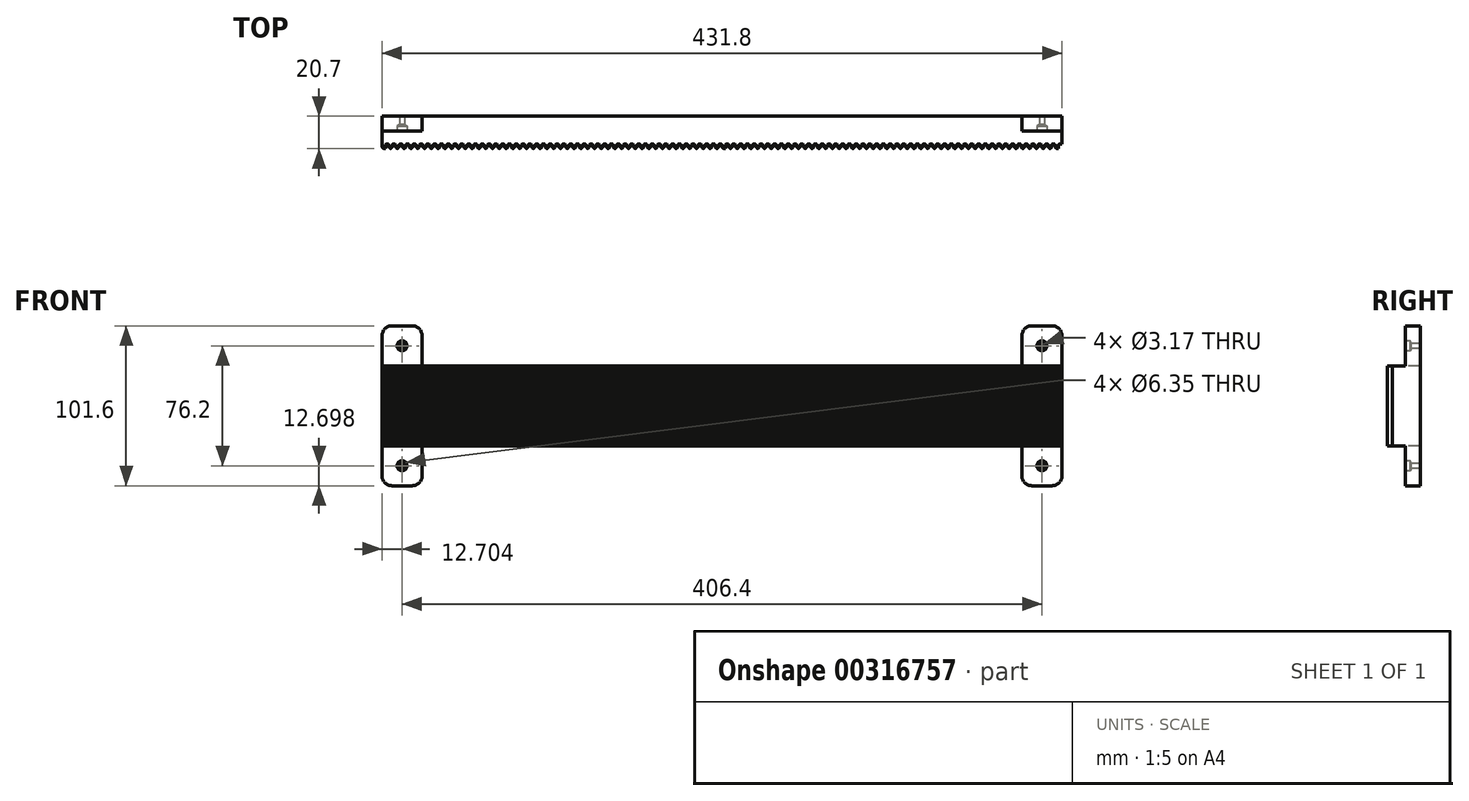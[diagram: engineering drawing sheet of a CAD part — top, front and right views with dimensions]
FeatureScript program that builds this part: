
annotation { "Feature Type Name" : "Feature", "Feature Type Description" : "" }
export const myFeature = defineFeature(function(context is Context, id is Id, definition is map)
    precondition{}
    {
        {
            var Q0;
            Q0=qCreatedBy(makeId("Front.planeOp"),FACE);
            var sketch = newSketch(context, id + "F0", { "sketchPlane" : qUnion([Q0])});
            skLineSegment(sketch, "E0.bottom", {"start": v(-210.38, -43.82) * mm, "end": v(221.42, -43.82) * mm});
            skLineSegment(sketch, "E0.top", {"start": v(-210.38, -94.62) * mm, "end": v(221.42, -94.62) * mm});
            skLineSegment(sketch, "E0.left", {"start": v(-210.38, -43.82) * mm, "end": v(-210.38, -94.62) * mm});
            skLineSegment(sketch, "E0.right", {"start": v(221.42, -43.82) * mm, "end": v(221.42, -94.62) * mm});
            skSolve(sketch);
        }
        {
            var Q0;
            Q0=makeQuery(id+"F0.imprint","IMPRINT",FACE,{"disambiguationData":[TD([[makeQuery(id+"F0.imprint","IMPRINT",EDGE,{"derivedFrom":sQuery(id+"F0.wireOp",EDGE,"E0.bottom")}),-1.0]])]});
            extrude(context, id + "F1", {"entities" : qUnion([Q0]), "depth" : 20.7 * mm});
        }
        {
            var Q0;
            Q0=makeQuery(id+"F1.opExtrude","SWEPT_FACE",FACE,{"disambiguationData":[OSD([sQuery(id+"F0.wireOp",EDGE,"E0.top")])]});
            var sketch = newSketch(context, id + "F2", { "sketchPlane" : qUnion([Q0])});
            skLineSegment(sketch, "E1.bottom", {"start": v(-210.38, 0) * mm, "end": v(-184.98, 0) * mm});
            skLineSegment(sketch, "E1.top", {"start": v(-210.38, 9.53) * mm, "end": v(-184.98, 9.53) * mm});
            skLineSegment(sketch, "E1.left", {"start": v(-210.38, 0) * mm, "end": v(-210.38, 9.53) * mm});
            skLineSegment(sketch, "E1.right", {"start": v(-184.98, 0) * mm, "end": v(-184.98, 9.53) * mm});
            skLineSegment(sketch, "E2.bottom", {"start": v(221.42, 0) * mm, "end": v(196.02, 0) * mm});
            skLineSegment(sketch, "E2.top", {"start": v(221.42, 9.52) * mm, "end": v(196.02, 9.52) * mm});
            skLineSegment(sketch, "E2.left", {"start": v(221.42, 0) * mm, "end": v(221.42, 9.52) * mm});
            skLineSegment(sketch, "E2.right", {"start": v(196.02, 0) * mm, "end": v(196.02, 9.52) * mm});
            skSolve(sketch);
        }
        {
            var Q0;
            Q0=makeQuery(id+"F1.opExtrude","SWEPT_FACE",FACE,{"disambiguationData":[OSD([sQuery(id+"F0.wireOp",EDGE,"E0.bottom")])]});
            var sketch = newSketch(context, id + "F3", { "sketchPlane" : qUnion([Q0])});
            skLineSegment(sketch, "E3.bottom", {"start": v(-210.38, 0) * mm, "end": v(-184.98, 0) * mm});
            skLineSegment(sketch, "E3.top", {"start": v(-210.38, -9.52) * mm, "end": v(-184.98, -9.52) * mm});
            skLineSegment(sketch, "E3.left", {"start": v(-210.38, 0) * mm, "end": v(-210.38, -9.52) * mm});
            skLineSegment(sketch, "E3.right", {"start": v(-184.98, 0) * mm, "end": v(-184.98, -9.52) * mm});
            skLineSegment(sketch, "E4.bottom", {"start": v(221.42, 0) * mm, "end": v(196.02, 0) * mm});
            skLineSegment(sketch, "E4.top", {"start": v(221.42, -9.53) * mm, "end": v(196.02, -9.53) * mm});
            skLineSegment(sketch, "E4.left", {"start": v(221.42, 0) * mm, "end": v(221.42, -9.53) * mm});
            skLineSegment(sketch, "E4.right", {"start": v(196.02, 0) * mm, "end": v(196.02, -9.53) * mm});
            skSolve(sketch);
        }
        {
            var Q0;
            Q0=makeQuery(id+"F2.imprint","IMPRINT",FACE,{"disambiguationData":[TD([[makeQuery(id+"F2.imprint","IMPRINT",EDGE,{"derivedFrom":sQuery(id+"F2.wireOp",EDGE,"E1.bottom")}),1.0]])]});
            var Q1;
            Q1=makeQuery(id+"F2.imprint","IMPRINT",FACE,{"disambiguationData":[TD([[makeQuery(id+"F2.imprint","IMPRINT",EDGE,{"derivedFrom":sQuery(id+"F2.wireOp",EDGE,"E2.bottom")}),1.0]])]});
            extrude(context, id + "F4", {"entities" : qUnion([Q0, Q1]), "operationType" : NewBodyOperationType.ADD, "depth" : 25.4 * mm});
        }
        {
            var Q0;
            Q0=makeQuery(id+"F3.imprint","IMPRINT",FACE,{"disambiguationData":[TD([[makeQuery(id+"F3.imprint","IMPRINT",EDGE,{"derivedFrom":sQuery(id+"F3.wireOp",EDGE,"E3.bottom")}),-1.0]])]});
            var Q1;
            Q1=makeQuery(id+"F3.imprint","IMPRINT",FACE,{"disambiguationData":[TD([[makeQuery(id+"F3.imprint","IMPRINT",EDGE,{"derivedFrom":sQuery(id+"F3.wireOp",EDGE,"E4.bottom")}),-1.0]])]});
            extrude(context, id + "F5", {"entities" : qUnion([Q0, Q1]), "operationType" : NewBodyOperationType.ADD, "depth" : 25.4 * mm});
        }
        {
            var Q0;
            Q0=makeQuery(id+"F5.opExtrude","CAP_EDGE",EDGE,{"disambiguationData":[OSD([sQuery(id+"F3.wireOp",EDGE,"E3.left")])],"isStart":false});
            var Q1;
            Q1=makeQuery(id+"F5.opExtrude","CAP_EDGE",EDGE,{"disambiguationData":[OSD([sQuery(id+"F3.wireOp",EDGE,"E3.right")])],"isStart":false});
            var Q2;
            Q2=makeQuery(id+"F5.opExtrude","CAP_EDGE",EDGE,{"disambiguationData":[OSD([sQuery(id+"F3.wireOp",EDGE,"E4.left")])],"isStart":false});
            var Q3;
            Q3=makeQuery(id+"F5.opExtrude","CAP_EDGE",EDGE,{"disambiguationData":[OSD([sQuery(id+"F3.wireOp",EDGE,"E4.right")])],"isStart":false});
            var Q4;
            Q4=makeQuery(id+"F4.opExtrude","CAP_EDGE",EDGE,{"disambiguationData":[OSD([sQuery(id+"F2.wireOp",EDGE,"E2.left")])],"isStart":false});
            var Q5;
            Q5=makeQuery(id+"F4.opExtrude","CAP_EDGE",EDGE,{"disambiguationData":[OSD([sQuery(id+"F2.wireOp",EDGE,"E2.right")])],"isStart":false});
            var Q6;
            Q6=makeQuery(id+"F4.opExtrude","CAP_EDGE",EDGE,{"disambiguationData":[OSD([sQuery(id+"F2.wireOp",EDGE,"E1.left")])],"isStart":false});
            var Q7;
            Q7=makeQuery(id+"F4.opExtrude","CAP_EDGE",EDGE,{"disambiguationData":[OSD([sQuery(id+"F2.wireOp",EDGE,"E1.right")])],"isStart":false});
            fillet(context, id + "F6", {"entities" : qUnion([Q0, Q1, Q2, Q3, Q4, Q5, Q6, Q7]), "radius" : 6.35 * mm, "tangentPropagation" : true, "allowEdgeOverflow" : false});
        }
        {
            var Q0;
            Q0=makeQuery(id+"F4.opExtrude","SWEPT_FACE",FACE,{"disambiguationData":[OSD([sQuery(id+"F2.wireOp",EDGE,"E1.top")])]});
            var sketch = newSketch(context, id + "F7", { "sketchPlane" : qUnion([Q0])});
            skPoint(sketch, "E5", {"position": v(-197.68, -107.32) * mm});
            skPoint(sketch, "E5.positionSnap0", {"position": v(-197.68, -94.62) * mm});
            skPoint(sketch, "E6", {"position": v(-197.68, -31.12) * mm});
            skSolve(sketch);
        }
        {
            var Q0;
            Q0=sQuery(id+"F7.wireOp",VERTEX,"E6");
            var Q1;
            Q1=sQuery(id+"F7.wireOp",VERTEX,"E5");
            var Q2;
            Q2=makeQuery(id+"F1.opExtrude","SWEPT_BODY",BODY,{"disambiguationData":[OSD([sQuery(id+"F0.wireOp",EDGE,"E0.bottom"),sQuery(id+"F0.wireOp",EDGE,"E0.top"),sQuery(id+"F0.wireOp",EDGE,"E0.left"),sQuery(id+"F0.wireOp",EDGE,"E0.right")])]});
            hole(context, id + "F8", {"style" : HoleStyle.SIMPLE, "endStyle" : HoleEndStyle.THROUGH, "holeDiameter" : 3.17 * mm, "tappedDepth" : 12.7 * mm, "tapClearance" : 3, "locations" : qUnion([Q0, Q1]), "scope" : qUnion([Q2])});
        }
        {
            var Q0;
            Q0=sQuery(id+"F7.wireOp",VERTEX,"E6");
            var Q1;
            Q1=sQuery(id+"F7.wireOp",VERTEX,"E5");
            var Q2;
            Q2=makeQuery(id+"F1.opExtrude","SWEPT_BODY",BODY,{"disambiguationData":[OSD([sQuery(id+"F0.wireOp",EDGE,"E0.bottom"),sQuery(id+"F0.wireOp",EDGE,"E0.top"),sQuery(id+"F0.wireOp",EDGE,"E0.left"),sQuery(id+"F0.wireOp",EDGE,"E0.right")])]});
            hole(context, id + "F9", {"style" : HoleStyle.SIMPLE, "endStyle" : HoleEndStyle.BLIND, "holeDiameter" : 6.35 * mm, "holeDepth" : 3.17 * mm, "tappedDepth" : 12.7 * mm, "tapClearance" : 3, "locations" : qUnion([Q0, Q1]), "scope" : qUnion([Q2])});
        }
        {
            var Q0;
            Q0=makeQuery(id+"F4.opExtrude","SWEPT_FACE",FACE,{"disambiguationData":[OSD([sQuery(id+"F2.wireOp",EDGE,"E2.top")])]});
            var sketch = newSketch(context, id + "F10", { "sketchPlane" : qUnion([Q0])});
            skPoint(sketch, "E7", {"position": v(208.72, -31.12) * mm});
            skPoint(sketch, "E8", {"position": v(208.72, -107.32) * mm});
            skSolve(sketch);
        }
        {
            var Q0;
            Q0=sQuery(id+"F10.wireOp",VERTEX,"E7");
            var Q1;
            Q1=sQuery(id+"F10.wireOp",VERTEX,"E8");
            var Q2;
            Q2=makeQuery(id+"F1.opExtrude","SWEPT_BODY",BODY,{"disambiguationData":[OSD([sQuery(id+"F0.wireOp",EDGE,"E0.bottom"),sQuery(id+"F0.wireOp",EDGE,"E0.top"),sQuery(id+"F0.wireOp",EDGE,"E0.left"),sQuery(id+"F0.wireOp",EDGE,"E0.right")])]});
            hole(context, id + "F11", {"style" : HoleStyle.SIMPLE, "endStyle" : HoleEndStyle.BLIND, "holeDiameter" : 6.35 * mm, "holeDepth" : 3.17 * mm, "tappedDepth" : 12.7 * mm, "tapClearance" : 3, "locations" : qUnion([Q0, Q1]), "scope" : qUnion([Q2])});
        }
        {
            var Q0;
            Q0=sQuery(id+"F10.wireOp",VERTEX,"E7");
            var Q1;
            Q1=sQuery(id+"F10.wireOp",VERTEX,"E8");
            var Q2;
            Q2=makeQuery(id+"F1.opExtrude","SWEPT_BODY",BODY,{"disambiguationData":[OSD([sQuery(id+"F0.wireOp",EDGE,"E0.bottom"),sQuery(id+"F0.wireOp",EDGE,"E0.top"),sQuery(id+"F0.wireOp",EDGE,"E0.left"),sQuery(id+"F0.wireOp",EDGE,"E0.right")])]});
            hole(context, id + "F12", {"style" : HoleStyle.SIMPLE, "endStyle" : HoleEndStyle.THROUGH, "holeDiameter" : 3.17 * mm, "tappedDepth" : 12.7 * mm, "tapClearance" : 3, "locations" : qUnion([Q0, Q1]), "scope" : qUnion([Q2])});
        }
        {
            var Q0;
            Q0=makeQuery(id+"F1.opExtrude","SWEPT_FACE",FACE,{"disambiguationData":[OSD([sQuery(id+"F0.wireOp",EDGE,"E0.top")])]});
            var sketch = newSketch(context, id + "F13", { "sketchPlane" : qUnion([Q0])});
            skLineSegment(sketch, "E9.bottom", {"start": v(-208.22, 20.7) * mm, "end": v(-206.03, 20.7) * mm});
            skLineSegment(sketch, "E9.top", {"start": v(-208.22, 17.65) * mm, "end": v(-206.03, 17.65) * mm});
            skLineSegment(sketch, "E9.left", {"start": v(-208.22, 20.7) * mm, "end": v(-208.22, 17.65) * mm});
            skLineSegment(sketch, "E9.right", {"start": v(-206.03, 20.7) * mm, "end": v(-206.03, 17.65) * mm});
            skLineSegment(sketch, "E10.1.0.0", {"start": v(-206.06, 20.7) * mm, "end": v(-206.06, 17.65) * mm});
            skLineSegment(sketch, "E10.1.0.1", {"start": v(-206.06, 20.7) * mm, "end": v(-203.87, 20.7) * mm});
            skLineSegment(sketch, "E10.1.0.2", {"start": v(-203.87, 20.7) * mm, "end": v(-203.87, 17.65) * mm});
            skLineSegment(sketch, "E10.1.0.3", {"start": v(-206.06, 17.65) * mm, "end": v(-203.87, 17.65) * mm});
            skLineSegment(sketch, "E10.2.0.0", {"start": v(-203.9, 20.7) * mm, "end": v(-203.9, 17.65) * mm});
            skLineSegment(sketch, "E10.2.0.1", {"start": v(-203.9, 20.7) * mm, "end": v(-201.71, 20.7) * mm});
            skLineSegment(sketch, "E10.2.0.2", {"start": v(-201.71, 20.7) * mm, "end": v(-201.71, 17.65) * mm});
            skLineSegment(sketch, "E10.2.0.3", {"start": v(-203.9, 17.65) * mm, "end": v(-201.71, 17.65) * mm});
            skLineSegment(sketch, "E10.3.0.0", {"start": v(-201.74, 20.7) * mm, "end": v(-201.74, 17.65) * mm});
            skLineSegment(sketch, "E10.3.0.1", {"start": v(-201.74, 20.7) * mm, "end": v(-199.56, 20.7) * mm});
            skLineSegment(sketch, "E10.3.0.2", {"start": v(-199.56, 20.7) * mm, "end": v(-199.56, 17.65) * mm});
            skLineSegment(sketch, "E10.3.0.3", {"start": v(-201.74, 17.65) * mm, "end": v(-199.56, 17.65) * mm});
            skLineSegment(sketch, "E10.4.0.0", {"start": v(-199.58, 20.7) * mm, "end": v(-199.58, 17.65) * mm});
            skLineSegment(sketch, "E10.4.0.1", {"start": v(-199.58, 20.7) * mm, "end": v(-197.4, 20.7) * mm});
            skLineSegment(sketch, "E10.4.0.2", {"start": v(-197.4, 20.7) * mm, "end": v(-197.4, 17.65) * mm});
            skLineSegment(sketch, "E10.4.0.3", {"start": v(-199.58, 17.65) * mm, "end": v(-197.4, 17.65) * mm});
            skLineSegment(sketch, "E10.5.0.0", {"start": v(-197.42, 20.7) * mm, "end": v(-197.42, 17.65) * mm});
            skLineSegment(sketch, "E10.5.0.1", {"start": v(-197.42, 20.7) * mm, "end": v(-195.24, 20.7) * mm});
            skLineSegment(sketch, "E10.5.0.2", {"start": v(-195.24, 20.7) * mm, "end": v(-195.24, 17.65) * mm});
            skLineSegment(sketch, "E10.5.0.3", {"start": v(-197.42, 17.65) * mm, "end": v(-195.24, 17.65) * mm});
            skLineSegment(sketch, "E10.6.0.0", {"start": v(-195.26, 20.7) * mm, "end": v(-195.26, 17.65) * mm});
            skLineSegment(sketch, "E10.6.0.1", {"start": v(-195.26, 20.7) * mm, "end": v(-193.08, 20.7) * mm});
            skLineSegment(sketch, "E10.6.0.2", {"start": v(-193.08, 20.7) * mm, "end": v(-193.08, 17.65) * mm});
            skLineSegment(sketch, "E10.6.0.3", {"start": v(-195.26, 17.65) * mm, "end": v(-193.08, 17.65) * mm});
            skLineSegment(sketch, "E10.7.0.0", {"start": v(-193.1, 20.7) * mm, "end": v(-193.1, 17.65) * mm});
            skLineSegment(sketch, "E10.7.0.1", {"start": v(-193.1, 20.7) * mm, "end": v(-190.92, 20.7) * mm});
            skLineSegment(sketch, "E10.7.0.2", {"start": v(-190.92, 20.7) * mm, "end": v(-190.92, 17.65) * mm});
            skLineSegment(sketch, "E10.7.0.3", {"start": v(-193.1, 17.65) * mm, "end": v(-190.92, 17.65) * mm});
            skLineSegment(sketch, "E10.8.0.0", {"start": v(-190.94, 20.7) * mm, "end": v(-190.94, 17.65) * mm});
            skLineSegment(sketch, "E10.8.0.1", {"start": v(-190.94, 20.7) * mm, "end": v(-188.76, 20.7) * mm});
            skLineSegment(sketch, "E10.8.0.2", {"start": v(-188.76, 20.7) * mm, "end": v(-188.76, 17.65) * mm});
            skLineSegment(sketch, "E10.8.0.3", {"start": v(-190.94, 17.65) * mm, "end": v(-188.76, 17.65) * mm});
            skLineSegment(sketch, "E10.9.0.0", {"start": v(-188.79, 20.7) * mm, "end": v(-188.79, 17.65) * mm});
            skLineSegment(sketch, "E10.9.0.1", {"start": v(-188.79, 20.7) * mm, "end": v(-186.6, 20.7) * mm});
            skLineSegment(sketch, "E10.9.0.2", {"start": v(-186.6, 20.7) * mm, "end": v(-186.6, 17.65) * mm});
            skLineSegment(sketch, "E10.9.0.3", {"start": v(-188.79, 17.65) * mm, "end": v(-186.6, 17.65) * mm});
            skLineSegment(sketch, "E10.10.0.0", {"start": v(-186.63, 20.7) * mm, "end": v(-186.63, 17.65) * mm});
            skLineSegment(sketch, "E10.10.0.1", {"start": v(-186.63, 20.7) * mm, "end": v(-184.44, 20.7) * mm});
            skLineSegment(sketch, "E10.10.0.2", {"start": v(-184.44, 20.7) * mm, "end": v(-184.44, 17.65) * mm});
            skLineSegment(sketch, "E10.10.0.3", {"start": v(-186.63, 17.65) * mm, "end": v(-184.44, 17.65) * mm});
            skLineSegment(sketch, "E10.11.0.0", {"start": v(-184.47, 20.7) * mm, "end": v(-184.47, 17.65) * mm});
            skLineSegment(sketch, "E10.11.0.1", {"start": v(-184.47, 20.7) * mm, "end": v(-182.28, 20.7) * mm});
            skLineSegment(sketch, "E10.11.0.2", {"start": v(-182.28, 20.7) * mm, "end": v(-182.28, 17.65) * mm});
            skLineSegment(sketch, "E10.11.0.3", {"start": v(-184.47, 17.65) * mm, "end": v(-182.28, 17.65) * mm});
            skLineSegment(sketch, "E10.12.0.0", {"start": v(-182.3, 20.7) * mm, "end": v(-182.3, 17.65) * mm});
            skLineSegment(sketch, "E10.12.0.1", {"start": v(-182.3, 20.7) * mm, "end": v(-180.12, 20.7) * mm});
            skLineSegment(sketch, "E10.12.0.2", {"start": v(-180.12, 20.7) * mm, "end": v(-180.12, 17.65) * mm});
            skLineSegment(sketch, "E10.12.0.3", {"start": v(-182.3, 17.65) * mm, "end": v(-180.12, 17.65) * mm});
            skLineSegment(sketch, "E10.13.0.0", {"start": v(-180.15, 20.7) * mm, "end": v(-180.15, 17.65) * mm});
            skLineSegment(sketch, "E10.13.0.1", {"start": v(-180.15, 20.7) * mm, "end": v(-177.97, 20.7) * mm});
            skLineSegment(sketch, "E10.13.0.2", {"start": v(-177.97, 20.7) * mm, "end": v(-177.97, 17.65) * mm});
            skLineSegment(sketch, "E10.13.0.3", {"start": v(-180.15, 17.65) * mm, "end": v(-177.97, 17.65) * mm});
            skLineSegment(sketch, "E10.14.0.0", {"start": v(-178, 20.7) * mm, "end": v(-178, 17.65) * mm});
            skLineSegment(sketch, "E10.14.0.1", {"start": v(-178, 20.7) * mm, "end": v(-175.8, 20.7) * mm});
            skLineSegment(sketch, "E10.14.0.2", {"start": v(-175.8, 20.7) * mm, "end": v(-175.8, 17.65) * mm});
            skLineSegment(sketch, "E10.14.0.3", {"start": v(-178, 17.65) * mm, "end": v(-175.8, 17.65) * mm});
            skLineSegment(sketch, "E10.15.0.0", {"start": v(-175.83, 20.7) * mm, "end": v(-175.83, 17.65) * mm});
            skLineSegment(sketch, "E10.15.0.1", {"start": v(-175.83, 20.7) * mm, "end": v(-173.65, 20.7) * mm});
            skLineSegment(sketch, "E10.15.0.2", {"start": v(-173.65, 20.7) * mm, "end": v(-173.65, 17.65) * mm});
            skLineSegment(sketch, "E10.15.0.3", {"start": v(-175.83, 17.65) * mm, "end": v(-173.65, 17.65) * mm});
            skLineSegment(sketch, "E10.16.0.0", {"start": v(-173.67, 20.7) * mm, "end": v(-173.67, 17.65) * mm});
            skLineSegment(sketch, "E10.16.0.1", {"start": v(-173.67, 20.7) * mm, "end": v(-171.49, 20.7) * mm});
            skLineSegment(sketch, "E10.16.0.2", {"start": v(-171.49, 20.7) * mm, "end": v(-171.49, 17.65) * mm});
            skLineSegment(sketch, "E10.16.0.3", {"start": v(-173.67, 17.65) * mm, "end": v(-171.49, 17.65) * mm});
            skLineSegment(sketch, "E10.17.0.0", {"start": v(-171.51, 20.7) * mm, "end": v(-171.51, 17.65) * mm});
            skLineSegment(sketch, "E10.17.0.1", {"start": v(-171.51, 20.7) * mm, "end": v(-169.33, 20.7) * mm});
            skLineSegment(sketch, "E10.17.0.2", {"start": v(-169.33, 20.7) * mm, "end": v(-169.33, 17.65) * mm});
            skLineSegment(sketch, "E10.17.0.3", {"start": v(-171.51, 17.65) * mm, "end": v(-169.33, 17.65) * mm});
            skLineSegment(sketch, "E10.18.0.0", {"start": v(-169.35, 20.7) * mm, "end": v(-169.35, 17.65) * mm});
            skLineSegment(sketch, "E10.18.0.1", {"start": v(-169.35, 20.7) * mm, "end": v(-167.17, 20.7) * mm});
            skLineSegment(sketch, "E10.18.0.2", {"start": v(-167.17, 20.7) * mm, "end": v(-167.17, 17.65) * mm});
            skLineSegment(sketch, "E10.18.0.3", {"start": v(-169.35, 17.65) * mm, "end": v(-167.17, 17.65) * mm});
            skLineSegment(sketch, "E10.19.0.0", {"start": v(-167.2, 20.7) * mm, "end": v(-167.2, 17.65) * mm});
            skLineSegment(sketch, "E10.19.0.1", {"start": v(-167.2, 20.7) * mm, "end": v(-165.01, 20.7) * mm});
            skLineSegment(sketch, "E10.19.0.2", {"start": v(-165.01, 20.7) * mm, "end": v(-165.01, 17.65) * mm});
            skLineSegment(sketch, "E10.19.0.3", {"start": v(-167.2, 17.65) * mm, "end": v(-165.01, 17.65) * mm});
            skLineSegment(sketch, "E10.20.0.0", {"start": v(-165.04, 20.7) * mm, "end": v(-165.04, 17.65) * mm});
            skLineSegment(sketch, "E10.20.0.1", {"start": v(-165.04, 20.7) * mm, "end": v(-162.85, 20.7) * mm});
            skLineSegment(sketch, "E10.20.0.2", {"start": v(-162.85, 20.7) * mm, "end": v(-162.85, 17.65) * mm});
            skLineSegment(sketch, "E10.20.0.3", {"start": v(-165.04, 17.65) * mm, "end": v(-162.85, 17.65) * mm});
            skLineSegment(sketch, "E10.21.0.0", {"start": v(-162.88, 20.7) * mm, "end": v(-162.88, 17.65) * mm});
            skLineSegment(sketch, "E10.21.0.1", {"start": v(-162.88, 20.7) * mm, "end": v(-160.7, 20.7) * mm});
            skLineSegment(sketch, "E10.21.0.2", {"start": v(-160.7, 20.7) * mm, "end": v(-160.7, 17.65) * mm});
            skLineSegment(sketch, "E10.21.0.3", {"start": v(-162.88, 17.65) * mm, "end": v(-160.7, 17.65) * mm});
            skLineSegment(sketch, "E10.22.0.0", {"start": v(-160.72, 20.7) * mm, "end": v(-160.72, 17.65) * mm});
            skLineSegment(sketch, "E10.22.0.1", {"start": v(-160.72, 20.7) * mm, "end": v(-158.53, 20.7) * mm});
            skLineSegment(sketch, "E10.22.0.2", {"start": v(-158.53, 20.7) * mm, "end": v(-158.53, 17.65) * mm});
            skLineSegment(sketch, "E10.22.0.3", {"start": v(-160.72, 17.65) * mm, "end": v(-158.53, 17.65) * mm});
            skLineSegment(sketch, "E10.23.0.0", {"start": v(-158.56, 20.7) * mm, "end": v(-158.56, 17.65) * mm});
            skLineSegment(sketch, "E10.23.0.1", {"start": v(-158.56, 20.7) * mm, "end": v(-156.38, 20.7) * mm});
            skLineSegment(sketch, "E10.23.0.2", {"start": v(-156.38, 20.7) * mm, "end": v(-156.38, 17.65) * mm});
            skLineSegment(sketch, "E10.23.0.3", {"start": v(-158.56, 17.65) * mm, "end": v(-156.38, 17.65) * mm});
            skLineSegment(sketch, "E10.24.0.0", {"start": v(-156.4, 20.7) * mm, "end": v(-156.4, 17.65) * mm});
            skLineSegment(sketch, "E10.24.0.1", {"start": v(-156.4, 20.7) * mm, "end": v(-154.22, 20.7) * mm});
            skLineSegment(sketch, "E10.24.0.2", {"start": v(-154.22, 20.7) * mm, "end": v(-154.22, 17.65) * mm});
            skLineSegment(sketch, "E10.24.0.3", {"start": v(-156.4, 17.65) * mm, "end": v(-154.22, 17.65) * mm});
            skLineSegment(sketch, "E10.25.0.0", {"start": v(-154.24, 20.7) * mm, "end": v(-154.24, 17.65) * mm});
            skLineSegment(sketch, "E10.25.0.1", {"start": v(-154.24, 20.7) * mm, "end": v(-152.06, 20.7) * mm});
            skLineSegment(sketch, "E10.25.0.2", {"start": v(-152.06, 20.7) * mm, "end": v(-152.06, 17.65) * mm});
            skLineSegment(sketch, "E10.25.0.3", {"start": v(-154.24, 17.65) * mm, "end": v(-152.06, 17.65) * mm});
            skLineSegment(sketch, "E10.26.0.0", {"start": v(-152.08, 20.7) * mm, "end": v(-152.08, 17.65) * mm});
            skLineSegment(sketch, "E10.26.0.1", {"start": v(-152.08, 20.7) * mm, "end": v(-149.9, 20.7) * mm});
            skLineSegment(sketch, "E10.26.0.2", {"start": v(-149.9, 20.7) * mm, "end": v(-149.9, 17.65) * mm});
            skLineSegment(sketch, "E10.26.0.3", {"start": v(-152.08, 17.65) * mm, "end": v(-149.9, 17.65) * mm});
            skLineSegment(sketch, "E10.27.0.0", {"start": v(-149.92, 20.7) * mm, "end": v(-149.92, 17.65) * mm});
            skLineSegment(sketch, "E10.27.0.1", {"start": v(-149.92, 20.7) * mm, "end": v(-147.74, 20.7) * mm});
            skLineSegment(sketch, "E10.27.0.2", {"start": v(-147.74, 20.7) * mm, "end": v(-147.74, 17.65) * mm});
            skLineSegment(sketch, "E10.27.0.3", {"start": v(-149.92, 17.65) * mm, "end": v(-147.74, 17.65) * mm});
            skLineSegment(sketch, "E10.28.0.0", {"start": v(-147.76, 20.7) * mm, "end": v(-147.76, 17.65) * mm});
            skLineSegment(sketch, "E10.28.0.1", {"start": v(-147.76, 20.7) * mm, "end": v(-145.58, 20.7) * mm});
            skLineSegment(sketch, "E10.28.0.2", {"start": v(-145.58, 20.7) * mm, "end": v(-145.58, 17.65) * mm});
            skLineSegment(sketch, "E10.28.0.3", {"start": v(-147.76, 17.65) * mm, "end": v(-145.58, 17.65) * mm});
            skLineSegment(sketch, "E10.29.0.0", {"start": v(-145.6, 20.7) * mm, "end": v(-145.6, 17.65) * mm});
            skLineSegment(sketch, "E10.29.0.1", {"start": v(-145.6, 20.7) * mm, "end": v(-143.42, 20.7) * mm});
            skLineSegment(sketch, "E10.29.0.2", {"start": v(-143.42, 20.7) * mm, "end": v(-143.42, 17.65) * mm});
            skLineSegment(sketch, "E10.29.0.3", {"start": v(-145.6, 17.65) * mm, "end": v(-143.42, 17.65) * mm});
            skLineSegment(sketch, "E10.30.0.0", {"start": v(-143.45, 20.7) * mm, "end": v(-143.45, 17.65) * mm});
            skLineSegment(sketch, "E10.30.0.1", {"start": v(-143.45, 20.7) * mm, "end": v(-141.26, 20.7) * mm});
            skLineSegment(sketch, "E10.30.0.2", {"start": v(-141.26, 20.7) * mm, "end": v(-141.26, 17.65) * mm});
            skLineSegment(sketch, "E10.30.0.3", {"start": v(-143.45, 17.65) * mm, "end": v(-141.26, 17.65) * mm});
            skLineSegment(sketch, "E10.31.0.0", {"start": v(-141.29, 20.7) * mm, "end": v(-141.29, 17.65) * mm});
            skLineSegment(sketch, "E10.31.0.1", {"start": v(-141.29, 20.7) * mm, "end": v(-139.1, 20.7) * mm});
            skLineSegment(sketch, "E10.31.0.2", {"start": v(-139.1, 20.7) * mm, "end": v(-139.1, 17.65) * mm});
            skLineSegment(sketch, "E10.31.0.3", {"start": v(-141.29, 17.65) * mm, "end": v(-139.1, 17.65) * mm});
            skLineSegment(sketch, "E10.32.0.0", {"start": v(-139.13, 20.7) * mm, "end": v(-139.13, 17.65) * mm});
            skLineSegment(sketch, "E10.32.0.1", {"start": v(-139.13, 20.7) * mm, "end": v(-136.94, 20.7) * mm});
            skLineSegment(sketch, "E10.32.0.2", {"start": v(-136.94, 20.7) * mm, "end": v(-136.94, 17.65) * mm});
            skLineSegment(sketch, "E10.32.0.3", {"start": v(-139.13, 17.65) * mm, "end": v(-136.94, 17.65) * mm});
            skLineSegment(sketch, "E10.33.0.0", {"start": v(-136.97, 20.7) * mm, "end": v(-136.97, 17.65) * mm});
            skLineSegment(sketch, "E10.33.0.1", {"start": v(-136.97, 20.7) * mm, "end": v(-134.79, 20.7) * mm});
            skLineSegment(sketch, "E10.33.0.2", {"start": v(-134.79, 20.7) * mm, "end": v(-134.79, 17.65) * mm});
            skLineSegment(sketch, "E10.33.0.3", {"start": v(-136.97, 17.65) * mm, "end": v(-134.79, 17.65) * mm});
            skLineSegment(sketch, "E10.34.0.0", {"start": v(-134.81, 20.7) * mm, "end": v(-134.81, 17.65) * mm});
            skLineSegment(sketch, "E10.34.0.1", {"start": v(-134.81, 20.7) * mm, "end": v(-132.63, 20.7) * mm});
            skLineSegment(sketch, "E10.34.0.2", {"start": v(-132.63, 20.7) * mm, "end": v(-132.63, 17.65) * mm});
            skLineSegment(sketch, "E10.34.0.3", {"start": v(-134.81, 17.65) * mm, "end": v(-132.63, 17.65) * mm});
            skLineSegment(sketch, "E10.35.0.0", {"start": v(-132.65, 20.7) * mm, "end": v(-132.65, 17.65) * mm});
            skLineSegment(sketch, "E10.35.0.1", {"start": v(-132.65, 20.7) * mm, "end": v(-130.47, 20.7) * mm});
            skLineSegment(sketch, "E10.35.0.2", {"start": v(-130.47, 20.7) * mm, "end": v(-130.47, 17.65) * mm});
            skLineSegment(sketch, "E10.35.0.3", {"start": v(-132.65, 17.65) * mm, "end": v(-130.47, 17.65) * mm});
            skLineSegment(sketch, "E10.36.0.0", {"start": v(-130.5, 20.7) * mm, "end": v(-130.5, 17.65) * mm});
            skLineSegment(sketch, "E10.36.0.1", {"start": v(-130.5, 20.7) * mm, "end": v(-128.3, 20.7) * mm});
            skLineSegment(sketch, "E10.36.0.2", {"start": v(-128.3, 20.7) * mm, "end": v(-128.3, 17.65) * mm});
            skLineSegment(sketch, "E10.36.0.3", {"start": v(-130.5, 17.65) * mm, "end": v(-128.3, 17.65) * mm});
            skLineSegment(sketch, "E10.37.0.0", {"start": v(-128.33, 20.7) * mm, "end": v(-128.33, 17.65) * mm});
            skLineSegment(sketch, "E10.37.0.1", {"start": v(-128.33, 20.7) * mm, "end": v(-126.15, 20.7) * mm});
            skLineSegment(sketch, "E10.37.0.2", {"start": v(-126.15, 20.7) * mm, "end": v(-126.15, 17.65) * mm});
            skLineSegment(sketch, "E10.37.0.3", {"start": v(-128.33, 17.65) * mm, "end": v(-126.15, 17.65) * mm});
            skLineSegment(sketch, "E10.38.0.0", {"start": v(-126.17, 20.7) * mm, "end": v(-126.17, 17.65) * mm});
            skLineSegment(sketch, "E10.38.0.1", {"start": v(-126.17, 20.7) * mm, "end": v(-124, 20.7) * mm});
            skLineSegment(sketch, "E10.38.0.2", {"start": v(-124, 20.7) * mm, "end": v(-124, 17.65) * mm});
            skLineSegment(sketch, "E10.38.0.3", {"start": v(-126.17, 17.65) * mm, "end": v(-124, 17.65) * mm});
            skLineSegment(sketch, "E10.39.0.0", {"start": v(-124.02, 20.7) * mm, "end": v(-124.02, 17.65) * mm});
            skLineSegment(sketch, "E10.39.0.1", {"start": v(-124.02, 20.7) * mm, "end": v(-121.83, 20.7) * mm});
            skLineSegment(sketch, "E10.39.0.2", {"start": v(-121.83, 20.7) * mm, "end": v(-121.83, 17.65) * mm});
            skLineSegment(sketch, "E10.39.0.3", {"start": v(-124.02, 17.65) * mm, "end": v(-121.83, 17.65) * mm});
            skLineSegment(sketch, "E10.40.0.0", {"start": v(-121.86, 20.7) * mm, "end": v(-121.86, 17.65) * mm});
            skLineSegment(sketch, "E10.40.0.1", {"start": v(-121.86, 20.7) * mm, "end": v(-119.67, 20.7) * mm});
            skLineSegment(sketch, "E10.40.0.2", {"start": v(-119.67, 20.7) * mm, "end": v(-119.67, 17.65) * mm});
            skLineSegment(sketch, "E10.40.0.3", {"start": v(-121.86, 17.65) * mm, "end": v(-119.67, 17.65) * mm});
            skLineSegment(sketch, "E10.41.0.0", {"start": v(-119.7, 20.7) * mm, "end": v(-119.7, 17.65) * mm});
            skLineSegment(sketch, "E10.41.0.1", {"start": v(-119.7, 20.7) * mm, "end": v(-117.51, 20.7) * mm});
            skLineSegment(sketch, "E10.41.0.2", {"start": v(-117.51, 20.7) * mm, "end": v(-117.51, 17.65) * mm});
            skLineSegment(sketch, "E10.41.0.3", {"start": v(-119.7, 17.65) * mm, "end": v(-117.51, 17.65) * mm});
            skLineSegment(sketch, "E10.42.0.0", {"start": v(-117.54, 20.7) * mm, "end": v(-117.54, 17.65) * mm});
            skLineSegment(sketch, "E10.42.0.1", {"start": v(-117.54, 20.7) * mm, "end": v(-115.35, 20.7) * mm});
            skLineSegment(sketch, "E10.42.0.2", {"start": v(-115.35, 20.7) * mm, "end": v(-115.35, 17.65) * mm});
            skLineSegment(sketch, "E10.42.0.3", {"start": v(-117.54, 17.65) * mm, "end": v(-115.35, 17.65) * mm});
            skLineSegment(sketch, "E10.43.0.0", {"start": v(-115.38, 20.7) * mm, "end": v(-115.38, 17.65) * mm});
            skLineSegment(sketch, "E10.43.0.1", {"start": v(-115.38, 20.7) * mm, "end": v(-113.2, 20.7) * mm});
            skLineSegment(sketch, "E10.43.0.2", {"start": v(-113.2, 20.7) * mm, "end": v(-113.2, 17.65) * mm});
            skLineSegment(sketch, "E10.43.0.3", {"start": v(-115.38, 17.65) * mm, "end": v(-113.2, 17.65) * mm});
            skLineSegment(sketch, "E10.44.0.0", {"start": v(-113.22, 20.7) * mm, "end": v(-113.22, 17.65) * mm});
            skLineSegment(sketch, "E10.44.0.1", {"start": v(-113.22, 20.7) * mm, "end": v(-111.04, 20.7) * mm});
            skLineSegment(sketch, "E10.44.0.2", {"start": v(-111.04, 20.7) * mm, "end": v(-111.04, 17.65) * mm});
            skLineSegment(sketch, "E10.44.0.3", {"start": v(-113.22, 17.65) * mm, "end": v(-111.04, 17.65) * mm});
            skLineSegment(sketch, "E10.45.0.0", {"start": v(-111.06, 20.7) * mm, "end": v(-111.06, 17.65) * mm});
            skLineSegment(sketch, "E10.45.0.1", {"start": v(-111.06, 20.7) * mm, "end": v(-108.88, 20.7) * mm});
            skLineSegment(sketch, "E10.45.0.2", {"start": v(-108.88, 20.7) * mm, "end": v(-108.88, 17.65) * mm});
            skLineSegment(sketch, "E10.45.0.3", {"start": v(-111.06, 17.65) * mm, "end": v(-108.88, 17.65) * mm});
            skLineSegment(sketch, "E10.46.0.0", {"start": v(-108.9, 20.7) * mm, "end": v(-108.9, 17.65) * mm});
            skLineSegment(sketch, "E10.46.0.1", {"start": v(-108.9, 20.7) * mm, "end": v(-106.72, 20.7) * mm});
            skLineSegment(sketch, "E10.46.0.2", {"start": v(-106.72, 20.7) * mm, "end": v(-106.72, 17.65) * mm});
            skLineSegment(sketch, "E10.46.0.3", {"start": v(-108.9, 17.65) * mm, "end": v(-106.72, 17.65) * mm});
            skLineSegment(sketch, "E10.47.0.0", {"start": v(-106.74, 20.7) * mm, "end": v(-106.74, 17.65) * mm});
            skLineSegment(sketch, "E10.47.0.1", {"start": v(-106.74, 20.7) * mm, "end": v(-104.56, 20.7) * mm});
            skLineSegment(sketch, "E10.47.0.2", {"start": v(-104.56, 20.7) * mm, "end": v(-104.56, 17.65) * mm});
            skLineSegment(sketch, "E10.47.0.3", {"start": v(-106.74, 17.65) * mm, "end": v(-104.56, 17.65) * mm});
            skLineSegment(sketch, "E10.48.0.0", {"start": v(-104.58, 20.7) * mm, "end": v(-104.58, 17.65) * mm});
            skLineSegment(sketch, "E10.48.0.1", {"start": v(-104.58, 20.7) * mm, "end": v(-102.4, 20.7) * mm});
            skLineSegment(sketch, "E10.48.0.2", {"start": v(-102.4, 20.7) * mm, "end": v(-102.4, 17.65) * mm});
            skLineSegment(sketch, "E10.48.0.3", {"start": v(-104.58, 17.65) * mm, "end": v(-102.4, 17.65) * mm});
            skLineSegment(sketch, "E10.49.0.0", {"start": v(-102.43, 20.7) * mm, "end": v(-102.43, 17.65) * mm});
            skLineSegment(sketch, "E10.49.0.1", {"start": v(-102.43, 20.7) * mm, "end": v(-100.24, 20.7) * mm});
            skLineSegment(sketch, "E10.49.0.2", {"start": v(-100.24, 20.7) * mm, "end": v(-100.24, 17.65) * mm});
            skLineSegment(sketch, "E10.49.0.3", {"start": v(-102.43, 17.65) * mm, "end": v(-100.24, 17.65) * mm});
            skLineSegment(sketch, "E10.50.0.0", {"start": v(-100.27, 20.7) * mm, "end": v(-100.27, 17.65) * mm});
            skLineSegment(sketch, "E10.50.0.1", {"start": v(-100.27, 20.7) * mm, "end": v(-98.08, 20.7) * mm});
            skLineSegment(sketch, "E10.50.0.2", {"start": v(-98.08, 20.7) * mm, "end": v(-98.08, 17.65) * mm});
            skLineSegment(sketch, "E10.50.0.3", {"start": v(-100.27, 17.65) * mm, "end": v(-98.08, 17.65) * mm});
            skLineSegment(sketch, "E10.51.0.0", {"start": v(-98.1, 20.7) * mm, "end": v(-98.1, 17.65) * mm});
            skLineSegment(sketch, "E10.51.0.1", {"start": v(-98.1, 20.7) * mm, "end": v(-95.92, 20.7) * mm});
            skLineSegment(sketch, "E10.51.0.2", {"start": v(-95.92, 20.7) * mm, "end": v(-95.92, 17.65) * mm});
            skLineSegment(sketch, "E10.51.0.3", {"start": v(-98.1, 17.65) * mm, "end": v(-95.92, 17.65) * mm});
            skLineSegment(sketch, "E10.52.0.0", {"start": v(-95.95, 20.7) * mm, "end": v(-95.95, 17.65) * mm});
            skLineSegment(sketch, "E10.52.0.1", {"start": v(-95.95, 20.7) * mm, "end": v(-93.76, 20.7) * mm});
            skLineSegment(sketch, "E10.52.0.2", {"start": v(-93.76, 20.7) * mm, "end": v(-93.76, 17.65) * mm});
            skLineSegment(sketch, "E10.52.0.3", {"start": v(-95.95, 17.65) * mm, "end": v(-93.76, 17.65) * mm});
            skLineSegment(sketch, "E10.53.0.0", {"start": v(-93.79, 20.7) * mm, "end": v(-93.79, 17.65) * mm});
            skLineSegment(sketch, "E10.53.0.1", {"start": v(-93.79, 20.7) * mm, "end": v(-91.6, 20.7) * mm});
            skLineSegment(sketch, "E10.53.0.2", {"start": v(-91.6, 20.7) * mm, "end": v(-91.6, 17.65) * mm});
            skLineSegment(sketch, "E10.53.0.3", {"start": v(-93.79, 17.65) * mm, "end": v(-91.6, 17.65) * mm});
            skLineSegment(sketch, "E10.54.0.0", {"start": v(-91.63, 20.7) * mm, "end": v(-91.63, 17.65) * mm});
            skLineSegment(sketch, "E10.54.0.1", {"start": v(-91.63, 20.7) * mm, "end": v(-89.45, 20.7) * mm});
            skLineSegment(sketch, "E10.54.0.2", {"start": v(-89.45, 20.7) * mm, "end": v(-89.45, 17.65) * mm});
            skLineSegment(sketch, "E10.54.0.3", {"start": v(-91.63, 17.65) * mm, "end": v(-89.45, 17.65) * mm});
            skLineSegment(sketch, "E10.55.0.0", {"start": v(-89.47, 20.7) * mm, "end": v(-89.47, 17.65) * mm});
            skLineSegment(sketch, "E10.55.0.1", {"start": v(-89.47, 20.7) * mm, "end": v(-87.29, 20.7) * mm});
            skLineSegment(sketch, "E10.55.0.2", {"start": v(-87.29, 20.7) * mm, "end": v(-87.29, 17.65) * mm});
            skLineSegment(sketch, "E10.55.0.3", {"start": v(-89.47, 17.65) * mm, "end": v(-87.29, 17.65) * mm});
            skLineSegment(sketch, "E10.56.0.0", {"start": v(-87.31, 20.7) * mm, "end": v(-87.31, 17.65) * mm});
            skLineSegment(sketch, "E10.56.0.1", {"start": v(-87.31, 20.7) * mm, "end": v(-85.13, 20.7) * mm});
            skLineSegment(sketch, "E10.56.0.2", {"start": v(-85.13, 20.7) * mm, "end": v(-85.13, 17.65) * mm});
            skLineSegment(sketch, "E10.56.0.3", {"start": v(-87.31, 17.65) * mm, "end": v(-85.13, 17.65) * mm});
            skLineSegment(sketch, "E10.57.0.0", {"start": v(-85.15, 20.7) * mm, "end": v(-85.15, 17.65) * mm});
            skLineSegment(sketch, "E10.57.0.1", {"start": v(-85.15, 20.7) * mm, "end": v(-82.97, 20.7) * mm});
            skLineSegment(sketch, "E10.57.0.2", {"start": v(-82.97, 20.7) * mm, "end": v(-82.97, 17.65) * mm});
            skLineSegment(sketch, "E10.57.0.3", {"start": v(-85.15, 17.65) * mm, "end": v(-82.97, 17.65) * mm});
            skLineSegment(sketch, "E10.58.0.0", {"start": v(-83, 20.7) * mm, "end": v(-83, 17.65) * mm});
            skLineSegment(sketch, "E10.58.0.1", {"start": v(-83, 20.7) * mm, "end": v(-80.81, 20.7) * mm});
            skLineSegment(sketch, "E10.58.0.2", {"start": v(-80.81, 20.7) * mm, "end": v(-80.81, 17.65) * mm});
            skLineSegment(sketch, "E10.58.0.3", {"start": v(-83, 17.65) * mm, "end": v(-80.81, 17.65) * mm});
            skLineSegment(sketch, "E10.59.0.0", {"start": v(-80.84, 20.7) * mm, "end": v(-80.84, 17.65) * mm});
            skLineSegment(sketch, "E10.59.0.1", {"start": v(-80.84, 20.7) * mm, "end": v(-78.65, 20.7) * mm});
            skLineSegment(sketch, "E10.59.0.2", {"start": v(-78.65, 20.7) * mm, "end": v(-78.65, 17.65) * mm});
            skLineSegment(sketch, "E10.59.0.3", {"start": v(-80.84, 17.65) * mm, "end": v(-78.65, 17.65) * mm});
            skLineSegment(sketch, "E10.60.0.0", {"start": v(-78.68, 20.7) * mm, "end": v(-78.68, 17.65) * mm});
            skLineSegment(sketch, "E10.60.0.1", {"start": v(-78.68, 20.7) * mm, "end": v(-76.5, 20.7) * mm});
            skLineSegment(sketch, "E10.60.0.2", {"start": v(-76.5, 20.7) * mm, "end": v(-76.5, 17.65) * mm});
            skLineSegment(sketch, "E10.60.0.3", {"start": v(-78.68, 17.65) * mm, "end": v(-76.5, 17.65) * mm});
            skLineSegment(sketch, "E10.61.0.0", {"start": v(-76.52, 20.7) * mm, "end": v(-76.52, 17.65) * mm});
            skLineSegment(sketch, "E10.61.0.1", {"start": v(-76.52, 20.7) * mm, "end": v(-74.33, 20.7) * mm});
            skLineSegment(sketch, "E10.61.0.2", {"start": v(-74.33, 20.7) * mm, "end": v(-74.33, 17.65) * mm});
            skLineSegment(sketch, "E10.61.0.3", {"start": v(-76.52, 17.65) * mm, "end": v(-74.33, 17.65) * mm});
            skLineSegment(sketch, "E10.62.0.0", {"start": v(-74.36, 20.7) * mm, "end": v(-74.36, 17.65) * mm});
            skLineSegment(sketch, "E10.62.0.1", {"start": v(-74.36, 20.7) * mm, "end": v(-72.17, 20.7) * mm});
            skLineSegment(sketch, "E10.62.0.2", {"start": v(-72.17, 20.7) * mm, "end": v(-72.17, 17.65) * mm});
            skLineSegment(sketch, "E10.62.0.3", {"start": v(-74.36, 17.65) * mm, "end": v(-72.17, 17.65) * mm});
            skLineSegment(sketch, "E10.63.0.0", {"start": v(-72.2, 20.7) * mm, "end": v(-72.2, 17.65) * mm});
            skLineSegment(sketch, "E10.63.0.1", {"start": v(-72.2, 20.7) * mm, "end": v(-70.02, 20.7) * mm});
            skLineSegment(sketch, "E10.63.0.2", {"start": v(-70.02, 20.7) * mm, "end": v(-70.02, 17.65) * mm});
            skLineSegment(sketch, "E10.63.0.3", {"start": v(-72.2, 17.65) * mm, "end": v(-70.02, 17.65) * mm});
            skLineSegment(sketch, "E10.64.0.0", {"start": v(-70.04, 20.7) * mm, "end": v(-70.04, 17.65) * mm});
            skLineSegment(sketch, "E10.64.0.1", {"start": v(-70.04, 20.7) * mm, "end": v(-67.86, 20.7) * mm});
            skLineSegment(sketch, "E10.64.0.2", {"start": v(-67.86, 20.7) * mm, "end": v(-67.86, 17.65) * mm});
            skLineSegment(sketch, "E10.64.0.3", {"start": v(-70.04, 17.65) * mm, "end": v(-67.86, 17.65) * mm});
            skLineSegment(sketch, "E10.65.0.0", {"start": v(-67.88, 20.7) * mm, "end": v(-67.88, 17.65) * mm});
            skLineSegment(sketch, "E10.65.0.1", {"start": v(-67.88, 20.7) * mm, "end": v(-65.7, 20.7) * mm});
            skLineSegment(sketch, "E10.65.0.2", {"start": v(-65.7, 20.7) * mm, "end": v(-65.7, 17.65) * mm});
            skLineSegment(sketch, "E10.65.0.3", {"start": v(-67.88, 17.65) * mm, "end": v(-65.7, 17.65) * mm});
            skLineSegment(sketch, "E10.66.0.0", {"start": v(-65.72, 20.7) * mm, "end": v(-65.72, 17.65) * mm});
            skLineSegment(sketch, "E10.66.0.1", {"start": v(-65.72, 20.7) * mm, "end": v(-63.54, 20.7) * mm});
            skLineSegment(sketch, "E10.66.0.2", {"start": v(-63.54, 20.7) * mm, "end": v(-63.54, 17.65) * mm});
            skLineSegment(sketch, "E10.66.0.3", {"start": v(-65.72, 17.65) * mm, "end": v(-63.54, 17.65) * mm});
            skLineSegment(sketch, "E10.67.0.0", {"start": v(-63.56, 20.7) * mm, "end": v(-63.56, 17.65) * mm});
            skLineSegment(sketch, "E10.67.0.1", {"start": v(-63.56, 20.7) * mm, "end": v(-61.38, 20.7) * mm});
            skLineSegment(sketch, "E10.67.0.2", {"start": v(-61.38, 20.7) * mm, "end": v(-61.38, 17.65) * mm});
            skLineSegment(sketch, "E10.67.0.3", {"start": v(-63.56, 17.65) * mm, "end": v(-61.38, 17.65) * mm});
            skLineSegment(sketch, "E10.68.0.0", {"start": v(-61.4, 20.7) * mm, "end": v(-61.4, 17.65) * mm});
            skLineSegment(sketch, "E10.68.0.1", {"start": v(-61.4, 20.7) * mm, "end": v(-59.22, 20.7) * mm});
            skLineSegment(sketch, "E10.68.0.2", {"start": v(-59.22, 20.7) * mm, "end": v(-59.22, 17.65) * mm});
            skLineSegment(sketch, "E10.68.0.3", {"start": v(-61.4, 17.65) * mm, "end": v(-59.22, 17.65) * mm});
            skLineSegment(sketch, "E10.69.0.0", {"start": v(-59.25, 20.7) * mm, "end": v(-59.25, 17.65) * mm});
            skLineSegment(sketch, "E10.69.0.1", {"start": v(-59.25, 20.7) * mm, "end": v(-57.06, 20.7) * mm});
            skLineSegment(sketch, "E10.69.0.2", {"start": v(-57.06, 20.7) * mm, "end": v(-57.06, 17.65) * mm});
            skLineSegment(sketch, "E10.69.0.3", {"start": v(-59.25, 17.65) * mm, "end": v(-57.06, 17.65) * mm});
            skLineSegment(sketch, "E10.70.0.0", {"start": v(-57.09, 20.7) * mm, "end": v(-57.09, 17.65) * mm});
            skLineSegment(sketch, "E10.70.0.1", {"start": v(-57.09, 20.7) * mm, "end": v(-54.9, 20.7) * mm});
            skLineSegment(sketch, "E10.70.0.2", {"start": v(-54.9, 20.7) * mm, "end": v(-54.9, 17.65) * mm});
            skLineSegment(sketch, "E10.70.0.3", {"start": v(-57.09, 17.65) * mm, "end": v(-54.9, 17.65) * mm});
            skLineSegment(sketch, "E10.71.0.0", {"start": v(-54.93, 20.7) * mm, "end": v(-54.93, 17.65) * mm});
            skLineSegment(sketch, "E10.71.0.1", {"start": v(-54.93, 20.7) * mm, "end": v(-52.74, 20.7) * mm});
            skLineSegment(sketch, "E10.71.0.2", {"start": v(-52.74, 20.7) * mm, "end": v(-52.74, 17.65) * mm});
            skLineSegment(sketch, "E10.71.0.3", {"start": v(-54.93, 17.65) * mm, "end": v(-52.74, 17.65) * mm});
            skLineSegment(sketch, "E10.72.0.0", {"start": v(-52.77, 20.7) * mm, "end": v(-52.77, 17.65) * mm});
            skLineSegment(sketch, "E10.72.0.1", {"start": v(-52.77, 20.7) * mm, "end": v(-50.58, 20.7) * mm});
            skLineSegment(sketch, "E10.72.0.2", {"start": v(-50.58, 20.7) * mm, "end": v(-50.58, 17.65) * mm});
            skLineSegment(sketch, "E10.72.0.3", {"start": v(-52.77, 17.65) * mm, "end": v(-50.58, 17.65) * mm});
            skLineSegment(sketch, "E10.73.0.0", {"start": v(-50.6, 20.7) * mm, "end": v(-50.6, 17.65) * mm});
            skLineSegment(sketch, "E10.73.0.1", {"start": v(-50.6, 20.7) * mm, "end": v(-48.43, 20.7) * mm});
            skLineSegment(sketch, "E10.73.0.2", {"start": v(-48.43, 20.7) * mm, "end": v(-48.43, 17.65) * mm});
            skLineSegment(sketch, "E10.73.0.3", {"start": v(-50.6, 17.65) * mm, "end": v(-48.43, 17.65) * mm});
            skLineSegment(sketch, "E10.74.0.0", {"start": v(-48.45, 20.7) * mm, "end": v(-48.45, 17.65) * mm});
            skLineSegment(sketch, "E10.74.0.1", {"start": v(-48.45, 20.7) * mm, "end": v(-46.27, 20.7) * mm});
            skLineSegment(sketch, "E10.74.0.2", {"start": v(-46.27, 20.7) * mm, "end": v(-46.27, 17.65) * mm});
            skLineSegment(sketch, "E10.74.0.3", {"start": v(-48.45, 17.65) * mm, "end": v(-46.27, 17.65) * mm});
            skLineSegment(sketch, "E10.75.0.0", {"start": v(-46.3, 20.7) * mm, "end": v(-46.3, 17.65) * mm});
            skLineSegment(sketch, "E10.75.0.1", {"start": v(-46.3, 20.7) * mm, "end": v(-44.1, 20.7) * mm});
            skLineSegment(sketch, "E10.75.0.2", {"start": v(-44.1, 20.7) * mm, "end": v(-44.1, 17.65) * mm});
            skLineSegment(sketch, "E10.75.0.3", {"start": v(-46.3, 17.65) * mm, "end": v(-44.1, 17.65) * mm});
            skLineSegment(sketch, "E10.76.0.0", {"start": v(-44.13, 20.7) * mm, "end": v(-44.13, 17.65) * mm});
            skLineSegment(sketch, "E10.76.0.1", {"start": v(-44.13, 20.7) * mm, "end": v(-41.95, 20.7) * mm});
            skLineSegment(sketch, "E10.76.0.2", {"start": v(-41.95, 20.7) * mm, "end": v(-41.95, 17.65) * mm});
            skLineSegment(sketch, "E10.76.0.3", {"start": v(-44.13, 17.65) * mm, "end": v(-41.95, 17.65) * mm});
            skLineSegment(sketch, "E10.77.0.0", {"start": v(-41.97, 20.7) * mm, "end": v(-41.97, 17.65) * mm});
            skLineSegment(sketch, "E10.77.0.1", {"start": v(-41.97, 20.7) * mm, "end": v(-39.79, 20.7) * mm});
            skLineSegment(sketch, "E10.77.0.2", {"start": v(-39.79, 20.7) * mm, "end": v(-39.79, 17.65) * mm});
            skLineSegment(sketch, "E10.77.0.3", {"start": v(-41.97, 17.65) * mm, "end": v(-39.79, 17.65) * mm});
            skLineSegment(sketch, "E10.78.0.0", {"start": v(-39.81, 20.7) * mm, "end": v(-39.81, 17.65) * mm});
            skLineSegment(sketch, "E10.78.0.1", {"start": v(-39.81, 20.7) * mm, "end": v(-37.63, 20.7) * mm});
            skLineSegment(sketch, "E10.78.0.2", {"start": v(-37.63, 20.7) * mm, "end": v(-37.63, 17.65) * mm});
            skLineSegment(sketch, "E10.78.0.3", {"start": v(-39.81, 17.65) * mm, "end": v(-37.63, 17.65) * mm});
            skLineSegment(sketch, "E10.79.0.0", {"start": v(-37.66, 20.7) * mm, "end": v(-37.66, 17.65) * mm});
            skLineSegment(sketch, "E10.79.0.1", {"start": v(-37.66, 20.7) * mm, "end": v(-35.47, 20.7) * mm});
            skLineSegment(sketch, "E10.79.0.2", {"start": v(-35.47, 20.7) * mm, "end": v(-35.47, 17.65) * mm});
            skLineSegment(sketch, "E10.79.0.3", {"start": v(-37.66, 17.65) * mm, "end": v(-35.47, 17.65) * mm});
            skLineSegment(sketch, "E10.80.0.0", {"start": v(-35.5, 20.7) * mm, "end": v(-35.5, 17.65) * mm});
            skLineSegment(sketch, "E10.80.0.1", {"start": v(-35.5, 20.7) * mm, "end": v(-33.31, 20.7) * mm});
            skLineSegment(sketch, "E10.80.0.2", {"start": v(-33.31, 20.7) * mm, "end": v(-33.31, 17.65) * mm});
            skLineSegment(sketch, "E10.80.0.3", {"start": v(-35.5, 17.65) * mm, "end": v(-33.31, 17.65) * mm});
            skLineSegment(sketch, "E10.81.0.0", {"start": v(-33.34, 20.7) * mm, "end": v(-33.34, 17.65) * mm});
            skLineSegment(sketch, "E10.81.0.1", {"start": v(-33.34, 20.7) * mm, "end": v(-31.15, 20.7) * mm});
            skLineSegment(sketch, "E10.81.0.2", {"start": v(-31.15, 20.7) * mm, "end": v(-31.15, 17.65) * mm});
            skLineSegment(sketch, "E10.81.0.3", {"start": v(-33.34, 17.65) * mm, "end": v(-31.15, 17.65) * mm});
            skLineSegment(sketch, "E10.82.0.0", {"start": v(-31.18, 20.7) * mm, "end": v(-31.18, 17.65) * mm});
            skLineSegment(sketch, "E10.82.0.1", {"start": v(-31.18, 20.7) * mm, "end": v(-29, 20.7) * mm});
            skLineSegment(sketch, "E10.82.0.2", {"start": v(-29, 20.7) * mm, "end": v(-29, 17.65) * mm});
            skLineSegment(sketch, "E10.82.0.3", {"start": v(-31.18, 17.65) * mm, "end": v(-29, 17.65) * mm});
            skLineSegment(sketch, "E10.83.0.0", {"start": v(-29.02, 20.7) * mm, "end": v(-29.02, 17.65) * mm});
            skLineSegment(sketch, "E10.83.0.1", {"start": v(-29.02, 20.7) * mm, "end": v(-26.84, 20.7) * mm});
            skLineSegment(sketch, "E10.83.0.2", {"start": v(-26.84, 20.7) * mm, "end": v(-26.84, 17.65) * mm});
            skLineSegment(sketch, "E10.83.0.3", {"start": v(-29.02, 17.65) * mm, "end": v(-26.84, 17.65) * mm});
            skLineSegment(sketch, "E10.84.0.0", {"start": v(-26.86, 20.7) * mm, "end": v(-26.86, 17.65) * mm});
            skLineSegment(sketch, "E10.84.0.1", {"start": v(-26.86, 20.7) * mm, "end": v(-24.68, 20.7) * mm});
            skLineSegment(sketch, "E10.84.0.2", {"start": v(-24.68, 20.7) * mm, "end": v(-24.68, 17.65) * mm});
            skLineSegment(sketch, "E10.84.0.3", {"start": v(-26.86, 17.65) * mm, "end": v(-24.68, 17.65) * mm});
            skLineSegment(sketch, "E10.85.0.0", {"start": v(-24.7, 20.7) * mm, "end": v(-24.7, 17.65) * mm});
            skLineSegment(sketch, "E10.85.0.1", {"start": v(-24.7, 20.7) * mm, "end": v(-22.52, 20.7) * mm});
            skLineSegment(sketch, "E10.85.0.2", {"start": v(-22.52, 20.7) * mm, "end": v(-22.52, 17.65) * mm});
            skLineSegment(sketch, "E10.85.0.3", {"start": v(-24.7, 17.65) * mm, "end": v(-22.52, 17.65) * mm});
            skLineSegment(sketch, "E10.86.0.0", {"start": v(-22.54, 20.7) * mm, "end": v(-22.54, 17.65) * mm});
            skLineSegment(sketch, "E10.86.0.1", {"start": v(-22.54, 20.7) * mm, "end": v(-20.36, 20.7) * mm});
            skLineSegment(sketch, "E10.86.0.2", {"start": v(-20.36, 20.7) * mm, "end": v(-20.36, 17.65) * mm});
            skLineSegment(sketch, "E10.86.0.3", {"start": v(-22.54, 17.65) * mm, "end": v(-20.36, 17.65) * mm});
            skLineSegment(sketch, "E10.87.0.0", {"start": v(-20.38, 20.7) * mm, "end": v(-20.38, 17.65) * mm});
            skLineSegment(sketch, "E10.87.0.1", {"start": v(-20.38, 20.7) * mm, "end": v(-18.2, 20.7) * mm});
            skLineSegment(sketch, "E10.87.0.2", {"start": v(-18.2, 20.7) * mm, "end": v(-18.2, 17.65) * mm});
            skLineSegment(sketch, "E10.87.0.3", {"start": v(-20.38, 17.65) * mm, "end": v(-18.2, 17.65) * mm});
            skLineSegment(sketch, "E10.88.0.0", {"start": v(-18.22, 20.7) * mm, "end": v(-18.22, 17.65) * mm});
            skLineSegment(sketch, "E10.88.0.1", {"start": v(-18.22, 20.7) * mm, "end": v(-16.04, 20.7) * mm});
            skLineSegment(sketch, "E10.88.0.2", {"start": v(-16.04, 20.7) * mm, "end": v(-16.04, 17.65) * mm});
            skLineSegment(sketch, "E10.88.0.3", {"start": v(-18.22, 17.65) * mm, "end": v(-16.04, 17.65) * mm});
            skLineSegment(sketch, "E10.89.0.0", {"start": v(-16.07, 20.7) * mm, "end": v(-16.07, 17.65) * mm});
            skLineSegment(sketch, "E10.89.0.1", {"start": v(-16.07, 20.7) * mm, "end": v(-13.88, 20.7) * mm});
            skLineSegment(sketch, "E10.89.0.2", {"start": v(-13.88, 20.7) * mm, "end": v(-13.88, 17.65) * mm});
            skLineSegment(sketch, "E10.89.0.3", {"start": v(-16.07, 17.65) * mm, "end": v(-13.88, 17.65) * mm});
            skLineSegment(sketch, "E10.90.0.0", {"start": v(-13.9, 20.7) * mm, "end": v(-13.9, 17.65) * mm});
            skLineSegment(sketch, "E10.90.0.1", {"start": v(-13.9, 20.7) * mm, "end": v(-11.72, 20.7) * mm});
            skLineSegment(sketch, "E10.90.0.2", {"start": v(-11.72, 20.7) * mm, "end": v(-11.72, 17.65) * mm});
            skLineSegment(sketch, "E10.90.0.3", {"start": v(-13.9, 17.65) * mm, "end": v(-11.72, 17.65) * mm});
            skLineSegment(sketch, "E10.91.0.0", {"start": v(-11.75, 20.7) * mm, "end": v(-11.75, 17.65) * mm});
            skLineSegment(sketch, "E10.91.0.1", {"start": v(-11.75, 20.7) * mm, "end": v(-9.56, 20.7) * mm});
            skLineSegment(sketch, "E10.91.0.2", {"start": v(-9.56, 20.7) * mm, "end": v(-9.56, 17.65) * mm});
            skLineSegment(sketch, "E10.91.0.3", {"start": v(-11.75, 17.65) * mm, "end": v(-9.56, 17.65) * mm});
            skLineSegment(sketch, "E10.92.0.0", {"start": v(-9.59, 20.7) * mm, "end": v(-9.59, 17.65) * mm});
            skLineSegment(sketch, "E10.92.0.1", {"start": v(-9.59, 20.7) * mm, "end": v(-7.4, 20.7) * mm});
            skLineSegment(sketch, "E10.92.0.2", {"start": v(-7.4, 20.7) * mm, "end": v(-7.4, 17.65) * mm});
            skLineSegment(sketch, "E10.92.0.3", {"start": v(-9.59, 17.65) * mm, "end": v(-7.4, 17.65) * mm});
            skLineSegment(sketch, "E10.93.0.0", {"start": v(-7.43, 20.7) * mm, "end": v(-7.43, 17.65) * mm});
            skLineSegment(sketch, "E10.93.0.1", {"start": v(-7.43, 20.7) * mm, "end": v(-5.25, 20.7) * mm});
            skLineSegment(sketch, "E10.93.0.2", {"start": v(-5.25, 20.7) * mm, "end": v(-5.25, 17.65) * mm});
            skLineSegment(sketch, "E10.93.0.3", {"start": v(-7.43, 17.65) * mm, "end": v(-5.25, 17.65) * mm});
            skLineSegment(sketch, "E10.94.0.0", {"start": v(-5.27, 20.7) * mm, "end": v(-5.27, 17.65) * mm});
            skLineSegment(sketch, "E10.94.0.1", {"start": v(-5.27, 20.7) * mm, "end": v(-3.09, 20.7) * mm});
            skLineSegment(sketch, "E10.94.0.2", {"start": v(-3.09, 20.7) * mm, "end": v(-3.09, 17.65) * mm});
            skLineSegment(sketch, "E10.94.0.3", {"start": v(-5.27, 17.65) * mm, "end": v(-3.09, 17.65) * mm});
            skLineSegment(sketch, "E10.95.0.0", {"start": v(-3.11, 20.7) * mm, "end": v(-3.11, 17.65) * mm});
            skLineSegment(sketch, "E10.95.0.1", {"start": v(-3.11, 20.7) * mm, "end": v(-0.93, 20.7) * mm});
            skLineSegment(sketch, "E10.95.0.2", {"start": v(-0.93, 20.7) * mm, "end": v(-0.93, 17.65) * mm});
            skLineSegment(sketch, "E10.95.0.3", {"start": v(-3.11, 17.65) * mm, "end": v(-0.93, 17.65) * mm});
            skLineSegment(sketch, "E10.96.0.0", {"start": v(-0.95, 20.7) * mm, "end": v(-0.95, 17.65) * mm});
            skLineSegment(sketch, "E10.96.0.1", {"start": v(-0.95, 20.7) * mm, "end": v(1.23, 20.7) * mm});
            skLineSegment(sketch, "E10.96.0.2", {"start": v(1.23, 20.7) * mm, "end": v(1.23, 17.65) * mm});
            skLineSegment(sketch, "E10.96.0.3", {"start": v(-0.95, 17.65) * mm, "end": v(1.23, 17.65) * mm});
            skLineSegment(sketch, "E10.97.0.0", {"start": v(1.2, 20.7) * mm, "end": v(1.2, 17.65) * mm});
            skLineSegment(sketch, "E10.97.0.1", {"start": v(1.2, 20.7) * mm, "end": v(3.4, 20.7) * mm});
            skLineSegment(sketch, "E10.97.0.2", {"start": v(3.4, 20.7) * mm, "end": v(3.4, 17.65) * mm});
            skLineSegment(sketch, "E10.97.0.3", {"start": v(1.2, 17.65) * mm, "end": v(3.4, 17.65) * mm});
            skLineSegment(sketch, "E10.98.0.0", {"start": v(3.37, 20.7) * mm, "end": v(3.37, 17.65) * mm});
            skLineSegment(sketch, "E10.98.0.1", {"start": v(3.37, 20.7) * mm, "end": v(5.55, 20.7) * mm});
            skLineSegment(sketch, "E10.98.0.2", {"start": v(5.55, 20.7) * mm, "end": v(5.55, 17.65) * mm});
            skLineSegment(sketch, "E10.98.0.3", {"start": v(3.37, 17.65) * mm, "end": v(5.55, 17.65) * mm});
            skLineSegment(sketch, "E10.99.0.0", {"start": v(5.52, 20.7) * mm, "end": v(5.52, 17.65) * mm});
            skLineSegment(sketch, "E10.99.0.1", {"start": v(5.52, 20.7) * mm, "end": v(7.7, 20.7) * mm});
            skLineSegment(sketch, "E10.99.0.2", {"start": v(7.7, 20.7) * mm, "end": v(7.7, 17.65) * mm});
            skLineSegment(sketch, "E10.99.0.3", {"start": v(5.52, 17.65) * mm, "end": v(7.7, 17.65) * mm});
            skLineSegment(sketch, "E10.direction1", {"start": v(-208.22, 17.65) * mm, "end": v(-206.06, 17.65) * mm, "construction": true});
            skSolve(sketch);
        }
        {
            var Q0;
            Q0=makeQuery(id+"F13.imprint","IMPRINT",FACE,{"disambiguationData":[TD([[makeQuery(id+"F13.imprint","IMPRINT",EDGE,{"derivedFrom":sQuery(id+"F13.wireOp",EDGE,"E9.bottom")}),-1.0]])]});
            var Q1;
            {var subQ0=sQuery(id+"F13.wireOp",EDGE,"E10.1.0.2");Q1=makeQuery(id+"F13.imprint","IMPRINT",FACE,{"disambiguationData":[TD([[makeQuery(id+"F13.imprint","IMPRINT",EDGE,{"derivedFrom":subQ0}),1.0]])]});}
            var Q2;
            {var subQ0=sQuery(id+"F13.wireOp",EDGE,"E10.3.0.2");Q2=makeQuery(id+"F13.imprint","IMPRINT",FACE,{"disambiguationData":[TD([[makeQuery(id+"F13.imprint","IMPRINT",EDGE,{"derivedFrom":subQ0}),1.0]])]});}
            var Q3;
            {var subQ0=sQuery(id+"F13.wireOp",EDGE,"E10.5.0.2");Q3=makeQuery(id+"F13.imprint","IMPRINT",FACE,{"disambiguationData":[TD([[makeQuery(id+"F13.imprint","IMPRINT",EDGE,{"derivedFrom":subQ0}),1.0]])]});}
            var Q4;
            {var subQ0=sQuery(id+"F13.wireOp",EDGE,"E10.7.0.2");Q4=makeQuery(id+"F13.imprint","IMPRINT",FACE,{"disambiguationData":[TD([[makeQuery(id+"F13.imprint","IMPRINT",EDGE,{"derivedFrom":subQ0}),1.0]])]});}
            var Q5;
            {var subQ0=sQuery(id+"F13.wireOp",EDGE,"E10.9.0.2");Q5=makeQuery(id+"F13.imprint","IMPRINT",FACE,{"disambiguationData":[TD([[makeQuery(id+"F13.imprint","IMPRINT",EDGE,{"derivedFrom":subQ0}),1.0]])]});}
            var Q6;
            {var subQ0=sQuery(id+"F13.wireOp",EDGE,"E10.11.0.2");Q6=makeQuery(id+"F13.imprint","IMPRINT",FACE,{"disambiguationData":[TD([[makeQuery(id+"F13.imprint","IMPRINT",EDGE,{"derivedFrom":subQ0}),1.0]])]});}
            var Q7;
            {var subQ0=sQuery(id+"F13.wireOp",EDGE,"E10.13.0.2");Q7=makeQuery(id+"F13.imprint","IMPRINT",FACE,{"disambiguationData":[TD([[makeQuery(id+"F13.imprint","IMPRINT",EDGE,{"derivedFrom":subQ0}),1.0]])]});}
            var Q8;
            {var subQ0=sQuery(id+"F13.wireOp",EDGE,"E10.15.0.2");Q8=makeQuery(id+"F13.imprint","IMPRINT",FACE,{"disambiguationData":[TD([[makeQuery(id+"F13.imprint","IMPRINT",EDGE,{"derivedFrom":subQ0}),1.0]])]});}
            var Q9;
            {var subQ0=sQuery(id+"F13.wireOp",EDGE,"E10.17.0.2");Q9=makeQuery(id+"F13.imprint","IMPRINT",FACE,{"disambiguationData":[TD([[makeQuery(id+"F13.imprint","IMPRINT",EDGE,{"derivedFrom":subQ0}),1.0]])]});}
            var Q10;
            {var subQ0=sQuery(id+"F13.wireOp",EDGE,"E10.19.0.2");Q10=makeQuery(id+"F13.imprint","IMPRINT",FACE,{"disambiguationData":[TD([[makeQuery(id+"F13.imprint","IMPRINT",EDGE,{"derivedFrom":subQ0}),1.0]])]});}
            var Q11;
            {var subQ0=sQuery(id+"F13.wireOp",EDGE,"E10.21.0.2");Q11=makeQuery(id+"F13.imprint","IMPRINT",FACE,{"disambiguationData":[TD([[makeQuery(id+"F13.imprint","IMPRINT",EDGE,{"derivedFrom":subQ0}),1.0]])]});}
            var Q12;
            {var subQ0=sQuery(id+"F13.wireOp",EDGE,"E10.23.0.2");Q12=makeQuery(id+"F13.imprint","IMPRINT",FACE,{"disambiguationData":[TD([[makeQuery(id+"F13.imprint","IMPRINT",EDGE,{"derivedFrom":subQ0}),1.0]])]});}
            var Q13;
            {var subQ0=sQuery(id+"F13.wireOp",EDGE,"E10.25.0.2");Q13=makeQuery(id+"F13.imprint","IMPRINT",FACE,{"disambiguationData":[TD([[makeQuery(id+"F13.imprint","IMPRINT",EDGE,{"derivedFrom":subQ0}),1.0]])]});}
            var Q14;
            {var subQ0=sQuery(id+"F13.wireOp",EDGE,"E10.27.0.2");Q14=makeQuery(id+"F13.imprint","IMPRINT",FACE,{"disambiguationData":[TD([[makeQuery(id+"F13.imprint","IMPRINT",EDGE,{"derivedFrom":subQ0}),1.0]])]});}
            var Q15;
            {var subQ0=sQuery(id+"F13.wireOp",EDGE,"E10.29.0.2");Q15=makeQuery(id+"F13.imprint","IMPRINT",FACE,{"disambiguationData":[TD([[makeQuery(id+"F13.imprint","IMPRINT",EDGE,{"derivedFrom":subQ0}),1.0]])]});}
            var Q16;
            {var subQ0=sQuery(id+"F13.wireOp",EDGE,"E10.31.0.2");Q16=makeQuery(id+"F13.imprint","IMPRINT",FACE,{"disambiguationData":[TD([[makeQuery(id+"F13.imprint","IMPRINT",EDGE,{"derivedFrom":subQ0}),1.0]])]});}
            var Q17;
            {var subQ0=sQuery(id+"F13.wireOp",EDGE,"E10.33.0.2");Q17=makeQuery(id+"F13.imprint","IMPRINT",FACE,{"disambiguationData":[TD([[makeQuery(id+"F13.imprint","IMPRINT",EDGE,{"derivedFrom":subQ0}),1.0]])]});}
            var Q18;
            {var subQ0=sQuery(id+"F13.wireOp",EDGE,"E10.35.0.2");Q18=makeQuery(id+"F13.imprint","IMPRINT",FACE,{"disambiguationData":[TD([[makeQuery(id+"F13.imprint","IMPRINT",EDGE,{"derivedFrom":subQ0}),1.0]])]});}
            var Q19;
            {var subQ0=sQuery(id+"F13.wireOp",EDGE,"E10.37.0.2");Q19=makeQuery(id+"F13.imprint","IMPRINT",FACE,{"disambiguationData":[TD([[makeQuery(id+"F13.imprint","IMPRINT",EDGE,{"derivedFrom":subQ0}),1.0]])]});}
            var Q20;
            {var subQ0=sQuery(id+"F13.wireOp",EDGE,"E10.39.0.2");Q20=makeQuery(id+"F13.imprint","IMPRINT",FACE,{"disambiguationData":[TD([[makeQuery(id+"F13.imprint","IMPRINT",EDGE,{"derivedFrom":subQ0}),1.0]])]});}
            var Q21;
            {var subQ0=sQuery(id+"F13.wireOp",EDGE,"E10.41.0.2");Q21=makeQuery(id+"F13.imprint","IMPRINT",FACE,{"disambiguationData":[TD([[makeQuery(id+"F13.imprint","IMPRINT",EDGE,{"derivedFrom":subQ0}),1.0]])]});}
            var Q22;
            {var subQ0=sQuery(id+"F13.wireOp",EDGE,"E10.43.0.2");Q22=makeQuery(id+"F13.imprint","IMPRINT",FACE,{"disambiguationData":[TD([[makeQuery(id+"F13.imprint","IMPRINT",EDGE,{"derivedFrom":subQ0}),1.0]])]});}
            var Q23;
            {var subQ0=sQuery(id+"F13.wireOp",EDGE,"E10.45.0.2");Q23=makeQuery(id+"F13.imprint","IMPRINT",FACE,{"disambiguationData":[TD([[makeQuery(id+"F13.imprint","IMPRINT",EDGE,{"derivedFrom":subQ0}),1.0]])]});}
            var Q24;
            {var subQ0=sQuery(id+"F13.wireOp",EDGE,"E10.47.0.2");Q24=makeQuery(id+"F13.imprint","IMPRINT",FACE,{"disambiguationData":[TD([[makeQuery(id+"F13.imprint","IMPRINT",EDGE,{"derivedFrom":subQ0}),1.0]])]});}
            var Q25;
            {var subQ0=sQuery(id+"F13.wireOp",EDGE,"E10.49.0.2");Q25=makeQuery(id+"F13.imprint","IMPRINT",FACE,{"disambiguationData":[TD([[makeQuery(id+"F13.imprint","IMPRINT",EDGE,{"derivedFrom":subQ0}),1.0]])]});}
            var Q26;
            {var subQ0=sQuery(id+"F13.wireOp",EDGE,"E10.51.0.2");Q26=makeQuery(id+"F13.imprint","IMPRINT",FACE,{"disambiguationData":[TD([[makeQuery(id+"F13.imprint","IMPRINT",EDGE,{"derivedFrom":subQ0}),1.0]])]});}
            var Q27;
            {var subQ0=sQuery(id+"F13.wireOp",EDGE,"E10.53.0.2");Q27=makeQuery(id+"F13.imprint","IMPRINT",FACE,{"disambiguationData":[TD([[makeQuery(id+"F13.imprint","IMPRINT",EDGE,{"derivedFrom":subQ0}),1.0]])]});}
            var Q28;
            {var subQ0=sQuery(id+"F13.wireOp",EDGE,"E10.55.0.2");Q28=makeQuery(id+"F13.imprint","IMPRINT",FACE,{"disambiguationData":[TD([[makeQuery(id+"F13.imprint","IMPRINT",EDGE,{"derivedFrom":subQ0}),1.0]])]});}
            var Q29;
            {var subQ0=sQuery(id+"F13.wireOp",EDGE,"E10.57.0.2");Q29=makeQuery(id+"F13.imprint","IMPRINT",FACE,{"disambiguationData":[TD([[makeQuery(id+"F13.imprint","IMPRINT",EDGE,{"derivedFrom":subQ0}),1.0]])]});}
            var Q30;
            {var subQ0=sQuery(id+"F13.wireOp",EDGE,"E10.59.0.2");Q30=makeQuery(id+"F13.imprint","IMPRINT",FACE,{"disambiguationData":[TD([[makeQuery(id+"F13.imprint","IMPRINT",EDGE,{"derivedFrom":subQ0}),1.0]])]});}
            var Q31;
            {var subQ0=sQuery(id+"F13.wireOp",EDGE,"E10.61.0.2");Q31=makeQuery(id+"F13.imprint","IMPRINT",FACE,{"disambiguationData":[TD([[makeQuery(id+"F13.imprint","IMPRINT",EDGE,{"derivedFrom":subQ0}),1.0]])]});}
            var Q32;
            {var subQ0=sQuery(id+"F13.wireOp",EDGE,"E10.63.0.2");Q32=makeQuery(id+"F13.imprint","IMPRINT",FACE,{"disambiguationData":[TD([[makeQuery(id+"F13.imprint","IMPRINT",EDGE,{"derivedFrom":subQ0}),1.0]])]});}
            var Q33;
            {var subQ0=sQuery(id+"F13.wireOp",EDGE,"E10.65.0.2");Q33=makeQuery(id+"F13.imprint","IMPRINT",FACE,{"disambiguationData":[TD([[makeQuery(id+"F13.imprint","IMPRINT",EDGE,{"derivedFrom":subQ0}),1.0]])]});}
            var Q34;
            {var subQ0=sQuery(id+"F13.wireOp",EDGE,"E10.67.0.2");Q34=makeQuery(id+"F13.imprint","IMPRINT",FACE,{"disambiguationData":[TD([[makeQuery(id+"F13.imprint","IMPRINT",EDGE,{"derivedFrom":subQ0}),1.0]])]});}
            var Q35;
            {var subQ0=sQuery(id+"F13.wireOp",EDGE,"E10.69.0.2");Q35=makeQuery(id+"F13.imprint","IMPRINT",FACE,{"disambiguationData":[TD([[makeQuery(id+"F13.imprint","IMPRINT",EDGE,{"derivedFrom":subQ0}),1.0]])]});}
            var Q36;
            {var subQ0=sQuery(id+"F13.wireOp",EDGE,"E10.71.0.2");Q36=makeQuery(id+"F13.imprint","IMPRINT",FACE,{"disambiguationData":[TD([[makeQuery(id+"F13.imprint","IMPRINT",EDGE,{"derivedFrom":subQ0}),1.0]])]});}
            var Q37;
            {var subQ0=sQuery(id+"F13.wireOp",EDGE,"E10.73.0.2");Q37=makeQuery(id+"F13.imprint","IMPRINT",FACE,{"disambiguationData":[TD([[makeQuery(id+"F13.imprint","IMPRINT",EDGE,{"derivedFrom":subQ0}),1.0]])]});}
            var Q38;
            {var subQ0=sQuery(id+"F13.wireOp",EDGE,"E10.75.0.2");Q38=makeQuery(id+"F13.imprint","IMPRINT",FACE,{"disambiguationData":[TD([[makeQuery(id+"F13.imprint","IMPRINT",EDGE,{"derivedFrom":subQ0}),1.0]])]});}
            var Q39;
            {var subQ0=sQuery(id+"F13.wireOp",EDGE,"E10.77.0.2");Q39=makeQuery(id+"F13.imprint","IMPRINT",FACE,{"disambiguationData":[TD([[makeQuery(id+"F13.imprint","IMPRINT",EDGE,{"derivedFrom":subQ0}),1.0]])]});}
            var Q40;
            {var subQ0=sQuery(id+"F13.wireOp",EDGE,"E10.79.0.2");Q40=makeQuery(id+"F13.imprint","IMPRINT",FACE,{"disambiguationData":[TD([[makeQuery(id+"F13.imprint","IMPRINT",EDGE,{"derivedFrom":subQ0}),1.0]])]});}
            var Q41;
            {var subQ0=sQuery(id+"F13.wireOp",EDGE,"E10.81.0.2");Q41=makeQuery(id+"F13.imprint","IMPRINT",FACE,{"disambiguationData":[TD([[makeQuery(id+"F13.imprint","IMPRINT",EDGE,{"derivedFrom":subQ0}),1.0]])]});}
            var Q42;
            {var subQ0=sQuery(id+"F13.wireOp",EDGE,"E10.83.0.2");Q42=makeQuery(id+"F13.imprint","IMPRINT",FACE,{"disambiguationData":[TD([[makeQuery(id+"F13.imprint","IMPRINT",EDGE,{"derivedFrom":subQ0}),1.0]])]});}
            var Q43;
            {var subQ0=sQuery(id+"F13.wireOp",EDGE,"E10.85.0.2");Q43=makeQuery(id+"F13.imprint","IMPRINT",FACE,{"disambiguationData":[TD([[makeQuery(id+"F13.imprint","IMPRINT",EDGE,{"derivedFrom":subQ0}),1.0]])]});}
            var Q44;
            {var subQ0=sQuery(id+"F13.wireOp",EDGE,"E10.87.0.2");Q44=makeQuery(id+"F13.imprint","IMPRINT",FACE,{"disambiguationData":[TD([[makeQuery(id+"F13.imprint","IMPRINT",EDGE,{"derivedFrom":subQ0}),1.0]])]});}
            var Q45;
            {var subQ0=sQuery(id+"F13.wireOp",EDGE,"E10.89.0.2");Q45=makeQuery(id+"F13.imprint","IMPRINT",FACE,{"disambiguationData":[TD([[makeQuery(id+"F13.imprint","IMPRINT",EDGE,{"derivedFrom":subQ0}),1.0]])]});}
            var Q46;
            {var subQ0=sQuery(id+"F13.wireOp",EDGE,"E10.91.0.2");Q46=makeQuery(id+"F13.imprint","IMPRINT",FACE,{"disambiguationData":[TD([[makeQuery(id+"F13.imprint","IMPRINT",EDGE,{"derivedFrom":subQ0}),1.0]])]});}
            var Q47;
            {var subQ0=sQuery(id+"F13.wireOp",EDGE,"E10.93.0.2");Q47=makeQuery(id+"F13.imprint","IMPRINT",FACE,{"disambiguationData":[TD([[makeQuery(id+"F13.imprint","IMPRINT",EDGE,{"derivedFrom":subQ0}),1.0]])]});}
            var Q48;
            {var subQ0=sQuery(id+"F13.wireOp",EDGE,"E10.95.0.2");Q48=makeQuery(id+"F13.imprint","IMPRINT",FACE,{"disambiguationData":[TD([[makeQuery(id+"F13.imprint","IMPRINT",EDGE,{"derivedFrom":subQ0}),1.0]])]});}
            var Q49;
            {var subQ0=sQuery(id+"F13.wireOp",EDGE,"E10.95.0.2");Q49=makeQuery(id+"F13.imprint","IMPRINT",FACE,{"disambiguationData":[TD([[makeQuery(id+"F13.imprint","IMPRINT",EDGE,{"derivedFrom":subQ0}),1.0]])]});}
            var Q50;
            {var subQ0=sQuery(id+"F13.wireOp",EDGE,"E10.97.0.2");Q50=makeQuery(id+"F13.imprint","IMPRINT",FACE,{"disambiguationData":[TD([[makeQuery(id+"F13.imprint","IMPRINT",EDGE,{"derivedFrom":subQ0}),1.0]])]});}
            extrude(context, id + "F14", {"entities" : qUnion([Q0, Q1, Q2, Q3, Q4, Q5, Q6, Q7, Q8, Q9, Q10, Q11, Q12, Q13, Q14, Q15, Q16, Q17, Q18, Q19, Q20, Q21, Q22, Q23, Q24, Q25, Q26, Q27, Q28, Q29, Q30, Q31, Q32, Q33, Q34, Q35, Q36, Q37, Q38, Q39, Q40, Q41, Q42, Q43, Q44, Q45, Q46, Q47, Q48, Q49, Q50]), "operationType" : NewBodyOperationType.REMOVE, "endBound" : BoundingType.UP_TO_NEXT, "oppositeDirection" : true, "depth" : 25.4 * mm});
        }
        {
            var Q0;
            Q0=makeQuery(id+"F1.opExtrude","SWEPT_FACE",FACE,{"disambiguationData":[OSD([sQuery(id+"F0.wireOp",EDGE,"E0.top")])]});
            var sketch = newSketch(context, id + "F15", { "sketchPlane" : qUnion([Q0])});
            skLineSegment(sketch, "E11.0", {"start": v(3.4, 20.7) * mm, "end": v(3.4, 17.65) * mm});
            skPoint(sketch, "E12.0", {"position": v(4.46, 17.65) * mm});
            skLineSegment(sketch, "E13.0", {"start": v(3.4, 17.65) * mm, "end": v(5.52, 17.65) * mm});
            skLineSegment(sketch, "E14.0", {"start": v(5.52, 20.7) * mm, "end": v(5.52, 17.65) * mm});
            skLineSegment(sketch, "E15.1.0.0", {"start": v(5.55, 20.7) * mm, "end": v(5.55, 17.65) * mm});
            skLineSegment(sketch, "E15.1.0.1", {"start": v(5.55, 17.65) * mm, "end": v(7.68, 17.65) * mm});
            skLineSegment(sketch, "E15.1.0.2", {"start": v(7.68, 20.7) * mm, "end": v(7.68, 17.65) * mm});
            skLineSegment(sketch, "E15.2.0.0", {"start": v(7.7, 20.7) * mm, "end": v(7.7, 17.65) * mm});
            skLineSegment(sketch, "E15.2.0.1", {"start": v(7.7, 17.65) * mm, "end": v(9.84, 17.65) * mm});
            skLineSegment(sketch, "E15.2.0.2", {"start": v(9.84, 20.7) * mm, "end": v(9.84, 17.65) * mm});
            skLineSegment(sketch, "E15.3.0.0", {"start": v(9.87, 20.7) * mm, "end": v(9.87, 17.65) * mm});
            skLineSegment(sketch, "E15.3.0.1", {"start": v(9.87, 17.65) * mm, "end": v(12, 17.65) * mm});
            skLineSegment(sketch, "E15.3.0.2", {"start": v(12, 20.7) * mm, "end": v(12, 17.65) * mm});
            skLineSegment(sketch, "E15.4.0.0", {"start": v(12.03, 20.7) * mm, "end": v(12.03, 17.65) * mm});
            skLineSegment(sketch, "E15.4.0.1", {"start": v(12.03, 17.65) * mm, "end": v(14.16, 17.65) * mm});
            skLineSegment(sketch, "E15.4.0.2", {"start": v(14.16, 20.7) * mm, "end": v(14.16, 17.65) * mm});
            skLineSegment(sketch, "E15.5.0.0", {"start": v(14.19, 20.7) * mm, "end": v(14.19, 17.65) * mm});
            skLineSegment(sketch, "E15.5.0.1", {"start": v(14.19, 17.65) * mm, "end": v(16.32, 17.65) * mm});
            skLineSegment(sketch, "E15.5.0.2", {"start": v(16.32, 20.7) * mm, "end": v(16.32, 17.65) * mm});
            skLineSegment(sketch, "E15.6.0.0", {"start": v(16.34, 20.7) * mm, "end": v(16.34, 17.65) * mm});
            skLineSegment(sketch, "E15.6.0.1", {"start": v(16.34, 17.65) * mm, "end": v(18.48, 17.65) * mm});
            skLineSegment(sketch, "E15.6.0.2", {"start": v(18.48, 20.7) * mm, "end": v(18.48, 17.65) * mm});
            skLineSegment(sketch, "E15.7.0.0", {"start": v(18.5, 20.7) * mm, "end": v(18.5, 17.65) * mm});
            skLineSegment(sketch, "E15.7.0.1", {"start": v(18.5, 17.65) * mm, "end": v(20.64, 17.65) * mm});
            skLineSegment(sketch, "E15.7.0.2", {"start": v(20.64, 20.7) * mm, "end": v(20.64, 17.65) * mm});
            skLineSegment(sketch, "E15.8.0.0", {"start": v(20.66, 20.7) * mm, "end": v(20.66, 17.65) * mm});
            skLineSegment(sketch, "E15.8.0.1", {"start": v(20.66, 17.65) * mm, "end": v(22.8, 17.65) * mm});
            skLineSegment(sketch, "E15.8.0.2", {"start": v(22.8, 20.7) * mm, "end": v(22.8, 17.65) * mm});
            skLineSegment(sketch, "E15.9.0.0", {"start": v(22.82, 20.7) * mm, "end": v(22.82, 17.65) * mm});
            skLineSegment(sketch, "E15.9.0.1", {"start": v(22.82, 17.65) * mm, "end": v(24.96, 17.65) * mm});
            skLineSegment(sketch, "E15.9.0.2", {"start": v(24.96, 20.7) * mm, "end": v(24.96, 17.65) * mm});
            skLineSegment(sketch, "E15.10.0.0", {"start": v(24.98, 20.7) * mm, "end": v(24.98, 17.65) * mm});
            skLineSegment(sketch, "E15.10.0.1", {"start": v(24.98, 17.65) * mm, "end": v(27.11, 17.65) * mm});
            skLineSegment(sketch, "E15.10.0.2", {"start": v(27.11, 20.7) * mm, "end": v(27.11, 17.65) * mm});
            skLineSegment(sketch, "E15.11.0.0", {"start": v(27.14, 20.7) * mm, "end": v(27.14, 17.65) * mm});
            skLineSegment(sketch, "E15.11.0.1", {"start": v(27.14, 17.65) * mm, "end": v(29.27, 17.65) * mm});
            skLineSegment(sketch, "E15.11.0.2", {"start": v(29.27, 20.7) * mm, "end": v(29.27, 17.65) * mm});
            skLineSegment(sketch, "E15.12.0.0", {"start": v(29.3, 20.7) * mm, "end": v(29.3, 17.65) * mm});
            skLineSegment(sketch, "E15.12.0.1", {"start": v(29.3, 17.65) * mm, "end": v(31.43, 17.65) * mm});
            skLineSegment(sketch, "E15.12.0.2", {"start": v(31.43, 20.7) * mm, "end": v(31.43, 17.65) * mm});
            skLineSegment(sketch, "E15.13.0.0", {"start": v(31.46, 20.7) * mm, "end": v(31.46, 17.65) * mm});
            skLineSegment(sketch, "E15.13.0.1", {"start": v(31.46, 17.65) * mm, "end": v(33.6, 17.65) * mm});
            skLineSegment(sketch, "E15.13.0.2", {"start": v(33.6, 20.7) * mm, "end": v(33.6, 17.65) * mm});
            skLineSegment(sketch, "E15.14.0.0", {"start": v(33.62, 20.7) * mm, "end": v(33.62, 17.65) * mm});
            skLineSegment(sketch, "E15.14.0.1", {"start": v(33.62, 17.65) * mm, "end": v(35.75, 17.65) * mm});
            skLineSegment(sketch, "E15.14.0.2", {"start": v(35.75, 20.7) * mm, "end": v(35.75, 17.65) * mm});
            skLineSegment(sketch, "E15.15.0.0", {"start": v(35.78, 20.7) * mm, "end": v(35.78, 17.65) * mm});
            skLineSegment(sketch, "E15.15.0.1", {"start": v(35.78, 17.65) * mm, "end": v(37.9, 17.65) * mm});
            skLineSegment(sketch, "E15.15.0.2", {"start": v(37.9, 20.7) * mm, "end": v(37.9, 17.65) * mm});
            skLineSegment(sketch, "E15.16.0.0", {"start": v(37.93, 20.7) * mm, "end": v(37.93, 17.65) * mm});
            skLineSegment(sketch, "E15.16.0.1", {"start": v(37.93, 17.65) * mm, "end": v(40.07, 17.65) * mm});
            skLineSegment(sketch, "E15.16.0.2", {"start": v(40.07, 20.7) * mm, "end": v(40.07, 17.65) * mm});
            skLineSegment(sketch, "E15.17.0.0", {"start": v(40.1, 20.7) * mm, "end": v(40.1, 17.65) * mm});
            skLineSegment(sketch, "E15.17.0.1", {"start": v(40.1, 17.65) * mm, "end": v(42.23, 17.65) * mm});
            skLineSegment(sketch, "E15.17.0.2", {"start": v(42.23, 20.7) * mm, "end": v(42.23, 17.65) * mm});
            skLineSegment(sketch, "E15.18.0.0", {"start": v(42.25, 20.7) * mm, "end": v(42.25, 17.65) * mm});
            skLineSegment(sketch, "E15.18.0.1", {"start": v(42.25, 17.65) * mm, "end": v(44.39, 17.65) * mm});
            skLineSegment(sketch, "E15.18.0.2", {"start": v(44.39, 20.7) * mm, "end": v(44.39, 17.65) * mm});
            skLineSegment(sketch, "E15.19.0.0", {"start": v(44.41, 20.7) * mm, "end": v(44.41, 17.65) * mm});
            skLineSegment(sketch, "E15.19.0.1", {"start": v(44.41, 17.65) * mm, "end": v(46.55, 17.65) * mm});
            skLineSegment(sketch, "E15.19.0.2", {"start": v(46.55, 20.7) * mm, "end": v(46.55, 17.65) * mm});
            skLineSegment(sketch, "E15.20.0.0", {"start": v(46.57, 20.7) * mm, "end": v(46.57, 17.65) * mm});
            skLineSegment(sketch, "E15.20.0.1", {"start": v(46.57, 17.65) * mm, "end": v(48.7, 17.65) * mm});
            skLineSegment(sketch, "E15.20.0.2", {"start": v(48.7, 20.7) * mm, "end": v(48.7, 17.65) * mm});
            skLineSegment(sketch, "E15.21.0.0", {"start": v(48.73, 20.7) * mm, "end": v(48.73, 17.65) * mm});
            skLineSegment(sketch, "E15.21.0.1", {"start": v(48.73, 17.65) * mm, "end": v(50.86, 17.65) * mm});
            skLineSegment(sketch, "E15.21.0.2", {"start": v(50.86, 20.7) * mm, "end": v(50.86, 17.65) * mm});
            skLineSegment(sketch, "E15.22.0.0", {"start": v(50.89, 20.7) * mm, "end": v(50.89, 17.65) * mm});
            skLineSegment(sketch, "E15.22.0.1", {"start": v(50.89, 17.65) * mm, "end": v(53.02, 17.65) * mm});
            skLineSegment(sketch, "E15.22.0.2", {"start": v(53.02, 20.7) * mm, "end": v(53.02, 17.65) * mm});
            skLineSegment(sketch, "E15.23.0.0", {"start": v(53.05, 20.7) * mm, "end": v(53.05, 17.65) * mm});
            skLineSegment(sketch, "E15.23.0.1", {"start": v(53.05, 17.65) * mm, "end": v(55.18, 17.65) * mm});
            skLineSegment(sketch, "E15.23.0.2", {"start": v(55.18, 20.7) * mm, "end": v(55.18, 17.65) * mm});
            skLineSegment(sketch, "E15.24.0.0", {"start": v(55.2, 20.7) * mm, "end": v(55.2, 17.65) * mm});
            skLineSegment(sketch, "E15.24.0.1", {"start": v(55.2, 17.65) * mm, "end": v(57.34, 17.65) * mm});
            skLineSegment(sketch, "E15.24.0.2", {"start": v(57.34, 20.7) * mm, "end": v(57.34, 17.65) * mm});
            skLineSegment(sketch, "E15.25.0.0", {"start": v(57.37, 20.7) * mm, "end": v(57.37, 17.65) * mm});
            skLineSegment(sketch, "E15.25.0.1", {"start": v(57.37, 17.65) * mm, "end": v(59.5, 17.65) * mm});
            skLineSegment(sketch, "E15.25.0.2", {"start": v(59.5, 20.7) * mm, "end": v(59.5, 17.65) * mm});
            skLineSegment(sketch, "E15.26.0.0", {"start": v(59.52, 20.7) * mm, "end": v(59.52, 17.65) * mm});
            skLineSegment(sketch, "E15.26.0.1", {"start": v(59.52, 17.65) * mm, "end": v(61.66, 17.65) * mm});
            skLineSegment(sketch, "E15.26.0.2", {"start": v(61.66, 20.7) * mm, "end": v(61.66, 17.65) * mm});
            skLineSegment(sketch, "E15.27.0.0", {"start": v(61.68, 20.7) * mm, "end": v(61.68, 17.65) * mm});
            skLineSegment(sketch, "E15.27.0.1", {"start": v(61.68, 17.65) * mm, "end": v(63.82, 17.65) * mm});
            skLineSegment(sketch, "E15.27.0.2", {"start": v(63.82, 20.7) * mm, "end": v(63.82, 17.65) * mm});
            skLineSegment(sketch, "E15.28.0.0", {"start": v(63.84, 20.7) * mm, "end": v(63.84, 17.65) * mm});
            skLineSegment(sketch, "E15.28.0.1", {"start": v(63.84, 17.65) * mm, "end": v(65.98, 17.65) * mm});
            skLineSegment(sketch, "E15.28.0.2", {"start": v(65.98, 20.7) * mm, "end": v(65.98, 17.65) * mm});
            skLineSegment(sketch, "E15.29.0.0", {"start": v(66, 20.7) * mm, "end": v(66, 17.65) * mm});
            skLineSegment(sketch, "E15.29.0.1", {"start": v(66, 17.65) * mm, "end": v(68.14, 17.65) * mm});
            skLineSegment(sketch, "E15.29.0.2", {"start": v(68.14, 20.7) * mm, "end": v(68.14, 17.65) * mm});
            skLineSegment(sketch, "E15.30.0.0", {"start": v(68.16, 20.7) * mm, "end": v(68.16, 17.65) * mm});
            skLineSegment(sketch, "E15.30.0.1", {"start": v(68.16, 17.65) * mm, "end": v(70.3, 17.65) * mm});
            skLineSegment(sketch, "E15.30.0.2", {"start": v(70.3, 20.7) * mm, "end": v(70.3, 17.65) * mm});
            skLineSegment(sketch, "E15.31.0.0", {"start": v(70.32, 20.7) * mm, "end": v(70.32, 17.65) * mm});
            skLineSegment(sketch, "E15.31.0.1", {"start": v(70.32, 17.65) * mm, "end": v(72.45, 17.65) * mm});
            skLineSegment(sketch, "E15.31.0.2", {"start": v(72.45, 20.7) * mm, "end": v(72.45, 17.65) * mm});
            skLineSegment(sketch, "E15.32.0.0", {"start": v(72.48, 20.7) * mm, "end": v(72.48, 17.65) * mm});
            skLineSegment(sketch, "E15.32.0.1", {"start": v(72.48, 17.65) * mm, "end": v(74.61, 17.65) * mm});
            skLineSegment(sketch, "E15.32.0.2", {"start": v(74.61, 20.7) * mm, "end": v(74.61, 17.65) * mm});
            skLineSegment(sketch, "E15.33.0.0", {"start": v(74.64, 20.7) * mm, "end": v(74.64, 17.65) * mm});
            skLineSegment(sketch, "E15.33.0.1", {"start": v(74.64, 17.65) * mm, "end": v(76.77, 17.65) * mm});
            skLineSegment(sketch, "E15.33.0.2", {"start": v(76.77, 20.7) * mm, "end": v(76.77, 17.65) * mm});
            skLineSegment(sketch, "E15.34.0.0", {"start": v(76.8, 20.7) * mm, "end": v(76.8, 17.65) * mm});
            skLineSegment(sketch, "E15.34.0.1", {"start": v(76.8, 17.65) * mm, "end": v(78.93, 17.65) * mm});
            skLineSegment(sketch, "E15.34.0.2", {"start": v(78.93, 20.7) * mm, "end": v(78.93, 17.65) * mm});
            skLineSegment(sketch, "E15.35.0.0", {"start": v(78.96, 20.7) * mm, "end": v(78.96, 17.65) * mm});
            skLineSegment(sketch, "E15.35.0.1", {"start": v(78.96, 17.65) * mm, "end": v(81.09, 17.65) * mm});
            skLineSegment(sketch, "E15.35.0.2", {"start": v(81.09, 20.7) * mm, "end": v(81.09, 17.65) * mm});
            skLineSegment(sketch, "E15.36.0.0", {"start": v(81.11, 20.7) * mm, "end": v(81.11, 17.65) * mm});
            skLineSegment(sketch, "E15.36.0.1", {"start": v(81.11, 17.65) * mm, "end": v(83.25, 17.65) * mm});
            skLineSegment(sketch, "E15.36.0.2", {"start": v(83.25, 20.7) * mm, "end": v(83.25, 17.65) * mm});
            skLineSegment(sketch, "E15.37.0.0", {"start": v(83.27, 20.7) * mm, "end": v(83.27, 17.65) * mm});
            skLineSegment(sketch, "E15.37.0.1", {"start": v(83.27, 17.65) * mm, "end": v(85.4, 17.65) * mm});
            skLineSegment(sketch, "E15.37.0.2", {"start": v(85.4, 20.7) * mm, "end": v(85.4, 17.65) * mm});
            skLineSegment(sketch, "E15.38.0.0", {"start": v(85.43, 20.7) * mm, "end": v(85.43, 17.65) * mm});
            skLineSegment(sketch, "E15.38.0.1", {"start": v(85.43, 17.65) * mm, "end": v(87.57, 17.65) * mm});
            skLineSegment(sketch, "E15.38.0.2", {"start": v(87.57, 20.7) * mm, "end": v(87.57, 17.65) * mm});
            skLineSegment(sketch, "E15.39.0.0", {"start": v(87.6, 20.7) * mm, "end": v(87.6, 17.65) * mm});
            skLineSegment(sketch, "E15.39.0.1", {"start": v(87.6, 17.65) * mm, "end": v(89.73, 17.65) * mm});
            skLineSegment(sketch, "E15.39.0.2", {"start": v(89.73, 20.7) * mm, "end": v(89.73, 17.65) * mm});
            skLineSegment(sketch, "E15.40.0.0", {"start": v(89.75, 20.7) * mm, "end": v(89.75, 17.65) * mm});
            skLineSegment(sketch, "E15.40.0.1", {"start": v(89.75, 17.65) * mm, "end": v(91.88, 17.65) * mm});
            skLineSegment(sketch, "E15.40.0.2", {"start": v(91.88, 20.7) * mm, "end": v(91.88, 17.65) * mm});
            skLineSegment(sketch, "E15.41.0.0", {"start": v(91.9, 20.7) * mm, "end": v(91.9, 17.65) * mm});
            skLineSegment(sketch, "E15.41.0.1", {"start": v(91.9, 17.65) * mm, "end": v(94.04, 17.65) * mm});
            skLineSegment(sketch, "E15.41.0.2", {"start": v(94.04, 20.7) * mm, "end": v(94.04, 17.65) * mm});
            skLineSegment(sketch, "E15.42.0.0", {"start": v(94.07, 20.7) * mm, "end": v(94.07, 17.65) * mm});
            skLineSegment(sketch, "E15.42.0.1", {"start": v(94.07, 17.65) * mm, "end": v(96.2, 17.65) * mm});
            skLineSegment(sketch, "E15.42.0.2", {"start": v(96.2, 20.7) * mm, "end": v(96.2, 17.65) * mm});
            skLineSegment(sketch, "E15.43.0.0", {"start": v(96.23, 20.7) * mm, "end": v(96.23, 17.65) * mm});
            skLineSegment(sketch, "E15.43.0.1", {"start": v(96.23, 17.65) * mm, "end": v(98.36, 17.65) * mm});
            skLineSegment(sketch, "E15.43.0.2", {"start": v(98.36, 20.7) * mm, "end": v(98.36, 17.65) * mm});
            skLineSegment(sketch, "E15.44.0.0", {"start": v(98.39, 20.7) * mm, "end": v(98.39, 17.65) * mm});
            skLineSegment(sketch, "E15.44.0.1", {"start": v(98.39, 17.65) * mm, "end": v(100.52, 17.65) * mm});
            skLineSegment(sketch, "E15.44.0.2", {"start": v(100.52, 20.7) * mm, "end": v(100.52, 17.65) * mm});
            skLineSegment(sketch, "E15.45.0.0", {"start": v(100.55, 20.7) * mm, "end": v(100.55, 17.65) * mm});
            skLineSegment(sketch, "E15.45.0.1", {"start": v(100.55, 17.65) * mm, "end": v(102.68, 17.65) * mm});
            skLineSegment(sketch, "E15.45.0.2", {"start": v(102.68, 20.7) * mm, "end": v(102.68, 17.65) * mm});
            skLineSegment(sketch, "E15.46.0.0", {"start": v(102.7, 20.7) * mm, "end": v(102.7, 17.65) * mm});
            skLineSegment(sketch, "E15.46.0.1", {"start": v(102.7, 17.65) * mm, "end": v(104.84, 17.65) * mm});
            skLineSegment(sketch, "E15.46.0.2", {"start": v(104.84, 20.7) * mm, "end": v(104.84, 17.65) * mm});
            skLineSegment(sketch, "E15.47.0.0", {"start": v(104.86, 20.7) * mm, "end": v(104.86, 17.65) * mm});
            skLineSegment(sketch, "E15.47.0.1", {"start": v(104.86, 17.65) * mm, "end": v(107, 17.65) * mm});
            skLineSegment(sketch, "E15.47.0.2", {"start": v(107, 20.7) * mm, "end": v(107, 17.65) * mm});
            skLineSegment(sketch, "E15.48.0.0", {"start": v(107.02, 20.7) * mm, "end": v(107.02, 17.65) * mm});
            skLineSegment(sketch, "E15.48.0.1", {"start": v(107.02, 17.65) * mm, "end": v(109.16, 17.65) * mm});
            skLineSegment(sketch, "E15.48.0.2", {"start": v(109.16, 20.7) * mm, "end": v(109.16, 17.65) * mm});
            skLineSegment(sketch, "E15.49.0.0", {"start": v(109.18, 20.7) * mm, "end": v(109.18, 17.65) * mm});
            skLineSegment(sketch, "E15.49.0.1", {"start": v(109.18, 17.65) * mm, "end": v(111.32, 17.65) * mm});
            skLineSegment(sketch, "E15.49.0.2", {"start": v(111.32, 20.7) * mm, "end": v(111.32, 17.65) * mm});
            skLineSegment(sketch, "E15.50.0.0", {"start": v(111.34, 20.7) * mm, "end": v(111.34, 17.65) * mm});
            skLineSegment(sketch, "E15.50.0.1", {"start": v(111.34, 17.65) * mm, "end": v(113.47, 17.65) * mm});
            skLineSegment(sketch, "E15.50.0.2", {"start": v(113.47, 20.7) * mm, "end": v(113.47, 17.65) * mm});
            skLineSegment(sketch, "E15.51.0.0", {"start": v(113.5, 20.7) * mm, "end": v(113.5, 17.65) * mm});
            skLineSegment(sketch, "E15.51.0.1", {"start": v(113.5, 17.65) * mm, "end": v(115.63, 17.65) * mm});
            skLineSegment(sketch, "E15.51.0.2", {"start": v(115.63, 20.7) * mm, "end": v(115.63, 17.65) * mm});
            skLineSegment(sketch, "E15.52.0.0", {"start": v(115.66, 20.7) * mm, "end": v(115.66, 17.65) * mm});
            skLineSegment(sketch, "E15.52.0.1", {"start": v(115.66, 17.65) * mm, "end": v(117.8, 17.65) * mm});
            skLineSegment(sketch, "E15.52.0.2", {"start": v(117.8, 20.7) * mm, "end": v(117.8, 17.65) * mm});
            skLineSegment(sketch, "E15.53.0.0", {"start": v(117.82, 20.7) * mm, "end": v(117.82, 17.65) * mm});
            skLineSegment(sketch, "E15.53.0.1", {"start": v(117.82, 17.65) * mm, "end": v(119.95, 17.65) * mm});
            skLineSegment(sketch, "E15.53.0.2", {"start": v(119.95, 20.7) * mm, "end": v(119.95, 17.65) * mm});
            skLineSegment(sketch, "E15.54.0.0", {"start": v(119.98, 20.7) * mm, "end": v(119.98, 17.65) * mm});
            skLineSegment(sketch, "E15.54.0.1", {"start": v(119.98, 17.65) * mm, "end": v(122.11, 17.65) * mm});
            skLineSegment(sketch, "E15.54.0.2", {"start": v(122.11, 20.7) * mm, "end": v(122.11, 17.65) * mm});
            skLineSegment(sketch, "E15.55.0.0", {"start": v(122.14, 20.7) * mm, "end": v(122.14, 17.65) * mm});
            skLineSegment(sketch, "E15.55.0.1", {"start": v(122.14, 17.65) * mm, "end": v(124.27, 17.65) * mm});
            skLineSegment(sketch, "E15.55.0.2", {"start": v(124.27, 20.7) * mm, "end": v(124.27, 17.65) * mm});
            skLineSegment(sketch, "E15.56.0.0", {"start": v(124.3, 20.7) * mm, "end": v(124.3, 17.65) * mm});
            skLineSegment(sketch, "E15.56.0.1", {"start": v(124.3, 17.65) * mm, "end": v(126.43, 17.65) * mm});
            skLineSegment(sketch, "E15.56.0.2", {"start": v(126.43, 20.7) * mm, "end": v(126.43, 17.65) * mm});
            skLineSegment(sketch, "E15.57.0.0", {"start": v(126.45, 20.7) * mm, "end": v(126.45, 17.65) * mm});
            skLineSegment(sketch, "E15.57.0.1", {"start": v(126.45, 17.65) * mm, "end": v(128.59, 17.65) * mm});
            skLineSegment(sketch, "E15.57.0.2", {"start": v(128.59, 20.7) * mm, "end": v(128.59, 17.65) * mm});
            skLineSegment(sketch, "E15.58.0.0", {"start": v(128.61, 20.7) * mm, "end": v(128.61, 17.65) * mm});
            skLineSegment(sketch, "E15.58.0.1", {"start": v(128.61, 17.65) * mm, "end": v(130.75, 17.65) * mm});
            skLineSegment(sketch, "E15.58.0.2", {"start": v(130.75, 20.7) * mm, "end": v(130.75, 17.65) * mm});
            skLineSegment(sketch, "E15.59.0.0", {"start": v(130.77, 20.7) * mm, "end": v(130.77, 17.65) * mm});
            skLineSegment(sketch, "E15.59.0.1", {"start": v(130.77, 17.65) * mm, "end": v(132.9, 17.65) * mm});
            skLineSegment(sketch, "E15.59.0.2", {"start": v(132.9, 20.7) * mm, "end": v(132.9, 17.65) * mm});
            skLineSegment(sketch, "E15.60.0.0", {"start": v(132.93, 20.7) * mm, "end": v(132.93, 17.65) * mm});
            skLineSegment(sketch, "E15.60.0.1", {"start": v(132.93, 17.65) * mm, "end": v(135.06, 17.65) * mm});
            skLineSegment(sketch, "E15.60.0.2", {"start": v(135.06, 20.7) * mm, "end": v(135.06, 17.65) * mm});
            skLineSegment(sketch, "E15.61.0.0", {"start": v(135.09, 20.7) * mm, "end": v(135.09, 17.65) * mm});
            skLineSegment(sketch, "E15.61.0.1", {"start": v(135.09, 17.65) * mm, "end": v(137.22, 17.65) * mm});
            skLineSegment(sketch, "E15.61.0.2", {"start": v(137.22, 20.7) * mm, "end": v(137.22, 17.65) * mm});
            skLineSegment(sketch, "E15.62.0.0", {"start": v(137.25, 20.7) * mm, "end": v(137.25, 17.65) * mm});
            skLineSegment(sketch, "E15.62.0.1", {"start": v(137.25, 17.65) * mm, "end": v(139.38, 17.65) * mm});
            skLineSegment(sketch, "E15.62.0.2", {"start": v(139.38, 20.7) * mm, "end": v(139.38, 17.65) * mm});
            skLineSegment(sketch, "E15.63.0.0", {"start": v(139.4, 20.7) * mm, "end": v(139.4, 17.65) * mm});
            skLineSegment(sketch, "E15.63.0.1", {"start": v(139.4, 17.65) * mm, "end": v(141.54, 17.65) * mm});
            skLineSegment(sketch, "E15.63.0.2", {"start": v(141.54, 20.7) * mm, "end": v(141.54, 17.65) * mm});
            skLineSegment(sketch, "E15.64.0.0", {"start": v(141.57, 20.7) * mm, "end": v(141.57, 17.65) * mm});
            skLineSegment(sketch, "E15.64.0.1", {"start": v(141.57, 17.65) * mm, "end": v(143.7, 17.65) * mm});
            skLineSegment(sketch, "E15.64.0.2", {"start": v(143.7, 20.7) * mm, "end": v(143.7, 17.65) * mm});
            skLineSegment(sketch, "E15.65.0.0", {"start": v(143.73, 20.7) * mm, "end": v(143.73, 17.65) * mm});
            skLineSegment(sketch, "E15.65.0.1", {"start": v(143.73, 17.65) * mm, "end": v(145.86, 17.65) * mm});
            skLineSegment(sketch, "E15.65.0.2", {"start": v(145.86, 20.7) * mm, "end": v(145.86, 17.65) * mm});
            skLineSegment(sketch, "E15.66.0.0", {"start": v(145.88, 20.7) * mm, "end": v(145.88, 17.65) * mm});
            skLineSegment(sketch, "E15.66.0.1", {"start": v(145.88, 17.65) * mm, "end": v(148.02, 17.65) * mm});
            skLineSegment(sketch, "E15.66.0.2", {"start": v(148.02, 20.7) * mm, "end": v(148.02, 17.65) * mm});
            skLineSegment(sketch, "E15.67.0.0", {"start": v(148.04, 20.7) * mm, "end": v(148.04, 17.65) * mm});
            skLineSegment(sketch, "E15.67.0.1", {"start": v(148.04, 17.65) * mm, "end": v(150.18, 17.65) * mm});
            skLineSegment(sketch, "E15.67.0.2", {"start": v(150.18, 20.7) * mm, "end": v(150.18, 17.65) * mm});
            skLineSegment(sketch, "E15.68.0.0", {"start": v(150.2, 20.7) * mm, "end": v(150.2, 17.65) * mm});
            skLineSegment(sketch, "E15.68.0.1", {"start": v(150.2, 17.65) * mm, "end": v(152.34, 17.65) * mm});
            skLineSegment(sketch, "E15.68.0.2", {"start": v(152.34, 20.7) * mm, "end": v(152.34, 17.65) * mm});
            skLineSegment(sketch, "E15.69.0.0", {"start": v(152.36, 20.7) * mm, "end": v(152.36, 17.65) * mm});
            skLineSegment(sketch, "E15.69.0.1", {"start": v(152.36, 17.65) * mm, "end": v(154.5, 17.65) * mm});
            skLineSegment(sketch, "E15.69.0.2", {"start": v(154.5, 20.7) * mm, "end": v(154.5, 17.65) * mm});
            skLineSegment(sketch, "E15.70.0.0", {"start": v(154.52, 20.7) * mm, "end": v(154.52, 17.65) * mm});
            skLineSegment(sketch, "E15.70.0.1", {"start": v(154.52, 17.65) * mm, "end": v(156.65, 17.65) * mm});
            skLineSegment(sketch, "E15.70.0.2", {"start": v(156.65, 20.7) * mm, "end": v(156.65, 17.65) * mm});
            skLineSegment(sketch, "E15.71.0.0", {"start": v(156.68, 20.7) * mm, "end": v(156.68, 17.65) * mm});
            skLineSegment(sketch, "E15.71.0.1", {"start": v(156.68, 17.65) * mm, "end": v(158.81, 17.65) * mm});
            skLineSegment(sketch, "E15.71.0.2", {"start": v(158.81, 20.7) * mm, "end": v(158.81, 17.65) * mm});
            skLineSegment(sketch, "E15.72.0.0", {"start": v(158.84, 20.7) * mm, "end": v(158.84, 17.65) * mm});
            skLineSegment(sketch, "E15.72.0.1", {"start": v(158.84, 17.65) * mm, "end": v(160.97, 17.65) * mm});
            skLineSegment(sketch, "E15.72.0.2", {"start": v(160.97, 20.7) * mm, "end": v(160.97, 17.65) * mm});
            skLineSegment(sketch, "E15.73.0.0", {"start": v(161, 20.7) * mm, "end": v(161, 17.65) * mm});
            skLineSegment(sketch, "E15.73.0.1", {"start": v(161, 17.65) * mm, "end": v(163.13, 17.65) * mm});
            skLineSegment(sketch, "E15.73.0.2", {"start": v(163.13, 20.7) * mm, "end": v(163.13, 17.65) * mm});
            skLineSegment(sketch, "E15.74.0.0", {"start": v(163.16, 20.7) * mm, "end": v(163.16, 17.65) * mm});
            skLineSegment(sketch, "E15.74.0.1", {"start": v(163.16, 17.65) * mm, "end": v(165.3, 17.65) * mm});
            skLineSegment(sketch, "E15.74.0.2", {"start": v(165.3, 20.7) * mm, "end": v(165.3, 17.65) * mm});
            skLineSegment(sketch, "E15.75.0.0", {"start": v(165.32, 20.7) * mm, "end": v(165.32, 17.65) * mm});
            skLineSegment(sketch, "E15.75.0.1", {"start": v(165.32, 17.65) * mm, "end": v(167.45, 17.65) * mm});
            skLineSegment(sketch, "E15.75.0.2", {"start": v(167.45, 20.7) * mm, "end": v(167.45, 17.65) * mm});
            skLineSegment(sketch, "E15.76.0.0", {"start": v(167.47, 20.7) * mm, "end": v(167.47, 17.65) * mm});
            skLineSegment(sketch, "E15.76.0.1", {"start": v(167.47, 17.65) * mm, "end": v(169.6, 17.65) * mm});
            skLineSegment(sketch, "E15.76.0.2", {"start": v(169.6, 20.7) * mm, "end": v(169.6, 17.65) * mm});
            skLineSegment(sketch, "E15.77.0.0", {"start": v(169.63, 20.7) * mm, "end": v(169.63, 17.65) * mm});
            skLineSegment(sketch, "E15.77.0.1", {"start": v(169.63, 17.65) * mm, "end": v(171.77, 17.65) * mm});
            skLineSegment(sketch, "E15.77.0.2", {"start": v(171.77, 20.7) * mm, "end": v(171.77, 17.65) * mm});
            skLineSegment(sketch, "E15.78.0.0", {"start": v(171.8, 20.7) * mm, "end": v(171.8, 17.65) * mm});
            skLineSegment(sketch, "E15.78.0.1", {"start": v(171.8, 17.65) * mm, "end": v(173.93, 17.65) * mm});
            skLineSegment(sketch, "E15.78.0.2", {"start": v(173.93, 20.7) * mm, "end": v(173.93, 17.65) * mm});
            skLineSegment(sketch, "E15.79.0.0", {"start": v(173.95, 20.7) * mm, "end": v(173.95, 17.65) * mm});
            skLineSegment(sketch, "E15.79.0.1", {"start": v(173.95, 17.65) * mm, "end": v(176.09, 17.65) * mm});
            skLineSegment(sketch, "E15.79.0.2", {"start": v(176.09, 20.7) * mm, "end": v(176.09, 17.65) * mm});
            skLineSegment(sketch, "E15.80.0.0", {"start": v(176.11, 20.7) * mm, "end": v(176.11, 17.65) * mm});
            skLineSegment(sketch, "E15.80.0.1", {"start": v(176.11, 17.65) * mm, "end": v(178.24, 17.65) * mm});
            skLineSegment(sketch, "E15.80.0.2", {"start": v(178.24, 20.7) * mm, "end": v(178.24, 17.65) * mm});
            skLineSegment(sketch, "E15.81.0.0", {"start": v(178.27, 20.7) * mm, "end": v(178.27, 17.65) * mm});
            skLineSegment(sketch, "E15.81.0.1", {"start": v(178.27, 17.65) * mm, "end": v(180.4, 17.65) * mm});
            skLineSegment(sketch, "E15.81.0.2", {"start": v(180.4, 20.7) * mm, "end": v(180.4, 17.65) * mm});
            skLineSegment(sketch, "E15.82.0.0", {"start": v(180.43, 20.7) * mm, "end": v(180.43, 17.65) * mm});
            skLineSegment(sketch, "E15.82.0.1", {"start": v(180.43, 17.65) * mm, "end": v(182.56, 17.65) * mm});
            skLineSegment(sketch, "E15.82.0.2", {"start": v(182.56, 20.7) * mm, "end": v(182.56, 17.65) * mm});
            skLineSegment(sketch, "E15.83.0.0", {"start": v(182.59, 20.7) * mm, "end": v(182.59, 17.65) * mm});
            skLineSegment(sketch, "E15.83.0.1", {"start": v(182.59, 17.65) * mm, "end": v(184.72, 17.65) * mm});
            skLineSegment(sketch, "E15.83.0.2", {"start": v(184.72, 20.7) * mm, "end": v(184.72, 17.65) * mm});
            skLineSegment(sketch, "E15.84.0.0", {"start": v(184.75, 20.7) * mm, "end": v(184.75, 17.65) * mm});
            skLineSegment(sketch, "E15.84.0.1", {"start": v(184.75, 17.65) * mm, "end": v(186.88, 17.65) * mm});
            skLineSegment(sketch, "E15.84.0.2", {"start": v(186.88, 20.7) * mm, "end": v(186.88, 17.65) * mm});
            skLineSegment(sketch, "E15.85.0.0", {"start": v(186.9, 20.7) * mm, "end": v(186.9, 17.65) * mm});
            skLineSegment(sketch, "E15.85.0.1", {"start": v(186.9, 17.65) * mm, "end": v(189.04, 17.65) * mm});
            skLineSegment(sketch, "E15.85.0.2", {"start": v(189.04, 20.7) * mm, "end": v(189.04, 17.65) * mm});
            skLineSegment(sketch, "E15.86.0.0", {"start": v(189.06, 20.7) * mm, "end": v(189.06, 17.65) * mm});
            skLineSegment(sketch, "E15.86.0.1", {"start": v(189.06, 17.65) * mm, "end": v(191.2, 17.65) * mm});
            skLineSegment(sketch, "E15.86.0.2", {"start": v(191.2, 20.7) * mm, "end": v(191.2, 17.65) * mm});
            skLineSegment(sketch, "E15.87.0.0", {"start": v(191.22, 20.7) * mm, "end": v(191.22, 17.65) * mm});
            skLineSegment(sketch, "E15.87.0.1", {"start": v(191.22, 17.65) * mm, "end": v(193.36, 17.65) * mm});
            skLineSegment(sketch, "E15.87.0.2", {"start": v(193.36, 20.7) * mm, "end": v(193.36, 17.65) * mm});
            skLineSegment(sketch, "E15.88.0.0", {"start": v(193.38, 20.7) * mm, "end": v(193.38, 17.65) * mm});
            skLineSegment(sketch, "E15.88.0.1", {"start": v(193.38, 17.65) * mm, "end": v(195.52, 17.65) * mm});
            skLineSegment(sketch, "E15.88.0.2", {"start": v(195.52, 20.7) * mm, "end": v(195.52, 17.65) * mm});
            skLineSegment(sketch, "E15.89.0.0", {"start": v(195.54, 20.7) * mm, "end": v(195.54, 17.65) * mm});
            skLineSegment(sketch, "E15.89.0.1", {"start": v(195.54, 17.65) * mm, "end": v(197.68, 17.65) * mm});
            skLineSegment(sketch, "E15.89.0.2", {"start": v(197.68, 20.7) * mm, "end": v(197.68, 17.65) * mm});
            skLineSegment(sketch, "E15.90.0.0", {"start": v(197.7, 20.7) * mm, "end": v(197.7, 17.65) * mm});
            skLineSegment(sketch, "E15.90.0.1", {"start": v(197.7, 17.65) * mm, "end": v(199.83, 17.65) * mm});
            skLineSegment(sketch, "E15.90.0.2", {"start": v(199.83, 20.7) * mm, "end": v(199.83, 17.65) * mm});
            skLineSegment(sketch, "E15.91.0.0", {"start": v(199.86, 20.7) * mm, "end": v(199.86, 17.65) * mm});
            skLineSegment(sketch, "E15.91.0.1", {"start": v(199.86, 17.65) * mm, "end": v(202, 17.65) * mm});
            skLineSegment(sketch, "E15.91.0.2", {"start": v(202, 20.7) * mm, "end": v(202, 17.65) * mm});
            skLineSegment(sketch, "E15.92.0.0", {"start": v(202.02, 20.7) * mm, "end": v(202.02, 17.65) * mm});
            skLineSegment(sketch, "E15.92.0.1", {"start": v(202.02, 17.65) * mm, "end": v(204.15, 17.65) * mm});
            skLineSegment(sketch, "E15.92.0.2", {"start": v(204.15, 20.7) * mm, "end": v(204.15, 17.65) * mm});
            skLineSegment(sketch, "E15.93.0.0", {"start": v(204.18, 20.7) * mm, "end": v(204.18, 17.65) * mm});
            skLineSegment(sketch, "E15.93.0.1", {"start": v(204.18, 17.65) * mm, "end": v(206.31, 17.65) * mm});
            skLineSegment(sketch, "E15.93.0.2", {"start": v(206.31, 20.7) * mm, "end": v(206.31, 17.65) * mm});
            skLineSegment(sketch, "E15.94.0.0", {"start": v(206.34, 20.7) * mm, "end": v(206.34, 17.65) * mm});
            skLineSegment(sketch, "E15.94.0.1", {"start": v(206.34, 17.65) * mm, "end": v(208.47, 17.65) * mm});
            skLineSegment(sketch, "E15.94.0.2", {"start": v(208.47, 20.7) * mm, "end": v(208.47, 17.65) * mm});
            skLineSegment(sketch, "E15.95.0.0", {"start": v(208.5, 20.7) * mm, "end": v(208.5, 17.65) * mm});
            skLineSegment(sketch, "E15.95.0.1", {"start": v(208.5, 17.65) * mm, "end": v(210.63, 17.65) * mm});
            skLineSegment(sketch, "E15.95.0.2", {"start": v(210.63, 20.7) * mm, "end": v(210.63, 17.65) * mm});
            skLineSegment(sketch, "E15.96.0.0", {"start": v(210.65, 20.7) * mm, "end": v(210.65, 17.65) * mm});
            skLineSegment(sketch, "E15.96.0.1", {"start": v(210.65, 17.65) * mm, "end": v(212.79, 17.65) * mm});
            skLineSegment(sketch, "E15.96.0.2", {"start": v(212.79, 20.7) * mm, "end": v(212.79, 17.65) * mm});
            skLineSegment(sketch, "E15.97.0.0", {"start": v(212.81, 20.7) * mm, "end": v(212.81, 17.65) * mm});
            skLineSegment(sketch, "E15.97.0.1", {"start": v(212.81, 17.65) * mm, "end": v(214.95, 17.65) * mm});
            skLineSegment(sketch, "E15.97.0.2", {"start": v(214.95, 20.7) * mm, "end": v(214.95, 17.65) * mm});
            skLineSegment(sketch, "E15.98.0.0", {"start": v(214.97, 20.7) * mm, "end": v(214.97, 17.65) * mm});
            skLineSegment(sketch, "E15.98.0.1", {"start": v(214.97, 17.65) * mm, "end": v(217.1, 17.65) * mm});
            skLineSegment(sketch, "E15.98.0.2", {"start": v(217.1, 20.7) * mm, "end": v(217.1, 17.65) * mm});
            skLineSegment(sketch, "E15.99.0.0", {"start": v(217.13, 20.7) * mm, "end": v(217.13, 17.65) * mm});
            skLineSegment(sketch, "E15.99.0.1", {"start": v(217.13, 17.65) * mm, "end": v(219.27, 17.65) * mm});
            skLineSegment(sketch, "E15.99.0.2", {"start": v(219.27, 20.7) * mm, "end": v(219.27, 17.65) * mm});
            skLineSegment(sketch, "E15.direction1", {"start": v(3.4, 17.65) * mm, "end": v(5.55, 17.65) * mm, "construction": true});
            skSolve(sketch);
        }
        {
            var Q0;
            {var subQ0=sQuery(id+"F15.wireOp",EDGE,"E15.2.0.0");Q0=makeQuery(id+"F15.imprint","IMPRINT",FACE,{"disambiguationData":[TD([[makeQuery(id+"F15.imprint","IMPRINT",EDGE,{"derivedFrom":subQ0}),1.0]])]});}
            var Q1;
            {var subQ0=sQuery(id+"F15.wireOp",EDGE,"E15.4.0.0");Q1=makeQuery(id+"F15.imprint","IMPRINT",FACE,{"disambiguationData":[TD([[makeQuery(id+"F15.imprint","IMPRINT",EDGE,{"derivedFrom":subQ0}),1.0]])]});}
            var Q2;
            {var subQ0=sQuery(id+"F15.wireOp",EDGE,"E15.6.0.0");Q2=makeQuery(id+"F15.imprint","IMPRINT",FACE,{"disambiguationData":[TD([[makeQuery(id+"F15.imprint","IMPRINT",EDGE,{"derivedFrom":subQ0}),1.0]])]});}
            var Q3;
            {var subQ0=sQuery(id+"F15.wireOp",EDGE,"E15.8.0.0");Q3=makeQuery(id+"F15.imprint","IMPRINT",FACE,{"disambiguationData":[TD([[makeQuery(id+"F15.imprint","IMPRINT",EDGE,{"derivedFrom":subQ0}),1.0]])]});}
            var Q4;
            {var subQ0=sQuery(id+"F15.wireOp",EDGE,"E15.10.0.0");Q4=makeQuery(id+"F15.imprint","IMPRINT",FACE,{"disambiguationData":[TD([[makeQuery(id+"F15.imprint","IMPRINT",EDGE,{"derivedFrom":subQ0}),1.0]])]});}
            var Q5;
            {var subQ0=sQuery(id+"F15.wireOp",EDGE,"E15.12.0.0");Q5=makeQuery(id+"F15.imprint","IMPRINT",FACE,{"disambiguationData":[TD([[makeQuery(id+"F15.imprint","IMPRINT",EDGE,{"derivedFrom":subQ0}),1.0]])]});}
            var Q6;
            {var subQ0=sQuery(id+"F15.wireOp",EDGE,"E15.14.0.0");Q6=makeQuery(id+"F15.imprint","IMPRINT",FACE,{"disambiguationData":[TD([[makeQuery(id+"F15.imprint","IMPRINT",EDGE,{"derivedFrom":subQ0}),1.0]])]});}
            var Q7;
            {var subQ0=sQuery(id+"F15.wireOp",EDGE,"E15.16.0.0");Q7=makeQuery(id+"F15.imprint","IMPRINT",FACE,{"disambiguationData":[TD([[makeQuery(id+"F15.imprint","IMPRINT",EDGE,{"derivedFrom":subQ0}),1.0]])]});}
            var Q8;
            {var subQ0=sQuery(id+"F15.wireOp",EDGE,"E15.18.0.0");Q8=makeQuery(id+"F15.imprint","IMPRINT",FACE,{"disambiguationData":[TD([[makeQuery(id+"F15.imprint","IMPRINT",EDGE,{"derivedFrom":subQ0}),1.0]])]});}
            var Q9;
            {var subQ0=sQuery(id+"F15.wireOp",EDGE,"E15.20.0.0");Q9=makeQuery(id+"F15.imprint","IMPRINT",FACE,{"disambiguationData":[TD([[makeQuery(id+"F15.imprint","IMPRINT",EDGE,{"derivedFrom":subQ0}),1.0]])]});}
            var Q10;
            {var subQ0=sQuery(id+"F15.wireOp",EDGE,"E15.22.0.0");Q10=makeQuery(id+"F15.imprint","IMPRINT",FACE,{"disambiguationData":[TD([[makeQuery(id+"F15.imprint","IMPRINT",EDGE,{"derivedFrom":subQ0}),1.0]])]});}
            var Q11;
            {var subQ0=sQuery(id+"F15.wireOp",EDGE,"E15.24.0.0");Q11=makeQuery(id+"F15.imprint","IMPRINT",FACE,{"disambiguationData":[TD([[makeQuery(id+"F15.imprint","IMPRINT",EDGE,{"derivedFrom":subQ0}),1.0]])]});}
            var Q12;
            {var subQ0=sQuery(id+"F15.wireOp",EDGE,"E15.26.0.0");Q12=makeQuery(id+"F15.imprint","IMPRINT",FACE,{"disambiguationData":[TD([[makeQuery(id+"F15.imprint","IMPRINT",EDGE,{"derivedFrom":subQ0}),1.0]])]});}
            var Q13;
            {var subQ0=sQuery(id+"F15.wireOp",EDGE,"E15.28.0.0");Q13=makeQuery(id+"F15.imprint","IMPRINT",FACE,{"disambiguationData":[TD([[makeQuery(id+"F15.imprint","IMPRINT",EDGE,{"derivedFrom":subQ0}),1.0]])]});}
            var Q14;
            {var subQ0=sQuery(id+"F15.wireOp",EDGE,"E15.30.0.0");Q14=makeQuery(id+"F15.imprint","IMPRINT",FACE,{"disambiguationData":[TD([[makeQuery(id+"F15.imprint","IMPRINT",EDGE,{"derivedFrom":subQ0}),1.0]])]});}
            var Q15;
            {var subQ0=sQuery(id+"F15.wireOp",EDGE,"E15.32.0.0");Q15=makeQuery(id+"F15.imprint","IMPRINT",FACE,{"disambiguationData":[TD([[makeQuery(id+"F15.imprint","IMPRINT",EDGE,{"derivedFrom":subQ0}),1.0]])]});}
            var Q16;
            {var subQ0=sQuery(id+"F15.wireOp",EDGE,"E15.34.0.0");Q16=makeQuery(id+"F15.imprint","IMPRINT",FACE,{"disambiguationData":[TD([[makeQuery(id+"F15.imprint","IMPRINT",EDGE,{"derivedFrom":subQ0}),1.0]])]});}
            var Q17;
            {var subQ0=sQuery(id+"F15.wireOp",EDGE,"E15.36.0.0");Q17=makeQuery(id+"F15.imprint","IMPRINT",FACE,{"disambiguationData":[TD([[makeQuery(id+"F15.imprint","IMPRINT",EDGE,{"derivedFrom":subQ0}),1.0]])]});}
            var Q18;
            {var subQ0=sQuery(id+"F15.wireOp",EDGE,"E15.38.0.0");Q18=makeQuery(id+"F15.imprint","IMPRINT",FACE,{"disambiguationData":[TD([[makeQuery(id+"F15.imprint","IMPRINT",EDGE,{"derivedFrom":subQ0}),1.0]])]});}
            var Q19;
            {var subQ0=sQuery(id+"F15.wireOp",EDGE,"E15.40.0.0");Q19=makeQuery(id+"F15.imprint","IMPRINT",FACE,{"disambiguationData":[TD([[makeQuery(id+"F15.imprint","IMPRINT",EDGE,{"derivedFrom":subQ0}),1.0]])]});}
            var Q20;
            {var subQ0=sQuery(id+"F15.wireOp",EDGE,"E15.42.0.0");Q20=makeQuery(id+"F15.imprint","IMPRINT",FACE,{"disambiguationData":[TD([[makeQuery(id+"F15.imprint","IMPRINT",EDGE,{"derivedFrom":subQ0}),1.0]])]});}
            var Q21;
            {var subQ0=sQuery(id+"F15.wireOp",EDGE,"E15.44.0.0");Q21=makeQuery(id+"F15.imprint","IMPRINT",FACE,{"disambiguationData":[TD([[makeQuery(id+"F15.imprint","IMPRINT",EDGE,{"derivedFrom":subQ0}),1.0]])]});}
            var Q22;
            {var subQ0=sQuery(id+"F15.wireOp",EDGE,"E15.46.0.0");Q22=makeQuery(id+"F15.imprint","IMPRINT",FACE,{"disambiguationData":[TD([[makeQuery(id+"F15.imprint","IMPRINT",EDGE,{"derivedFrom":subQ0}),1.0]])]});}
            var Q23;
            {var subQ0=sQuery(id+"F15.wireOp",EDGE,"E15.48.0.0");Q23=makeQuery(id+"F15.imprint","IMPRINT",FACE,{"disambiguationData":[TD([[makeQuery(id+"F15.imprint","IMPRINT",EDGE,{"derivedFrom":subQ0}),1.0]])]});}
            var Q24;
            {var subQ0=sQuery(id+"F15.wireOp",EDGE,"E15.50.0.0");Q24=makeQuery(id+"F15.imprint","IMPRINT",FACE,{"disambiguationData":[TD([[makeQuery(id+"F15.imprint","IMPRINT",EDGE,{"derivedFrom":subQ0}),1.0]])]});}
            var Q25;
            {var subQ0=sQuery(id+"F15.wireOp",EDGE,"E15.52.0.0");Q25=makeQuery(id+"F15.imprint","IMPRINT",FACE,{"disambiguationData":[TD([[makeQuery(id+"F15.imprint","IMPRINT",EDGE,{"derivedFrom":subQ0}),1.0]])]});}
            var Q26;
            {var subQ0=sQuery(id+"F15.wireOp",EDGE,"E15.54.0.0");Q26=makeQuery(id+"F15.imprint","IMPRINT",FACE,{"disambiguationData":[TD([[makeQuery(id+"F15.imprint","IMPRINT",EDGE,{"derivedFrom":subQ0}),1.0]])]});}
            var Q27;
            {var subQ0=sQuery(id+"F15.wireOp",EDGE,"E15.56.0.0");Q27=makeQuery(id+"F15.imprint","IMPRINT",FACE,{"disambiguationData":[TD([[makeQuery(id+"F15.imprint","IMPRINT",EDGE,{"derivedFrom":subQ0}),1.0]])]});}
            var Q28;
            {var subQ0=sQuery(id+"F15.wireOp",EDGE,"E15.58.0.0");Q28=makeQuery(id+"F15.imprint","IMPRINT",FACE,{"disambiguationData":[TD([[makeQuery(id+"F15.imprint","IMPRINT",EDGE,{"derivedFrom":subQ0}),1.0]])]});}
            var Q29;
            {var subQ0=sQuery(id+"F15.wireOp",EDGE,"E15.60.0.0");Q29=makeQuery(id+"F15.imprint","IMPRINT",FACE,{"disambiguationData":[TD([[makeQuery(id+"F15.imprint","IMPRINT",EDGE,{"derivedFrom":subQ0}),1.0]])]});}
            var Q30;
            {var subQ0=sQuery(id+"F15.wireOp",EDGE,"E15.62.0.0");Q30=makeQuery(id+"F15.imprint","IMPRINT",FACE,{"disambiguationData":[TD([[makeQuery(id+"F15.imprint","IMPRINT",EDGE,{"derivedFrom":subQ0}),1.0]])]});}
            var Q31;
            {var subQ0=sQuery(id+"F15.wireOp",EDGE,"E15.64.0.0");Q31=makeQuery(id+"F15.imprint","IMPRINT",FACE,{"disambiguationData":[TD([[makeQuery(id+"F15.imprint","IMPRINT",EDGE,{"derivedFrom":subQ0}),1.0]])]});}
            var Q32;
            {var subQ0=sQuery(id+"F15.wireOp",EDGE,"E15.66.0.0");Q32=makeQuery(id+"F15.imprint","IMPRINT",FACE,{"disambiguationData":[TD([[makeQuery(id+"F15.imprint","IMPRINT",EDGE,{"derivedFrom":subQ0}),1.0]])]});}
            var Q33;
            {var subQ0=sQuery(id+"F15.wireOp",EDGE,"E15.68.0.0");Q33=makeQuery(id+"F15.imprint","IMPRINT",FACE,{"disambiguationData":[TD([[makeQuery(id+"F15.imprint","IMPRINT",EDGE,{"derivedFrom":subQ0}),1.0]])]});}
            var Q34;
            {var subQ0=sQuery(id+"F15.wireOp",EDGE,"E15.70.0.0");Q34=makeQuery(id+"F15.imprint","IMPRINT",FACE,{"disambiguationData":[TD([[makeQuery(id+"F15.imprint","IMPRINT",EDGE,{"derivedFrom":subQ0}),1.0]])]});}
            var Q35;
            {var subQ0=sQuery(id+"F15.wireOp",EDGE,"E15.72.0.0");Q35=makeQuery(id+"F15.imprint","IMPRINT",FACE,{"disambiguationData":[TD([[makeQuery(id+"F15.imprint","IMPRINT",EDGE,{"derivedFrom":subQ0}),1.0]])]});}
            var Q36;
            {var subQ0=sQuery(id+"F15.wireOp",EDGE,"E15.74.0.0");Q36=makeQuery(id+"F15.imprint","IMPRINT",FACE,{"disambiguationData":[TD([[makeQuery(id+"F15.imprint","IMPRINT",EDGE,{"derivedFrom":subQ0}),1.0]])]});}
            var Q37;
            {var subQ0=sQuery(id+"F15.wireOp",EDGE,"E15.76.0.0");Q37=makeQuery(id+"F15.imprint","IMPRINT",FACE,{"disambiguationData":[TD([[makeQuery(id+"F15.imprint","IMPRINT",EDGE,{"derivedFrom":subQ0}),1.0]])]});}
            var Q38;
            {var subQ0=sQuery(id+"F15.wireOp",EDGE,"E15.78.0.0");Q38=makeQuery(id+"F15.imprint","IMPRINT",FACE,{"disambiguationData":[TD([[makeQuery(id+"F15.imprint","IMPRINT",EDGE,{"derivedFrom":subQ0}),1.0]])]});}
            var Q39;
            {var subQ0=sQuery(id+"F15.wireOp",EDGE,"E15.60.0.0");Q39=makeQuery(id+"F15.imprint","IMPRINT",FACE,{"disambiguationData":[TD([[makeQuery(id+"F15.imprint","IMPRINT",EDGE,{"derivedFrom":subQ0}),1.0]])]});}
            var Q40;
            {var subQ0=sQuery(id+"F15.wireOp",EDGE,"E15.62.0.0");Q40=makeQuery(id+"F15.imprint","IMPRINT",FACE,{"disambiguationData":[TD([[makeQuery(id+"F15.imprint","IMPRINT",EDGE,{"derivedFrom":subQ0}),1.0]])]});}
            var Q41;
            {var subQ0=sQuery(id+"F15.wireOp",EDGE,"E15.64.0.0");Q41=makeQuery(id+"F15.imprint","IMPRINT",FACE,{"disambiguationData":[TD([[makeQuery(id+"F15.imprint","IMPRINT",EDGE,{"derivedFrom":subQ0}),1.0]])]});}
            var Q42;
            {var subQ0=sQuery(id+"F15.wireOp",EDGE,"E15.66.0.0");Q42=makeQuery(id+"F15.imprint","IMPRINT",FACE,{"disambiguationData":[TD([[makeQuery(id+"F15.imprint","IMPRINT",EDGE,{"derivedFrom":subQ0}),1.0]])]});}
            var Q43;
            {var subQ0=sQuery(id+"F15.wireOp",EDGE,"E15.68.0.0");Q43=makeQuery(id+"F15.imprint","IMPRINT",FACE,{"disambiguationData":[TD([[makeQuery(id+"F15.imprint","IMPRINT",EDGE,{"derivedFrom":subQ0}),1.0]])]});}
            var Q44;
            {var subQ0=sQuery(id+"F15.wireOp",EDGE,"E15.70.0.0");Q44=makeQuery(id+"F15.imprint","IMPRINT",FACE,{"disambiguationData":[TD([[makeQuery(id+"F15.imprint","IMPRINT",EDGE,{"derivedFrom":subQ0}),1.0]])]});}
            var Q45;
            {var subQ0=sQuery(id+"F15.wireOp",EDGE,"E15.72.0.0");Q45=makeQuery(id+"F15.imprint","IMPRINT",FACE,{"disambiguationData":[TD([[makeQuery(id+"F15.imprint","IMPRINT",EDGE,{"derivedFrom":subQ0}),1.0]])]});}
            var Q46;
            {var subQ0=sQuery(id+"F15.wireOp",EDGE,"E15.74.0.0");Q46=makeQuery(id+"F15.imprint","IMPRINT",FACE,{"disambiguationData":[TD([[makeQuery(id+"F15.imprint","IMPRINT",EDGE,{"derivedFrom":subQ0}),1.0]])]});}
            var Q47;
            {var subQ0=sQuery(id+"F15.wireOp",EDGE,"E15.76.0.0");Q47=makeQuery(id+"F15.imprint","IMPRINT",FACE,{"disambiguationData":[TD([[makeQuery(id+"F15.imprint","IMPRINT",EDGE,{"derivedFrom":subQ0}),1.0]])]});}
            var Q48;
            {var subQ0=sQuery(id+"F15.wireOp",EDGE,"E15.78.0.0");Q48=makeQuery(id+"F15.imprint","IMPRINT",FACE,{"disambiguationData":[TD([[makeQuery(id+"F15.imprint","IMPRINT",EDGE,{"derivedFrom":subQ0}),1.0]])]});}
            var Q49;
            {var subQ0=sQuery(id+"F15.wireOp",EDGE,"E15.80.0.0");Q49=makeQuery(id+"F15.imprint","IMPRINT",FACE,{"disambiguationData":[TD([[makeQuery(id+"F15.imprint","IMPRINT",EDGE,{"derivedFrom":subQ0}),1.0]])]});}
            var Q50;
            {var subQ0=sQuery(id+"F15.wireOp",EDGE,"E15.82.0.0");Q50=makeQuery(id+"F15.imprint","IMPRINT",FACE,{"disambiguationData":[TD([[makeQuery(id+"F15.imprint","IMPRINT",EDGE,{"derivedFrom":subQ0}),1.0]])]});}
            var Q51;
            {var subQ0=sQuery(id+"F15.wireOp",EDGE,"E15.84.0.0");Q51=makeQuery(id+"F15.imprint","IMPRINT",FACE,{"disambiguationData":[TD([[makeQuery(id+"F15.imprint","IMPRINT",EDGE,{"derivedFrom":subQ0}),1.0]])]});}
            var Q52;
            {var subQ0=sQuery(id+"F15.wireOp",EDGE,"E15.86.0.0");Q52=makeQuery(id+"F15.imprint","IMPRINT",FACE,{"disambiguationData":[TD([[makeQuery(id+"F15.imprint","IMPRINT",EDGE,{"derivedFrom":subQ0}),1.0]])]});}
            var Q53;
            {var subQ0=sQuery(id+"F15.wireOp",EDGE,"E15.88.0.0");Q53=makeQuery(id+"F15.imprint","IMPRINT",FACE,{"disambiguationData":[TD([[makeQuery(id+"F15.imprint","IMPRINT",EDGE,{"derivedFrom":subQ0}),1.0]])]});}
            var Q54;
            {var subQ0=sQuery(id+"F15.wireOp",EDGE,"E15.90.0.0");Q54=makeQuery(id+"F15.imprint","IMPRINT",FACE,{"disambiguationData":[TD([[makeQuery(id+"F15.imprint","IMPRINT",EDGE,{"derivedFrom":subQ0}),1.0]])]});}
            var Q55;
            {var subQ0=sQuery(id+"F15.wireOp",EDGE,"E15.92.0.0");Q55=makeQuery(id+"F15.imprint","IMPRINT",FACE,{"disambiguationData":[TD([[makeQuery(id+"F15.imprint","IMPRINT",EDGE,{"derivedFrom":subQ0}),1.0]])]});}
            var Q56;
            {var subQ0=sQuery(id+"F15.wireOp",EDGE,"E15.94.0.0");Q56=makeQuery(id+"F15.imprint","IMPRINT",FACE,{"disambiguationData":[TD([[makeQuery(id+"F15.imprint","IMPRINT",EDGE,{"derivedFrom":subQ0}),1.0]])]});}
            var Q57;
            {var subQ0=sQuery(id+"F15.wireOp",EDGE,"E15.96.0.0");Q57=makeQuery(id+"F15.imprint","IMPRINT",FACE,{"disambiguationData":[TD([[makeQuery(id+"F15.imprint","IMPRINT",EDGE,{"derivedFrom":subQ0}),1.0]])]});}
            var Q58;
            {var subQ0=sQuery(id+"F15.wireOp",EDGE,"E15.98.0.0");Q58=makeQuery(id+"F15.imprint","IMPRINT",FACE,{"disambiguationData":[TD([[makeQuery(id+"F15.imprint","IMPRINT",EDGE,{"derivedFrom":subQ0}),1.0]])]});}
            extrude(context, id + "F16", {"entities" : qUnion([Q0, Q1, Q2, Q3, Q4, Q5, Q6, Q7, Q8, Q9, Q10, Q11, Q12, Q13, Q14, Q15, Q16, Q17, Q18, Q19, Q20, Q21, Q22, Q23, Q24, Q25, Q26, Q27, Q28, Q29, Q30, Q31, Q32, Q33, Q34, Q35, Q36, Q37, Q38, Q39, Q40, Q41, Q42, Q43, Q44, Q45, Q46, Q47, Q48, Q49, Q50, Q51, Q52, Q53, Q54, Q55, Q56, Q57, Q58]), "operationType" : NewBodyOperationType.REMOVE, "endBound" : BoundingType.UP_TO_NEXT, "oppositeDirection" : true, "depth" : 25.4 * mm});
        }
        {
            var Q0;
            Q0=makeQuery(id+"F1.opExtrude","SWEPT_FACE",FACE,{"disambiguationData":[OSD([sQuery(id+"F0.wireOp",EDGE,"E0.top")])]});
            var sketch = newSketch(context, id + "F17", { "sketchPlane" : qUnion([Q0])});
            skLineSegment(sketch, "E16.0", {"start": v(214.97, 20.7) * mm, "end": v(214.97, 17.65) * mm});
            skLineSegment(sketch, "E17.0", {"start": v(217.1, 20.7) * mm, "end": v(217.1, 17.65) * mm});
            skLineSegment(sketch, "E18.0", {"start": v(214.97, 17.65) * mm, "end": v(217.1, 17.65) * mm});
            skLineSegment(sketch, "E19.1.0.0", {"start": v(217.13, 20.7) * mm, "end": v(217.13, 17.65) * mm});
            skLineSegment(sketch, "E19.1.0.1", {"start": v(217.13, 17.65) * mm, "end": v(219.27, 17.65) * mm});
            skLineSegment(sketch, "E19.1.0.2", {"start": v(219.27, 20.7) * mm, "end": v(219.27, 17.65) * mm});
            skLineSegment(sketch, "E19.2.0.0", {"start": v(219.3, 20.7) * mm, "end": v(219.3, 17.65) * mm});
            skLineSegment(sketch, "E19.2.0.1", {"start": v(219.3, 17.65) * mm, "end": v(221.42, 17.65) * mm});
            skLineSegment(sketch, "E19.2.0.2", {"start": v(221.42, 20.7) * mm, "end": v(221.42, 17.65) * mm});
            skLineSegment(sketch, "E19.direction1", {"start": v(214.97, 17.65) * mm, "end": v(217.13, 17.65) * mm, "construction": true});
            skSolve(sketch);
        }
        {
            var Q0;
            {var subQ0=sQuery(id+"F17.wireOp",EDGE,"E19.2.0.0");Q0=makeQuery(id+"F17.imprint","IMPRINT",FACE,{"disambiguationData":[TD([[makeQuery(id+"F17.imprint","IMPRINT",EDGE,{"derivedFrom":subQ0}),1.0]])]});}
            extrude(context, id + "F18", {"entities" : qUnion([Q0]), "operationType" : NewBodyOperationType.REMOVE, "endBound" : BoundingType.UP_TO_NEXT, "oppositeDirection" : true, "depth" : 25.4 * mm});
        }
        {
            var Q0;
            Q0=makeQuery(id+"F14.boolean.opBoolean","COPY",EDGE,{"derivedFrom":makeQuery(id+"F14.opExtrude","SWEPT_EDGE",EDGE,{"disambiguationData":[OSD([sQuery(id+"F13.wireOp",EDGE,"E9.top"),sQuery(id+"F13.wireOp",EDGE,"E9.left")])]})});
            var Q1;
            Q1=makeQuery(id+"F14.boolean.opBoolean","COPY",EDGE,{"derivedFrom":makeQuery(id+"F14.opExtrude","SWEPT_EDGE",EDGE,{"disambiguationData":[OSD([sQuery(id+"F13.wireOp",EDGE,"E10.1.0.2"),sQuery(id+"F13.wireOp",EDGE,"E10.2.0.3")])]})});
            var Q2;
            Q2=makeQuery(id+"F14.boolean.opBoolean","COPY",EDGE,{"derivedFrom":makeQuery(id+"F14.opExtrude","SWEPT_EDGE",EDGE,{"disambiguationData":[OSD([sQuery(id+"F13.wireOp",EDGE,"E10.3.0.2"),sQuery(id+"F13.wireOp",EDGE,"E10.4.0.3")])]})});
            var Q3;
            Q3=makeQuery(id+"F14.boolean.opBoolean","COPY",EDGE,{"derivedFrom":makeQuery(id+"F14.opExtrude","SWEPT_EDGE",EDGE,{"disambiguationData":[OSD([sQuery(id+"F13.wireOp",EDGE,"E10.5.0.2"),sQuery(id+"F13.wireOp",EDGE,"E10.6.0.3")])]})});
            var Q4;
            Q4=makeQuery(id+"F14.boolean.opBoolean","COPY",EDGE,{"derivedFrom":makeQuery(id+"F14.opExtrude","SWEPT_EDGE",EDGE,{"disambiguationData":[OSD([sQuery(id+"F13.wireOp",EDGE,"E10.7.0.2"),sQuery(id+"F13.wireOp",EDGE,"E10.8.0.3")])]})});
            var Q5;
            Q5=makeQuery(id+"F14.boolean.opBoolean","COPY",EDGE,{"derivedFrom":makeQuery(id+"F14.opExtrude","SWEPT_EDGE",EDGE,{"disambiguationData":[OSD([sQuery(id+"F13.wireOp",EDGE,"E10.11.0.2"),sQuery(id+"F13.wireOp",EDGE,"E10.12.0.3")])]})});
            var Q6;
            Q6=makeQuery(id+"F14.boolean.opBoolean","COPY",EDGE,{"derivedFrom":makeQuery(id+"F14.opExtrude","SWEPT_EDGE",EDGE,{"disambiguationData":[OSD([sQuery(id+"F13.wireOp",EDGE,"E10.9.0.2"),sQuery(id+"F13.wireOp",EDGE,"E10.10.0.3")])]})});
            var Q7;
            Q7=makeQuery(id+"F14.boolean.opBoolean","COPY",EDGE,{"derivedFrom":makeQuery(id+"F14.opExtrude","SWEPT_EDGE",EDGE,{"disambiguationData":[OSD([sQuery(id+"F13.wireOp",EDGE,"E10.13.0.2"),sQuery(id+"F13.wireOp",EDGE,"E10.14.0.3")])]})});
            var Q8;
            Q8=makeQuery(id+"F14.boolean.opBoolean","COPY",EDGE,{"derivedFrom":makeQuery(id+"F14.opExtrude","SWEPT_EDGE",EDGE,{"disambiguationData":[OSD([sQuery(id+"F13.wireOp",EDGE,"E10.15.0.2"),sQuery(id+"F13.wireOp",EDGE,"E10.16.0.3")])]})});
            var Q9;
            Q9=makeQuery(id+"F14.boolean.opBoolean","COPY",EDGE,{"derivedFrom":makeQuery(id+"F14.opExtrude","SWEPT_EDGE",EDGE,{"disambiguationData":[OSD([sQuery(id+"F13.wireOp",EDGE,"E10.17.0.2"),sQuery(id+"F13.wireOp",EDGE,"E10.18.0.3")])]})});
            var Q10;
            Q10=makeQuery(id+"F14.boolean.opBoolean","COPY",EDGE,{"derivedFrom":makeQuery(id+"F14.opExtrude","SWEPT_EDGE",EDGE,{"disambiguationData":[OSD([sQuery(id+"F13.wireOp",EDGE,"E10.19.0.2"),sQuery(id+"F13.wireOp",EDGE,"E10.20.0.3")])]})});
            var Q11;
            Q11=makeQuery(id+"F14.boolean.opBoolean","COPY",EDGE,{"derivedFrom":makeQuery(id+"F14.opExtrude","SWEPT_EDGE",EDGE,{"disambiguationData":[OSD([sQuery(id+"F13.wireOp",EDGE,"E10.21.0.2"),sQuery(id+"F13.wireOp",EDGE,"E10.22.0.3")])]})});
            var Q12;
            Q12=makeQuery(id+"F14.boolean.opBoolean","COPY",EDGE,{"derivedFrom":makeQuery(id+"F14.opExtrude","SWEPT_EDGE",EDGE,{"disambiguationData":[OSD([sQuery(id+"F13.wireOp",EDGE,"E10.23.0.2"),sQuery(id+"F13.wireOp",EDGE,"E10.24.0.3")])]})});
            var Q13;
            Q13=makeQuery(id+"F14.boolean.opBoolean","COPY",EDGE,{"derivedFrom":makeQuery(id+"F14.opExtrude","SWEPT_EDGE",EDGE,{"disambiguationData":[OSD([sQuery(id+"F13.wireOp",EDGE,"E10.25.0.2"),sQuery(id+"F13.wireOp",EDGE,"E10.26.0.3")])]})});
            var Q14;
            Q14=makeQuery(id+"F14.boolean.opBoolean","COPY",EDGE,{"derivedFrom":makeQuery(id+"F14.opExtrude","SWEPT_EDGE",EDGE,{"disambiguationData":[OSD([sQuery(id+"F13.wireOp",EDGE,"E10.27.0.2"),sQuery(id+"F13.wireOp",EDGE,"E10.28.0.3")])]})});
            var Q15;
            Q15=makeQuery(id+"F14.boolean.opBoolean","COPY",EDGE,{"derivedFrom":makeQuery(id+"F14.opExtrude","SWEPT_EDGE",EDGE,{"disambiguationData":[OSD([sQuery(id+"F13.wireOp",EDGE,"E10.29.0.2"),sQuery(id+"F13.wireOp",EDGE,"E10.30.0.3")])]})});
            var Q16;
            Q16=makeQuery(id+"F14.boolean.opBoolean","COPY",EDGE,{"derivedFrom":makeQuery(id+"F14.opExtrude","SWEPT_EDGE",EDGE,{"disambiguationData":[OSD([sQuery(id+"F13.wireOp",EDGE,"E10.31.0.2"),sQuery(id+"F13.wireOp",EDGE,"E10.32.0.3")])]})});
            var Q17;
            Q17=makeQuery(id+"F14.boolean.opBoolean","COPY",EDGE,{"derivedFrom":makeQuery(id+"F14.opExtrude","SWEPT_EDGE",EDGE,{"disambiguationData":[OSD([sQuery(id+"F13.wireOp",EDGE,"E10.33.0.2"),sQuery(id+"F13.wireOp",EDGE,"E10.34.0.3")])]})});
            var Q18;
            Q18=makeQuery(id+"F14.boolean.opBoolean","COPY",EDGE,{"derivedFrom":makeQuery(id+"F14.opExtrude","SWEPT_EDGE",EDGE,{"disambiguationData":[OSD([sQuery(id+"F13.wireOp",EDGE,"E10.35.0.2"),sQuery(id+"F13.wireOp",EDGE,"E10.36.0.3")])]})});
            var Q19;
            Q19=makeQuery(id+"F14.boolean.opBoolean","COPY",EDGE,{"derivedFrom":makeQuery(id+"F14.opExtrude","SWEPT_EDGE",EDGE,{"disambiguationData":[OSD([sQuery(id+"F13.wireOp",EDGE,"E10.37.0.2"),sQuery(id+"F13.wireOp",EDGE,"E10.38.0.3")])]})});
            var Q20;
            Q20=makeQuery(id+"F14.boolean.opBoolean","COPY",EDGE,{"derivedFrom":makeQuery(id+"F14.opExtrude","SWEPT_EDGE",EDGE,{"disambiguationData":[OSD([sQuery(id+"F13.wireOp",EDGE,"E10.39.0.2"),sQuery(id+"F13.wireOp",EDGE,"E10.40.0.3")])]})});
            var Q21;
            Q21=makeQuery(id+"F14.boolean.opBoolean","COPY",EDGE,{"derivedFrom":makeQuery(id+"F14.opExtrude","SWEPT_EDGE",EDGE,{"disambiguationData":[OSD([sQuery(id+"F13.wireOp",EDGE,"E10.41.0.2"),sQuery(id+"F13.wireOp",EDGE,"E10.42.0.3")])]})});
            var Q22;
            Q22=makeQuery(id+"F14.boolean.opBoolean","COPY",EDGE,{"derivedFrom":makeQuery(id+"F14.opExtrude","SWEPT_EDGE",EDGE,{"disambiguationData":[OSD([sQuery(id+"F13.wireOp",EDGE,"E10.43.0.2"),sQuery(id+"F13.wireOp",EDGE,"E10.44.0.3")])]})});
            var Q23;
            Q23=makeQuery(id+"F14.boolean.opBoolean","COPY",EDGE,{"derivedFrom":makeQuery(id+"F14.opExtrude","SWEPT_EDGE",EDGE,{"disambiguationData":[OSD([sQuery(id+"F13.wireOp",EDGE,"E10.45.0.2"),sQuery(id+"F13.wireOp",EDGE,"E10.46.0.3")])]})});
            var Q24;
            Q24=makeQuery(id+"F14.boolean.opBoolean","COPY",EDGE,{"derivedFrom":makeQuery(id+"F14.opExtrude","SWEPT_EDGE",EDGE,{"disambiguationData":[OSD([sQuery(id+"F13.wireOp",EDGE,"E10.47.0.2"),sQuery(id+"F13.wireOp",EDGE,"E10.48.0.3")])]})});
            var Q25;
            Q25=makeQuery(id+"F14.boolean.opBoolean","COPY",EDGE,{"derivedFrom":makeQuery(id+"F14.opExtrude","SWEPT_EDGE",EDGE,{"disambiguationData":[OSD([sQuery(id+"F13.wireOp",EDGE,"E9.top"),sQuery(id+"F13.wireOp",EDGE,"E10.1.0.0"),sQuery(id+"F13.wireOp",EDGE,"E10.1.0.3")])]})});
            var Q26;
            Q26=makeQuery(id+"F14.boolean.opBoolean","COPY",EDGE,{"derivedFrom":makeQuery(id+"F14.opExtrude","SWEPT_EDGE",EDGE,{"disambiguationData":[OSD([sQuery(id+"F13.wireOp",EDGE,"E10.2.0.3"),sQuery(id+"F13.wireOp",EDGE,"E10.3.0.0"),sQuery(id+"F13.wireOp",EDGE,"E10.3.0.3")])]})});
            var Q27;
            Q27=makeQuery(id+"F14.boolean.opBoolean","COPY",EDGE,{"derivedFrom":makeQuery(id+"F14.opExtrude","SWEPT_EDGE",EDGE,{"disambiguationData":[OSD([sQuery(id+"F13.wireOp",EDGE,"E10.4.0.3"),sQuery(id+"F13.wireOp",EDGE,"E10.5.0.0"),sQuery(id+"F13.wireOp",EDGE,"E10.5.0.3")])]})});
            var Q28;
            Q28=makeQuery(id+"F14.boolean.opBoolean","COPY",EDGE,{"derivedFrom":makeQuery(id+"F14.opExtrude","SWEPT_EDGE",EDGE,{"disambiguationData":[OSD([sQuery(id+"F13.wireOp",EDGE,"E10.6.0.3"),sQuery(id+"F13.wireOp",EDGE,"E10.7.0.0"),sQuery(id+"F13.wireOp",EDGE,"E10.7.0.3")])]})});
            var Q29;
            Q29=makeQuery(id+"F14.boolean.opBoolean","COPY",EDGE,{"derivedFrom":makeQuery(id+"F14.opExtrude","SWEPT_EDGE",EDGE,{"disambiguationData":[OSD([sQuery(id+"F13.wireOp",EDGE,"E10.8.0.3"),sQuery(id+"F13.wireOp",EDGE,"E10.9.0.0"),sQuery(id+"F13.wireOp",EDGE,"E10.9.0.3")])]})});
            var Q30;
            Q30=makeQuery(id+"F14.boolean.opBoolean","COPY",EDGE,{"derivedFrom":makeQuery(id+"F14.opExtrude","SWEPT_EDGE",EDGE,{"disambiguationData":[OSD([sQuery(id+"F13.wireOp",EDGE,"E10.10.0.3"),sQuery(id+"F13.wireOp",EDGE,"E10.11.0.0"),sQuery(id+"F13.wireOp",EDGE,"E10.11.0.3")])]})});
            var Q31;
            Q31=makeQuery(id+"F14.boolean.opBoolean","COPY",EDGE,{"derivedFrom":makeQuery(id+"F14.opExtrude","SWEPT_EDGE",EDGE,{"disambiguationData":[OSD([sQuery(id+"F13.wireOp",EDGE,"E10.12.0.3"),sQuery(id+"F13.wireOp",EDGE,"E10.13.0.0"),sQuery(id+"F13.wireOp",EDGE,"E10.13.0.3")])]})});
            var Q32;
            Q32=makeQuery(id+"F14.boolean.opBoolean","COPY",EDGE,{"derivedFrom":makeQuery(id+"F14.opExtrude","SWEPT_EDGE",EDGE,{"disambiguationData":[OSD([sQuery(id+"F13.wireOp",EDGE,"E10.14.0.3"),sQuery(id+"F13.wireOp",EDGE,"E10.15.0.0"),sQuery(id+"F13.wireOp",EDGE,"E10.15.0.3")])]})});
            var Q33;
            Q33=makeQuery(id+"F14.boolean.opBoolean","COPY",EDGE,{"derivedFrom":makeQuery(id+"F14.opExtrude","SWEPT_EDGE",EDGE,{"disambiguationData":[OSD([sQuery(id+"F13.wireOp",EDGE,"E10.16.0.3"),sQuery(id+"F13.wireOp",EDGE,"E10.17.0.0"),sQuery(id+"F13.wireOp",EDGE,"E10.17.0.3")])]})});
            var Q34;
            Q34=makeQuery(id+"F14.boolean.opBoolean","COPY",EDGE,{"derivedFrom":makeQuery(id+"F14.opExtrude","SWEPT_EDGE",EDGE,{"disambiguationData":[OSD([sQuery(id+"F13.wireOp",EDGE,"E10.18.0.3"),sQuery(id+"F13.wireOp",EDGE,"E10.19.0.0"),sQuery(id+"F13.wireOp",EDGE,"E10.19.0.3")])]})});
            var Q35;
            Q35=makeQuery(id+"F14.boolean.opBoolean","COPY",EDGE,{"derivedFrom":makeQuery(id+"F14.opExtrude","SWEPT_EDGE",EDGE,{"disambiguationData":[OSD([sQuery(id+"F13.wireOp",EDGE,"E10.20.0.3"),sQuery(id+"F13.wireOp",EDGE,"E10.21.0.0"),sQuery(id+"F13.wireOp",EDGE,"E10.21.0.3")])]})});
            var Q36;
            Q36=makeQuery(id+"F14.boolean.opBoolean","COPY",EDGE,{"derivedFrom":makeQuery(id+"F14.opExtrude","SWEPT_EDGE",EDGE,{"disambiguationData":[OSD([sQuery(id+"F13.wireOp",EDGE,"E10.22.0.3"),sQuery(id+"F13.wireOp",EDGE,"E10.23.0.0"),sQuery(id+"F13.wireOp",EDGE,"E10.23.0.3")])]})});
            var Q37;
            Q37=makeQuery(id+"F14.boolean.opBoolean","COPY",EDGE,{"derivedFrom":makeQuery(id+"F14.opExtrude","SWEPT_EDGE",EDGE,{"disambiguationData":[OSD([sQuery(id+"F13.wireOp",EDGE,"E10.24.0.3"),sQuery(id+"F13.wireOp",EDGE,"E10.25.0.0"),sQuery(id+"F13.wireOp",EDGE,"E10.25.0.3")])]})});
            var Q38;
            Q38=makeQuery(id+"F14.boolean.opBoolean","COPY",EDGE,{"derivedFrom":makeQuery(id+"F14.opExtrude","SWEPT_EDGE",EDGE,{"disambiguationData":[OSD([sQuery(id+"F13.wireOp",EDGE,"E10.26.0.3"),sQuery(id+"F13.wireOp",EDGE,"E10.27.0.0"),sQuery(id+"F13.wireOp",EDGE,"E10.27.0.3")])]})});
            var Q39;
            Q39=makeQuery(id+"F14.boolean.opBoolean","COPY",EDGE,{"derivedFrom":makeQuery(id+"F14.opExtrude","SWEPT_EDGE",EDGE,{"disambiguationData":[OSD([sQuery(id+"F13.wireOp",EDGE,"E10.28.0.3"),sQuery(id+"F13.wireOp",EDGE,"E10.29.0.0"),sQuery(id+"F13.wireOp",EDGE,"E10.29.0.3")])]})});
            var Q40;
            Q40=makeQuery(id+"F14.boolean.opBoolean","COPY",EDGE,{"derivedFrom":makeQuery(id+"F14.opExtrude","SWEPT_EDGE",EDGE,{"disambiguationData":[OSD([sQuery(id+"F13.wireOp",EDGE,"E10.30.0.3"),sQuery(id+"F13.wireOp",EDGE,"E10.31.0.0"),sQuery(id+"F13.wireOp",EDGE,"E10.31.0.3")])]})});
            var Q41;
            Q41=makeQuery(id+"F14.boolean.opBoolean","COPY",EDGE,{"derivedFrom":makeQuery(id+"F14.opExtrude","SWEPT_EDGE",EDGE,{"disambiguationData":[OSD([sQuery(id+"F13.wireOp",EDGE,"E10.32.0.3"),sQuery(id+"F13.wireOp",EDGE,"E10.33.0.0"),sQuery(id+"F13.wireOp",EDGE,"E10.33.0.3")])]})});
            var Q42;
            Q42=makeQuery(id+"F14.boolean.opBoolean","COPY",EDGE,{"derivedFrom":makeQuery(id+"F14.opExtrude","SWEPT_EDGE",EDGE,{"disambiguationData":[OSD([sQuery(id+"F13.wireOp",EDGE,"E10.34.0.3"),sQuery(id+"F13.wireOp",EDGE,"E10.35.0.0"),sQuery(id+"F13.wireOp",EDGE,"E10.35.0.3")])]})});
            var Q43;
            Q43=makeQuery(id+"F14.boolean.opBoolean","COPY",EDGE,{"derivedFrom":makeQuery(id+"F14.opExtrude","SWEPT_EDGE",EDGE,{"disambiguationData":[OSD([sQuery(id+"F13.wireOp",EDGE,"E10.36.0.3"),sQuery(id+"F13.wireOp",EDGE,"E10.37.0.0"),sQuery(id+"F13.wireOp",EDGE,"E10.37.0.3")])]})});
            var Q44;
            Q44=makeQuery(id+"F14.boolean.opBoolean","COPY",EDGE,{"derivedFrom":makeQuery(id+"F14.opExtrude","SWEPT_EDGE",EDGE,{"disambiguationData":[OSD([sQuery(id+"F13.wireOp",EDGE,"E10.38.0.3"),sQuery(id+"F13.wireOp",EDGE,"E10.39.0.0"),sQuery(id+"F13.wireOp",EDGE,"E10.39.0.3")])]})});
            var Q45;
            Q45=makeQuery(id+"F14.boolean.opBoolean","COPY",EDGE,{"derivedFrom":makeQuery(id+"F14.opExtrude","SWEPT_EDGE",EDGE,{"disambiguationData":[OSD([sQuery(id+"F13.wireOp",EDGE,"E10.40.0.3"),sQuery(id+"F13.wireOp",EDGE,"E10.41.0.0"),sQuery(id+"F13.wireOp",EDGE,"E10.41.0.3")])]})});
            var Q46;
            Q46=makeQuery(id+"F14.boolean.opBoolean","COPY",EDGE,{"derivedFrom":makeQuery(id+"F14.opExtrude","SWEPT_EDGE",EDGE,{"disambiguationData":[OSD([sQuery(id+"F13.wireOp",EDGE,"E10.42.0.3"),sQuery(id+"F13.wireOp",EDGE,"E10.43.0.0"),sQuery(id+"F13.wireOp",EDGE,"E10.43.0.3")])]})});
            var Q47;
            Q47=makeQuery(id+"F14.boolean.opBoolean","COPY",EDGE,{"derivedFrom":makeQuery(id+"F14.opExtrude","SWEPT_EDGE",EDGE,{"disambiguationData":[OSD([sQuery(id+"F13.wireOp",EDGE,"E10.44.0.3"),sQuery(id+"F13.wireOp",EDGE,"E10.45.0.0"),sQuery(id+"F13.wireOp",EDGE,"E10.45.0.3")])]})});
            var Q48;
            Q48=makeQuery(id+"F14.boolean.opBoolean","COPY",EDGE,{"derivedFrom":makeQuery(id+"F14.opExtrude","SWEPT_EDGE",EDGE,{"disambiguationData":[OSD([sQuery(id+"F13.wireOp",EDGE,"E10.46.0.3"),sQuery(id+"F13.wireOp",EDGE,"E10.47.0.0"),sQuery(id+"F13.wireOp",EDGE,"E10.47.0.3")])]})});
            var Q49;
            Q49=makeQuery(id+"F14.boolean.opBoolean","COPY",EDGE,{"derivedFrom":makeQuery(id+"F14.opExtrude","SWEPT_EDGE",EDGE,{"disambiguationData":[OSD([sQuery(id+"F13.wireOp",EDGE,"E10.48.0.3"),sQuery(id+"F13.wireOp",EDGE,"E10.49.0.0"),sQuery(id+"F13.wireOp",EDGE,"E10.49.0.3")])]})});
            var Q50;
            Q50=makeQuery(id+"F14.boolean.opBoolean","COPY",EDGE,{"derivedFrom":makeQuery(id+"F14.opExtrude","SWEPT_EDGE",EDGE,{"disambiguationData":[OSD([sQuery(id+"F13.wireOp",EDGE,"E10.50.0.3"),sQuery(id+"F13.wireOp",EDGE,"E10.51.0.0"),sQuery(id+"F13.wireOp",EDGE,"E10.51.0.3")])]})});
            var Q51;
            Q51=makeQuery(id+"F14.boolean.opBoolean","COPY",EDGE,{"derivedFrom":makeQuery(id+"F14.opExtrude","SWEPT_EDGE",EDGE,{"disambiguationData":[OSD([sQuery(id+"F13.wireOp",EDGE,"E10.52.0.3"),sQuery(id+"F13.wireOp",EDGE,"E10.53.0.0"),sQuery(id+"F13.wireOp",EDGE,"E10.53.0.3")])]})});
            var Q52;
            Q52=makeQuery(id+"F14.boolean.opBoolean","COPY",EDGE,{"derivedFrom":makeQuery(id+"F14.opExtrude","SWEPT_EDGE",EDGE,{"disambiguationData":[OSD([sQuery(id+"F13.wireOp",EDGE,"E10.70.0.3"),sQuery(id+"F13.wireOp",EDGE,"E10.71.0.0"),sQuery(id+"F13.wireOp",EDGE,"E10.71.0.3")])]})});
            var Q53;
            Q53=makeQuery(id+"F14.boolean.opBoolean","COPY",EDGE,{"derivedFrom":makeQuery(id+"F14.opExtrude","SWEPT_EDGE",EDGE,{"disambiguationData":[OSD([sQuery(id+"F13.wireOp",EDGE,"E10.68.0.3"),sQuery(id+"F13.wireOp",EDGE,"E10.69.0.0"),sQuery(id+"F13.wireOp",EDGE,"E10.69.0.3")])]})});
            var Q54;
            Q54=makeQuery(id+"F14.boolean.opBoolean","COPY",EDGE,{"derivedFrom":makeQuery(id+"F14.opExtrude","SWEPT_EDGE",EDGE,{"disambiguationData":[OSD([sQuery(id+"F13.wireOp",EDGE,"E10.66.0.3"),sQuery(id+"F13.wireOp",EDGE,"E10.67.0.0"),sQuery(id+"F13.wireOp",EDGE,"E10.67.0.3")])]})});
            var Q55;
            Q55=makeQuery(id+"F14.boolean.opBoolean","COPY",EDGE,{"derivedFrom":makeQuery(id+"F14.opExtrude","SWEPT_EDGE",EDGE,{"disambiguationData":[OSD([sQuery(id+"F13.wireOp",EDGE,"E10.64.0.3"),sQuery(id+"F13.wireOp",EDGE,"E10.65.0.0"),sQuery(id+"F13.wireOp",EDGE,"E10.65.0.3")])]})});
            var Q56;
            Q56=makeQuery(id+"F14.boolean.opBoolean","COPY",EDGE,{"derivedFrom":makeQuery(id+"F14.opExtrude","SWEPT_EDGE",EDGE,{"disambiguationData":[OSD([sQuery(id+"F13.wireOp",EDGE,"E10.62.0.3"),sQuery(id+"F13.wireOp",EDGE,"E10.63.0.0"),sQuery(id+"F13.wireOp",EDGE,"E10.63.0.3")])]})});
            var Q57;
            Q57=makeQuery(id+"F14.boolean.opBoolean","COPY",EDGE,{"derivedFrom":makeQuery(id+"F14.opExtrude","SWEPT_EDGE",EDGE,{"disambiguationData":[OSD([sQuery(id+"F13.wireOp",EDGE,"E10.60.0.3"),sQuery(id+"F13.wireOp",EDGE,"E10.61.0.0"),sQuery(id+"F13.wireOp",EDGE,"E10.61.0.3")])]})});
            var Q58;
            Q58=makeQuery(id+"F14.boolean.opBoolean","COPY",EDGE,{"derivedFrom":makeQuery(id+"F14.opExtrude","SWEPT_EDGE",EDGE,{"disambiguationData":[OSD([sQuery(id+"F13.wireOp",EDGE,"E10.58.0.3"),sQuery(id+"F13.wireOp",EDGE,"E10.59.0.0"),sQuery(id+"F13.wireOp",EDGE,"E10.59.0.3")])]})});
            var Q59;
            Q59=makeQuery(id+"F14.boolean.opBoolean","COPY",EDGE,{"derivedFrom":makeQuery(id+"F14.opExtrude","SWEPT_EDGE",EDGE,{"disambiguationData":[OSD([sQuery(id+"F13.wireOp",EDGE,"E10.56.0.3"),sQuery(id+"F13.wireOp",EDGE,"E10.57.0.0"),sQuery(id+"F13.wireOp",EDGE,"E10.57.0.3")])]})});
            var Q60;
            Q60=makeQuery(id+"F14.boolean.opBoolean","COPY",EDGE,{"derivedFrom":makeQuery(id+"F14.opExtrude","SWEPT_EDGE",EDGE,{"disambiguationData":[OSD([sQuery(id+"F13.wireOp",EDGE,"E10.54.0.3"),sQuery(id+"F13.wireOp",EDGE,"E10.55.0.0"),sQuery(id+"F13.wireOp",EDGE,"E10.55.0.3")])]})});
            var Q61;
            Q61=makeQuery(id+"F14.boolean.opBoolean","COPY",EDGE,{"derivedFrom":makeQuery(id+"F14.opExtrude","SWEPT_EDGE",EDGE,{"disambiguationData":[OSD([sQuery(id+"F13.wireOp",EDGE,"E10.49.0.2"),sQuery(id+"F13.wireOp",EDGE,"E10.50.0.3")])]})});
            var Q62;
            Q62=makeQuery(id+"F14.boolean.opBoolean","COPY",EDGE,{"derivedFrom":makeQuery(id+"F14.opExtrude","SWEPT_EDGE",EDGE,{"disambiguationData":[OSD([sQuery(id+"F13.wireOp",EDGE,"E10.51.0.2"),sQuery(id+"F13.wireOp",EDGE,"E10.52.0.3")])]})});
            var Q63;
            Q63=makeQuery(id+"F14.boolean.opBoolean","COPY",EDGE,{"derivedFrom":makeQuery(id+"F14.opExtrude","SWEPT_EDGE",EDGE,{"disambiguationData":[OSD([sQuery(id+"F13.wireOp",EDGE,"E10.53.0.2"),sQuery(id+"F13.wireOp",EDGE,"E10.54.0.3")])]})});
            var Q64;
            Q64=makeQuery(id+"F14.boolean.opBoolean","COPY",EDGE,{"derivedFrom":makeQuery(id+"F14.opExtrude","SWEPT_EDGE",EDGE,{"disambiguationData":[OSD([sQuery(id+"F13.wireOp",EDGE,"E10.55.0.2"),sQuery(id+"F13.wireOp",EDGE,"E10.56.0.3")])]})});
            var Q65;
            Q65=makeQuery(id+"F14.boolean.opBoolean","COPY",EDGE,{"derivedFrom":makeQuery(id+"F14.opExtrude","SWEPT_EDGE",EDGE,{"disambiguationData":[OSD([sQuery(id+"F13.wireOp",EDGE,"E10.57.0.2"),sQuery(id+"F13.wireOp",EDGE,"E10.58.0.3")])]})});
            var Q66;
            Q66=makeQuery(id+"F14.boolean.opBoolean","COPY",EDGE,{"derivedFrom":makeQuery(id+"F14.opExtrude","SWEPT_EDGE",EDGE,{"disambiguationData":[OSD([sQuery(id+"F13.wireOp",EDGE,"E10.59.0.2"),sQuery(id+"F13.wireOp",EDGE,"E10.60.0.3")])]})});
            var Q67;
            Q67=makeQuery(id+"F14.boolean.opBoolean","COPY",EDGE,{"derivedFrom":makeQuery(id+"F14.opExtrude","SWEPT_EDGE",EDGE,{"disambiguationData":[OSD([sQuery(id+"F13.wireOp",EDGE,"E10.61.0.2"),sQuery(id+"F13.wireOp",EDGE,"E10.62.0.3")])]})});
            var Q68;
            Q68=makeQuery(id+"F14.boolean.opBoolean","COPY",EDGE,{"derivedFrom":makeQuery(id+"F14.opExtrude","SWEPT_EDGE",EDGE,{"disambiguationData":[OSD([sQuery(id+"F13.wireOp",EDGE,"E10.63.0.2"),sQuery(id+"F13.wireOp",EDGE,"E10.64.0.3")])]})});
            var Q69;
            Q69=makeQuery(id+"F14.boolean.opBoolean","COPY",EDGE,{"derivedFrom":makeQuery(id+"F14.opExtrude","SWEPT_EDGE",EDGE,{"disambiguationData":[OSD([sQuery(id+"F13.wireOp",EDGE,"E10.65.0.2"),sQuery(id+"F13.wireOp",EDGE,"E10.66.0.3")])]})});
            var Q70;
            Q70=makeQuery(id+"F14.boolean.opBoolean","COPY",EDGE,{"derivedFrom":makeQuery(id+"F14.opExtrude","SWEPT_EDGE",EDGE,{"disambiguationData":[OSD([sQuery(id+"F13.wireOp",EDGE,"E10.67.0.2"),sQuery(id+"F13.wireOp",EDGE,"E10.68.0.3")])]})});
            var Q71;
            Q71=makeQuery(id+"F14.boolean.opBoolean","COPY",EDGE,{"derivedFrom":makeQuery(id+"F14.opExtrude","SWEPT_EDGE",EDGE,{"disambiguationData":[OSD([sQuery(id+"F13.wireOp",EDGE,"E10.69.0.2"),sQuery(id+"F13.wireOp",EDGE,"E10.70.0.3")])]})});
            var Q72;
            Q72=makeQuery(id+"F14.boolean.opBoolean","COPY",EDGE,{"derivedFrom":makeQuery(id+"F14.opExtrude","SWEPT_EDGE",EDGE,{"disambiguationData":[OSD([sQuery(id+"F13.wireOp",EDGE,"E10.71.0.2"),sQuery(id+"F13.wireOp",EDGE,"E10.72.0.3")])]})});
            var Q73;
            Q73=makeQuery(id+"F14.boolean.opBoolean","COPY",EDGE,{"derivedFrom":makeQuery(id+"F14.opExtrude","SWEPT_EDGE",EDGE,{"disambiguationData":[OSD([sQuery(id+"F13.wireOp",EDGE,"E10.73.0.2"),sQuery(id+"F13.wireOp",EDGE,"E10.74.0.3")])]})});
            var Q74;
            Q74=makeQuery(id+"F14.boolean.opBoolean","COPY",EDGE,{"derivedFrom":makeQuery(id+"F14.opExtrude","SWEPT_EDGE",EDGE,{"disambiguationData":[OSD([sQuery(id+"F13.wireOp",EDGE,"E10.75.0.2"),sQuery(id+"F13.wireOp",EDGE,"E10.76.0.3")])]})});
            var Q75;
            Q75=makeQuery(id+"F14.boolean.opBoolean","COPY",EDGE,{"derivedFrom":makeQuery(id+"F14.opExtrude","SWEPT_EDGE",EDGE,{"disambiguationData":[OSD([sQuery(id+"F13.wireOp",EDGE,"E10.77.0.2"),sQuery(id+"F13.wireOp",EDGE,"E10.78.0.3")])]})});
            var Q76;
            Q76=makeQuery(id+"F14.boolean.opBoolean","COPY",EDGE,{"derivedFrom":makeQuery(id+"F14.opExtrude","SWEPT_EDGE",EDGE,{"disambiguationData":[OSD([sQuery(id+"F13.wireOp",EDGE,"E10.79.0.2"),sQuery(id+"F13.wireOp",EDGE,"E10.80.0.3")])]})});
            var Q77;
            Q77=makeQuery(id+"F14.boolean.opBoolean","COPY",EDGE,{"derivedFrom":makeQuery(id+"F14.opExtrude","SWEPT_EDGE",EDGE,{"disambiguationData":[OSD([sQuery(id+"F13.wireOp",EDGE,"E10.81.0.2"),sQuery(id+"F13.wireOp",EDGE,"E10.82.0.3")])]})});
            var Q78;
            Q78=makeQuery(id+"F14.boolean.opBoolean","COPY",EDGE,{"derivedFrom":makeQuery(id+"F14.opExtrude","SWEPT_EDGE",EDGE,{"disambiguationData":[OSD([sQuery(id+"F13.wireOp",EDGE,"E10.83.0.2"),sQuery(id+"F13.wireOp",EDGE,"E10.84.0.3")])]})});
            var Q79;
            Q79=makeQuery(id+"F14.boolean.opBoolean","COPY",EDGE,{"derivedFrom":makeQuery(id+"F14.opExtrude","SWEPT_EDGE",EDGE,{"disambiguationData":[OSD([sQuery(id+"F13.wireOp",EDGE,"E10.85.0.2"),sQuery(id+"F13.wireOp",EDGE,"E10.86.0.3")])]})});
            var Q80;
            Q80=makeQuery(id+"F14.boolean.opBoolean","COPY",EDGE,{"derivedFrom":makeQuery(id+"F14.opExtrude","SWEPT_EDGE",EDGE,{"disambiguationData":[OSD([sQuery(id+"F13.wireOp",EDGE,"E10.87.0.2"),sQuery(id+"F13.wireOp",EDGE,"E10.88.0.3")])]})});
            var Q81;
            Q81=makeQuery(id+"F14.boolean.opBoolean","COPY",EDGE,{"derivedFrom":makeQuery(id+"F14.opExtrude","SWEPT_EDGE",EDGE,{"disambiguationData":[OSD([sQuery(id+"F13.wireOp",EDGE,"E10.89.0.2"),sQuery(id+"F13.wireOp",EDGE,"E10.90.0.3")])]})});
            var Q82;
            Q82=makeQuery(id+"F14.boolean.opBoolean","COPY",EDGE,{"derivedFrom":makeQuery(id+"F14.opExtrude","SWEPT_EDGE",EDGE,{"disambiguationData":[OSD([sQuery(id+"F13.wireOp",EDGE,"E10.91.0.2"),sQuery(id+"F13.wireOp",EDGE,"E10.92.0.3")])]})});
            var Q83;
            Q83=makeQuery(id+"F14.boolean.opBoolean","COPY",EDGE,{"derivedFrom":makeQuery(id+"F14.opExtrude","SWEPT_EDGE",EDGE,{"disambiguationData":[OSD([sQuery(id+"F13.wireOp",EDGE,"E10.93.0.2"),sQuery(id+"F13.wireOp",EDGE,"E10.94.0.3")])]})});
            var Q84;
            Q84=makeQuery(id+"F14.boolean.opBoolean","COPY",EDGE,{"derivedFrom":makeQuery(id+"F14.opExtrude","SWEPT_EDGE",EDGE,{"disambiguationData":[OSD([sQuery(id+"F13.wireOp",EDGE,"E10.95.0.2"),sQuery(id+"F13.wireOp",EDGE,"E10.96.0.3")])]})});
            var Q85;
            Q85=makeQuery(id+"F14.boolean.opBoolean","COPY",EDGE,{"derivedFrom":makeQuery(id+"F14.opExtrude","SWEPT_EDGE",EDGE,{"disambiguationData":[OSD([sQuery(id+"F13.wireOp",EDGE,"E10.97.0.2"),sQuery(id+"F13.wireOp",EDGE,"E10.98.0.3")])]})});
            var Q86;
            Q86=makeQuery(id+"F16.boolean.opBoolean","COPY",EDGE,{"derivedFrom":makeQuery(id+"F16.opExtrude","SWEPT_EDGE",EDGE,{"disambiguationData":[OSD([sQuery(id+"F15.wireOp",EDGE,"E15.2.0.0"),sQuery(id+"F15.wireOp",EDGE,"E15.2.0.1")])]})});
            var Q87;
            Q87=makeQuery(id+"F16.boolean.opBoolean","COPY",EDGE,{"derivedFrom":makeQuery(id+"F16.opExtrude","SWEPT_EDGE",EDGE,{"disambiguationData":[OSD([sQuery(id+"F15.wireOp",EDGE,"E15.4.0.0"),sQuery(id+"F15.wireOp",EDGE,"E15.4.0.1")])]})});
            var Q88;
            Q88=makeQuery(id+"F16.boolean.opBoolean","COPY",EDGE,{"derivedFrom":makeQuery(id+"F16.opExtrude","SWEPT_EDGE",EDGE,{"disambiguationData":[OSD([sQuery(id+"F15.wireOp",EDGE,"E15.6.0.0"),sQuery(id+"F15.wireOp",EDGE,"E15.6.0.1")])]})});
            var Q89;
            Q89=makeQuery(id+"F16.boolean.opBoolean","COPY",EDGE,{"derivedFrom":makeQuery(id+"F16.opExtrude","SWEPT_EDGE",EDGE,{"disambiguationData":[OSD([sQuery(id+"F15.wireOp",EDGE,"E15.8.0.0"),sQuery(id+"F15.wireOp",EDGE,"E15.8.0.1")])]})});
            var Q90;
            Q90=makeQuery(id+"F16.boolean.opBoolean","COPY",EDGE,{"derivedFrom":makeQuery(id+"F16.opExtrude","SWEPT_EDGE",EDGE,{"disambiguationData":[OSD([sQuery(id+"F15.wireOp",EDGE,"E15.10.0.0"),sQuery(id+"F15.wireOp",EDGE,"E15.10.0.1")])]})});
            var Q91;
            Q91=makeQuery(id+"F16.boolean.opBoolean","COPY",EDGE,{"derivedFrom":makeQuery(id+"F16.opExtrude","SWEPT_EDGE",EDGE,{"disambiguationData":[OSD([sQuery(id+"F15.wireOp",EDGE,"E15.12.0.0"),sQuery(id+"F15.wireOp",EDGE,"E15.12.0.1")])]})});
            var Q92;
            Q92=makeQuery(id+"F16.boolean.opBoolean","COPY",EDGE,{"derivedFrom":makeQuery(id+"F16.opExtrude","SWEPT_EDGE",EDGE,{"disambiguationData":[OSD([sQuery(id+"F15.wireOp",EDGE,"E15.14.0.0"),sQuery(id+"F15.wireOp",EDGE,"E15.14.0.1")])]})});
            var Q93;
            Q93=makeQuery(id+"F16.boolean.opBoolean","COPY",EDGE,{"derivedFrom":makeQuery(id+"F16.opExtrude","SWEPT_EDGE",EDGE,{"disambiguationData":[OSD([sQuery(id+"F15.wireOp",EDGE,"E15.16.0.0"),sQuery(id+"F15.wireOp",EDGE,"E15.16.0.1")])]})});
            var Q94;
            Q94=makeQuery(id+"F16.boolean.opBoolean","COPY",EDGE,{"derivedFrom":makeQuery(id+"F16.opExtrude","SWEPT_EDGE",EDGE,{"disambiguationData":[OSD([sQuery(id+"F15.wireOp",EDGE,"E15.18.0.0"),sQuery(id+"F15.wireOp",EDGE,"E15.18.0.1")])]})});
            var Q95;
            Q95=makeQuery(id+"F16.boolean.opBoolean","COPY",EDGE,{"derivedFrom":makeQuery(id+"F16.opExtrude","SWEPT_EDGE",EDGE,{"disambiguationData":[OSD([sQuery(id+"F15.wireOp",EDGE,"E15.20.0.0"),sQuery(id+"F15.wireOp",EDGE,"E15.20.0.1")])]})});
            var Q96;
            Q96=makeQuery(id+"F16.boolean.opBoolean","COPY",EDGE,{"derivedFrom":makeQuery(id+"F16.opExtrude","SWEPT_EDGE",EDGE,{"disambiguationData":[OSD([sQuery(id+"F15.wireOp",EDGE,"E15.22.0.0"),sQuery(id+"F15.wireOp",EDGE,"E15.22.0.1")])]})});
            var Q97;
            Q97=makeQuery(id+"F16.boolean.opBoolean","COPY",EDGE,{"derivedFrom":makeQuery(id+"F16.opExtrude","SWEPT_EDGE",EDGE,{"disambiguationData":[OSD([sQuery(id+"F15.wireOp",EDGE,"E15.24.0.0"),sQuery(id+"F15.wireOp",EDGE,"E15.24.0.1")])]})});
            var Q98;
            Q98=makeQuery(id+"F16.boolean.opBoolean","COPY",EDGE,{"derivedFrom":makeQuery(id+"F16.opExtrude","SWEPT_EDGE",EDGE,{"disambiguationData":[OSD([sQuery(id+"F15.wireOp",EDGE,"E15.26.0.0"),sQuery(id+"F15.wireOp",EDGE,"E15.26.0.1")])]})});
            var Q99;
            Q99=makeQuery(id+"F16.boolean.opBoolean","COPY",EDGE,{"derivedFrom":makeQuery(id+"F16.opExtrude","SWEPT_EDGE",EDGE,{"disambiguationData":[OSD([sQuery(id+"F15.wireOp",EDGE,"E15.28.0.0"),sQuery(id+"F15.wireOp",EDGE,"E15.28.0.1")])]})});
            var Q100;
            Q100=makeQuery(id+"F16.boolean.opBoolean","COPY",EDGE,{"derivedFrom":makeQuery(id+"F16.opExtrude","SWEPT_EDGE",EDGE,{"disambiguationData":[OSD([sQuery(id+"F15.wireOp",EDGE,"E15.30.0.0"),sQuery(id+"F15.wireOp",EDGE,"E15.30.0.1")])]})});
            var Q101;
            Q101=makeQuery(id+"F16.boolean.opBoolean","COPY",EDGE,{"derivedFrom":makeQuery(id+"F16.opExtrude","SWEPT_EDGE",EDGE,{"disambiguationData":[OSD([sQuery(id+"F15.wireOp",EDGE,"E15.32.0.0"),sQuery(id+"F15.wireOp",EDGE,"E15.32.0.1")])]})});
            var Q102;
            Q102=makeQuery(id+"F16.boolean.opBoolean","COPY",EDGE,{"derivedFrom":makeQuery(id+"F16.opExtrude","SWEPT_EDGE",EDGE,{"disambiguationData":[OSD([sQuery(id+"F15.wireOp",EDGE,"E15.34.0.0"),sQuery(id+"F15.wireOp",EDGE,"E15.34.0.1")])]})});
            var Q103;
            Q103=makeQuery(id+"F16.boolean.opBoolean","COPY",EDGE,{"derivedFrom":makeQuery(id+"F16.opExtrude","SWEPT_EDGE",EDGE,{"disambiguationData":[OSD([sQuery(id+"F15.wireOp",EDGE,"E15.36.0.0"),sQuery(id+"F15.wireOp",EDGE,"E15.36.0.1")])]})});
            var Q104;
            Q104=makeQuery(id+"F16.boolean.opBoolean","COPY",EDGE,{"derivedFrom":makeQuery(id+"F16.opExtrude","SWEPT_EDGE",EDGE,{"disambiguationData":[OSD([sQuery(id+"F15.wireOp",EDGE,"E15.38.0.0"),sQuery(id+"F15.wireOp",EDGE,"E15.38.0.1")])]})});
            var Q105;
            Q105=makeQuery(id+"F16.boolean.opBoolean","COPY",EDGE,{"derivedFrom":makeQuery(id+"F16.opExtrude","SWEPT_EDGE",EDGE,{"disambiguationData":[OSD([sQuery(id+"F15.wireOp",EDGE,"E15.40.0.0"),sQuery(id+"F15.wireOp",EDGE,"E15.40.0.1")])]})});
            var Q106;
            Q106=makeQuery(id+"F16.boolean.opBoolean","COPY",EDGE,{"derivedFrom":makeQuery(id+"F16.opExtrude","SWEPT_EDGE",EDGE,{"disambiguationData":[OSD([sQuery(id+"F15.wireOp",EDGE,"E15.42.0.0"),sQuery(id+"F15.wireOp",EDGE,"E15.42.0.1")])]})});
            var Q107;
            Q107=makeQuery(id+"F16.boolean.opBoolean","COPY",EDGE,{"derivedFrom":makeQuery(id+"F16.opExtrude","SWEPT_EDGE",EDGE,{"disambiguationData":[OSD([sQuery(id+"F15.wireOp",EDGE,"E15.44.0.0"),sQuery(id+"F15.wireOp",EDGE,"E15.44.0.1")])]})});
            var Q108;
            Q108=makeQuery(id+"F16.boolean.opBoolean","COPY",EDGE,{"derivedFrom":makeQuery(id+"F16.opExtrude","SWEPT_EDGE",EDGE,{"disambiguationData":[OSD([sQuery(id+"F15.wireOp",EDGE,"E15.46.0.0"),sQuery(id+"F15.wireOp",EDGE,"E15.46.0.1")])]})});
            var Q109;
            Q109=makeQuery(id+"F16.boolean.opBoolean","COPY",EDGE,{"derivedFrom":makeQuery(id+"F16.opExtrude","SWEPT_EDGE",EDGE,{"disambiguationData":[OSD([sQuery(id+"F15.wireOp",EDGE,"E15.48.0.0"),sQuery(id+"F15.wireOp",EDGE,"E15.48.0.1")])]})});
            var Q110;
            Q110=makeQuery(id+"F16.boolean.opBoolean","COPY",EDGE,{"derivedFrom":makeQuery(id+"F16.opExtrude","SWEPT_EDGE",EDGE,{"disambiguationData":[OSD([sQuery(id+"F15.wireOp",EDGE,"E15.50.0.0"),sQuery(id+"F15.wireOp",EDGE,"E15.50.0.1")])]})});
            var Q111;
            Q111=makeQuery(id+"F16.boolean.opBoolean","COPY",EDGE,{"derivedFrom":makeQuery(id+"F16.opExtrude","SWEPT_EDGE",EDGE,{"disambiguationData":[OSD([sQuery(id+"F15.wireOp",EDGE,"E15.54.0.0"),sQuery(id+"F15.wireOp",EDGE,"E15.54.0.1")])]})});
            var Q112;
            Q112=makeQuery(id+"F16.boolean.opBoolean","COPY",EDGE,{"derivedFrom":makeQuery(id+"F16.opExtrude","SWEPT_EDGE",EDGE,{"disambiguationData":[OSD([sQuery(id+"F15.wireOp",EDGE,"E15.56.0.0"),sQuery(id+"F15.wireOp",EDGE,"E15.56.0.1")])]})});
            var Q113;
            Q113=makeQuery(id+"F16.boolean.opBoolean","COPY",EDGE,{"derivedFrom":makeQuery(id+"F16.opExtrude","SWEPT_EDGE",EDGE,{"disambiguationData":[OSD([sQuery(id+"F15.wireOp",EDGE,"E15.58.0.0"),sQuery(id+"F15.wireOp",EDGE,"E15.58.0.1")])]})});
            var Q114;
            Q114=makeQuery(id+"F16.boolean.opBoolean","COPY",EDGE,{"derivedFrom":makeQuery(id+"F16.opExtrude","SWEPT_EDGE",EDGE,{"disambiguationData":[OSD([sQuery(id+"F15.wireOp",EDGE,"E15.60.0.0"),sQuery(id+"F15.wireOp",EDGE,"E15.60.0.1")])]})});
            var Q115;
            Q115=makeQuery(id+"F16.boolean.opBoolean","COPY",EDGE,{"derivedFrom":makeQuery(id+"F16.opExtrude","SWEPT_EDGE",EDGE,{"disambiguationData":[OSD([sQuery(id+"F15.wireOp",EDGE,"E15.62.0.0"),sQuery(id+"F15.wireOp",EDGE,"E15.62.0.1")])]})});
            var Q116;
            Q116=makeQuery(id+"F16.boolean.opBoolean","COPY",EDGE,{"derivedFrom":makeQuery(id+"F16.opExtrude","SWEPT_EDGE",EDGE,{"disambiguationData":[OSD([sQuery(id+"F15.wireOp",EDGE,"E15.64.0.0"),sQuery(id+"F15.wireOp",EDGE,"E15.64.0.1")])]})});
            var Q117;
            Q117=makeQuery(id+"F16.boolean.opBoolean","COPY",EDGE,{"derivedFrom":makeQuery(id+"F16.opExtrude","SWEPT_EDGE",EDGE,{"disambiguationData":[OSD([sQuery(id+"F15.wireOp",EDGE,"E15.66.0.0"),sQuery(id+"F15.wireOp",EDGE,"E15.66.0.1")])]})});
            var Q118;
            Q118=makeQuery(id+"F16.boolean.opBoolean","COPY",EDGE,{"derivedFrom":makeQuery(id+"F16.opExtrude","SWEPT_EDGE",EDGE,{"disambiguationData":[OSD([sQuery(id+"F15.wireOp",EDGE,"E15.68.0.0"),sQuery(id+"F15.wireOp",EDGE,"E15.68.0.1")])]})});
            var Q119;
            Q119=makeQuery(id+"F16.boolean.opBoolean","COPY",EDGE,{"derivedFrom":makeQuery(id+"F16.opExtrude","SWEPT_EDGE",EDGE,{"disambiguationData":[OSD([sQuery(id+"F15.wireOp",EDGE,"E15.70.0.0"),sQuery(id+"F15.wireOp",EDGE,"E15.70.0.1")])]})});
            var Q120;
            Q120=makeQuery(id+"F16.boolean.opBoolean","COPY",EDGE,{"derivedFrom":makeQuery(id+"F16.opExtrude","SWEPT_EDGE",EDGE,{"disambiguationData":[OSD([sQuery(id+"F15.wireOp",EDGE,"E15.72.0.0"),sQuery(id+"F15.wireOp",EDGE,"E15.72.0.1")])]})});
            var Q121;
            Q121=makeQuery(id+"F16.boolean.opBoolean","COPY",EDGE,{"derivedFrom":makeQuery(id+"F16.opExtrude","SWEPT_EDGE",EDGE,{"disambiguationData":[OSD([sQuery(id+"F15.wireOp",EDGE,"E15.74.0.0"),sQuery(id+"F15.wireOp",EDGE,"E15.74.0.1")])]})});
            var Q122;
            Q122=makeQuery(id+"F16.boolean.opBoolean","COPY",EDGE,{"derivedFrom":makeQuery(id+"F16.opExtrude","SWEPT_EDGE",EDGE,{"disambiguationData":[OSD([sQuery(id+"F15.wireOp",EDGE,"E15.76.0.0"),sQuery(id+"F15.wireOp",EDGE,"E15.76.0.1")])]})});
            var Q123;
            Q123=makeQuery(id+"F16.boolean.opBoolean","COPY",EDGE,{"derivedFrom":makeQuery(id+"F16.opExtrude","SWEPT_EDGE",EDGE,{"disambiguationData":[OSD([sQuery(id+"F15.wireOp",EDGE,"E15.78.0.0"),sQuery(id+"F15.wireOp",EDGE,"E15.78.0.1")])]})});
            var Q124;
            Q124=makeQuery(id+"F16.boolean.opBoolean","COPY",EDGE,{"derivedFrom":makeQuery(id+"F16.opExtrude","SWEPT_EDGE",EDGE,{"disambiguationData":[OSD([sQuery(id+"F15.wireOp",EDGE,"E15.80.0.0"),sQuery(id+"F15.wireOp",EDGE,"E15.80.0.1")])]})});
            var Q125;
            Q125=makeQuery(id+"F16.boolean.opBoolean","COPY",EDGE,{"derivedFrom":makeQuery(id+"F16.opExtrude","SWEPT_EDGE",EDGE,{"disambiguationData":[OSD([sQuery(id+"F15.wireOp",EDGE,"E15.82.0.0"),sQuery(id+"F15.wireOp",EDGE,"E15.82.0.1")])]})});
            var Q126;
            Q126=makeQuery(id+"F16.boolean.opBoolean","COPY",EDGE,{"derivedFrom":makeQuery(id+"F16.opExtrude","SWEPT_EDGE",EDGE,{"disambiguationData":[OSD([sQuery(id+"F15.wireOp",EDGE,"E15.84.0.0"),sQuery(id+"F15.wireOp",EDGE,"E15.84.0.1")])]})});
            var Q127;
            Q127=makeQuery(id+"F16.boolean.opBoolean","COPY",EDGE,{"derivedFrom":makeQuery(id+"F16.opExtrude","SWEPT_EDGE",EDGE,{"disambiguationData":[OSD([sQuery(id+"F15.wireOp",EDGE,"E15.86.0.0"),sQuery(id+"F15.wireOp",EDGE,"E15.86.0.1")])]})});
            var Q128;
            Q128=makeQuery(id+"F16.boolean.opBoolean","COPY",EDGE,{"derivedFrom":makeQuery(id+"F16.opExtrude","SWEPT_EDGE",EDGE,{"disambiguationData":[OSD([sQuery(id+"F15.wireOp",EDGE,"E15.88.0.0"),sQuery(id+"F15.wireOp",EDGE,"E15.88.0.1")])]})});
            var Q129;
            Q129=makeQuery(id+"F16.boolean.opBoolean","COPY",EDGE,{"derivedFrom":makeQuery(id+"F16.opExtrude","SWEPT_EDGE",EDGE,{"disambiguationData":[OSD([sQuery(id+"F15.wireOp",EDGE,"E15.90.0.0"),sQuery(id+"F15.wireOp",EDGE,"E15.90.0.1")])]})});
            var Q130;
            Q130=makeQuery(id+"F16.boolean.opBoolean","COPY",EDGE,{"derivedFrom":makeQuery(id+"F16.opExtrude","SWEPT_EDGE",EDGE,{"disambiguationData":[OSD([sQuery(id+"F15.wireOp",EDGE,"E15.92.0.0"),sQuery(id+"F15.wireOp",EDGE,"E15.92.0.1")])]})});
            var Q131;
            Q131=makeQuery(id+"F16.boolean.opBoolean","COPY",EDGE,{"derivedFrom":makeQuery(id+"F16.opExtrude","SWEPT_EDGE",EDGE,{"disambiguationData":[OSD([sQuery(id+"F15.wireOp",EDGE,"E15.94.0.0"),sQuery(id+"F15.wireOp",EDGE,"E15.94.0.1")])]})});
            var Q132;
            Q132=makeQuery(id+"F16.boolean.opBoolean","COPY",EDGE,{"derivedFrom":makeQuery(id+"F16.opExtrude","SWEPT_EDGE",EDGE,{"disambiguationData":[OSD([sQuery(id+"F15.wireOp",EDGE,"E15.96.0.0"),sQuery(id+"F15.wireOp",EDGE,"E15.96.0.1")])]})});
            var Q133;
            Q133=makeQuery(id+"F16.boolean.opBoolean","COPY",EDGE,{"derivedFrom":makeQuery(id+"F16.opExtrude","SWEPT_EDGE",EDGE,{"disambiguationData":[OSD([sQuery(id+"F15.wireOp",EDGE,"E15.98.0.0"),sQuery(id+"F15.wireOp",EDGE,"E15.98.0.1")])]})});
            var Q134;
            Q134=makeQuery(id+"F18.boolean.opBoolean","COPY",EDGE,{"derivedFrom":makeQuery(id+"F18.opExtrude","SWEPT_EDGE",EDGE,{"disambiguationData":[OSD([sQuery(id+"F17.wireOp",EDGE,"E19.2.0.0"),sQuery(id+"F17.wireOp",EDGE,"E19.2.0.1")])]})});
            var Q135;
            Q135=makeQuery(id+"F16.boolean.opBoolean","COPY",EDGE,{"derivedFrom":makeQuery(id+"F16.opExtrude","SWEPT_EDGE",EDGE,{"disambiguationData":[OSD([sQuery(id+"F15.wireOp",EDGE,"E15.52.0.0"),sQuery(id+"F15.wireOp",EDGE,"E15.52.0.1")])]})});
            var Q136;
            Q136=makeQuery(id+"F14.boolean.opBoolean","COPY",EDGE,{"derivedFrom":makeQuery(id+"F14.opExtrude","SWEPT_EDGE",EDGE,{"disambiguationData":[OSD([sQuery(id+"F13.wireOp",EDGE,"E10.72.0.3"),sQuery(id+"F13.wireOp",EDGE,"E10.73.0.0"),sQuery(id+"F13.wireOp",EDGE,"E10.73.0.3")])]})});
            var Q137;
            Q137=makeQuery(id+"F14.boolean.opBoolean","COPY",EDGE,{"derivedFrom":makeQuery(id+"F14.opExtrude","SWEPT_EDGE",EDGE,{"disambiguationData":[OSD([sQuery(id+"F13.wireOp",EDGE,"E10.74.0.3"),sQuery(id+"F13.wireOp",EDGE,"E10.75.0.0"),sQuery(id+"F13.wireOp",EDGE,"E10.75.0.3")])]})});
            var Q138;
            Q138=makeQuery(id+"F14.boolean.opBoolean","COPY",EDGE,{"derivedFrom":makeQuery(id+"F14.opExtrude","SWEPT_EDGE",EDGE,{"disambiguationData":[OSD([sQuery(id+"F13.wireOp",EDGE,"E10.76.0.3"),sQuery(id+"F13.wireOp",EDGE,"E10.77.0.0"),sQuery(id+"F13.wireOp",EDGE,"E10.77.0.3")])]})});
            var Q139;
            Q139=makeQuery(id+"F14.boolean.opBoolean","COPY",EDGE,{"derivedFrom":makeQuery(id+"F14.opExtrude","SWEPT_EDGE",EDGE,{"disambiguationData":[OSD([sQuery(id+"F13.wireOp",EDGE,"E10.78.0.3"),sQuery(id+"F13.wireOp",EDGE,"E10.79.0.0"),sQuery(id+"F13.wireOp",EDGE,"E10.79.0.3")])]})});
            var Q140;
            Q140=makeQuery(id+"F14.boolean.opBoolean","COPY",EDGE,{"derivedFrom":makeQuery(id+"F14.opExtrude","SWEPT_EDGE",EDGE,{"disambiguationData":[OSD([sQuery(id+"F13.wireOp",EDGE,"E10.80.0.3"),sQuery(id+"F13.wireOp",EDGE,"E10.81.0.0"),sQuery(id+"F13.wireOp",EDGE,"E10.81.0.3")])]})});
            var Q141;
            Q141=makeQuery(id+"F14.boolean.opBoolean","COPY",EDGE,{"derivedFrom":makeQuery(id+"F14.opExtrude","SWEPT_EDGE",EDGE,{"disambiguationData":[OSD([sQuery(id+"F13.wireOp",EDGE,"E10.82.0.3"),sQuery(id+"F13.wireOp",EDGE,"E10.83.0.0"),sQuery(id+"F13.wireOp",EDGE,"E10.83.0.3")])]})});
            var Q142;
            Q142=makeQuery(id+"F14.boolean.opBoolean","COPY",EDGE,{"derivedFrom":makeQuery(id+"F14.opExtrude","SWEPT_EDGE",EDGE,{"disambiguationData":[OSD([sQuery(id+"F13.wireOp",EDGE,"E10.84.0.3"),sQuery(id+"F13.wireOp",EDGE,"E10.85.0.0"),sQuery(id+"F13.wireOp",EDGE,"E10.85.0.3")])]})});
            var Q143;
            Q143=makeQuery(id+"F14.boolean.opBoolean","COPY",EDGE,{"derivedFrom":makeQuery(id+"F14.opExtrude","SWEPT_EDGE",EDGE,{"disambiguationData":[OSD([sQuery(id+"F13.wireOp",EDGE,"E10.86.0.3"),sQuery(id+"F13.wireOp",EDGE,"E10.87.0.0"),sQuery(id+"F13.wireOp",EDGE,"E10.87.0.3")])]})});
            var Q144;
            Q144=makeQuery(id+"F14.boolean.opBoolean","COPY",EDGE,{"derivedFrom":makeQuery(id+"F14.opExtrude","SWEPT_EDGE",EDGE,{"disambiguationData":[OSD([sQuery(id+"F13.wireOp",EDGE,"E10.88.0.3"),sQuery(id+"F13.wireOp",EDGE,"E10.89.0.0"),sQuery(id+"F13.wireOp",EDGE,"E10.89.0.3")])]})});
            var Q145;
            Q145=makeQuery(id+"F14.boolean.opBoolean","COPY",EDGE,{"derivedFrom":makeQuery(id+"F14.opExtrude","SWEPT_EDGE",EDGE,{"disambiguationData":[OSD([sQuery(id+"F13.wireOp",EDGE,"E10.90.0.3"),sQuery(id+"F13.wireOp",EDGE,"E10.91.0.0"),sQuery(id+"F13.wireOp",EDGE,"E10.91.0.3")])]})});
            var Q146;
            Q146=makeQuery(id+"F14.boolean.opBoolean","COPY",EDGE,{"derivedFrom":makeQuery(id+"F14.opExtrude","SWEPT_EDGE",EDGE,{"disambiguationData":[OSD([sQuery(id+"F13.wireOp",EDGE,"E10.92.0.3"),sQuery(id+"F13.wireOp",EDGE,"E10.93.0.0"),sQuery(id+"F13.wireOp",EDGE,"E10.93.0.3")])]})});
            var Q147;
            Q147=makeQuery(id+"F14.boolean.opBoolean","COPY",EDGE,{"derivedFrom":makeQuery(id+"F14.opExtrude","SWEPT_EDGE",EDGE,{"disambiguationData":[OSD([sQuery(id+"F13.wireOp",EDGE,"E10.94.0.3"),sQuery(id+"F13.wireOp",EDGE,"E10.95.0.0"),sQuery(id+"F13.wireOp",EDGE,"E10.95.0.3")])]})});
            var Q148;
            Q148=makeQuery(id+"F14.boolean.opBoolean","COPY",EDGE,{"derivedFrom":makeQuery(id+"F14.opExtrude","SWEPT_EDGE",EDGE,{"disambiguationData":[OSD([sQuery(id+"F13.wireOp",EDGE,"E10.96.0.3"),sQuery(id+"F13.wireOp",EDGE,"E10.97.0.0"),sQuery(id+"F13.wireOp",EDGE,"E10.97.0.3")])]})});
            var Q149;
            Q149=makeQuery(id+"F14.boolean.opBoolean","COPY",EDGE,{"derivedFrom":makeQuery(id+"F14.opExtrude","SWEPT_EDGE",EDGE,{"disambiguationData":[OSD([sQuery(id+"F13.wireOp",EDGE,"E10.98.0.3"),sQuery(id+"F13.wireOp",EDGE,"E10.99.0.0"),sQuery(id+"F13.wireOp",EDGE,"E10.99.0.3")])]})});
            var Q150;
            Q150=makeQuery(id+"F16.boolean.opBoolean","COPY",EDGE,{"derivedFrom":makeQuery(id+"F16.opExtrude","SWEPT_EDGE",EDGE,{"disambiguationData":[OSD([sQuery(id+"F15.wireOp",EDGE,"E15.2.0.1"),sQuery(id+"F15.wireOp",EDGE,"E15.2.0.2")])]})});
            var Q151;
            Q151=makeQuery(id+"F16.boolean.opBoolean","COPY",EDGE,{"derivedFrom":makeQuery(id+"F16.opExtrude","SWEPT_EDGE",EDGE,{"disambiguationData":[OSD([sQuery(id+"F15.wireOp",EDGE,"E15.4.0.1"),sQuery(id+"F15.wireOp",EDGE,"E15.4.0.2")])]})});
            var Q152;
            Q152=makeQuery(id+"F16.boolean.opBoolean","COPY",EDGE,{"derivedFrom":makeQuery(id+"F16.opExtrude","SWEPT_EDGE",EDGE,{"disambiguationData":[OSD([sQuery(id+"F15.wireOp",EDGE,"E15.6.0.1"),sQuery(id+"F15.wireOp",EDGE,"E15.6.0.2")])]})});
            var Q153;
            Q153=makeQuery(id+"F16.boolean.opBoolean","COPY",EDGE,{"derivedFrom":makeQuery(id+"F16.opExtrude","SWEPT_EDGE",EDGE,{"disambiguationData":[OSD([sQuery(id+"F15.wireOp",EDGE,"E15.8.0.1"),sQuery(id+"F15.wireOp",EDGE,"E15.8.0.2")])]})});
            var Q154;
            Q154=makeQuery(id+"F16.boolean.opBoolean","COPY",EDGE,{"derivedFrom":makeQuery(id+"F16.opExtrude","SWEPT_EDGE",EDGE,{"disambiguationData":[OSD([sQuery(id+"F15.wireOp",EDGE,"E15.10.0.1"),sQuery(id+"F15.wireOp",EDGE,"E15.10.0.2")])]})});
            var Q155;
            Q155=makeQuery(id+"F16.boolean.opBoolean","COPY",EDGE,{"derivedFrom":makeQuery(id+"F16.opExtrude","SWEPT_EDGE",EDGE,{"disambiguationData":[OSD([sQuery(id+"F15.wireOp",EDGE,"E15.12.0.1"),sQuery(id+"F15.wireOp",EDGE,"E15.12.0.2")])]})});
            var Q156;
            Q156=makeQuery(id+"F16.boolean.opBoolean","COPY",EDGE,{"derivedFrom":makeQuery(id+"F16.opExtrude","SWEPT_EDGE",EDGE,{"disambiguationData":[OSD([sQuery(id+"F15.wireOp",EDGE,"E15.14.0.1"),sQuery(id+"F15.wireOp",EDGE,"E15.14.0.2")])]})});
            var Q157;
            Q157=makeQuery(id+"F16.boolean.opBoolean","COPY",EDGE,{"derivedFrom":makeQuery(id+"F16.opExtrude","SWEPT_EDGE",EDGE,{"disambiguationData":[OSD([sQuery(id+"F15.wireOp",EDGE,"E15.16.0.1"),sQuery(id+"F15.wireOp",EDGE,"E15.16.0.2")])]})});
            var Q158;
            Q158=makeQuery(id+"F16.boolean.opBoolean","COPY",EDGE,{"derivedFrom":makeQuery(id+"F16.opExtrude","SWEPT_EDGE",EDGE,{"disambiguationData":[OSD([sQuery(id+"F15.wireOp",EDGE,"E15.18.0.1"),sQuery(id+"F15.wireOp",EDGE,"E15.18.0.2")])]})});
            var Q159;
            Q159=makeQuery(id+"F16.boolean.opBoolean","COPY",EDGE,{"derivedFrom":makeQuery(id+"F16.opExtrude","SWEPT_EDGE",EDGE,{"disambiguationData":[OSD([sQuery(id+"F15.wireOp",EDGE,"E15.20.0.1"),sQuery(id+"F15.wireOp",EDGE,"E15.20.0.2")])]})});
            var Q160;
            Q160=makeQuery(id+"F16.boolean.opBoolean","COPY",EDGE,{"derivedFrom":makeQuery(id+"F16.opExtrude","SWEPT_EDGE",EDGE,{"disambiguationData":[OSD([sQuery(id+"F15.wireOp",EDGE,"E15.22.0.1"),sQuery(id+"F15.wireOp",EDGE,"E15.22.0.2")])]})});
            var Q161;
            Q161=makeQuery(id+"F16.boolean.opBoolean","COPY",EDGE,{"derivedFrom":makeQuery(id+"F16.opExtrude","SWEPT_EDGE",EDGE,{"disambiguationData":[OSD([sQuery(id+"F15.wireOp",EDGE,"E15.24.0.1"),sQuery(id+"F15.wireOp",EDGE,"E15.24.0.2")])]})});
            var Q162;
            Q162=makeQuery(id+"F16.boolean.opBoolean","COPY",EDGE,{"derivedFrom":makeQuery(id+"F16.opExtrude","SWEPT_EDGE",EDGE,{"disambiguationData":[OSD([sQuery(id+"F15.wireOp",EDGE,"E15.26.0.1"),sQuery(id+"F15.wireOp",EDGE,"E15.26.0.2")])]})});
            var Q163;
            Q163=makeQuery(id+"F16.boolean.opBoolean","COPY",EDGE,{"derivedFrom":makeQuery(id+"F16.opExtrude","SWEPT_EDGE",EDGE,{"disambiguationData":[OSD([sQuery(id+"F15.wireOp",EDGE,"E15.28.0.1"),sQuery(id+"F15.wireOp",EDGE,"E15.28.0.2")])]})});
            var Q164;
            Q164=makeQuery(id+"F16.boolean.opBoolean","COPY",EDGE,{"derivedFrom":makeQuery(id+"F16.opExtrude","SWEPT_EDGE",EDGE,{"disambiguationData":[OSD([sQuery(id+"F15.wireOp",EDGE,"E15.30.0.1"),sQuery(id+"F15.wireOp",EDGE,"E15.30.0.2")])]})});
            var Q165;
            Q165=makeQuery(id+"F16.boolean.opBoolean","COPY",EDGE,{"derivedFrom":makeQuery(id+"F16.opExtrude","SWEPT_EDGE",EDGE,{"disambiguationData":[OSD([sQuery(id+"F15.wireOp",EDGE,"E15.32.0.1"),sQuery(id+"F15.wireOp",EDGE,"E15.32.0.2")])]})});
            var Q166;
            Q166=makeQuery(id+"F16.boolean.opBoolean","COPY",EDGE,{"derivedFrom":makeQuery(id+"F16.opExtrude","SWEPT_EDGE",EDGE,{"disambiguationData":[OSD([sQuery(id+"F15.wireOp",EDGE,"E15.34.0.1"),sQuery(id+"F15.wireOp",EDGE,"E15.34.0.2")])]})});
            var Q167;
            Q167=makeQuery(id+"F16.boolean.opBoolean","COPY",EDGE,{"derivedFrom":makeQuery(id+"F16.opExtrude","SWEPT_EDGE",EDGE,{"disambiguationData":[OSD([sQuery(id+"F15.wireOp",EDGE,"E15.36.0.1"),sQuery(id+"F15.wireOp",EDGE,"E15.36.0.2")])]})});
            var Q168;
            Q168=makeQuery(id+"F16.boolean.opBoolean","COPY",EDGE,{"derivedFrom":makeQuery(id+"F16.opExtrude","SWEPT_EDGE",EDGE,{"disambiguationData":[OSD([sQuery(id+"F15.wireOp",EDGE,"E15.38.0.1"),sQuery(id+"F15.wireOp",EDGE,"E15.38.0.2")])]})});
            var Q169;
            Q169=makeQuery(id+"F16.boolean.opBoolean","COPY",EDGE,{"derivedFrom":makeQuery(id+"F16.opExtrude","SWEPT_EDGE",EDGE,{"disambiguationData":[OSD([sQuery(id+"F15.wireOp",EDGE,"E15.40.0.1"),sQuery(id+"F15.wireOp",EDGE,"E15.40.0.2")])]})});
            var Q170;
            Q170=makeQuery(id+"F16.boolean.opBoolean","COPY",EDGE,{"derivedFrom":makeQuery(id+"F16.opExtrude","SWEPT_EDGE",EDGE,{"disambiguationData":[OSD([sQuery(id+"F15.wireOp",EDGE,"E15.42.0.1"),sQuery(id+"F15.wireOp",EDGE,"E15.42.0.2")])]})});
            var Q171;
            Q171=makeQuery(id+"F16.boolean.opBoolean","COPY",EDGE,{"derivedFrom":makeQuery(id+"F16.opExtrude","SWEPT_EDGE",EDGE,{"disambiguationData":[OSD([sQuery(id+"F15.wireOp",EDGE,"E15.44.0.1"),sQuery(id+"F15.wireOp",EDGE,"E15.44.0.2")])]})});
            var Q172;
            Q172=makeQuery(id+"F16.boolean.opBoolean","COPY",EDGE,{"derivedFrom":makeQuery(id+"F16.opExtrude","SWEPT_EDGE",EDGE,{"disambiguationData":[OSD([sQuery(id+"F15.wireOp",EDGE,"E15.46.0.1"),sQuery(id+"F15.wireOp",EDGE,"E15.46.0.2")])]})});
            var Q173;
            Q173=makeQuery(id+"F16.boolean.opBoolean","COPY",EDGE,{"derivedFrom":makeQuery(id+"F16.opExtrude","SWEPT_EDGE",EDGE,{"disambiguationData":[OSD([sQuery(id+"F15.wireOp",EDGE,"E15.48.0.1"),sQuery(id+"F15.wireOp",EDGE,"E15.48.0.2")])]})});
            var Q174;
            Q174=makeQuery(id+"F16.boolean.opBoolean","COPY",EDGE,{"derivedFrom":makeQuery(id+"F16.opExtrude","SWEPT_EDGE",EDGE,{"disambiguationData":[OSD([sQuery(id+"F15.wireOp",EDGE,"E15.50.0.1"),sQuery(id+"F15.wireOp",EDGE,"E15.50.0.2")])]})});
            var Q175;
            Q175=makeQuery(id+"F16.boolean.opBoolean","COPY",EDGE,{"derivedFrom":makeQuery(id+"F16.opExtrude","SWEPT_EDGE",EDGE,{"disambiguationData":[OSD([sQuery(id+"F15.wireOp",EDGE,"E15.52.0.1"),sQuery(id+"F15.wireOp",EDGE,"E15.52.0.2")])]})});
            var Q176;
            Q176=makeQuery(id+"F16.boolean.opBoolean","COPY",EDGE,{"derivedFrom":makeQuery(id+"F16.opExtrude","SWEPT_EDGE",EDGE,{"disambiguationData":[OSD([sQuery(id+"F15.wireOp",EDGE,"E15.54.0.1"),sQuery(id+"F15.wireOp",EDGE,"E15.54.0.2")])]})});
            var Q177;
            Q177=makeQuery(id+"F16.boolean.opBoolean","COPY",EDGE,{"derivedFrom":makeQuery(id+"F16.opExtrude","SWEPT_EDGE",EDGE,{"disambiguationData":[OSD([sQuery(id+"F15.wireOp",EDGE,"E15.56.0.1"),sQuery(id+"F15.wireOp",EDGE,"E15.56.0.2")])]})});
            var Q178;
            Q178=makeQuery(id+"F16.boolean.opBoolean","COPY",EDGE,{"derivedFrom":makeQuery(id+"F16.opExtrude","SWEPT_EDGE",EDGE,{"disambiguationData":[OSD([sQuery(id+"F15.wireOp",EDGE,"E15.58.0.1"),sQuery(id+"F15.wireOp",EDGE,"E15.58.0.2")])]})});
            var Q179;
            Q179=makeQuery(id+"F16.boolean.opBoolean","COPY",EDGE,{"derivedFrom":makeQuery(id+"F16.opExtrude","SWEPT_EDGE",EDGE,{"disambiguationData":[OSD([sQuery(id+"F15.wireOp",EDGE,"E15.60.0.1"),sQuery(id+"F15.wireOp",EDGE,"E15.60.0.2")])]})});
            var Q180;
            Q180=makeQuery(id+"F16.boolean.opBoolean","COPY",EDGE,{"derivedFrom":makeQuery(id+"F16.opExtrude","SWEPT_EDGE",EDGE,{"disambiguationData":[OSD([sQuery(id+"F15.wireOp",EDGE,"E15.62.0.1"),sQuery(id+"F15.wireOp",EDGE,"E15.62.0.2")])]})});
            var Q181;
            Q181=makeQuery(id+"F16.boolean.opBoolean","COPY",EDGE,{"derivedFrom":makeQuery(id+"F16.opExtrude","SWEPT_EDGE",EDGE,{"disambiguationData":[OSD([sQuery(id+"F15.wireOp",EDGE,"E15.64.0.1"),sQuery(id+"F15.wireOp",EDGE,"E15.64.0.2")])]})});
            var Q182;
            Q182=makeQuery(id+"F16.boolean.opBoolean","COPY",EDGE,{"derivedFrom":makeQuery(id+"F16.opExtrude","SWEPT_EDGE",EDGE,{"disambiguationData":[OSD([sQuery(id+"F15.wireOp",EDGE,"E15.66.0.1"),sQuery(id+"F15.wireOp",EDGE,"E15.66.0.2")])]})});
            var Q183;
            Q183=makeQuery(id+"F16.boolean.opBoolean","COPY",EDGE,{"derivedFrom":makeQuery(id+"F16.opExtrude","SWEPT_EDGE",EDGE,{"disambiguationData":[OSD([sQuery(id+"F15.wireOp",EDGE,"E15.68.0.1"),sQuery(id+"F15.wireOp",EDGE,"E15.68.0.2")])]})});
            var Q184;
            Q184=makeQuery(id+"F16.boolean.opBoolean","COPY",EDGE,{"derivedFrom":makeQuery(id+"F16.opExtrude","SWEPT_EDGE",EDGE,{"disambiguationData":[OSD([sQuery(id+"F15.wireOp",EDGE,"E15.70.0.1"),sQuery(id+"F15.wireOp",EDGE,"E15.70.0.2")])]})});
            var Q185;
            Q185=makeQuery(id+"F16.boolean.opBoolean","COPY",EDGE,{"derivedFrom":makeQuery(id+"F16.opExtrude","SWEPT_EDGE",EDGE,{"disambiguationData":[OSD([sQuery(id+"F15.wireOp",EDGE,"E15.72.0.1"),sQuery(id+"F15.wireOp",EDGE,"E15.72.0.2")])]})});
            var Q186;
            Q186=makeQuery(id+"F16.boolean.opBoolean","COPY",EDGE,{"derivedFrom":makeQuery(id+"F16.opExtrude","SWEPT_EDGE",EDGE,{"disambiguationData":[OSD([sQuery(id+"F15.wireOp",EDGE,"E15.74.0.1"),sQuery(id+"F15.wireOp",EDGE,"E15.74.0.2")])]})});
            var Q187;
            Q187=makeQuery(id+"F16.boolean.opBoolean","COPY",EDGE,{"derivedFrom":makeQuery(id+"F16.opExtrude","SWEPT_EDGE",EDGE,{"disambiguationData":[OSD([sQuery(id+"F15.wireOp",EDGE,"E15.76.0.1"),sQuery(id+"F15.wireOp",EDGE,"E15.76.0.2")])]})});
            var Q188;
            Q188=makeQuery(id+"F16.boolean.opBoolean","COPY",EDGE,{"derivedFrom":makeQuery(id+"F16.opExtrude","SWEPT_EDGE",EDGE,{"disambiguationData":[OSD([sQuery(id+"F15.wireOp",EDGE,"E15.78.0.1"),sQuery(id+"F15.wireOp",EDGE,"E15.78.0.2")])]})});
            var Q189;
            Q189=makeQuery(id+"F16.boolean.opBoolean","COPY",EDGE,{"derivedFrom":makeQuery(id+"F16.opExtrude","SWEPT_EDGE",EDGE,{"disambiguationData":[OSD([sQuery(id+"F15.wireOp",EDGE,"E15.80.0.1"),sQuery(id+"F15.wireOp",EDGE,"E15.80.0.2")])]})});
            var Q190;
            Q190=makeQuery(id+"F16.boolean.opBoolean","COPY",EDGE,{"derivedFrom":makeQuery(id+"F16.opExtrude","SWEPT_EDGE",EDGE,{"disambiguationData":[OSD([sQuery(id+"F15.wireOp",EDGE,"E15.82.0.1"),sQuery(id+"F15.wireOp",EDGE,"E15.82.0.2")])]})});
            var Q191;
            Q191=makeQuery(id+"F16.boolean.opBoolean","COPY",EDGE,{"derivedFrom":makeQuery(id+"F16.opExtrude","SWEPT_EDGE",EDGE,{"disambiguationData":[OSD([sQuery(id+"F15.wireOp",EDGE,"E15.84.0.1"),sQuery(id+"F15.wireOp",EDGE,"E15.84.0.2")])]})});
            var Q192;
            Q192=makeQuery(id+"F16.boolean.opBoolean","COPY",EDGE,{"derivedFrom":makeQuery(id+"F16.opExtrude","SWEPT_EDGE",EDGE,{"disambiguationData":[OSD([sQuery(id+"F15.wireOp",EDGE,"E15.86.0.1"),sQuery(id+"F15.wireOp",EDGE,"E15.86.0.2")])]})});
            var Q193;
            Q193=makeQuery(id+"F16.boolean.opBoolean","COPY",EDGE,{"derivedFrom":makeQuery(id+"F16.opExtrude","SWEPT_EDGE",EDGE,{"disambiguationData":[OSD([sQuery(id+"F15.wireOp",EDGE,"E15.88.0.1"),sQuery(id+"F15.wireOp",EDGE,"E15.88.0.2")])]})});
            var Q194;
            Q194=makeQuery(id+"F16.boolean.opBoolean","COPY",EDGE,{"derivedFrom":makeQuery(id+"F16.opExtrude","SWEPT_EDGE",EDGE,{"disambiguationData":[OSD([sQuery(id+"F15.wireOp",EDGE,"E15.90.0.1"),sQuery(id+"F15.wireOp",EDGE,"E15.90.0.2")])]})});
            var Q195;
            Q195=makeQuery(id+"F16.boolean.opBoolean","COPY",EDGE,{"derivedFrom":makeQuery(id+"F16.opExtrude","SWEPT_EDGE",EDGE,{"disambiguationData":[OSD([sQuery(id+"F15.wireOp",EDGE,"E15.92.0.1"),sQuery(id+"F15.wireOp",EDGE,"E15.92.0.2")])]})});
            var Q196;
            Q196=makeQuery(id+"F16.boolean.opBoolean","COPY",EDGE,{"derivedFrom":makeQuery(id+"F16.opExtrude","SWEPT_EDGE",EDGE,{"disambiguationData":[OSD([sQuery(id+"F15.wireOp",EDGE,"E15.94.0.1"),sQuery(id+"F15.wireOp",EDGE,"E15.94.0.2")])]})});
            var Q197;
            Q197=makeQuery(id+"F16.boolean.opBoolean","COPY",EDGE,{"derivedFrom":makeQuery(id+"F16.opExtrude","SWEPT_EDGE",EDGE,{"disambiguationData":[OSD([sQuery(id+"F15.wireOp",EDGE,"E15.96.0.1"),sQuery(id+"F15.wireOp",EDGE,"E15.96.0.2")])]})});
            var Q198;
            Q198=makeQuery(id+"F16.boolean.opBoolean","COPY",EDGE,{"derivedFrom":makeQuery(id+"F16.opExtrude","SWEPT_EDGE",EDGE,{"disambiguationData":[OSD([sQuery(id+"F15.wireOp",EDGE,"E15.98.0.1"),sQuery(id+"F15.wireOp",EDGE,"E15.98.0.2")])]})});
            fillet(context, id + "F19", {"entities" : qUnion([Q0, Q1, Q2, Q3, Q4, Q5, Q6, Q7, Q8, Q9, Q10, Q11, Q12, Q13, Q14, Q15, Q16, Q17, Q18, Q19, Q20, Q21, Q22, Q23, Q24, Q25, Q26, Q27, Q28, Q29, Q30, Q31, Q32, Q33, Q34, Q35, Q36, Q37, Q38, Q39, Q40, Q41, Q42, Q43, Q44, Q45, Q46, Q47, Q48, Q49, Q50, Q51, Q52, Q53, Q54, Q55, Q56, Q57, Q58, Q59, Q60, Q61, Q62, Q63, Q64, Q65, Q66, Q67, Q68, Q69, Q70, Q71, Q72, Q73, Q74, Q75, Q76, Q77, Q78, Q79, Q80, Q81, Q82, Q83, Q84, Q85, Q86, Q87, Q88, Q89, Q90, Q91, Q92, Q93, Q94, Q95, Q96, Q97, Q98, Q99, Q100, Q101, Q102, Q103, Q104, Q105, Q106, Q107, Q108, Q109, Q110, Q111, Q112, Q113, Q114, Q115, Q116, Q117, Q118, Q119, Q120, Q121, Q122, Q123, Q124, Q125, Q126, Q127, Q128, Q129, Q130, Q131, Q132, Q133, Q134, Q135, Q136, Q137, Q138, Q139, Q140, Q141, Q142, Q143, Q144, Q145, Q146, Q147, Q148, Q149, Q150, Q151, Q152, Q153, Q154, Q155, Q156, Q157, Q158, Q159, Q160, Q161, Q162, Q163, Q164, Q165, Q166, Q167, Q168, Q169, Q170, Q171, Q172, Q173, Q174, Q175, Q176, Q177, Q178, Q179, Q180, Q181, Q182, Q183, Q184, Q185, Q186, Q187, Q188, Q189, Q190, Q191, Q192, Q193, Q194, Q195, Q196, Q197, Q198]), "radius" : 0.79 * mm, "tangentPropagation" : true, "allowEdgeOverflow" : false});
        }
        {
            var Q0;
            Q0=makeQuery(id+"F18.boolean.opBoolean","COPY",EDGE,{"derivedFrom":makeQuery(id+"F18.opExtrude","SWEPT_EDGE",EDGE,{"disambiguationData":[OSD([sQuery(id+"F0.wireOp",EDGE,"E0.top"),sQuery(id+"F17.wireOp",EDGE,"E19.2.0.0")])]})});
            var Q1;
            Q1=makeQuery(id+"F16.boolean.opBoolean","COPY",EDGE,{"derivedFrom":makeQuery(id+"F16.opExtrude","SWEPT_EDGE",EDGE,{"disambiguationData":[OSD([sQuery(id+"F0.wireOp",EDGE,"E0.top"),sQuery(id+"F15.wireOp",EDGE,"E15.98.0.2")])]})});
            var Q2;
            Q2=makeQuery(id+"F16.boolean.opBoolean","COPY",EDGE,{"derivedFrom":makeQuery(id+"F16.opExtrude","SWEPT_EDGE",EDGE,{"disambiguationData":[OSD([sQuery(id+"F0.wireOp",EDGE,"E0.top"),sQuery(id+"F15.wireOp",EDGE,"E15.98.0.0")])]})});
            var Q3;
            Q3=makeQuery(id+"F16.boolean.opBoolean","COPY",EDGE,{"derivedFrom":makeQuery(id+"F16.opExtrude","SWEPT_EDGE",EDGE,{"disambiguationData":[OSD([sQuery(id+"F0.wireOp",EDGE,"E0.top"),sQuery(id+"F15.wireOp",EDGE,"E15.96.0.2")])]})});
            var Q4;
            Q4=makeQuery(id+"F16.boolean.opBoolean","COPY",EDGE,{"derivedFrom":makeQuery(id+"F16.opExtrude","SWEPT_EDGE",EDGE,{"disambiguationData":[OSD([sQuery(id+"F0.wireOp",EDGE,"E0.top"),sQuery(id+"F15.wireOp",EDGE,"E15.96.0.0")])]})});
            var Q5;
            Q5=makeQuery(id+"F16.boolean.opBoolean","COPY",EDGE,{"derivedFrom":makeQuery(id+"F16.opExtrude","SWEPT_EDGE",EDGE,{"disambiguationData":[OSD([sQuery(id+"F0.wireOp",EDGE,"E0.top"),sQuery(id+"F15.wireOp",EDGE,"E15.94.0.2")])]})});
            var Q6;
            Q6=makeQuery(id+"F16.boolean.opBoolean","COPY",EDGE,{"derivedFrom":makeQuery(id+"F16.opExtrude","SWEPT_EDGE",EDGE,{"disambiguationData":[OSD([sQuery(id+"F0.wireOp",EDGE,"E0.top"),sQuery(id+"F15.wireOp",EDGE,"E15.94.0.0")])]})});
            var Q7;
            Q7=makeQuery(id+"F16.boolean.opBoolean","COPY",EDGE,{"derivedFrom":makeQuery(id+"F16.opExtrude","SWEPT_EDGE",EDGE,{"disambiguationData":[OSD([sQuery(id+"F0.wireOp",EDGE,"E0.top"),sQuery(id+"F15.wireOp",EDGE,"E15.92.0.2")])]})});
            var Q8;
            Q8=makeQuery(id+"F16.boolean.opBoolean","COPY",EDGE,{"derivedFrom":makeQuery(id+"F16.opExtrude","SWEPT_EDGE",EDGE,{"disambiguationData":[OSD([sQuery(id+"F0.wireOp",EDGE,"E0.top"),sQuery(id+"F15.wireOp",EDGE,"E15.92.0.0")])]})});
            var Q9;
            Q9=makeQuery(id+"F16.boolean.opBoolean","COPY",EDGE,{"derivedFrom":makeQuery(id+"F16.opExtrude","SWEPT_EDGE",EDGE,{"disambiguationData":[OSD([sQuery(id+"F0.wireOp",EDGE,"E0.top"),sQuery(id+"F15.wireOp",EDGE,"E15.90.0.2")])]})});
            var Q10;
            Q10=makeQuery(id+"F16.boolean.opBoolean","COPY",EDGE,{"derivedFrom":makeQuery(id+"F16.opExtrude","SWEPT_EDGE",EDGE,{"disambiguationData":[OSD([sQuery(id+"F0.wireOp",EDGE,"E0.top"),sQuery(id+"F15.wireOp",EDGE,"E15.90.0.0")])]})});
            var Q11;
            Q11=makeQuery(id+"F16.boolean.opBoolean","COPY",EDGE,{"derivedFrom":makeQuery(id+"F16.opExtrude","SWEPT_EDGE",EDGE,{"disambiguationData":[OSD([sQuery(id+"F0.wireOp",EDGE,"E0.top"),sQuery(id+"F15.wireOp",EDGE,"E15.88.0.2")])]})});
            var Q12;
            Q12=makeQuery(id+"F16.boolean.opBoolean","COPY",EDGE,{"derivedFrom":makeQuery(id+"F16.opExtrude","SWEPT_EDGE",EDGE,{"disambiguationData":[OSD([sQuery(id+"F0.wireOp",EDGE,"E0.top"),sQuery(id+"F15.wireOp",EDGE,"E15.88.0.0")])]})});
            var Q13;
            Q13=makeQuery(id+"F16.boolean.opBoolean","COPY",EDGE,{"derivedFrom":makeQuery(id+"F16.opExtrude","SWEPT_EDGE",EDGE,{"disambiguationData":[OSD([sQuery(id+"F0.wireOp",EDGE,"E0.top"),sQuery(id+"F15.wireOp",EDGE,"E15.86.0.2")])]})});
            var Q14;
            Q14=makeQuery(id+"F16.boolean.opBoolean","COPY",EDGE,{"derivedFrom":makeQuery(id+"F16.opExtrude","SWEPT_EDGE",EDGE,{"disambiguationData":[OSD([sQuery(id+"F0.wireOp",EDGE,"E0.top"),sQuery(id+"F15.wireOp",EDGE,"E15.86.0.0")])]})});
            var Q15;
            Q15=makeQuery(id+"F16.boolean.opBoolean","COPY",EDGE,{"derivedFrom":makeQuery(id+"F16.opExtrude","SWEPT_EDGE",EDGE,{"disambiguationData":[OSD([sQuery(id+"F0.wireOp",EDGE,"E0.top"),sQuery(id+"F15.wireOp",EDGE,"E15.84.0.2")])]})});
            var Q16;
            Q16=makeQuery(id+"F16.boolean.opBoolean","COPY",EDGE,{"derivedFrom":makeQuery(id+"F16.opExtrude","SWEPT_EDGE",EDGE,{"disambiguationData":[OSD([sQuery(id+"F0.wireOp",EDGE,"E0.top"),sQuery(id+"F15.wireOp",EDGE,"E15.84.0.0")])]})});
            var Q17;
            Q17=makeQuery(id+"F16.boolean.opBoolean","COPY",EDGE,{"derivedFrom":makeQuery(id+"F16.opExtrude","SWEPT_EDGE",EDGE,{"disambiguationData":[OSD([sQuery(id+"F0.wireOp",EDGE,"E0.top"),sQuery(id+"F15.wireOp",EDGE,"E15.82.0.2")])]})});
            var Q18;
            Q18=makeQuery(id+"F16.boolean.opBoolean","COPY",EDGE,{"derivedFrom":makeQuery(id+"F16.opExtrude","SWEPT_EDGE",EDGE,{"disambiguationData":[OSD([sQuery(id+"F0.wireOp",EDGE,"E0.top"),sQuery(id+"F15.wireOp",EDGE,"E15.82.0.0")])]})});
            var Q19;
            Q19=makeQuery(id+"F16.boolean.opBoolean","COPY",EDGE,{"derivedFrom":makeQuery(id+"F16.opExtrude","SWEPT_EDGE",EDGE,{"disambiguationData":[OSD([sQuery(id+"F0.wireOp",EDGE,"E0.top"),sQuery(id+"F15.wireOp",EDGE,"E15.80.0.2")])]})});
            var Q20;
            Q20=makeQuery(id+"F16.boolean.opBoolean","COPY",EDGE,{"derivedFrom":makeQuery(id+"F16.opExtrude","SWEPT_EDGE",EDGE,{"disambiguationData":[OSD([sQuery(id+"F0.wireOp",EDGE,"E0.top"),sQuery(id+"F15.wireOp",EDGE,"E15.80.0.0")])]})});
            var Q21;
            Q21=makeQuery(id+"F16.boolean.opBoolean","COPY",EDGE,{"derivedFrom":makeQuery(id+"F16.opExtrude","SWEPT_EDGE",EDGE,{"disambiguationData":[OSD([sQuery(id+"F0.wireOp",EDGE,"E0.top"),sQuery(id+"F15.wireOp",EDGE,"E15.78.0.2")])]})});
            var Q22;
            Q22=makeQuery(id+"F16.boolean.opBoolean","COPY",EDGE,{"derivedFrom":makeQuery(id+"F16.opExtrude","SWEPT_EDGE",EDGE,{"disambiguationData":[OSD([sQuery(id+"F0.wireOp",EDGE,"E0.top"),sQuery(id+"F15.wireOp",EDGE,"E15.78.0.0")])]})});
            var Q23;
            Q23=makeQuery(id+"F16.boolean.opBoolean","COPY",EDGE,{"derivedFrom":makeQuery(id+"F16.opExtrude","SWEPT_EDGE",EDGE,{"disambiguationData":[OSD([sQuery(id+"F0.wireOp",EDGE,"E0.top"),sQuery(id+"F15.wireOp",EDGE,"E15.76.0.2")])]})});
            var Q24;
            Q24=makeQuery(id+"F16.boolean.opBoolean","COPY",EDGE,{"derivedFrom":makeQuery(id+"F16.opExtrude","SWEPT_EDGE",EDGE,{"disambiguationData":[OSD([sQuery(id+"F0.wireOp",EDGE,"E0.top"),sQuery(id+"F15.wireOp",EDGE,"E15.76.0.0")])]})});
            var Q25;
            Q25=makeQuery(id+"F16.boolean.opBoolean","COPY",EDGE,{"derivedFrom":makeQuery(id+"F16.opExtrude","SWEPT_EDGE",EDGE,{"disambiguationData":[OSD([sQuery(id+"F0.wireOp",EDGE,"E0.top"),sQuery(id+"F15.wireOp",EDGE,"E15.74.0.2")])]})});
            var Q26;
            Q26=makeQuery(id+"F16.boolean.opBoolean","COPY",EDGE,{"derivedFrom":makeQuery(id+"F16.opExtrude","SWEPT_EDGE",EDGE,{"disambiguationData":[OSD([sQuery(id+"F0.wireOp",EDGE,"E0.top"),sQuery(id+"F15.wireOp",EDGE,"E15.74.0.0")])]})});
            var Q27;
            Q27=makeQuery(id+"F16.boolean.opBoolean","COPY",EDGE,{"derivedFrom":makeQuery(id+"F16.opExtrude","SWEPT_EDGE",EDGE,{"disambiguationData":[OSD([sQuery(id+"F0.wireOp",EDGE,"E0.top"),sQuery(id+"F15.wireOp",EDGE,"E15.72.0.2")])]})});
            var Q28;
            Q28=makeQuery(id+"F16.boolean.opBoolean","COPY",EDGE,{"derivedFrom":makeQuery(id+"F16.opExtrude","SWEPT_EDGE",EDGE,{"disambiguationData":[OSD([sQuery(id+"F0.wireOp",EDGE,"E0.top"),sQuery(id+"F15.wireOp",EDGE,"E15.70.0.2")])]})});
            var Q29;
            Q29=makeQuery(id+"F16.boolean.opBoolean","COPY",EDGE,{"derivedFrom":makeQuery(id+"F16.opExtrude","SWEPT_EDGE",EDGE,{"disambiguationData":[OSD([sQuery(id+"F0.wireOp",EDGE,"E0.top"),sQuery(id+"F15.wireOp",EDGE,"E15.70.0.0")])]})});
            var Q30;
            Q30=makeQuery(id+"F16.boolean.opBoolean","COPY",EDGE,{"derivedFrom":makeQuery(id+"F16.opExtrude","SWEPT_EDGE",EDGE,{"disambiguationData":[OSD([sQuery(id+"F0.wireOp",EDGE,"E0.top"),sQuery(id+"F15.wireOp",EDGE,"E15.68.0.2")])]})});
            var Q31;
            Q31=makeQuery(id+"F16.boolean.opBoolean","COPY",EDGE,{"derivedFrom":makeQuery(id+"F16.opExtrude","SWEPT_EDGE",EDGE,{"disambiguationData":[OSD([sQuery(id+"F0.wireOp",EDGE,"E0.top"),sQuery(id+"F15.wireOp",EDGE,"E15.66.0.2")])]})});
            var Q32;
            Q32=makeQuery(id+"F16.boolean.opBoolean","COPY",EDGE,{"derivedFrom":makeQuery(id+"F16.opExtrude","SWEPT_EDGE",EDGE,{"disambiguationData":[OSD([sQuery(id+"F0.wireOp",EDGE,"E0.top"),sQuery(id+"F15.wireOp",EDGE,"E15.68.0.0")])]})});
            var Q33;
            Q33=makeQuery(id+"F16.boolean.opBoolean","COPY",EDGE,{"derivedFrom":makeQuery(id+"F16.opExtrude","SWEPT_EDGE",EDGE,{"disambiguationData":[OSD([sQuery(id+"F0.wireOp",EDGE,"E0.top"),sQuery(id+"F15.wireOp",EDGE,"E15.66.0.0")])]})});
            var Q34;
            Q34=makeQuery(id+"F16.boolean.opBoolean","COPY",EDGE,{"derivedFrom":makeQuery(id+"F16.opExtrude","SWEPT_EDGE",EDGE,{"disambiguationData":[OSD([sQuery(id+"F0.wireOp",EDGE,"E0.top"),sQuery(id+"F15.wireOp",EDGE,"E15.64.0.2")])]})});
            var Q35;
            Q35=makeQuery(id+"F16.boolean.opBoolean","COPY",EDGE,{"derivedFrom":makeQuery(id+"F16.opExtrude","SWEPT_EDGE",EDGE,{"disambiguationData":[OSD([sQuery(id+"F0.wireOp",EDGE,"E0.top"),sQuery(id+"F15.wireOp",EDGE,"E15.64.0.0")])]})});
            var Q36;
            Q36=makeQuery(id+"F16.boolean.opBoolean","COPY",EDGE,{"derivedFrom":makeQuery(id+"F16.opExtrude","SWEPT_EDGE",EDGE,{"disambiguationData":[OSD([sQuery(id+"F0.wireOp",EDGE,"E0.top"),sQuery(id+"F15.wireOp",EDGE,"E15.62.0.2")])]})});
            var Q37;
            Q37=makeQuery(id+"F16.boolean.opBoolean","COPY",EDGE,{"derivedFrom":makeQuery(id+"F16.opExtrude","SWEPT_EDGE",EDGE,{"disambiguationData":[OSD([sQuery(id+"F0.wireOp",EDGE,"E0.top"),sQuery(id+"F15.wireOp",EDGE,"E15.62.0.0")])]})});
            var Q38;
            Q38=makeQuery(id+"F16.boolean.opBoolean","COPY",EDGE,{"derivedFrom":makeQuery(id+"F16.opExtrude","SWEPT_EDGE",EDGE,{"disambiguationData":[OSD([sQuery(id+"F0.wireOp",EDGE,"E0.top"),sQuery(id+"F15.wireOp",EDGE,"E15.60.0.2")])]})});
            var Q39;
            Q39=makeQuery(id+"F16.boolean.opBoolean","COPY",EDGE,{"derivedFrom":makeQuery(id+"F16.opExtrude","SWEPT_EDGE",EDGE,{"disambiguationData":[OSD([sQuery(id+"F0.wireOp",EDGE,"E0.top"),sQuery(id+"F15.wireOp",EDGE,"E15.60.0.0")])]})});
            var Q40;
            Q40=makeQuery(id+"F16.boolean.opBoolean","COPY",EDGE,{"derivedFrom":makeQuery(id+"F16.opExtrude","SWEPT_EDGE",EDGE,{"disambiguationData":[OSD([sQuery(id+"F0.wireOp",EDGE,"E0.top"),sQuery(id+"F15.wireOp",EDGE,"E15.58.0.2")])]})});
            var Q41;
            Q41=makeQuery(id+"F16.boolean.opBoolean","COPY",EDGE,{"derivedFrom":makeQuery(id+"F16.opExtrude","SWEPT_EDGE",EDGE,{"disambiguationData":[OSD([sQuery(id+"F0.wireOp",EDGE,"E0.top"),sQuery(id+"F15.wireOp",EDGE,"E15.58.0.0")])]})});
            var Q42;
            Q42=makeQuery(id+"F16.boolean.opBoolean","COPY",EDGE,{"derivedFrom":makeQuery(id+"F16.opExtrude","SWEPT_EDGE",EDGE,{"disambiguationData":[OSD([sQuery(id+"F0.wireOp",EDGE,"E0.top"),sQuery(id+"F15.wireOp",EDGE,"E15.56.0.2")])]})});
            var Q43;
            Q43=makeQuery(id+"F16.boolean.opBoolean","COPY",EDGE,{"derivedFrom":makeQuery(id+"F16.opExtrude","SWEPT_EDGE",EDGE,{"disambiguationData":[OSD([sQuery(id+"F0.wireOp",EDGE,"E0.top"),sQuery(id+"F15.wireOp",EDGE,"E15.56.0.0")])]})});
            var Q44;
            Q44=makeQuery(id+"F16.boolean.opBoolean","COPY",EDGE,{"derivedFrom":makeQuery(id+"F16.opExtrude","SWEPT_EDGE",EDGE,{"disambiguationData":[OSD([sQuery(id+"F0.wireOp",EDGE,"E0.top"),sQuery(id+"F15.wireOp",EDGE,"E15.54.0.2")])]})});
            var Q45;
            Q45=makeQuery(id+"F16.boolean.opBoolean","COPY",EDGE,{"derivedFrom":makeQuery(id+"F16.opExtrude","SWEPT_EDGE",EDGE,{"disambiguationData":[OSD([sQuery(id+"F0.wireOp",EDGE,"E0.top"),sQuery(id+"F15.wireOp",EDGE,"E15.54.0.0")])]})});
            var Q46;
            Q46=makeQuery(id+"F16.boolean.opBoolean","COPY",EDGE,{"derivedFrom":makeQuery(id+"F16.opExtrude","SWEPT_EDGE",EDGE,{"disambiguationData":[OSD([sQuery(id+"F0.wireOp",EDGE,"E0.top"),sQuery(id+"F15.wireOp",EDGE,"E15.52.0.2")])]})});
            var Q47;
            Q47=makeQuery(id+"F16.boolean.opBoolean","COPY",EDGE,{"derivedFrom":makeQuery(id+"F16.opExtrude","SWEPT_EDGE",EDGE,{"disambiguationData":[OSD([sQuery(id+"F0.wireOp",EDGE,"E0.top"),sQuery(id+"F15.wireOp",EDGE,"E15.52.0.0")])]})});
            var Q48;
            Q48=makeQuery(id+"F16.boolean.opBoolean","COPY",EDGE,{"derivedFrom":makeQuery(id+"F16.opExtrude","SWEPT_EDGE",EDGE,{"disambiguationData":[OSD([sQuery(id+"F0.wireOp",EDGE,"E0.top"),sQuery(id+"F15.wireOp",EDGE,"E15.50.0.2")])]})});
            var Q49;
            Q49=makeQuery(id+"F16.boolean.opBoolean","COPY",EDGE,{"derivedFrom":makeQuery(id+"F16.opExtrude","SWEPT_EDGE",EDGE,{"disambiguationData":[OSD([sQuery(id+"F0.wireOp",EDGE,"E0.top"),sQuery(id+"F15.wireOp",EDGE,"E15.50.0.0")])]})});
            var Q50;
            Q50=makeQuery(id+"F16.boolean.opBoolean","COPY",EDGE,{"derivedFrom":makeQuery(id+"F16.opExtrude","SWEPT_EDGE",EDGE,{"disambiguationData":[OSD([sQuery(id+"F0.wireOp",EDGE,"E0.top"),sQuery(id+"F15.wireOp",EDGE,"E15.48.0.2")])]})});
            var Q51;
            Q51=makeQuery(id+"F16.boolean.opBoolean","COPY",EDGE,{"derivedFrom":makeQuery(id+"F16.opExtrude","SWEPT_EDGE",EDGE,{"disambiguationData":[OSD([sQuery(id+"F0.wireOp",EDGE,"E0.top"),sQuery(id+"F15.wireOp",EDGE,"E15.48.0.0")])]})});
            var Q52;
            Q52=makeQuery(id+"F16.boolean.opBoolean","COPY",EDGE,{"derivedFrom":makeQuery(id+"F16.opExtrude","SWEPT_EDGE",EDGE,{"disambiguationData":[OSD([sQuery(id+"F0.wireOp",EDGE,"E0.top"),sQuery(id+"F15.wireOp",EDGE,"E15.46.0.2")])]})});
            var Q53;
            Q53=makeQuery(id+"F16.boolean.opBoolean","COPY",EDGE,{"derivedFrom":makeQuery(id+"F16.opExtrude","SWEPT_EDGE",EDGE,{"disambiguationData":[OSD([sQuery(id+"F0.wireOp",EDGE,"E0.top"),sQuery(id+"F15.wireOp",EDGE,"E15.46.0.0")])]})});
            var Q54;
            Q54=makeQuery(id+"F16.boolean.opBoolean","COPY",EDGE,{"derivedFrom":makeQuery(id+"F16.opExtrude","SWEPT_EDGE",EDGE,{"disambiguationData":[OSD([sQuery(id+"F0.wireOp",EDGE,"E0.top"),sQuery(id+"F15.wireOp",EDGE,"E15.44.0.2")])]})});
            var Q55;
            Q55=makeQuery(id+"F16.boolean.opBoolean","COPY",EDGE,{"derivedFrom":makeQuery(id+"F16.opExtrude","SWEPT_EDGE",EDGE,{"disambiguationData":[OSD([sQuery(id+"F0.wireOp",EDGE,"E0.top"),sQuery(id+"F15.wireOp",EDGE,"E15.44.0.0")])]})});
            var Q56;
            Q56=makeQuery(id+"F16.boolean.opBoolean","COPY",EDGE,{"derivedFrom":makeQuery(id+"F16.opExtrude","SWEPT_EDGE",EDGE,{"disambiguationData":[OSD([sQuery(id+"F0.wireOp",EDGE,"E0.top"),sQuery(id+"F15.wireOp",EDGE,"E15.42.0.2")])]})});
            var Q57;
            Q57=makeQuery(id+"F16.boolean.opBoolean","COPY",EDGE,{"derivedFrom":makeQuery(id+"F16.opExtrude","SWEPT_EDGE",EDGE,{"disambiguationData":[OSD([sQuery(id+"F0.wireOp",EDGE,"E0.top"),sQuery(id+"F15.wireOp",EDGE,"E15.42.0.0")])]})});
            var Q58;
            Q58=makeQuery(id+"F16.boolean.opBoolean","COPY",EDGE,{"derivedFrom":makeQuery(id+"F16.opExtrude","SWEPT_EDGE",EDGE,{"disambiguationData":[OSD([sQuery(id+"F0.wireOp",EDGE,"E0.top"),sQuery(id+"F15.wireOp",EDGE,"E15.40.0.2")])]})});
            var Q59;
            Q59=makeQuery(id+"F16.boolean.opBoolean","COPY",EDGE,{"derivedFrom":makeQuery(id+"F16.opExtrude","SWEPT_EDGE",EDGE,{"disambiguationData":[OSD([sQuery(id+"F0.wireOp",EDGE,"E0.top"),sQuery(id+"F15.wireOp",EDGE,"E15.40.0.0")])]})});
            var Q60;
            Q60=makeQuery(id+"F16.boolean.opBoolean","COPY",EDGE,{"derivedFrom":makeQuery(id+"F16.opExtrude","SWEPT_EDGE",EDGE,{"disambiguationData":[OSD([sQuery(id+"F0.wireOp",EDGE,"E0.top"),sQuery(id+"F15.wireOp",EDGE,"E15.38.0.2")])]})});
            var Q61;
            Q61=makeQuery(id+"F16.boolean.opBoolean","COPY",EDGE,{"derivedFrom":makeQuery(id+"F16.opExtrude","SWEPT_EDGE",EDGE,{"disambiguationData":[OSD([sQuery(id+"F0.wireOp",EDGE,"E0.top"),sQuery(id+"F15.wireOp",EDGE,"E15.38.0.0")])]})});
            var Q62;
            Q62=makeQuery(id+"F16.boolean.opBoolean","COPY",EDGE,{"derivedFrom":makeQuery(id+"F16.opExtrude","SWEPT_EDGE",EDGE,{"disambiguationData":[OSD([sQuery(id+"F0.wireOp",EDGE,"E0.top"),sQuery(id+"F15.wireOp",EDGE,"E15.36.0.2")])]})});
            var Q63;
            Q63=makeQuery(id+"F16.boolean.opBoolean","COPY",EDGE,{"derivedFrom":makeQuery(id+"F16.opExtrude","SWEPT_EDGE",EDGE,{"disambiguationData":[OSD([sQuery(id+"F0.wireOp",EDGE,"E0.top"),sQuery(id+"F15.wireOp",EDGE,"E15.36.0.0")])]})});
            var Q64;
            Q64=makeQuery(id+"F16.boolean.opBoolean","COPY",EDGE,{"derivedFrom":makeQuery(id+"F16.opExtrude","SWEPT_EDGE",EDGE,{"disambiguationData":[OSD([sQuery(id+"F0.wireOp",EDGE,"E0.top"),sQuery(id+"F15.wireOp",EDGE,"E15.34.0.2")])]})});
            var Q65;
            Q65=makeQuery(id+"F16.boolean.opBoolean","COPY",EDGE,{"derivedFrom":makeQuery(id+"F16.opExtrude","SWEPT_EDGE",EDGE,{"disambiguationData":[OSD([sQuery(id+"F0.wireOp",EDGE,"E0.top"),sQuery(id+"F15.wireOp",EDGE,"E15.34.0.0")])]})});
            var Q66;
            Q66=makeQuery(id+"F16.boolean.opBoolean","COPY",EDGE,{"derivedFrom":makeQuery(id+"F16.opExtrude","SWEPT_EDGE",EDGE,{"disambiguationData":[OSD([sQuery(id+"F0.wireOp",EDGE,"E0.top"),sQuery(id+"F15.wireOp",EDGE,"E15.32.0.2")])]})});
            var Q67;
            Q67=makeQuery(id+"F16.boolean.opBoolean","COPY",EDGE,{"derivedFrom":makeQuery(id+"F16.opExtrude","SWEPT_EDGE",EDGE,{"disambiguationData":[OSD([sQuery(id+"F0.wireOp",EDGE,"E0.top"),sQuery(id+"F15.wireOp",EDGE,"E15.32.0.0")])]})});
            var Q68;
            Q68=makeQuery(id+"F16.boolean.opBoolean","COPY",EDGE,{"derivedFrom":makeQuery(id+"F16.opExtrude","SWEPT_EDGE",EDGE,{"disambiguationData":[OSD([sQuery(id+"F0.wireOp",EDGE,"E0.top"),sQuery(id+"F15.wireOp",EDGE,"E15.30.0.2")])]})});
            var Q69;
            Q69=makeQuery(id+"F16.boolean.opBoolean","COPY",EDGE,{"derivedFrom":makeQuery(id+"F16.opExtrude","SWEPT_EDGE",EDGE,{"disambiguationData":[OSD([sQuery(id+"F0.wireOp",EDGE,"E0.top"),sQuery(id+"F15.wireOp",EDGE,"E15.30.0.0")])]})});
            var Q70;
            Q70=makeQuery(id+"F16.boolean.opBoolean","COPY",EDGE,{"derivedFrom":makeQuery(id+"F16.opExtrude","SWEPT_EDGE",EDGE,{"disambiguationData":[OSD([sQuery(id+"F0.wireOp",EDGE,"E0.top"),sQuery(id+"F15.wireOp",EDGE,"E15.28.0.2")])]})});
            var Q71;
            Q71=makeQuery(id+"F16.boolean.opBoolean","COPY",EDGE,{"derivedFrom":makeQuery(id+"F16.opExtrude","SWEPT_EDGE",EDGE,{"disambiguationData":[OSD([sQuery(id+"F0.wireOp",EDGE,"E0.top"),sQuery(id+"F15.wireOp",EDGE,"E15.28.0.0")])]})});
            var Q72;
            Q72=makeQuery(id+"F16.boolean.opBoolean","COPY",EDGE,{"derivedFrom":makeQuery(id+"F16.opExtrude","SWEPT_EDGE",EDGE,{"disambiguationData":[OSD([sQuery(id+"F0.wireOp",EDGE,"E0.top"),sQuery(id+"F15.wireOp",EDGE,"E15.26.0.2")])]})});
            var Q73;
            Q73=makeQuery(id+"F16.boolean.opBoolean","COPY",EDGE,{"derivedFrom":makeQuery(id+"F16.opExtrude","SWEPT_EDGE",EDGE,{"disambiguationData":[OSD([sQuery(id+"F0.wireOp",EDGE,"E0.top"),sQuery(id+"F15.wireOp",EDGE,"E15.24.0.2")])]})});
            var Q74;
            Q74=makeQuery(id+"F16.boolean.opBoolean","COPY",EDGE,{"derivedFrom":makeQuery(id+"F16.opExtrude","SWEPT_EDGE",EDGE,{"disambiguationData":[OSD([sQuery(id+"F0.wireOp",EDGE,"E0.top"),sQuery(id+"F15.wireOp",EDGE,"E15.26.0.0")])]})});
            var Q75;
            Q75=makeQuery(id+"F16.boolean.opBoolean","COPY",EDGE,{"derivedFrom":makeQuery(id+"F16.opExtrude","SWEPT_EDGE",EDGE,{"disambiguationData":[OSD([sQuery(id+"F0.wireOp",EDGE,"E0.top"),sQuery(id+"F15.wireOp",EDGE,"E15.24.0.0")])]})});
            var Q76;
            Q76=makeQuery(id+"F16.boolean.opBoolean","COPY",EDGE,{"derivedFrom":makeQuery(id+"F16.opExtrude","SWEPT_EDGE",EDGE,{"disambiguationData":[OSD([sQuery(id+"F0.wireOp",EDGE,"E0.top"),sQuery(id+"F15.wireOp",EDGE,"E15.22.0.2")])]})});
            var Q77;
            Q77=makeQuery(id+"F16.boolean.opBoolean","COPY",EDGE,{"derivedFrom":makeQuery(id+"F16.opExtrude","SWEPT_EDGE",EDGE,{"disambiguationData":[OSD([sQuery(id+"F0.wireOp",EDGE,"E0.top"),sQuery(id+"F15.wireOp",EDGE,"E15.22.0.0")])]})});
            var Q78;
            Q78=makeQuery(id+"F16.boolean.opBoolean","COPY",EDGE,{"derivedFrom":makeQuery(id+"F16.opExtrude","SWEPT_EDGE",EDGE,{"disambiguationData":[OSD([sQuery(id+"F0.wireOp",EDGE,"E0.top"),sQuery(id+"F15.wireOp",EDGE,"E15.20.0.2")])]})});
            var Q79;
            Q79=makeQuery(id+"F16.boolean.opBoolean","COPY",EDGE,{"derivedFrom":makeQuery(id+"F16.opExtrude","SWEPT_EDGE",EDGE,{"disambiguationData":[OSD([sQuery(id+"F0.wireOp",EDGE,"E0.top"),sQuery(id+"F15.wireOp",EDGE,"E15.20.0.0")])]})});
            var Q80;
            Q80=makeQuery(id+"F16.boolean.opBoolean","COPY",EDGE,{"derivedFrom":makeQuery(id+"F16.opExtrude","SWEPT_EDGE",EDGE,{"disambiguationData":[OSD([sQuery(id+"F0.wireOp",EDGE,"E0.top"),sQuery(id+"F15.wireOp",EDGE,"E15.18.0.2")])]})});
            var Q81;
            Q81=makeQuery(id+"F16.boolean.opBoolean","COPY",EDGE,{"derivedFrom":makeQuery(id+"F16.opExtrude","SWEPT_EDGE",EDGE,{"disambiguationData":[OSD([sQuery(id+"F0.wireOp",EDGE,"E0.top"),sQuery(id+"F15.wireOp",EDGE,"E15.18.0.0")])]})});
            var Q82;
            Q82=makeQuery(id+"F16.boolean.opBoolean","COPY",EDGE,{"derivedFrom":makeQuery(id+"F16.opExtrude","SWEPT_EDGE",EDGE,{"disambiguationData":[OSD([sQuery(id+"F0.wireOp",EDGE,"E0.top"),sQuery(id+"F15.wireOp",EDGE,"E15.16.0.2")])]})});
            var Q83;
            Q83=makeQuery(id+"F16.boolean.opBoolean","COPY",EDGE,{"derivedFrom":makeQuery(id+"F16.opExtrude","SWEPT_EDGE",EDGE,{"disambiguationData":[OSD([sQuery(id+"F0.wireOp",EDGE,"E0.top"),sQuery(id+"F15.wireOp",EDGE,"E15.14.0.2")])]})});
            var Q84;
            Q84=makeQuery(id+"F16.boolean.opBoolean","COPY",EDGE,{"derivedFrom":makeQuery(id+"F16.opExtrude","SWEPT_EDGE",EDGE,{"disambiguationData":[OSD([sQuery(id+"F0.wireOp",EDGE,"E0.top"),sQuery(id+"F15.wireOp",EDGE,"E15.16.0.0")])]})});
            var Q85;
            Q85=makeQuery(id+"F16.boolean.opBoolean","COPY",EDGE,{"derivedFrom":makeQuery(id+"F16.opExtrude","SWEPT_EDGE",EDGE,{"disambiguationData":[OSD([sQuery(id+"F0.wireOp",EDGE,"E0.top"),sQuery(id+"F15.wireOp",EDGE,"E15.14.0.0")])]})});
            var Q86;
            Q86=makeQuery(id+"F16.boolean.opBoolean","COPY",EDGE,{"derivedFrom":makeQuery(id+"F16.opExtrude","SWEPT_EDGE",EDGE,{"disambiguationData":[OSD([sQuery(id+"F0.wireOp",EDGE,"E0.top"),sQuery(id+"F15.wireOp",EDGE,"E15.12.0.2")])]})});
            var Q87;
            Q87=makeQuery(id+"F16.boolean.opBoolean","COPY",EDGE,{"derivedFrom":makeQuery(id+"F16.opExtrude","SWEPT_EDGE",EDGE,{"disambiguationData":[OSD([sQuery(id+"F0.wireOp",EDGE,"E0.top"),sQuery(id+"F15.wireOp",EDGE,"E15.12.0.0")])]})});
            var Q88;
            Q88=makeQuery(id+"F16.boolean.opBoolean","COPY",EDGE,{"derivedFrom":makeQuery(id+"F16.opExtrude","SWEPT_EDGE",EDGE,{"disambiguationData":[OSD([sQuery(id+"F0.wireOp",EDGE,"E0.top"),sQuery(id+"F15.wireOp",EDGE,"E15.10.0.2")])]})});
            var Q89;
            Q89=makeQuery(id+"F16.boolean.opBoolean","COPY",EDGE,{"derivedFrom":makeQuery(id+"F16.opExtrude","SWEPT_EDGE",EDGE,{"disambiguationData":[OSD([sQuery(id+"F0.wireOp",EDGE,"E0.top"),sQuery(id+"F15.wireOp",EDGE,"E15.10.0.0")])]})});
            var Q90;
            Q90=makeQuery(id+"F16.boolean.opBoolean","COPY",EDGE,{"derivedFrom":makeQuery(id+"F16.opExtrude","SWEPT_EDGE",EDGE,{"disambiguationData":[OSD([sQuery(id+"F0.wireOp",EDGE,"E0.top"),sQuery(id+"F15.wireOp",EDGE,"E15.8.0.2")])]})});
            var Q91;
            Q91=makeQuery(id+"F16.boolean.opBoolean","COPY",EDGE,{"derivedFrom":makeQuery(id+"F16.opExtrude","SWEPT_EDGE",EDGE,{"disambiguationData":[OSD([sQuery(id+"F0.wireOp",EDGE,"E0.top"),sQuery(id+"F15.wireOp",EDGE,"E15.6.0.2")])]})});
            var Q92;
            Q92=makeQuery(id+"F16.boolean.opBoolean","COPY",EDGE,{"derivedFrom":makeQuery(id+"F16.opExtrude","SWEPT_EDGE",EDGE,{"disambiguationData":[OSD([sQuery(id+"F0.wireOp",EDGE,"E0.top"),sQuery(id+"F15.wireOp",EDGE,"E15.6.0.0")])]})});
            var Q93;
            Q93=makeQuery(id+"F16.boolean.opBoolean","COPY",EDGE,{"derivedFrom":makeQuery(id+"F16.opExtrude","SWEPT_EDGE",EDGE,{"disambiguationData":[OSD([sQuery(id+"F0.wireOp",EDGE,"E0.top"),sQuery(id+"F15.wireOp",EDGE,"E15.4.0.2")])]})});
            var Q94;
            Q94=makeQuery(id+"F16.boolean.opBoolean","COPY",EDGE,{"derivedFrom":makeQuery(id+"F16.opExtrude","SWEPT_EDGE",EDGE,{"disambiguationData":[OSD([sQuery(id+"F0.wireOp",EDGE,"E0.top"),sQuery(id+"F15.wireOp",EDGE,"E15.4.0.0")])]})});
            var Q95;
            Q95=makeQuery(id+"F16.boolean.opBoolean","COPY",EDGE,{"derivedFrom":makeQuery(id+"F16.opExtrude","SWEPT_EDGE",EDGE,{"disambiguationData":[OSD([sQuery(id+"F0.wireOp",EDGE,"E0.top"),sQuery(id+"F15.wireOp",EDGE,"E15.2.0.2")])]})});
            var Q96;
            Q96=makeQuery(id+"F16.boolean.opBoolean","COPY",EDGE,{"derivedFrom":makeQuery(id+"F16.opExtrude","SWEPT_EDGE",EDGE,{"disambiguationData":[OSD([sQuery(id+"F0.wireOp",EDGE,"E0.top"),sQuery(id+"F15.wireOp",EDGE,"E15.2.0.0")])]})});
            var Q97;
            Q97=makeQuery(id+"F14.boolean.opBoolean","COPY",EDGE,{"derivedFrom":makeQuery(id+"F14.opExtrude","SWEPT_EDGE",EDGE,{"disambiguationData":[OSD([sQuery(id+"F13.wireOp",EDGE,"E10.98.0.1"),sQuery(id+"F13.wireOp",EDGE,"E10.99.0.0"),sQuery(id+"F13.wireOp",EDGE,"E10.99.0.1")])]})});
            var Q98;
            Q98=makeQuery(id+"F14.boolean.opBoolean","COPY",EDGE,{"derivedFrom":makeQuery(id+"F14.opExtrude","SWEPT_EDGE",EDGE,{"disambiguationData":[OSD([sQuery(id+"F13.wireOp",EDGE,"E10.96.0.1"),sQuery(id+"F13.wireOp",EDGE,"E10.97.0.0"),sQuery(id+"F13.wireOp",EDGE,"E10.97.0.1")])]})});
            var Q99;
            Q99=makeQuery(id+"F14.boolean.opBoolean","COPY",EDGE,{"derivedFrom":makeQuery(id+"F14.opExtrude","SWEPT_EDGE",EDGE,{"disambiguationData":[OSD([sQuery(id+"F13.wireOp",EDGE,"E10.97.0.2"),sQuery(id+"F13.wireOp",EDGE,"E10.98.0.1")])]})});
            var Q100;
            Q100=makeQuery(id+"F14.boolean.opBoolean","COPY",EDGE,{"derivedFrom":makeQuery(id+"F14.opExtrude","SWEPT_EDGE",EDGE,{"disambiguationData":[OSD([sQuery(id+"F13.wireOp",EDGE,"E10.95.0.2"),sQuery(id+"F13.wireOp",EDGE,"E10.96.0.1")])]})});
            var Q101;
            Q101=makeQuery(id+"F14.boolean.opBoolean","COPY",EDGE,{"derivedFrom":makeQuery(id+"F14.opExtrude","SWEPT_EDGE",EDGE,{"disambiguationData":[OSD([sQuery(id+"F13.wireOp",EDGE,"E10.94.0.1"),sQuery(id+"F13.wireOp",EDGE,"E10.95.0.0"),sQuery(id+"F13.wireOp",EDGE,"E10.95.0.1")])]})});
            var Q102;
            Q102=makeQuery(id+"F14.boolean.opBoolean","COPY",EDGE,{"derivedFrom":makeQuery(id+"F14.opExtrude","SWEPT_EDGE",EDGE,{"disambiguationData":[OSD([sQuery(id+"F13.wireOp",EDGE,"E10.92.0.1"),sQuery(id+"F13.wireOp",EDGE,"E10.93.0.0"),sQuery(id+"F13.wireOp",EDGE,"E10.93.0.1")])]})});
            var Q103;
            Q103=makeQuery(id+"F14.boolean.opBoolean","COPY",EDGE,{"derivedFrom":makeQuery(id+"F14.opExtrude","SWEPT_EDGE",EDGE,{"disambiguationData":[OSD([sQuery(id+"F13.wireOp",EDGE,"E10.93.0.2"),sQuery(id+"F13.wireOp",EDGE,"E10.94.0.1")])]})});
            var Q104;
            Q104=makeQuery(id+"F14.boolean.opBoolean","COPY",EDGE,{"derivedFrom":makeQuery(id+"F14.opExtrude","SWEPT_EDGE",EDGE,{"disambiguationData":[OSD([sQuery(id+"F13.wireOp",EDGE,"E10.91.0.2"),sQuery(id+"F13.wireOp",EDGE,"E10.92.0.1")])]})});
            var Q105;
            Q105=makeQuery(id+"F14.boolean.opBoolean","COPY",EDGE,{"derivedFrom":makeQuery(id+"F14.opExtrude","SWEPT_EDGE",EDGE,{"disambiguationData":[OSD([sQuery(id+"F13.wireOp",EDGE,"E10.90.0.1"),sQuery(id+"F13.wireOp",EDGE,"E10.91.0.0"),sQuery(id+"F13.wireOp",EDGE,"E10.91.0.1")])]})});
            var Q106;
            Q106=makeQuery(id+"F14.boolean.opBoolean","COPY",EDGE,{"derivedFrom":makeQuery(id+"F14.opExtrude","SWEPT_EDGE",EDGE,{"disambiguationData":[OSD([sQuery(id+"F13.wireOp",EDGE,"E10.89.0.2"),sQuery(id+"F13.wireOp",EDGE,"E10.90.0.1")])]})});
            var Q107;
            Q107=makeQuery(id+"F14.boolean.opBoolean","COPY",EDGE,{"derivedFrom":makeQuery(id+"F14.opExtrude","SWEPT_EDGE",EDGE,{"disambiguationData":[OSD([sQuery(id+"F13.wireOp",EDGE,"E10.88.0.1"),sQuery(id+"F13.wireOp",EDGE,"E10.89.0.0"),sQuery(id+"F13.wireOp",EDGE,"E10.89.0.1")])]})});
            var Q108;
            Q108=makeQuery(id+"F14.boolean.opBoolean","COPY",EDGE,{"derivedFrom":makeQuery(id+"F14.opExtrude","SWEPT_EDGE",EDGE,{"disambiguationData":[OSD([sQuery(id+"F13.wireOp",EDGE,"E10.87.0.2"),sQuery(id+"F13.wireOp",EDGE,"E10.88.0.1")])]})});
            var Q109;
            Q109=makeQuery(id+"F14.boolean.opBoolean","COPY",EDGE,{"derivedFrom":makeQuery(id+"F14.opExtrude","SWEPT_EDGE",EDGE,{"disambiguationData":[OSD([sQuery(id+"F13.wireOp",EDGE,"E10.86.0.1"),sQuery(id+"F13.wireOp",EDGE,"E10.87.0.0"),sQuery(id+"F13.wireOp",EDGE,"E10.87.0.1")])]})});
            var Q110;
            Q110=makeQuery(id+"F14.boolean.opBoolean","COPY",EDGE,{"derivedFrom":makeQuery(id+"F14.opExtrude","SWEPT_EDGE",EDGE,{"disambiguationData":[OSD([sQuery(id+"F13.wireOp",EDGE,"E10.85.0.2"),sQuery(id+"F13.wireOp",EDGE,"E10.86.0.1")])]})});
            var Q111;
            Q111=makeQuery(id+"F14.boolean.opBoolean","COPY",EDGE,{"derivedFrom":makeQuery(id+"F14.opExtrude","SWEPT_EDGE",EDGE,{"disambiguationData":[OSD([sQuery(id+"F13.wireOp",EDGE,"E10.84.0.1"),sQuery(id+"F13.wireOp",EDGE,"E10.85.0.0"),sQuery(id+"F13.wireOp",EDGE,"E10.85.0.1")])]})});
            var Q112;
            Q112=makeQuery(id+"F14.boolean.opBoolean","COPY",EDGE,{"derivedFrom":makeQuery(id+"F14.opExtrude","SWEPT_EDGE",EDGE,{"disambiguationData":[OSD([sQuery(id+"F13.wireOp",EDGE,"E10.83.0.2"),sQuery(id+"F13.wireOp",EDGE,"E10.84.0.1")])]})});
            var Q113;
            Q113=makeQuery(id+"F14.boolean.opBoolean","COPY",EDGE,{"derivedFrom":makeQuery(id+"F14.opExtrude","SWEPT_EDGE",EDGE,{"disambiguationData":[OSD([sQuery(id+"F13.wireOp",EDGE,"E10.82.0.1"),sQuery(id+"F13.wireOp",EDGE,"E10.83.0.0"),sQuery(id+"F13.wireOp",EDGE,"E10.83.0.1")])]})});
            var Q114;
            Q114=makeQuery(id+"F14.boolean.opBoolean","COPY",EDGE,{"derivedFrom":makeQuery(id+"F14.opExtrude","SWEPT_EDGE",EDGE,{"disambiguationData":[OSD([sQuery(id+"F13.wireOp",EDGE,"E10.81.0.2"),sQuery(id+"F13.wireOp",EDGE,"E10.82.0.1")])]})});
            var Q115;
            Q115=makeQuery(id+"F14.boolean.opBoolean","COPY",EDGE,{"derivedFrom":makeQuery(id+"F14.opExtrude","SWEPT_EDGE",EDGE,{"disambiguationData":[OSD([sQuery(id+"F13.wireOp",EDGE,"E10.80.0.1"),sQuery(id+"F13.wireOp",EDGE,"E10.81.0.0"),sQuery(id+"F13.wireOp",EDGE,"E10.81.0.1")])]})});
            var Q116;
            Q116=makeQuery(id+"F14.boolean.opBoolean","COPY",EDGE,{"derivedFrom":makeQuery(id+"F14.opExtrude","SWEPT_EDGE",EDGE,{"disambiguationData":[OSD([sQuery(id+"F13.wireOp",EDGE,"E10.79.0.2"),sQuery(id+"F13.wireOp",EDGE,"E10.80.0.1")])]})});
            var Q117;
            Q117=makeQuery(id+"F14.boolean.opBoolean","COPY",EDGE,{"derivedFrom":makeQuery(id+"F14.opExtrude","SWEPT_EDGE",EDGE,{"disambiguationData":[OSD([sQuery(id+"F13.wireOp",EDGE,"E10.78.0.1"),sQuery(id+"F13.wireOp",EDGE,"E10.79.0.0"),sQuery(id+"F13.wireOp",EDGE,"E10.79.0.1")])]})});
            var Q118;
            Q118=makeQuery(id+"F14.boolean.opBoolean","COPY",EDGE,{"derivedFrom":makeQuery(id+"F14.opExtrude","SWEPT_EDGE",EDGE,{"disambiguationData":[OSD([sQuery(id+"F13.wireOp",EDGE,"E10.77.0.2"),sQuery(id+"F13.wireOp",EDGE,"E10.78.0.1")])]})});
            var Q119;
            Q119=makeQuery(id+"F14.boolean.opBoolean","COPY",EDGE,{"derivedFrom":makeQuery(id+"F14.opExtrude","SWEPT_EDGE",EDGE,{"disambiguationData":[OSD([sQuery(id+"F13.wireOp",EDGE,"E10.76.0.1"),sQuery(id+"F13.wireOp",EDGE,"E10.77.0.0"),sQuery(id+"F13.wireOp",EDGE,"E10.77.0.1")])]})});
            var Q120;
            Q120=makeQuery(id+"F14.boolean.opBoolean","COPY",EDGE,{"derivedFrom":makeQuery(id+"F14.opExtrude","SWEPT_EDGE",EDGE,{"disambiguationData":[OSD([sQuery(id+"F13.wireOp",EDGE,"E10.75.0.2"),sQuery(id+"F13.wireOp",EDGE,"E10.76.0.1")])]})});
            var Q121;
            Q121=makeQuery(id+"F14.boolean.opBoolean","COPY",EDGE,{"derivedFrom":makeQuery(id+"F14.opExtrude","SWEPT_EDGE",EDGE,{"disambiguationData":[OSD([sQuery(id+"F13.wireOp",EDGE,"E10.74.0.1"),sQuery(id+"F13.wireOp",EDGE,"E10.75.0.0"),sQuery(id+"F13.wireOp",EDGE,"E10.75.0.1")])]})});
            var Q122;
            Q122=makeQuery(id+"F14.boolean.opBoolean","COPY",EDGE,{"derivedFrom":makeQuery(id+"F14.opExtrude","SWEPT_EDGE",EDGE,{"disambiguationData":[OSD([sQuery(id+"F13.wireOp",EDGE,"E10.72.0.1"),sQuery(id+"F13.wireOp",EDGE,"E10.73.0.0"),sQuery(id+"F13.wireOp",EDGE,"E10.73.0.1")])]})});
            var Q123;
            Q123=makeQuery(id+"F14.boolean.opBoolean","COPY",EDGE,{"derivedFrom":makeQuery(id+"F14.opExtrude","SWEPT_EDGE",EDGE,{"disambiguationData":[OSD([sQuery(id+"F13.wireOp",EDGE,"E10.73.0.2"),sQuery(id+"F13.wireOp",EDGE,"E10.74.0.1")])]})});
            var Q124;
            Q124=makeQuery(id+"F14.boolean.opBoolean","COPY",EDGE,{"derivedFrom":makeQuery(id+"F14.opExtrude","SWEPT_EDGE",EDGE,{"disambiguationData":[OSD([sQuery(id+"F13.wireOp",EDGE,"E10.70.0.1"),sQuery(id+"F13.wireOp",EDGE,"E10.71.0.0"),sQuery(id+"F13.wireOp",EDGE,"E10.71.0.1")])]})});
            var Q125;
            Q125=makeQuery(id+"F14.boolean.opBoolean","COPY",EDGE,{"derivedFrom":makeQuery(id+"F14.opExtrude","SWEPT_EDGE",EDGE,{"disambiguationData":[OSD([sQuery(id+"F13.wireOp",EDGE,"E10.71.0.2"),sQuery(id+"F13.wireOp",EDGE,"E10.72.0.1")])]})});
            var Q126;
            Q126=makeQuery(id+"F14.boolean.opBoolean","COPY",EDGE,{"derivedFrom":makeQuery(id+"F14.opExtrude","SWEPT_EDGE",EDGE,{"disambiguationData":[OSD([sQuery(id+"F13.wireOp",EDGE,"E10.69.0.2"),sQuery(id+"F13.wireOp",EDGE,"E10.70.0.1")])]})});
            var Q127;
            Q127=makeQuery(id+"F14.boolean.opBoolean","COPY",EDGE,{"derivedFrom":makeQuery(id+"F14.opExtrude","SWEPT_EDGE",EDGE,{"disambiguationData":[OSD([sQuery(id+"F13.wireOp",EDGE,"E10.68.0.1"),sQuery(id+"F13.wireOp",EDGE,"E10.69.0.0"),sQuery(id+"F13.wireOp",EDGE,"E10.69.0.1")])]})});
            var Q128;
            Q128=makeQuery(id+"F14.boolean.opBoolean","COPY",EDGE,{"derivedFrom":makeQuery(id+"F14.opExtrude","SWEPT_EDGE",EDGE,{"disambiguationData":[OSD([sQuery(id+"F13.wireOp",EDGE,"E10.67.0.2"),sQuery(id+"F13.wireOp",EDGE,"E10.68.0.1")])]})});
            var Q129;
            Q129=makeQuery(id+"F14.boolean.opBoolean","COPY",EDGE,{"derivedFrom":makeQuery(id+"F14.opExtrude","SWEPT_EDGE",EDGE,{"disambiguationData":[OSD([sQuery(id+"F13.wireOp",EDGE,"E10.65.0.2"),sQuery(id+"F13.wireOp",EDGE,"E10.66.0.1")])]})});
            var Q130;
            Q130=makeQuery(id+"F14.boolean.opBoolean","COPY",EDGE,{"derivedFrom":makeQuery(id+"F14.opExtrude","SWEPT_EDGE",EDGE,{"disambiguationData":[OSD([sQuery(id+"F13.wireOp",EDGE,"E10.64.0.1"),sQuery(id+"F13.wireOp",EDGE,"E10.65.0.0"),sQuery(id+"F13.wireOp",EDGE,"E10.65.0.1")])]})});
            var Q131;
            Q131=makeQuery(id+"F14.boolean.opBoolean","COPY",EDGE,{"derivedFrom":makeQuery(id+"F14.opExtrude","SWEPT_EDGE",EDGE,{"disambiguationData":[OSD([sQuery(id+"F13.wireOp",EDGE,"E10.63.0.2"),sQuery(id+"F13.wireOp",EDGE,"E10.64.0.1")])]})});
            var Q132;
            Q132=makeQuery(id+"F14.boolean.opBoolean","COPY",EDGE,{"derivedFrom":makeQuery(id+"F14.opExtrude","SWEPT_EDGE",EDGE,{"disambiguationData":[OSD([sQuery(id+"F13.wireOp",EDGE,"E10.62.0.1"),sQuery(id+"F13.wireOp",EDGE,"E10.63.0.0"),sQuery(id+"F13.wireOp",EDGE,"E10.63.0.1")])]})});
            var Q133;
            Q133=makeQuery(id+"F14.boolean.opBoolean","COPY",EDGE,{"derivedFrom":makeQuery(id+"F14.opExtrude","SWEPT_EDGE",EDGE,{"disambiguationData":[OSD([sQuery(id+"F13.wireOp",EDGE,"E10.61.0.2"),sQuery(id+"F13.wireOp",EDGE,"E10.62.0.1")])]})});
            var Q134;
            Q134=makeQuery(id+"F14.boolean.opBoolean","COPY",EDGE,{"derivedFrom":makeQuery(id+"F14.opExtrude","SWEPT_EDGE",EDGE,{"disambiguationData":[OSD([sQuery(id+"F13.wireOp",EDGE,"E10.59.0.2"),sQuery(id+"F13.wireOp",EDGE,"E10.60.0.1")])]})});
            var Q135;
            Q135=makeQuery(id+"F14.boolean.opBoolean","COPY",EDGE,{"derivedFrom":makeQuery(id+"F14.opExtrude","SWEPT_EDGE",EDGE,{"disambiguationData":[OSD([sQuery(id+"F13.wireOp",EDGE,"E10.58.0.1"),sQuery(id+"F13.wireOp",EDGE,"E10.59.0.0"),sQuery(id+"F13.wireOp",EDGE,"E10.59.0.1")])]})});
            var Q136;
            Q136=makeQuery(id+"F14.boolean.opBoolean","COPY",EDGE,{"derivedFrom":makeQuery(id+"F14.opExtrude","SWEPT_EDGE",EDGE,{"disambiguationData":[OSD([sQuery(id+"F13.wireOp",EDGE,"E10.57.0.2"),sQuery(id+"F13.wireOp",EDGE,"E10.58.0.1")])]})});
            var Q137;
            Q137=makeQuery(id+"F14.boolean.opBoolean","COPY",EDGE,{"derivedFrom":makeQuery(id+"F14.opExtrude","SWEPT_EDGE",EDGE,{"disambiguationData":[OSD([sQuery(id+"F13.wireOp",EDGE,"E10.56.0.1"),sQuery(id+"F13.wireOp",EDGE,"E10.57.0.0"),sQuery(id+"F13.wireOp",EDGE,"E10.57.0.1")])]})});
            var Q138;
            Q138=makeQuery(id+"F16.boolean.opBoolean","COPY",EDGE,{"derivedFrom":makeQuery(id+"F16.opExtrude","SWEPT_EDGE",EDGE,{"disambiguationData":[OSD([sQuery(id+"F0.wireOp",EDGE,"E0.top"),sQuery(id+"F15.wireOp",EDGE,"E15.8.0.0")])]})});
            var Q139;
            Q139=makeQuery(id+"F14.boolean.opBoolean","COPY",EDGE,{"derivedFrom":makeQuery(id+"F14.opExtrude","SWEPT_EDGE",EDGE,{"disambiguationData":[OSD([sQuery(id+"F13.wireOp",EDGE,"E10.60.0.1"),sQuery(id+"F13.wireOp",EDGE,"E10.61.0.0"),sQuery(id+"F13.wireOp",EDGE,"E10.61.0.1")])]})});
            var Q140;
            Q140=makeQuery(id+"F14.boolean.opBoolean","COPY",EDGE,{"derivedFrom":makeQuery(id+"F14.opExtrude","SWEPT_EDGE",EDGE,{"disambiguationData":[OSD([sQuery(id+"F13.wireOp",EDGE,"E10.55.0.2"),sQuery(id+"F13.wireOp",EDGE,"E10.56.0.1")])]})});
            var Q141;
            Q141=makeQuery(id+"F14.boolean.opBoolean","COPY",EDGE,{"derivedFrom":makeQuery(id+"F14.opExtrude","SWEPT_EDGE",EDGE,{"disambiguationData":[OSD([sQuery(id+"F13.wireOp",EDGE,"E10.54.0.1"),sQuery(id+"F13.wireOp",EDGE,"E10.55.0.0"),sQuery(id+"F13.wireOp",EDGE,"E10.55.0.1")])]})});
            var Q142;
            Q142=makeQuery(id+"F14.boolean.opBoolean","COPY",EDGE,{"derivedFrom":makeQuery(id+"F14.opExtrude","SWEPT_EDGE",EDGE,{"disambiguationData":[OSD([sQuery(id+"F13.wireOp",EDGE,"E10.53.0.2"),sQuery(id+"F13.wireOp",EDGE,"E10.54.0.1")])]})});
            var Q143;
            Q143=makeQuery(id+"F14.boolean.opBoolean","COPY",EDGE,{"derivedFrom":makeQuery(id+"F14.opExtrude","SWEPT_EDGE",EDGE,{"disambiguationData":[OSD([sQuery(id+"F13.wireOp",EDGE,"E10.52.0.1"),sQuery(id+"F13.wireOp",EDGE,"E10.53.0.0"),sQuery(id+"F13.wireOp",EDGE,"E10.53.0.1")])]})});
            var Q144;
            Q144=makeQuery(id+"F14.boolean.opBoolean","COPY",EDGE,{"derivedFrom":makeQuery(id+"F14.opExtrude","SWEPT_EDGE",EDGE,{"disambiguationData":[OSD([sQuery(id+"F13.wireOp",EDGE,"E10.51.0.2"),sQuery(id+"F13.wireOp",EDGE,"E10.52.0.1")])]})});
            var Q145;
            Q145=makeQuery(id+"F14.boolean.opBoolean","COPY",EDGE,{"derivedFrom":makeQuery(id+"F14.opExtrude","SWEPT_EDGE",EDGE,{"disambiguationData":[OSD([sQuery(id+"F13.wireOp",EDGE,"E10.50.0.1"),sQuery(id+"F13.wireOp",EDGE,"E10.51.0.0"),sQuery(id+"F13.wireOp",EDGE,"E10.51.0.1")])]})});
            var Q146;
            Q146=makeQuery(id+"F14.boolean.opBoolean","COPY",EDGE,{"derivedFrom":makeQuery(id+"F14.opExtrude","SWEPT_EDGE",EDGE,{"disambiguationData":[OSD([sQuery(id+"F13.wireOp",EDGE,"E10.48.0.1"),sQuery(id+"F13.wireOp",EDGE,"E10.49.0.0"),sQuery(id+"F13.wireOp",EDGE,"E10.49.0.1")])]})});
            var Q147;
            Q147=makeQuery(id+"F14.boolean.opBoolean","COPY",EDGE,{"derivedFrom":makeQuery(id+"F14.opExtrude","SWEPT_EDGE",EDGE,{"disambiguationData":[OSD([sQuery(id+"F13.wireOp",EDGE,"E10.49.0.2"),sQuery(id+"F13.wireOp",EDGE,"E10.50.0.1")])]})});
            var Q148;
            Q148=makeQuery(id+"F14.boolean.opBoolean","COPY",EDGE,{"derivedFrom":makeQuery(id+"F14.opExtrude","SWEPT_EDGE",EDGE,{"disambiguationData":[OSD([sQuery(id+"F13.wireOp",EDGE,"E10.46.0.1"),sQuery(id+"F13.wireOp",EDGE,"E10.47.0.0"),sQuery(id+"F13.wireOp",EDGE,"E10.47.0.1")])]})});
            var Q149;
            Q149=makeQuery(id+"F14.boolean.opBoolean","COPY",EDGE,{"derivedFrom":makeQuery(id+"F14.opExtrude","SWEPT_EDGE",EDGE,{"disambiguationData":[OSD([sQuery(id+"F13.wireOp",EDGE,"E10.47.0.2"),sQuery(id+"F13.wireOp",EDGE,"E10.48.0.1")])]})});
            var Q150;
            {var subQ0=sQuery(id+"F13.wireOp",EDGE,"E10.49.0.0");Q150=makeQuery(id+"F19.opFillet","BLEND_EDGE",EDGE,{"blendedFrom":[makeQuery(id+"F14.boolean.opBoolean","COPY",EDGE,{"derivedFrom":makeQuery(id+"F14.opExtrude","SWEPT_EDGE",EDGE,{"disambiguationData":[OSD([sQuery(id+"F13.wireOp",EDGE,"E10.48.0.3"),subQ0,sQuery(id+"F13.wireOp",EDGE,"E10.49.0.3")])]})}),makeQuery(id+"F14.boolean.opBoolean","COPY",FACE,{"derivedFrom":makeQuery(id+"F14.opExtrude","SWEPT_FACE",FACE,{"disambiguationData":[OSD([subQ0])]})})],"blendedInto":[makeQuery(id+"F14.boolean.opBoolean","COPY",FACE,{"derivedFrom":makeQuery(id+"F14.opExtrude","SWEPT_FACE",FACE,{"disambiguationData":[OSD([subQ0])]})})]});}
            var Q151;
            Q151=makeQuery(id+"F14.boolean.opBoolean","COPY",EDGE,{"derivedFrom":makeQuery(id+"F14.opExtrude","SWEPT_EDGE",EDGE,{"disambiguationData":[OSD([sQuery(id+"F13.wireOp",EDGE,"E10.44.0.1"),sQuery(id+"F13.wireOp",EDGE,"E10.45.0.0"),sQuery(id+"F13.wireOp",EDGE,"E10.45.0.1")])]})});
            var Q152;
            Q152=makeQuery(id+"F14.boolean.opBoolean","COPY",EDGE,{"derivedFrom":makeQuery(id+"F14.opExtrude","SWEPT_EDGE",EDGE,{"disambiguationData":[OSD([sQuery(id+"F13.wireOp",EDGE,"E10.45.0.2"),sQuery(id+"F13.wireOp",EDGE,"E10.46.0.1")])]})});
            var Q153;
            Q153=makeQuery(id+"F14.boolean.opBoolean","COPY",EDGE,{"derivedFrom":makeQuery(id+"F14.opExtrude","SWEPT_EDGE",EDGE,{"disambiguationData":[OSD([sQuery(id+"F13.wireOp",EDGE,"E10.43.0.2"),sQuery(id+"F13.wireOp",EDGE,"E10.44.0.1")])]})});
            var Q154;
            Q154=makeQuery(id+"F14.boolean.opBoolean","COPY",EDGE,{"derivedFrom":makeQuery(id+"F14.opExtrude","SWEPT_EDGE",EDGE,{"disambiguationData":[OSD([sQuery(id+"F13.wireOp",EDGE,"E10.42.0.1"),sQuery(id+"F13.wireOp",EDGE,"E10.43.0.0"),sQuery(id+"F13.wireOp",EDGE,"E10.43.0.1")])]})});
            var Q155;
            Q155=makeQuery(id+"F14.boolean.opBoolean","COPY",EDGE,{"derivedFrom":makeQuery(id+"F14.opExtrude","SWEPT_EDGE",EDGE,{"disambiguationData":[OSD([sQuery(id+"F13.wireOp",EDGE,"E10.41.0.2"),sQuery(id+"F13.wireOp",EDGE,"E10.42.0.1")])]})});
            var Q156;
            Q156=makeQuery(id+"F14.boolean.opBoolean","COPY",EDGE,{"derivedFrom":makeQuery(id+"F14.opExtrude","SWEPT_EDGE",EDGE,{"disambiguationData":[OSD([sQuery(id+"F13.wireOp",EDGE,"E10.40.0.1"),sQuery(id+"F13.wireOp",EDGE,"E10.41.0.0"),sQuery(id+"F13.wireOp",EDGE,"E10.41.0.1")])]})});
            var Q157;
            Q157=makeQuery(id+"F14.boolean.opBoolean","COPY",EDGE,{"derivedFrom":makeQuery(id+"F14.opExtrude","SWEPT_EDGE",EDGE,{"disambiguationData":[OSD([sQuery(id+"F13.wireOp",EDGE,"E10.39.0.2"),sQuery(id+"F13.wireOp",EDGE,"E10.40.0.1")])]})});
            var Q158;
            Q158=makeQuery(id+"F14.boolean.opBoolean","COPY",EDGE,{"derivedFrom":makeQuery(id+"F14.opExtrude","SWEPT_EDGE",EDGE,{"disambiguationData":[OSD([sQuery(id+"F13.wireOp",EDGE,"E10.38.0.1"),sQuery(id+"F13.wireOp",EDGE,"E10.39.0.0"),sQuery(id+"F13.wireOp",EDGE,"E10.39.0.1")])]})});
            var Q159;
            Q159=makeQuery(id+"F14.boolean.opBoolean","COPY",EDGE,{"derivedFrom":makeQuery(id+"F14.opExtrude","SWEPT_EDGE",EDGE,{"disambiguationData":[OSD([sQuery(id+"F13.wireOp",EDGE,"E10.37.0.2"),sQuery(id+"F13.wireOp",EDGE,"E10.38.0.1")])]})});
            var Q160;
            Q160=makeQuery(id+"F14.boolean.opBoolean","COPY",EDGE,{"derivedFrom":makeQuery(id+"F14.opExtrude","SWEPT_EDGE",EDGE,{"disambiguationData":[OSD([sQuery(id+"F13.wireOp",EDGE,"E10.36.0.1"),sQuery(id+"F13.wireOp",EDGE,"E10.37.0.0"),sQuery(id+"F13.wireOp",EDGE,"E10.37.0.1")])]})});
            var Q161;
            Q161=makeQuery(id+"F14.boolean.opBoolean","COPY",EDGE,{"derivedFrom":makeQuery(id+"F14.opExtrude","SWEPT_EDGE",EDGE,{"disambiguationData":[OSD([sQuery(id+"F13.wireOp",EDGE,"E10.35.0.2"),sQuery(id+"F13.wireOp",EDGE,"E10.36.0.1")])]})});
            var Q162;
            Q162=makeQuery(id+"F14.boolean.opBoolean","COPY",EDGE,{"derivedFrom":makeQuery(id+"F14.opExtrude","SWEPT_EDGE",EDGE,{"disambiguationData":[OSD([sQuery(id+"F13.wireOp",EDGE,"E10.34.0.1"),sQuery(id+"F13.wireOp",EDGE,"E10.35.0.0"),sQuery(id+"F13.wireOp",EDGE,"E10.35.0.1")])]})});
            var Q163;
            Q163=makeQuery(id+"F14.boolean.opBoolean","COPY",EDGE,{"derivedFrom":makeQuery(id+"F14.opExtrude","SWEPT_EDGE",EDGE,{"disambiguationData":[OSD([sQuery(id+"F13.wireOp",EDGE,"E10.33.0.2"),sQuery(id+"F13.wireOp",EDGE,"E10.34.0.1")])]})});
            var Q164;
            Q164=makeQuery(id+"F14.boolean.opBoolean","COPY",EDGE,{"derivedFrom":makeQuery(id+"F14.opExtrude","SWEPT_EDGE",EDGE,{"disambiguationData":[OSD([sQuery(id+"F13.wireOp",EDGE,"E10.32.0.1"),sQuery(id+"F13.wireOp",EDGE,"E10.33.0.0"),sQuery(id+"F13.wireOp",EDGE,"E10.33.0.1")])]})});
            var Q165;
            Q165=makeQuery(id+"F14.boolean.opBoolean","COPY",EDGE,{"derivedFrom":makeQuery(id+"F14.opExtrude","SWEPT_EDGE",EDGE,{"disambiguationData":[OSD([sQuery(id+"F13.wireOp",EDGE,"E10.31.0.2"),sQuery(id+"F13.wireOp",EDGE,"E10.32.0.1")])]})});
            var Q166;
            Q166=makeQuery(id+"F14.boolean.opBoolean","COPY",EDGE,{"derivedFrom":makeQuery(id+"F14.opExtrude","SWEPT_EDGE",EDGE,{"disambiguationData":[OSD([sQuery(id+"F13.wireOp",EDGE,"E10.30.0.1"),sQuery(id+"F13.wireOp",EDGE,"E10.31.0.0"),sQuery(id+"F13.wireOp",EDGE,"E10.31.0.1")])]})});
            var Q167;
            Q167=makeQuery(id+"F1.opExtrude","CAP_EDGE",EDGE,{"disambiguationData":[OSD([sQuery(id+"F0.wireOp",EDGE,"E0.left")])],"isStart":false});
            var Q168;
            Q168=makeQuery(id+"F14.boolean.opBoolean","COPY",EDGE,{"derivedFrom":makeQuery(id+"F14.opExtrude","SWEPT_EDGE",EDGE,{"disambiguationData":[OSD([sQuery(id+"F0.wireOp",EDGE,"E0.top"),sQuery(id+"F13.wireOp",EDGE,"E9.bottom"),sQuery(id+"F13.wireOp",EDGE,"E9.left")])]})});
            var Q169;
            Q169=makeQuery(id+"F14.boolean.opBoolean","COPY",EDGE,{"derivedFrom":makeQuery(id+"F14.opExtrude","SWEPT_EDGE",EDGE,{"disambiguationData":[OSD([sQuery(id+"F13.wireOp",EDGE,"E9.bottom"),sQuery(id+"F13.wireOp",EDGE,"E10.1.0.0"),sQuery(id+"F13.wireOp",EDGE,"E10.1.0.1")])]})});
            var Q170;
            Q170=makeQuery(id+"F14.boolean.opBoolean","COPY",EDGE,{"derivedFrom":makeQuery(id+"F14.opExtrude","SWEPT_EDGE",EDGE,{"disambiguationData":[OSD([sQuery(id+"F13.wireOp",EDGE,"E10.1.0.2"),sQuery(id+"F13.wireOp",EDGE,"E10.2.0.1")])]})});
            var Q171;
            Q171=makeQuery(id+"F14.boolean.opBoolean","COPY",EDGE,{"derivedFrom":makeQuery(id+"F14.opExtrude","SWEPT_EDGE",EDGE,{"disambiguationData":[OSD([sQuery(id+"F13.wireOp",EDGE,"E10.2.0.1"),sQuery(id+"F13.wireOp",EDGE,"E10.3.0.0"),sQuery(id+"F13.wireOp",EDGE,"E10.3.0.1")])]})});
            var Q172;
            Q172=makeQuery(id+"F14.boolean.opBoolean","COPY",EDGE,{"derivedFrom":makeQuery(id+"F14.opExtrude","SWEPT_EDGE",EDGE,{"disambiguationData":[OSD([sQuery(id+"F13.wireOp",EDGE,"E10.3.0.2"),sQuery(id+"F13.wireOp",EDGE,"E10.4.0.1")])]})});
            var Q173;
            Q173=makeQuery(id+"F14.boolean.opBoolean","COPY",EDGE,{"derivedFrom":makeQuery(id+"F14.opExtrude","SWEPT_EDGE",EDGE,{"disambiguationData":[OSD([sQuery(id+"F13.wireOp",EDGE,"E10.4.0.1"),sQuery(id+"F13.wireOp",EDGE,"E10.5.0.0"),sQuery(id+"F13.wireOp",EDGE,"E10.5.0.1")])]})});
            var Q174;
            Q174=makeQuery(id+"F14.boolean.opBoolean","COPY",EDGE,{"derivedFrom":makeQuery(id+"F14.opExtrude","SWEPT_EDGE",EDGE,{"disambiguationData":[OSD([sQuery(id+"F13.wireOp",EDGE,"E10.5.0.2"),sQuery(id+"F13.wireOp",EDGE,"E10.6.0.1")])]})});
            var Q175;
            Q175=makeQuery(id+"F14.boolean.opBoolean","COPY",EDGE,{"derivedFrom":makeQuery(id+"F14.opExtrude","SWEPT_EDGE",EDGE,{"disambiguationData":[OSD([sQuery(id+"F13.wireOp",EDGE,"E10.6.0.1"),sQuery(id+"F13.wireOp",EDGE,"E10.7.0.0"),sQuery(id+"F13.wireOp",EDGE,"E10.7.0.1")])]})});
            var Q176;
            Q176=makeQuery(id+"F14.boolean.opBoolean","COPY",EDGE,{"derivedFrom":makeQuery(id+"F14.opExtrude","SWEPT_EDGE",EDGE,{"disambiguationData":[OSD([sQuery(id+"F13.wireOp",EDGE,"E10.7.0.2"),sQuery(id+"F13.wireOp",EDGE,"E10.8.0.1")])]})});
            var Q177;
            Q177=makeQuery(id+"F14.boolean.opBoolean","COPY",EDGE,{"derivedFrom":makeQuery(id+"F14.opExtrude","SWEPT_EDGE",EDGE,{"disambiguationData":[OSD([sQuery(id+"F13.wireOp",EDGE,"E10.8.0.1"),sQuery(id+"F13.wireOp",EDGE,"E10.9.0.0"),sQuery(id+"F13.wireOp",EDGE,"E10.9.0.1")])]})});
            var Q178;
            Q178=makeQuery(id+"F14.boolean.opBoolean","COPY",EDGE,{"derivedFrom":makeQuery(id+"F14.opExtrude","SWEPT_EDGE",EDGE,{"disambiguationData":[OSD([sQuery(id+"F13.wireOp",EDGE,"E10.9.0.2"),sQuery(id+"F13.wireOp",EDGE,"E10.10.0.1")])]})});
            var Q179;
            Q179=makeQuery(id+"F14.boolean.opBoolean","COPY",EDGE,{"derivedFrom":makeQuery(id+"F14.opExtrude","SWEPT_EDGE",EDGE,{"disambiguationData":[OSD([sQuery(id+"F13.wireOp",EDGE,"E10.10.0.1"),sQuery(id+"F13.wireOp",EDGE,"E10.11.0.0"),sQuery(id+"F13.wireOp",EDGE,"E10.11.0.1")])]})});
            var Q180;
            Q180=makeQuery(id+"F14.boolean.opBoolean","COPY",EDGE,{"derivedFrom":makeQuery(id+"F14.opExtrude","SWEPT_EDGE",EDGE,{"disambiguationData":[OSD([sQuery(id+"F13.wireOp",EDGE,"E10.12.0.1"),sQuery(id+"F13.wireOp",EDGE,"E10.13.0.0"),sQuery(id+"F13.wireOp",EDGE,"E10.13.0.1")])]})});
            var Q181;
            Q181=makeQuery(id+"F14.boolean.opBoolean","COPY",EDGE,{"derivedFrom":makeQuery(id+"F14.opExtrude","SWEPT_EDGE",EDGE,{"disambiguationData":[OSD([sQuery(id+"F13.wireOp",EDGE,"E10.11.0.2"),sQuery(id+"F13.wireOp",EDGE,"E10.12.0.1")])]})});
            var Q182;
            Q182=makeQuery(id+"F14.boolean.opBoolean","COPY",EDGE,{"derivedFrom":makeQuery(id+"F14.opExtrude","SWEPT_EDGE",EDGE,{"disambiguationData":[OSD([sQuery(id+"F13.wireOp",EDGE,"E10.13.0.2"),sQuery(id+"F13.wireOp",EDGE,"E10.14.0.1")])]})});
            var Q183;
            Q183=makeQuery(id+"F14.boolean.opBoolean","COPY",EDGE,{"derivedFrom":makeQuery(id+"F14.opExtrude","SWEPT_EDGE",EDGE,{"disambiguationData":[OSD([sQuery(id+"F13.wireOp",EDGE,"E10.14.0.1"),sQuery(id+"F13.wireOp",EDGE,"E10.15.0.0"),sQuery(id+"F13.wireOp",EDGE,"E10.15.0.1")])]})});
            var Q184;
            Q184=makeQuery(id+"F14.boolean.opBoolean","COPY",EDGE,{"derivedFrom":makeQuery(id+"F14.opExtrude","SWEPT_EDGE",EDGE,{"disambiguationData":[OSD([sQuery(id+"F13.wireOp",EDGE,"E10.15.0.2"),sQuery(id+"F13.wireOp",EDGE,"E10.16.0.1")])]})});
            var Q185;
            Q185=makeQuery(id+"F14.boolean.opBoolean","COPY",EDGE,{"derivedFrom":makeQuery(id+"F14.opExtrude","SWEPT_EDGE",EDGE,{"disambiguationData":[OSD([sQuery(id+"F13.wireOp",EDGE,"E10.16.0.1"),sQuery(id+"F13.wireOp",EDGE,"E10.17.0.0"),sQuery(id+"F13.wireOp",EDGE,"E10.17.0.1")])]})});
            var Q186;
            Q186=makeQuery(id+"F14.boolean.opBoolean","COPY",EDGE,{"derivedFrom":makeQuery(id+"F14.opExtrude","SWEPT_EDGE",EDGE,{"disambiguationData":[OSD([sQuery(id+"F13.wireOp",EDGE,"E10.17.0.2"),sQuery(id+"F13.wireOp",EDGE,"E10.18.0.1")])]})});
            var Q187;
            Q187=makeQuery(id+"F14.boolean.opBoolean","COPY",EDGE,{"derivedFrom":makeQuery(id+"F14.opExtrude","SWEPT_EDGE",EDGE,{"disambiguationData":[OSD([sQuery(id+"F13.wireOp",EDGE,"E10.18.0.1"),sQuery(id+"F13.wireOp",EDGE,"E10.19.0.0"),sQuery(id+"F13.wireOp",EDGE,"E10.19.0.1")])]})});
            var Q188;
            Q188=makeQuery(id+"F14.boolean.opBoolean","COPY",EDGE,{"derivedFrom":makeQuery(id+"F14.opExtrude","SWEPT_EDGE",EDGE,{"disambiguationData":[OSD([sQuery(id+"F13.wireOp",EDGE,"E10.19.0.2"),sQuery(id+"F13.wireOp",EDGE,"E10.20.0.1")])]})});
            var Q189;
            Q189=makeQuery(id+"F14.boolean.opBoolean","COPY",EDGE,{"derivedFrom":makeQuery(id+"F14.opExtrude","SWEPT_EDGE",EDGE,{"disambiguationData":[OSD([sQuery(id+"F13.wireOp",EDGE,"E10.20.0.1"),sQuery(id+"F13.wireOp",EDGE,"E10.21.0.0"),sQuery(id+"F13.wireOp",EDGE,"E10.21.0.1")])]})});
            var Q190;
            Q190=makeQuery(id+"F14.boolean.opBoolean","COPY",EDGE,{"derivedFrom":makeQuery(id+"F14.opExtrude","SWEPT_EDGE",EDGE,{"disambiguationData":[OSD([sQuery(id+"F13.wireOp",EDGE,"E10.21.0.2"),sQuery(id+"F13.wireOp",EDGE,"E10.22.0.1")])]})});
            var Q191;
            Q191=makeQuery(id+"F14.boolean.opBoolean","COPY",EDGE,{"derivedFrom":makeQuery(id+"F14.opExtrude","SWEPT_EDGE",EDGE,{"disambiguationData":[OSD([sQuery(id+"F13.wireOp",EDGE,"E10.22.0.1"),sQuery(id+"F13.wireOp",EDGE,"E10.23.0.0"),sQuery(id+"F13.wireOp",EDGE,"E10.23.0.1")])]})});
            var Q192;
            Q192=makeQuery(id+"F14.boolean.opBoolean","COPY",EDGE,{"derivedFrom":makeQuery(id+"F14.opExtrude","SWEPT_EDGE",EDGE,{"disambiguationData":[OSD([sQuery(id+"F13.wireOp",EDGE,"E10.23.0.2"),sQuery(id+"F13.wireOp",EDGE,"E10.24.0.1")])]})});
            var Q193;
            Q193=makeQuery(id+"F14.boolean.opBoolean","COPY",EDGE,{"derivedFrom":makeQuery(id+"F14.opExtrude","SWEPT_EDGE",EDGE,{"disambiguationData":[OSD([sQuery(id+"F13.wireOp",EDGE,"E10.24.0.1"),sQuery(id+"F13.wireOp",EDGE,"E10.25.0.0"),sQuery(id+"F13.wireOp",EDGE,"E10.25.0.1")])]})});
            var Q194;
            Q194=makeQuery(id+"F14.boolean.opBoolean","COPY",EDGE,{"derivedFrom":makeQuery(id+"F14.opExtrude","SWEPT_EDGE",EDGE,{"disambiguationData":[OSD([sQuery(id+"F13.wireOp",EDGE,"E10.25.0.2"),sQuery(id+"F13.wireOp",EDGE,"E10.26.0.1")])]})});
            var Q195;
            Q195=makeQuery(id+"F14.boolean.opBoolean","COPY",EDGE,{"derivedFrom":makeQuery(id+"F14.opExtrude","SWEPT_EDGE",EDGE,{"disambiguationData":[OSD([sQuery(id+"F13.wireOp",EDGE,"E10.26.0.1"),sQuery(id+"F13.wireOp",EDGE,"E10.27.0.0"),sQuery(id+"F13.wireOp",EDGE,"E10.27.0.1")])]})});
            var Q196;
            Q196=makeQuery(id+"F14.boolean.opBoolean","COPY",EDGE,{"derivedFrom":makeQuery(id+"F14.opExtrude","SWEPT_EDGE",EDGE,{"disambiguationData":[OSD([sQuery(id+"F13.wireOp",EDGE,"E10.27.0.2"),sQuery(id+"F13.wireOp",EDGE,"E10.28.0.1")])]})});
            var Q197;
            Q197=makeQuery(id+"F14.boolean.opBoolean","COPY",EDGE,{"derivedFrom":makeQuery(id+"F14.opExtrude","SWEPT_EDGE",EDGE,{"disambiguationData":[OSD([sQuery(id+"F13.wireOp",EDGE,"E10.28.0.1"),sQuery(id+"F13.wireOp",EDGE,"E10.29.0.0"),sQuery(id+"F13.wireOp",EDGE,"E10.29.0.1")])]})});
            var Q198;
            Q198=makeQuery(id+"F14.boolean.opBoolean","COPY",EDGE,{"derivedFrom":makeQuery(id+"F14.opExtrude","SWEPT_EDGE",EDGE,{"disambiguationData":[OSD([sQuery(id+"F13.wireOp",EDGE,"E10.29.0.2"),sQuery(id+"F13.wireOp",EDGE,"E10.30.0.1")])]})});
            var Q199;
            Q199=makeQuery(id+"F14.boolean.opBoolean","COPY",EDGE,{"derivedFrom":makeQuery(id+"F14.opExtrude","SWEPT_EDGE",EDGE,{"disambiguationData":[OSD([sQuery(id+"F13.wireOp",EDGE,"E10.66.0.1"),sQuery(id+"F13.wireOp",EDGE,"E10.67.0.0"),sQuery(id+"F13.wireOp",EDGE,"E10.67.0.1")])]})});
            var Q200;
            Q200=makeQuery(id+"F16.boolean.opBoolean","COPY",EDGE,{"derivedFrom":makeQuery(id+"F16.opExtrude","SWEPT_EDGE",EDGE,{"disambiguationData":[OSD([sQuery(id+"F0.wireOp",EDGE,"E0.top"),sQuery(id+"F15.wireOp",EDGE,"E15.72.0.0")])]})});
            fillet(context, id + "F20", {"entities" : qUnion([Q0, Q1, Q2, Q3, Q4, Q5, Q6, Q7, Q8, Q9, Q10, Q11, Q12, Q13, Q14, Q15, Q16, Q17, Q18, Q19, Q20, Q21, Q22, Q23, Q24, Q25, Q26, Q27, Q28, Q29, Q30, Q31, Q32, Q33, Q34, Q35, Q36, Q37, Q38, Q39, Q40, Q41, Q42, Q43, Q44, Q45, Q46, Q47, Q48, Q49, Q50, Q51, Q52, Q53, Q54, Q55, Q56, Q57, Q58, Q59, Q60, Q61, Q62, Q63, Q64, Q65, Q66, Q67, Q68, Q69, Q70, Q71, Q72, Q73, Q74, Q75, Q76, Q77, Q78, Q79, Q80, Q81, Q82, Q83, Q84, Q85, Q86, Q87, Q88, Q89, Q90, Q91, Q92, Q93, Q94, Q95, Q96, Q97, Q98, Q99, Q100, Q101, Q102, Q103, Q104, Q105, Q106, Q107, Q108, Q109, Q110, Q111, Q112, Q113, Q114, Q115, Q116, Q117, Q118, Q119, Q120, Q121, Q122, Q123, Q124, Q125, Q126, Q127, Q128, Q129, Q130, Q131, Q132, Q133, Q134, Q135, Q136, Q137, Q138, Q139, Q140, Q141, Q142, Q143, Q144, Q145, Q146, Q147, Q148, Q149, Q150, Q151, Q152, Q153, Q154, Q155, Q156, Q157, Q158, Q159, Q160, Q161, Q162, Q163, Q164, Q165, Q166, Q167, Q168, Q169, Q170, Q171, Q172, Q173, Q174, Q175, Q176, Q177, Q178, Q179, Q180, Q181, Q182, Q183, Q184, Q185, Q186, Q187, Q188, Q189, Q190, Q191, Q192, Q193, Q194, Q195, Q196, Q197, Q198, Q199, Q200]), "radius" : 1.6 * mm, "tangentPropagation" : true, "allowEdgeOverflow" : false});
        }
        {
            var Q0;
            Q0=makeQuery(id+"F20.opFillet","BLEND_EDGE",EDGE,{"blendedFrom":[makeQuery(id+"F1.opExtrude","CAP_EDGE",EDGE,{"disambiguationData":[OSD([sQuery(id+"F0.wireOp",EDGE,"E0.left")])],"isStart":false}),makeQuery(id+"F14.boolean.opBoolean","COPY",EDGE,{"derivedFrom":makeQuery(id+"F14.opExtrude","SWEPT_EDGE",EDGE,{"disambiguationData":[OSD([sQuery(id+"F0.wireOp",EDGE,"E0.top"),sQuery(id+"F13.wireOp",EDGE,"E9.bottom"),sQuery(id+"F13.wireOp",EDGE,"E9.left")])]})})],"blendedInto":[]});
            var Q1;
            Q1=makeQuery(id+"F20.opFillet","BLEND_EDGE",EDGE,{"blendedFrom":[makeQuery(id+"F14.boolean.opBoolean","COPY",EDGE,{"derivedFrom":makeQuery(id+"F14.opExtrude","SWEPT_EDGE",EDGE,{"disambiguationData":[OSD([sQuery(id+"F13.wireOp",EDGE,"E9.bottom"),sQuery(id+"F13.wireOp",EDGE,"E10.1.0.0"),sQuery(id+"F13.wireOp",EDGE,"E10.1.0.1")])]})}),makeQuery(id+"F14.boolean.opBoolean","COPY",EDGE,{"derivedFrom":makeQuery(id+"F14.opExtrude","SWEPT_EDGE",EDGE,{"disambiguationData":[OSD([sQuery(id+"F13.wireOp",EDGE,"E10.1.0.2"),sQuery(id+"F13.wireOp",EDGE,"E10.2.0.1")])]})})],"blendedInto":[]});
            var Q2;
            Q2=makeQuery(id+"F20.opFillet","BLEND_EDGE",EDGE,{"blendedFrom":[makeQuery(id+"F14.boolean.opBoolean","COPY",EDGE,{"derivedFrom":makeQuery(id+"F14.opExtrude","SWEPT_EDGE",EDGE,{"disambiguationData":[OSD([sQuery(id+"F13.wireOp",EDGE,"E10.2.0.1"),sQuery(id+"F13.wireOp",EDGE,"E10.3.0.0"),sQuery(id+"F13.wireOp",EDGE,"E10.3.0.1")])]})}),makeQuery(id+"F14.boolean.opBoolean","COPY",EDGE,{"derivedFrom":makeQuery(id+"F14.opExtrude","SWEPT_EDGE",EDGE,{"disambiguationData":[OSD([sQuery(id+"F13.wireOp",EDGE,"E10.3.0.2"),sQuery(id+"F13.wireOp",EDGE,"E10.4.0.1")])]})})],"blendedInto":[]});
            var Q3;
            Q3=makeQuery(id+"F20.opFillet","BLEND_EDGE",EDGE,{"blendedFrom":[makeQuery(id+"F14.boolean.opBoolean","COPY",EDGE,{"derivedFrom":makeQuery(id+"F14.opExtrude","SWEPT_EDGE",EDGE,{"disambiguationData":[OSD([sQuery(id+"F13.wireOp",EDGE,"E10.4.0.1"),sQuery(id+"F13.wireOp",EDGE,"E10.5.0.0"),sQuery(id+"F13.wireOp",EDGE,"E10.5.0.1")])]})}),makeQuery(id+"F14.boolean.opBoolean","COPY",EDGE,{"derivedFrom":makeQuery(id+"F14.opExtrude","SWEPT_EDGE",EDGE,{"disambiguationData":[OSD([sQuery(id+"F13.wireOp",EDGE,"E10.5.0.2"),sQuery(id+"F13.wireOp",EDGE,"E10.6.0.1")])]})})],"blendedInto":[]});
            var Q4;
            Q4=makeQuery(id+"F20.opFillet","BLEND_EDGE",EDGE,{"blendedFrom":[makeQuery(id+"F14.boolean.opBoolean","COPY",EDGE,{"derivedFrom":makeQuery(id+"F14.opExtrude","SWEPT_EDGE",EDGE,{"disambiguationData":[OSD([sQuery(id+"F13.wireOp",EDGE,"E10.6.0.1"),sQuery(id+"F13.wireOp",EDGE,"E10.7.0.0"),sQuery(id+"F13.wireOp",EDGE,"E10.7.0.1")])]})}),makeQuery(id+"F14.boolean.opBoolean","COPY",EDGE,{"derivedFrom":makeQuery(id+"F14.opExtrude","SWEPT_EDGE",EDGE,{"disambiguationData":[OSD([sQuery(id+"F13.wireOp",EDGE,"E10.7.0.2"),sQuery(id+"F13.wireOp",EDGE,"E10.8.0.1")])]})})],"blendedInto":[]});
            var Q5;
            Q5=makeQuery(id+"F20.opFillet","BLEND_EDGE",EDGE,{"blendedFrom":[makeQuery(id+"F14.boolean.opBoolean","COPY",EDGE,{"derivedFrom":makeQuery(id+"F14.opExtrude","SWEPT_EDGE",EDGE,{"disambiguationData":[OSD([sQuery(id+"F13.wireOp",EDGE,"E10.8.0.1"),sQuery(id+"F13.wireOp",EDGE,"E10.9.0.0"),sQuery(id+"F13.wireOp",EDGE,"E10.9.0.1")])]})}),makeQuery(id+"F14.boolean.opBoolean","COPY",EDGE,{"derivedFrom":makeQuery(id+"F14.opExtrude","SWEPT_EDGE",EDGE,{"disambiguationData":[OSD([sQuery(id+"F13.wireOp",EDGE,"E10.9.0.2"),sQuery(id+"F13.wireOp",EDGE,"E10.10.0.1")])]})})],"blendedInto":[]});
            var Q6;
            Q6=makeQuery(id+"F20.opFillet","BLEND_EDGE",EDGE,{"blendedFrom":[makeQuery(id+"F14.boolean.opBoolean","COPY",EDGE,{"derivedFrom":makeQuery(id+"F14.opExtrude","SWEPT_EDGE",EDGE,{"disambiguationData":[OSD([sQuery(id+"F13.wireOp",EDGE,"E10.10.0.1"),sQuery(id+"F13.wireOp",EDGE,"E10.11.0.0"),sQuery(id+"F13.wireOp",EDGE,"E10.11.0.1")])]})}),makeQuery(id+"F14.boolean.opBoolean","COPY",EDGE,{"derivedFrom":makeQuery(id+"F14.opExtrude","SWEPT_EDGE",EDGE,{"disambiguationData":[OSD([sQuery(id+"F13.wireOp",EDGE,"E10.11.0.2"),sQuery(id+"F13.wireOp",EDGE,"E10.12.0.1")])]})})],"blendedInto":[]});
            var Q7;
            Q7=makeQuery(id+"F20.opFillet","BLEND_EDGE",EDGE,{"blendedFrom":[makeQuery(id+"F14.boolean.opBoolean","COPY",EDGE,{"derivedFrom":makeQuery(id+"F14.opExtrude","SWEPT_EDGE",EDGE,{"disambiguationData":[OSD([sQuery(id+"F13.wireOp",EDGE,"E10.12.0.1"),sQuery(id+"F13.wireOp",EDGE,"E10.13.0.0"),sQuery(id+"F13.wireOp",EDGE,"E10.13.0.1")])]})}),makeQuery(id+"F14.boolean.opBoolean","COPY",EDGE,{"derivedFrom":makeQuery(id+"F14.opExtrude","SWEPT_EDGE",EDGE,{"disambiguationData":[OSD([sQuery(id+"F13.wireOp",EDGE,"E10.13.0.2"),sQuery(id+"F13.wireOp",EDGE,"E10.14.0.1")])]})})],"blendedInto":[]});
            var Q8;
            Q8=makeQuery(id+"F20.opFillet","BLEND_EDGE",EDGE,{"blendedFrom":[makeQuery(id+"F14.boolean.opBoolean","COPY",EDGE,{"derivedFrom":makeQuery(id+"F14.opExtrude","SWEPT_EDGE",EDGE,{"disambiguationData":[OSD([sQuery(id+"F13.wireOp",EDGE,"E10.14.0.1"),sQuery(id+"F13.wireOp",EDGE,"E10.15.0.0"),sQuery(id+"F13.wireOp",EDGE,"E10.15.0.1")])]})}),makeQuery(id+"F14.boolean.opBoolean","COPY",EDGE,{"derivedFrom":makeQuery(id+"F14.opExtrude","SWEPT_EDGE",EDGE,{"disambiguationData":[OSD([sQuery(id+"F13.wireOp",EDGE,"E10.15.0.2"),sQuery(id+"F13.wireOp",EDGE,"E10.16.0.1")])]})})],"blendedInto":[]});
            var Q9;
            Q9=makeQuery(id+"F20.opFillet","BLEND_EDGE",EDGE,{"blendedFrom":[makeQuery(id+"F14.boolean.opBoolean","COPY",EDGE,{"derivedFrom":makeQuery(id+"F14.opExtrude","SWEPT_EDGE",EDGE,{"disambiguationData":[OSD([sQuery(id+"F13.wireOp",EDGE,"E10.16.0.1"),sQuery(id+"F13.wireOp",EDGE,"E10.17.0.0"),sQuery(id+"F13.wireOp",EDGE,"E10.17.0.1")])]})}),makeQuery(id+"F14.boolean.opBoolean","COPY",EDGE,{"derivedFrom":makeQuery(id+"F14.opExtrude","SWEPT_EDGE",EDGE,{"disambiguationData":[OSD([sQuery(id+"F13.wireOp",EDGE,"E10.17.0.2"),sQuery(id+"F13.wireOp",EDGE,"E10.18.0.1")])]})})],"blendedInto":[]});
            var Q10;
            Q10=makeQuery(id+"F20.opFillet","BLEND_EDGE",EDGE,{"blendedFrom":[makeQuery(id+"F14.boolean.opBoolean","COPY",EDGE,{"derivedFrom":makeQuery(id+"F14.opExtrude","SWEPT_EDGE",EDGE,{"disambiguationData":[OSD([sQuery(id+"F13.wireOp",EDGE,"E10.18.0.1"),sQuery(id+"F13.wireOp",EDGE,"E10.19.0.0"),sQuery(id+"F13.wireOp",EDGE,"E10.19.0.1")])]})}),makeQuery(id+"F14.boolean.opBoolean","COPY",EDGE,{"derivedFrom":makeQuery(id+"F14.opExtrude","SWEPT_EDGE",EDGE,{"disambiguationData":[OSD([sQuery(id+"F13.wireOp",EDGE,"E10.19.0.2"),sQuery(id+"F13.wireOp",EDGE,"E10.20.0.1")])]})})],"blendedInto":[]});
            var Q11;
            Q11=makeQuery(id+"F20.opFillet","BLEND_EDGE",EDGE,{"blendedFrom":[makeQuery(id+"F14.boolean.opBoolean","COPY",EDGE,{"derivedFrom":makeQuery(id+"F14.opExtrude","SWEPT_EDGE",EDGE,{"disambiguationData":[OSD([sQuery(id+"F13.wireOp",EDGE,"E10.20.0.1"),sQuery(id+"F13.wireOp",EDGE,"E10.21.0.0"),sQuery(id+"F13.wireOp",EDGE,"E10.21.0.1")])]})}),makeQuery(id+"F14.boolean.opBoolean","COPY",EDGE,{"derivedFrom":makeQuery(id+"F14.opExtrude","SWEPT_EDGE",EDGE,{"disambiguationData":[OSD([sQuery(id+"F13.wireOp",EDGE,"E10.21.0.2"),sQuery(id+"F13.wireOp",EDGE,"E10.22.0.1")])]})})],"blendedInto":[]});
            var Q12;
            Q12=makeQuery(id+"F20.opFillet","BLEND_EDGE",EDGE,{"blendedFrom":[makeQuery(id+"F14.boolean.opBoolean","COPY",EDGE,{"derivedFrom":makeQuery(id+"F14.opExtrude","SWEPT_EDGE",EDGE,{"disambiguationData":[OSD([sQuery(id+"F13.wireOp",EDGE,"E10.22.0.1"),sQuery(id+"F13.wireOp",EDGE,"E10.23.0.0"),sQuery(id+"F13.wireOp",EDGE,"E10.23.0.1")])]})}),makeQuery(id+"F14.boolean.opBoolean","COPY",EDGE,{"derivedFrom":makeQuery(id+"F14.opExtrude","SWEPT_EDGE",EDGE,{"disambiguationData":[OSD([sQuery(id+"F13.wireOp",EDGE,"E10.23.0.2"),sQuery(id+"F13.wireOp",EDGE,"E10.24.0.1")])]})})],"blendedInto":[]});
            var Q13;
            Q13=makeQuery(id+"F20.opFillet","BLEND_EDGE",EDGE,{"blendedFrom":[makeQuery(id+"F14.boolean.opBoolean","COPY",EDGE,{"derivedFrom":makeQuery(id+"F14.opExtrude","SWEPT_EDGE",EDGE,{"disambiguationData":[OSD([sQuery(id+"F13.wireOp",EDGE,"E10.24.0.1"),sQuery(id+"F13.wireOp",EDGE,"E10.25.0.0"),sQuery(id+"F13.wireOp",EDGE,"E10.25.0.1")])]})}),makeQuery(id+"F14.boolean.opBoolean","COPY",EDGE,{"derivedFrom":makeQuery(id+"F14.opExtrude","SWEPT_EDGE",EDGE,{"disambiguationData":[OSD([sQuery(id+"F13.wireOp",EDGE,"E10.25.0.2"),sQuery(id+"F13.wireOp",EDGE,"E10.26.0.1")])]})})],"blendedInto":[]});
            var Q14;
            Q14=makeQuery(id+"F20.opFillet","BLEND_EDGE",EDGE,{"blendedFrom":[makeQuery(id+"F14.boolean.opBoolean","COPY",EDGE,{"derivedFrom":makeQuery(id+"F14.opExtrude","SWEPT_EDGE",EDGE,{"disambiguationData":[OSD([sQuery(id+"F13.wireOp",EDGE,"E10.26.0.1"),sQuery(id+"F13.wireOp",EDGE,"E10.27.0.0"),sQuery(id+"F13.wireOp",EDGE,"E10.27.0.1")])]})}),makeQuery(id+"F14.boolean.opBoolean","COPY",EDGE,{"derivedFrom":makeQuery(id+"F14.opExtrude","SWEPT_EDGE",EDGE,{"disambiguationData":[OSD([sQuery(id+"F13.wireOp",EDGE,"E10.27.0.2"),sQuery(id+"F13.wireOp",EDGE,"E10.28.0.1")])]})})],"blendedInto":[]});
            var Q15;
            Q15=makeQuery(id+"F20.opFillet","BLEND_EDGE",EDGE,{"blendedFrom":[makeQuery(id+"F14.boolean.opBoolean","COPY",EDGE,{"derivedFrom":makeQuery(id+"F14.opExtrude","SWEPT_EDGE",EDGE,{"disambiguationData":[OSD([sQuery(id+"F13.wireOp",EDGE,"E10.28.0.1"),sQuery(id+"F13.wireOp",EDGE,"E10.29.0.0"),sQuery(id+"F13.wireOp",EDGE,"E10.29.0.1")])]})}),makeQuery(id+"F14.boolean.opBoolean","COPY",EDGE,{"derivedFrom":makeQuery(id+"F14.opExtrude","SWEPT_EDGE",EDGE,{"disambiguationData":[OSD([sQuery(id+"F13.wireOp",EDGE,"E10.29.0.2"),sQuery(id+"F13.wireOp",EDGE,"E10.30.0.1")])]})})],"blendedInto":[]});
            var Q16;
            Q16=makeQuery(id+"F20.opFillet","BLEND_EDGE",EDGE,{"blendedFrom":[makeQuery(id+"F14.boolean.opBoolean","COPY",EDGE,{"derivedFrom":makeQuery(id+"F14.opExtrude","SWEPT_EDGE",EDGE,{"disambiguationData":[OSD([sQuery(id+"F13.wireOp",EDGE,"E10.30.0.1"),sQuery(id+"F13.wireOp",EDGE,"E10.31.0.0"),sQuery(id+"F13.wireOp",EDGE,"E10.31.0.1")])]})}),makeQuery(id+"F14.boolean.opBoolean","COPY",EDGE,{"derivedFrom":makeQuery(id+"F14.opExtrude","SWEPT_EDGE",EDGE,{"disambiguationData":[OSD([sQuery(id+"F13.wireOp",EDGE,"E10.31.0.2"),sQuery(id+"F13.wireOp",EDGE,"E10.32.0.1")])]})})],"blendedInto":[]});
            var Q17;
            Q17=makeQuery(id+"F20.opFillet","BLEND_EDGE",EDGE,{"blendedFrom":[makeQuery(id+"F14.boolean.opBoolean","COPY",EDGE,{"derivedFrom":makeQuery(id+"F14.opExtrude","SWEPT_EDGE",EDGE,{"disambiguationData":[OSD([sQuery(id+"F13.wireOp",EDGE,"E10.32.0.1"),sQuery(id+"F13.wireOp",EDGE,"E10.33.0.0"),sQuery(id+"F13.wireOp",EDGE,"E10.33.0.1")])]})}),makeQuery(id+"F14.boolean.opBoolean","COPY",EDGE,{"derivedFrom":makeQuery(id+"F14.opExtrude","SWEPT_EDGE",EDGE,{"disambiguationData":[OSD([sQuery(id+"F13.wireOp",EDGE,"E10.33.0.2"),sQuery(id+"F13.wireOp",EDGE,"E10.34.0.1")])]})})],"blendedInto":[]});
            var Q18;
            Q18=makeQuery(id+"F20.opFillet","BLEND_EDGE",EDGE,{"blendedFrom":[makeQuery(id+"F14.boolean.opBoolean","COPY",EDGE,{"derivedFrom":makeQuery(id+"F14.opExtrude","SWEPT_EDGE",EDGE,{"disambiguationData":[OSD([sQuery(id+"F13.wireOp",EDGE,"E10.34.0.1"),sQuery(id+"F13.wireOp",EDGE,"E10.35.0.0"),sQuery(id+"F13.wireOp",EDGE,"E10.35.0.1")])]})}),makeQuery(id+"F14.boolean.opBoolean","COPY",EDGE,{"derivedFrom":makeQuery(id+"F14.opExtrude","SWEPT_EDGE",EDGE,{"disambiguationData":[OSD([sQuery(id+"F13.wireOp",EDGE,"E10.35.0.2"),sQuery(id+"F13.wireOp",EDGE,"E10.36.0.1")])]})})],"blendedInto":[]});
            var Q19;
            Q19=makeQuery(id+"F20.opFillet","BLEND_EDGE",EDGE,{"blendedFrom":[makeQuery(id+"F14.boolean.opBoolean","COPY",EDGE,{"derivedFrom":makeQuery(id+"F14.opExtrude","SWEPT_EDGE",EDGE,{"disambiguationData":[OSD([sQuery(id+"F13.wireOp",EDGE,"E10.36.0.1"),sQuery(id+"F13.wireOp",EDGE,"E10.37.0.0"),sQuery(id+"F13.wireOp",EDGE,"E10.37.0.1")])]})}),makeQuery(id+"F14.boolean.opBoolean","COPY",EDGE,{"derivedFrom":makeQuery(id+"F14.opExtrude","SWEPT_EDGE",EDGE,{"disambiguationData":[OSD([sQuery(id+"F13.wireOp",EDGE,"E10.37.0.2"),sQuery(id+"F13.wireOp",EDGE,"E10.38.0.1")])]})})],"blendedInto":[]});
            var Q20;
            Q20=makeQuery(id+"F20.opFillet","BLEND_EDGE",EDGE,{"blendedFrom":[makeQuery(id+"F14.boolean.opBoolean","COPY",EDGE,{"derivedFrom":makeQuery(id+"F14.opExtrude","SWEPT_EDGE",EDGE,{"disambiguationData":[OSD([sQuery(id+"F13.wireOp",EDGE,"E10.38.0.1"),sQuery(id+"F13.wireOp",EDGE,"E10.39.0.0"),sQuery(id+"F13.wireOp",EDGE,"E10.39.0.1")])]})}),makeQuery(id+"F14.boolean.opBoolean","COPY",EDGE,{"derivedFrom":makeQuery(id+"F14.opExtrude","SWEPT_EDGE",EDGE,{"disambiguationData":[OSD([sQuery(id+"F13.wireOp",EDGE,"E10.39.0.2"),sQuery(id+"F13.wireOp",EDGE,"E10.40.0.1")])]})})],"blendedInto":[]});
            var Q21;
            Q21=makeQuery(id+"F20.opFillet","BLEND_EDGE",EDGE,{"blendedFrom":[makeQuery(id+"F14.boolean.opBoolean","COPY",EDGE,{"derivedFrom":makeQuery(id+"F14.opExtrude","SWEPT_EDGE",EDGE,{"disambiguationData":[OSD([sQuery(id+"F13.wireOp",EDGE,"E10.40.0.1"),sQuery(id+"F13.wireOp",EDGE,"E10.41.0.0"),sQuery(id+"F13.wireOp",EDGE,"E10.41.0.1")])]})}),makeQuery(id+"F14.boolean.opBoolean","COPY",EDGE,{"derivedFrom":makeQuery(id+"F14.opExtrude","SWEPT_EDGE",EDGE,{"disambiguationData":[OSD([sQuery(id+"F13.wireOp",EDGE,"E10.41.0.2"),sQuery(id+"F13.wireOp",EDGE,"E10.42.0.1")])]})})],"blendedInto":[]});
            var Q22;
            Q22=makeQuery(id+"F20.opFillet","BLEND_EDGE",EDGE,{"blendedFrom":[makeQuery(id+"F14.boolean.opBoolean","COPY",EDGE,{"derivedFrom":makeQuery(id+"F14.opExtrude","SWEPT_EDGE",EDGE,{"disambiguationData":[OSD([sQuery(id+"F13.wireOp",EDGE,"E10.42.0.1"),sQuery(id+"F13.wireOp",EDGE,"E10.43.0.0"),sQuery(id+"F13.wireOp",EDGE,"E10.43.0.1")])]})}),makeQuery(id+"F14.boolean.opBoolean","COPY",EDGE,{"derivedFrom":makeQuery(id+"F14.opExtrude","SWEPT_EDGE",EDGE,{"disambiguationData":[OSD([sQuery(id+"F13.wireOp",EDGE,"E10.43.0.2"),sQuery(id+"F13.wireOp",EDGE,"E10.44.0.1")])]})})],"blendedInto":[]});
            var Q23;
            Q23=makeQuery(id+"F20.opFillet","BLEND_EDGE",EDGE,{"blendedFrom":[makeQuery(id+"F14.boolean.opBoolean","COPY",EDGE,{"derivedFrom":makeQuery(id+"F14.opExtrude","SWEPT_EDGE",EDGE,{"disambiguationData":[OSD([sQuery(id+"F13.wireOp",EDGE,"E10.44.0.1"),sQuery(id+"F13.wireOp",EDGE,"E10.45.0.0"),sQuery(id+"F13.wireOp",EDGE,"E10.45.0.1")])]})}),makeQuery(id+"F14.boolean.opBoolean","COPY",EDGE,{"derivedFrom":makeQuery(id+"F14.opExtrude","SWEPT_EDGE",EDGE,{"disambiguationData":[OSD([sQuery(id+"F13.wireOp",EDGE,"E10.45.0.2"),sQuery(id+"F13.wireOp",EDGE,"E10.46.0.1")])]})})],"blendedInto":[]});
            var Q24;
            Q24=makeQuery(id+"F20.opFillet","BLEND_EDGE",EDGE,{"blendedFrom":[makeQuery(id+"F14.boolean.opBoolean","COPY",EDGE,{"derivedFrom":makeQuery(id+"F14.opExtrude","SWEPT_EDGE",EDGE,{"disambiguationData":[OSD([sQuery(id+"F13.wireOp",EDGE,"E10.46.0.1"),sQuery(id+"F13.wireOp",EDGE,"E10.47.0.0"),sQuery(id+"F13.wireOp",EDGE,"E10.47.0.1")])]})}),makeQuery(id+"F14.boolean.opBoolean","COPY",EDGE,{"derivedFrom":makeQuery(id+"F14.opExtrude","SWEPT_EDGE",EDGE,{"disambiguationData":[OSD([sQuery(id+"F13.wireOp",EDGE,"E10.47.0.2"),sQuery(id+"F13.wireOp",EDGE,"E10.48.0.1")])]})})],"blendedInto":[]});
            var Q25;
            Q25=makeQuery(id+"F20.opFillet","BLEND_EDGE",EDGE,{"blendedFrom":[makeQuery(id+"F14.boolean.opBoolean","COPY",EDGE,{"derivedFrom":makeQuery(id+"F14.opExtrude","SWEPT_EDGE",EDGE,{"disambiguationData":[OSD([sQuery(id+"F13.wireOp",EDGE,"E10.48.0.1"),sQuery(id+"F13.wireOp",EDGE,"E10.49.0.0"),sQuery(id+"F13.wireOp",EDGE,"E10.49.0.1")])]})}),makeQuery(id+"F14.boolean.opBoolean","COPY",EDGE,{"derivedFrom":makeQuery(id+"F14.opExtrude","SWEPT_EDGE",EDGE,{"disambiguationData":[OSD([sQuery(id+"F13.wireOp",EDGE,"E10.49.0.2"),sQuery(id+"F13.wireOp",EDGE,"E10.50.0.1")])]})})],"blendedInto":[]});
            var Q26;
            Q26=makeQuery(id+"F20.opFillet","BLEND_EDGE",EDGE,{"blendedFrom":[makeQuery(id+"F14.boolean.opBoolean","COPY",EDGE,{"derivedFrom":makeQuery(id+"F14.opExtrude","SWEPT_EDGE",EDGE,{"disambiguationData":[OSD([sQuery(id+"F13.wireOp",EDGE,"E10.50.0.1"),sQuery(id+"F13.wireOp",EDGE,"E10.51.0.0"),sQuery(id+"F13.wireOp",EDGE,"E10.51.0.1")])]})}),makeQuery(id+"F14.boolean.opBoolean","COPY",EDGE,{"derivedFrom":makeQuery(id+"F14.opExtrude","SWEPT_EDGE",EDGE,{"disambiguationData":[OSD([sQuery(id+"F13.wireOp",EDGE,"E10.51.0.2"),sQuery(id+"F13.wireOp",EDGE,"E10.52.0.1")])]})})],"blendedInto":[]});
            var Q27;
            Q27=makeQuery(id+"F20.opFillet","BLEND_EDGE",EDGE,{"blendedFrom":[makeQuery(id+"F14.boolean.opBoolean","COPY",EDGE,{"derivedFrom":makeQuery(id+"F14.opExtrude","SWEPT_EDGE",EDGE,{"disambiguationData":[OSD([sQuery(id+"F13.wireOp",EDGE,"E10.52.0.1"),sQuery(id+"F13.wireOp",EDGE,"E10.53.0.0"),sQuery(id+"F13.wireOp",EDGE,"E10.53.0.1")])]})}),makeQuery(id+"F14.boolean.opBoolean","COPY",EDGE,{"derivedFrom":makeQuery(id+"F14.opExtrude","SWEPT_EDGE",EDGE,{"disambiguationData":[OSD([sQuery(id+"F13.wireOp",EDGE,"E10.53.0.2"),sQuery(id+"F13.wireOp",EDGE,"E10.54.0.1")])]})})],"blendedInto":[]});
            var Q28;
            Q28=makeQuery(id+"F20.opFillet","BLEND_EDGE",EDGE,{"blendedFrom":[makeQuery(id+"F14.boolean.opBoolean","COPY",EDGE,{"derivedFrom":makeQuery(id+"F14.opExtrude","SWEPT_EDGE",EDGE,{"disambiguationData":[OSD([sQuery(id+"F13.wireOp",EDGE,"E10.54.0.1"),sQuery(id+"F13.wireOp",EDGE,"E10.55.0.0"),sQuery(id+"F13.wireOp",EDGE,"E10.55.0.1")])]})}),makeQuery(id+"F14.boolean.opBoolean","COPY",EDGE,{"derivedFrom":makeQuery(id+"F14.opExtrude","SWEPT_EDGE",EDGE,{"disambiguationData":[OSD([sQuery(id+"F13.wireOp",EDGE,"E10.55.0.2"),sQuery(id+"F13.wireOp",EDGE,"E10.56.0.1")])]})})],"blendedInto":[]});
            var Q29;
            Q29=makeQuery(id+"F20.opFillet","BLEND_EDGE",EDGE,{"blendedFrom":[makeQuery(id+"F14.boolean.opBoolean","COPY",EDGE,{"derivedFrom":makeQuery(id+"F14.opExtrude","SWEPT_EDGE",EDGE,{"disambiguationData":[OSD([sQuery(id+"F13.wireOp",EDGE,"E10.56.0.1"),sQuery(id+"F13.wireOp",EDGE,"E10.57.0.0"),sQuery(id+"F13.wireOp",EDGE,"E10.57.0.1")])]})}),makeQuery(id+"F14.boolean.opBoolean","COPY",EDGE,{"derivedFrom":makeQuery(id+"F14.opExtrude","SWEPT_EDGE",EDGE,{"disambiguationData":[OSD([sQuery(id+"F13.wireOp",EDGE,"E10.57.0.2"),sQuery(id+"F13.wireOp",EDGE,"E10.58.0.1")])]})})],"blendedInto":[]});
            var Q30;
            Q30=makeQuery(id+"F20.opFillet","BLEND_EDGE",EDGE,{"blendedFrom":[makeQuery(id+"F14.boolean.opBoolean","COPY",EDGE,{"derivedFrom":makeQuery(id+"F14.opExtrude","SWEPT_EDGE",EDGE,{"disambiguationData":[OSD([sQuery(id+"F13.wireOp",EDGE,"E10.58.0.1"),sQuery(id+"F13.wireOp",EDGE,"E10.59.0.0"),sQuery(id+"F13.wireOp",EDGE,"E10.59.0.1")])]})}),makeQuery(id+"F14.boolean.opBoolean","COPY",EDGE,{"derivedFrom":makeQuery(id+"F14.opExtrude","SWEPT_EDGE",EDGE,{"disambiguationData":[OSD([sQuery(id+"F13.wireOp",EDGE,"E10.59.0.2"),sQuery(id+"F13.wireOp",EDGE,"E10.60.0.1")])]})})],"blendedInto":[]});
            var Q31;
            Q31=makeQuery(id+"F20.opFillet","BLEND_EDGE",EDGE,{"blendedFrom":[makeQuery(id+"F14.boolean.opBoolean","COPY",EDGE,{"derivedFrom":makeQuery(id+"F14.opExtrude","SWEPT_EDGE",EDGE,{"disambiguationData":[OSD([sQuery(id+"F13.wireOp",EDGE,"E10.60.0.1"),sQuery(id+"F13.wireOp",EDGE,"E10.61.0.0"),sQuery(id+"F13.wireOp",EDGE,"E10.61.0.1")])]})}),makeQuery(id+"F14.boolean.opBoolean","COPY",EDGE,{"derivedFrom":makeQuery(id+"F14.opExtrude","SWEPT_EDGE",EDGE,{"disambiguationData":[OSD([sQuery(id+"F13.wireOp",EDGE,"E10.61.0.2"),sQuery(id+"F13.wireOp",EDGE,"E10.62.0.1")])]})})],"blendedInto":[]});
            var Q32;
            Q32=makeQuery(id+"F20.opFillet","BLEND_EDGE",EDGE,{"blendedFrom":[makeQuery(id+"F14.boolean.opBoolean","COPY",EDGE,{"derivedFrom":makeQuery(id+"F14.opExtrude","SWEPT_EDGE",EDGE,{"disambiguationData":[OSD([sQuery(id+"F13.wireOp",EDGE,"E10.62.0.1"),sQuery(id+"F13.wireOp",EDGE,"E10.63.0.0"),sQuery(id+"F13.wireOp",EDGE,"E10.63.0.1")])]})}),makeQuery(id+"F14.boolean.opBoolean","COPY",EDGE,{"derivedFrom":makeQuery(id+"F14.opExtrude","SWEPT_EDGE",EDGE,{"disambiguationData":[OSD([sQuery(id+"F13.wireOp",EDGE,"E10.63.0.2"),sQuery(id+"F13.wireOp",EDGE,"E10.64.0.1")])]})})],"blendedInto":[]});
            var Q33;
            Q33=makeQuery(id+"F20.opFillet","BLEND_EDGE",EDGE,{"blendedFrom":[makeQuery(id+"F14.boolean.opBoolean","COPY",EDGE,{"derivedFrom":makeQuery(id+"F14.opExtrude","SWEPT_EDGE",EDGE,{"disambiguationData":[OSD([sQuery(id+"F13.wireOp",EDGE,"E10.64.0.1"),sQuery(id+"F13.wireOp",EDGE,"E10.65.0.0"),sQuery(id+"F13.wireOp",EDGE,"E10.65.0.1")])]})}),makeQuery(id+"F14.boolean.opBoolean","COPY",EDGE,{"derivedFrom":makeQuery(id+"F14.opExtrude","SWEPT_EDGE",EDGE,{"disambiguationData":[OSD([sQuery(id+"F13.wireOp",EDGE,"E10.65.0.2"),sQuery(id+"F13.wireOp",EDGE,"E10.66.0.1")])]})})],"blendedInto":[]});
            var Q34;
            Q34=makeQuery(id+"F20.opFillet","BLEND_EDGE",EDGE,{"blendedFrom":[makeQuery(id+"F14.boolean.opBoolean","COPY",EDGE,{"derivedFrom":makeQuery(id+"F14.opExtrude","SWEPT_EDGE",EDGE,{"disambiguationData":[OSD([sQuery(id+"F13.wireOp",EDGE,"E10.66.0.1"),sQuery(id+"F13.wireOp",EDGE,"E10.67.0.0"),sQuery(id+"F13.wireOp",EDGE,"E10.67.0.1")])]})}),makeQuery(id+"F14.boolean.opBoolean","COPY",EDGE,{"derivedFrom":makeQuery(id+"F14.opExtrude","SWEPT_EDGE",EDGE,{"disambiguationData":[OSD([sQuery(id+"F13.wireOp",EDGE,"E10.67.0.2"),sQuery(id+"F13.wireOp",EDGE,"E10.68.0.1")])]})})],"blendedInto":[]});
            var Q35;
            Q35=makeQuery(id+"F20.opFillet","BLEND_EDGE",EDGE,{"blendedFrom":[makeQuery(id+"F14.boolean.opBoolean","COPY",EDGE,{"derivedFrom":makeQuery(id+"F14.opExtrude","SWEPT_EDGE",EDGE,{"disambiguationData":[OSD([sQuery(id+"F13.wireOp",EDGE,"E10.68.0.1"),sQuery(id+"F13.wireOp",EDGE,"E10.69.0.0"),sQuery(id+"F13.wireOp",EDGE,"E10.69.0.1")])]})}),makeQuery(id+"F14.boolean.opBoolean","COPY",EDGE,{"derivedFrom":makeQuery(id+"F14.opExtrude","SWEPT_EDGE",EDGE,{"disambiguationData":[OSD([sQuery(id+"F13.wireOp",EDGE,"E10.69.0.2"),sQuery(id+"F13.wireOp",EDGE,"E10.70.0.1")])]})})],"blendedInto":[]});
            var Q36;
            Q36=makeQuery(id+"F20.opFillet","BLEND_EDGE",EDGE,{"blendedFrom":[makeQuery(id+"F14.boolean.opBoolean","COPY",EDGE,{"derivedFrom":makeQuery(id+"F14.opExtrude","SWEPT_EDGE",EDGE,{"disambiguationData":[OSD([sQuery(id+"F13.wireOp",EDGE,"E10.70.0.1"),sQuery(id+"F13.wireOp",EDGE,"E10.71.0.0"),sQuery(id+"F13.wireOp",EDGE,"E10.71.0.1")])]})}),makeQuery(id+"F14.boolean.opBoolean","COPY",EDGE,{"derivedFrom":makeQuery(id+"F14.opExtrude","SWEPT_EDGE",EDGE,{"disambiguationData":[OSD([sQuery(id+"F13.wireOp",EDGE,"E10.71.0.2"),sQuery(id+"F13.wireOp",EDGE,"E10.72.0.1")])]})})],"blendedInto":[]});
            var Q37;
            Q37=makeQuery(id+"F20.opFillet","BLEND_EDGE",EDGE,{"blendedFrom":[makeQuery(id+"F14.boolean.opBoolean","COPY",EDGE,{"derivedFrom":makeQuery(id+"F14.opExtrude","SWEPT_EDGE",EDGE,{"disambiguationData":[OSD([sQuery(id+"F13.wireOp",EDGE,"E10.72.0.1"),sQuery(id+"F13.wireOp",EDGE,"E10.73.0.0"),sQuery(id+"F13.wireOp",EDGE,"E10.73.0.1")])]})}),makeQuery(id+"F14.boolean.opBoolean","COPY",EDGE,{"derivedFrom":makeQuery(id+"F14.opExtrude","SWEPT_EDGE",EDGE,{"disambiguationData":[OSD([sQuery(id+"F13.wireOp",EDGE,"E10.73.0.2"),sQuery(id+"F13.wireOp",EDGE,"E10.74.0.1")])]})})],"blendedInto":[]});
            var Q38;
            Q38=makeQuery(id+"F20.opFillet","BLEND_EDGE",EDGE,{"blendedFrom":[makeQuery(id+"F14.boolean.opBoolean","COPY",EDGE,{"derivedFrom":makeQuery(id+"F14.opExtrude","SWEPT_EDGE",EDGE,{"disambiguationData":[OSD([sQuery(id+"F13.wireOp",EDGE,"E10.74.0.1"),sQuery(id+"F13.wireOp",EDGE,"E10.75.0.0"),sQuery(id+"F13.wireOp",EDGE,"E10.75.0.1")])]})}),makeQuery(id+"F14.boolean.opBoolean","COPY",EDGE,{"derivedFrom":makeQuery(id+"F14.opExtrude","SWEPT_EDGE",EDGE,{"disambiguationData":[OSD([sQuery(id+"F13.wireOp",EDGE,"E10.75.0.2"),sQuery(id+"F13.wireOp",EDGE,"E10.76.0.1")])]})})],"blendedInto":[]});
            var Q39;
            Q39=makeQuery(id+"F20.opFillet","BLEND_EDGE",EDGE,{"blendedFrom":[makeQuery(id+"F14.boolean.opBoolean","COPY",EDGE,{"derivedFrom":makeQuery(id+"F14.opExtrude","SWEPT_EDGE",EDGE,{"disambiguationData":[OSD([sQuery(id+"F13.wireOp",EDGE,"E10.76.0.1"),sQuery(id+"F13.wireOp",EDGE,"E10.77.0.0"),sQuery(id+"F13.wireOp",EDGE,"E10.77.0.1")])]})}),makeQuery(id+"F14.boolean.opBoolean","COPY",EDGE,{"derivedFrom":makeQuery(id+"F14.opExtrude","SWEPT_EDGE",EDGE,{"disambiguationData":[OSD([sQuery(id+"F13.wireOp",EDGE,"E10.77.0.2"),sQuery(id+"F13.wireOp",EDGE,"E10.78.0.1")])]})})],"blendedInto":[]});
            var Q40;
            Q40=makeQuery(id+"F20.opFillet","BLEND_EDGE",EDGE,{"blendedFrom":[makeQuery(id+"F14.boolean.opBoolean","COPY",EDGE,{"derivedFrom":makeQuery(id+"F14.opExtrude","SWEPT_EDGE",EDGE,{"disambiguationData":[OSD([sQuery(id+"F13.wireOp",EDGE,"E10.78.0.1"),sQuery(id+"F13.wireOp",EDGE,"E10.79.0.0"),sQuery(id+"F13.wireOp",EDGE,"E10.79.0.1")])]})}),makeQuery(id+"F14.boolean.opBoolean","COPY",EDGE,{"derivedFrom":makeQuery(id+"F14.opExtrude","SWEPT_EDGE",EDGE,{"disambiguationData":[OSD([sQuery(id+"F13.wireOp",EDGE,"E10.79.0.2"),sQuery(id+"F13.wireOp",EDGE,"E10.80.0.1")])]})})],"blendedInto":[]});
            var Q41;
            Q41=makeQuery(id+"F20.opFillet","BLEND_EDGE",EDGE,{"blendedFrom":[makeQuery(id+"F14.boolean.opBoolean","COPY",EDGE,{"derivedFrom":makeQuery(id+"F14.opExtrude","SWEPT_EDGE",EDGE,{"disambiguationData":[OSD([sQuery(id+"F13.wireOp",EDGE,"E10.80.0.1"),sQuery(id+"F13.wireOp",EDGE,"E10.81.0.0"),sQuery(id+"F13.wireOp",EDGE,"E10.81.0.1")])]})}),makeQuery(id+"F14.boolean.opBoolean","COPY",EDGE,{"derivedFrom":makeQuery(id+"F14.opExtrude","SWEPT_EDGE",EDGE,{"disambiguationData":[OSD([sQuery(id+"F13.wireOp",EDGE,"E10.81.0.2"),sQuery(id+"F13.wireOp",EDGE,"E10.82.0.1")])]})})],"blendedInto":[]});
            var Q42;
            Q42=makeQuery(id+"F20.opFillet","BLEND_EDGE",EDGE,{"blendedFrom":[makeQuery(id+"F14.boolean.opBoolean","COPY",EDGE,{"derivedFrom":makeQuery(id+"F14.opExtrude","SWEPT_EDGE",EDGE,{"disambiguationData":[OSD([sQuery(id+"F13.wireOp",EDGE,"E10.82.0.1"),sQuery(id+"F13.wireOp",EDGE,"E10.83.0.0"),sQuery(id+"F13.wireOp",EDGE,"E10.83.0.1")])]})}),makeQuery(id+"F14.boolean.opBoolean","COPY",EDGE,{"derivedFrom":makeQuery(id+"F14.opExtrude","SWEPT_EDGE",EDGE,{"disambiguationData":[OSD([sQuery(id+"F13.wireOp",EDGE,"E10.83.0.2"),sQuery(id+"F13.wireOp",EDGE,"E10.84.0.1")])]})})],"blendedInto":[]});
            var Q43;
            Q43=makeQuery(id+"F20.opFillet","BLEND_EDGE",EDGE,{"blendedFrom":[makeQuery(id+"F14.boolean.opBoolean","COPY",EDGE,{"derivedFrom":makeQuery(id+"F14.opExtrude","SWEPT_EDGE",EDGE,{"disambiguationData":[OSD([sQuery(id+"F13.wireOp",EDGE,"E10.84.0.1"),sQuery(id+"F13.wireOp",EDGE,"E10.85.0.0"),sQuery(id+"F13.wireOp",EDGE,"E10.85.0.1")])]})}),makeQuery(id+"F14.boolean.opBoolean","COPY",EDGE,{"derivedFrom":makeQuery(id+"F14.opExtrude","SWEPT_EDGE",EDGE,{"disambiguationData":[OSD([sQuery(id+"F13.wireOp",EDGE,"E10.85.0.2"),sQuery(id+"F13.wireOp",EDGE,"E10.86.0.1")])]})})],"blendedInto":[]});
            var Q44;
            Q44=makeQuery(id+"F20.opFillet","BLEND_EDGE",EDGE,{"blendedFrom":[makeQuery(id+"F14.boolean.opBoolean","COPY",EDGE,{"derivedFrom":makeQuery(id+"F14.opExtrude","SWEPT_EDGE",EDGE,{"disambiguationData":[OSD([sQuery(id+"F13.wireOp",EDGE,"E10.86.0.1"),sQuery(id+"F13.wireOp",EDGE,"E10.87.0.0"),sQuery(id+"F13.wireOp",EDGE,"E10.87.0.1")])]})}),makeQuery(id+"F14.boolean.opBoolean","COPY",EDGE,{"derivedFrom":makeQuery(id+"F14.opExtrude","SWEPT_EDGE",EDGE,{"disambiguationData":[OSD([sQuery(id+"F13.wireOp",EDGE,"E10.87.0.2"),sQuery(id+"F13.wireOp",EDGE,"E10.88.0.1")])]})})],"blendedInto":[]});
            var Q45;
            Q45=makeQuery(id+"F20.opFillet","BLEND_EDGE",EDGE,{"blendedFrom":[makeQuery(id+"F14.boolean.opBoolean","COPY",EDGE,{"derivedFrom":makeQuery(id+"F14.opExtrude","SWEPT_EDGE",EDGE,{"disambiguationData":[OSD([sQuery(id+"F13.wireOp",EDGE,"E10.88.0.1"),sQuery(id+"F13.wireOp",EDGE,"E10.89.0.0"),sQuery(id+"F13.wireOp",EDGE,"E10.89.0.1")])]})}),makeQuery(id+"F14.boolean.opBoolean","COPY",EDGE,{"derivedFrom":makeQuery(id+"F14.opExtrude","SWEPT_EDGE",EDGE,{"disambiguationData":[OSD([sQuery(id+"F13.wireOp",EDGE,"E10.89.0.2"),sQuery(id+"F13.wireOp",EDGE,"E10.90.0.1")])]})})],"blendedInto":[]});
            var Q46;
            Q46=makeQuery(id+"F20.opFillet","BLEND_EDGE",EDGE,{"blendedFrom":[makeQuery(id+"F14.boolean.opBoolean","COPY",EDGE,{"derivedFrom":makeQuery(id+"F14.opExtrude","SWEPT_EDGE",EDGE,{"disambiguationData":[OSD([sQuery(id+"F13.wireOp",EDGE,"E10.90.0.1"),sQuery(id+"F13.wireOp",EDGE,"E10.91.0.0"),sQuery(id+"F13.wireOp",EDGE,"E10.91.0.1")])]})}),makeQuery(id+"F14.boolean.opBoolean","COPY",EDGE,{"derivedFrom":makeQuery(id+"F14.opExtrude","SWEPT_EDGE",EDGE,{"disambiguationData":[OSD([sQuery(id+"F13.wireOp",EDGE,"E10.91.0.2"),sQuery(id+"F13.wireOp",EDGE,"E10.92.0.1")])]})})],"blendedInto":[]});
            var Q47;
            Q47=makeQuery(id+"F20.opFillet","BLEND_EDGE",EDGE,{"blendedFrom":[makeQuery(id+"F14.boolean.opBoolean","COPY",EDGE,{"derivedFrom":makeQuery(id+"F14.opExtrude","SWEPT_EDGE",EDGE,{"disambiguationData":[OSD([sQuery(id+"F13.wireOp",EDGE,"E10.92.0.1"),sQuery(id+"F13.wireOp",EDGE,"E10.93.0.0"),sQuery(id+"F13.wireOp",EDGE,"E10.93.0.1")])]})}),makeQuery(id+"F14.boolean.opBoolean","COPY",EDGE,{"derivedFrom":makeQuery(id+"F14.opExtrude","SWEPT_EDGE",EDGE,{"disambiguationData":[OSD([sQuery(id+"F13.wireOp",EDGE,"E10.93.0.2"),sQuery(id+"F13.wireOp",EDGE,"E10.94.0.1")])]})})],"blendedInto":[]});
            var Q48;
            Q48=makeQuery(id+"F20.opFillet","BLEND_EDGE",EDGE,{"blendedFrom":[makeQuery(id+"F14.boolean.opBoolean","COPY",EDGE,{"derivedFrom":makeQuery(id+"F14.opExtrude","SWEPT_EDGE",EDGE,{"disambiguationData":[OSD([sQuery(id+"F13.wireOp",EDGE,"E10.94.0.1"),sQuery(id+"F13.wireOp",EDGE,"E10.95.0.0"),sQuery(id+"F13.wireOp",EDGE,"E10.95.0.1")])]})}),makeQuery(id+"F14.boolean.opBoolean","COPY",EDGE,{"derivedFrom":makeQuery(id+"F14.opExtrude","SWEPT_EDGE",EDGE,{"disambiguationData":[OSD([sQuery(id+"F13.wireOp",EDGE,"E10.95.0.2"),sQuery(id+"F13.wireOp",EDGE,"E10.96.0.1")])]})})],"blendedInto":[]});
            var Q49;
            Q49=makeQuery(id+"F20.opFillet","BLEND_EDGE",EDGE,{"blendedFrom":[makeQuery(id+"F14.boolean.opBoolean","COPY",EDGE,{"derivedFrom":makeQuery(id+"F14.opExtrude","SWEPT_EDGE",EDGE,{"disambiguationData":[OSD([sQuery(id+"F13.wireOp",EDGE,"E10.96.0.1"),sQuery(id+"F13.wireOp",EDGE,"E10.97.0.0"),sQuery(id+"F13.wireOp",EDGE,"E10.97.0.1")])]})}),makeQuery(id+"F14.boolean.opBoolean","COPY",EDGE,{"derivedFrom":makeQuery(id+"F14.opExtrude","SWEPT_EDGE",EDGE,{"disambiguationData":[OSD([sQuery(id+"F13.wireOp",EDGE,"E10.97.0.2"),sQuery(id+"F13.wireOp",EDGE,"E10.98.0.1")])]})})],"blendedInto":[]});
            var Q50;
            Q50=makeQuery(id+"F20.opFillet","BLEND_EDGE",EDGE,{"blendedFrom":[makeQuery(id+"F14.boolean.opBoolean","COPY",EDGE,{"derivedFrom":makeQuery(id+"F14.opExtrude","SWEPT_EDGE",EDGE,{"disambiguationData":[OSD([sQuery(id+"F13.wireOp",EDGE,"E10.98.0.1"),sQuery(id+"F13.wireOp",EDGE,"E10.99.0.0"),sQuery(id+"F13.wireOp",EDGE,"E10.99.0.1")])]})}),makeQuery(id+"F16.boolean.opBoolean","COPY",EDGE,{"derivedFrom":makeQuery(id+"F16.opExtrude","SWEPT_EDGE",EDGE,{"disambiguationData":[OSD([sQuery(id+"F0.wireOp",EDGE,"E0.top"),sQuery(id+"F15.wireOp",EDGE,"E15.2.0.0")])]})})],"blendedInto":[]});
            var Q51;
            {var subQ0=sQuery(id+"F0.wireOp",EDGE,"E0.top");Q51=makeQuery(id+"F20.opFillet","BLEND_EDGE",EDGE,{"blendedFrom":[makeQuery(id+"F16.boolean.opBoolean","COPY",EDGE,{"derivedFrom":makeQuery(id+"F16.opExtrude","SWEPT_EDGE",EDGE,{"disambiguationData":[OSD([subQ0,sQuery(id+"F15.wireOp",EDGE,"E15.4.0.2")])]})}),makeQuery(id+"F16.boolean.opBoolean","COPY",EDGE,{"derivedFrom":makeQuery(id+"F16.opExtrude","SWEPT_EDGE",EDGE,{"disambiguationData":[OSD([subQ0,sQuery(id+"F15.wireOp",EDGE,"E15.6.0.0")])]})})],"blendedInto":[]});}
            var Q52;
            {var subQ0=sQuery(id+"F0.wireOp",EDGE,"E0.top");Q52=makeQuery(id+"F20.opFillet","BLEND_EDGE",EDGE,{"blendedFrom":[makeQuery(id+"F16.boolean.opBoolean","COPY",EDGE,{"derivedFrom":makeQuery(id+"F16.opExtrude","SWEPT_EDGE",EDGE,{"disambiguationData":[OSD([subQ0,sQuery(id+"F15.wireOp",EDGE,"E15.6.0.2")])]})}),makeQuery(id+"F16.boolean.opBoolean","COPY",EDGE,{"derivedFrom":makeQuery(id+"F16.opExtrude","SWEPT_EDGE",EDGE,{"disambiguationData":[OSD([subQ0,sQuery(id+"F15.wireOp",EDGE,"E15.8.0.0")])]})})],"blendedInto":[]});}
            var Q53;
            {var subQ0=sQuery(id+"F0.wireOp",EDGE,"E0.top");Q53=makeQuery(id+"F20.opFillet","BLEND_EDGE",EDGE,{"blendedFrom":[makeQuery(id+"F16.boolean.opBoolean","COPY",EDGE,{"derivedFrom":makeQuery(id+"F16.opExtrude","SWEPT_EDGE",EDGE,{"disambiguationData":[OSD([subQ0,sQuery(id+"F15.wireOp",EDGE,"E15.8.0.2")])]})}),makeQuery(id+"F16.boolean.opBoolean","COPY",EDGE,{"derivedFrom":makeQuery(id+"F16.opExtrude","SWEPT_EDGE",EDGE,{"disambiguationData":[OSD([subQ0,sQuery(id+"F15.wireOp",EDGE,"E15.10.0.0")])]})})],"blendedInto":[]});}
            var Q54;
            {var subQ0=sQuery(id+"F0.wireOp",EDGE,"E0.top");Q54=makeQuery(id+"F20.opFillet","BLEND_EDGE",EDGE,{"blendedFrom":[makeQuery(id+"F16.boolean.opBoolean","COPY",EDGE,{"derivedFrom":makeQuery(id+"F16.opExtrude","SWEPT_EDGE",EDGE,{"disambiguationData":[OSD([subQ0,sQuery(id+"F15.wireOp",EDGE,"E15.2.0.2")])]})}),makeQuery(id+"F16.boolean.opBoolean","COPY",EDGE,{"derivedFrom":makeQuery(id+"F16.opExtrude","SWEPT_EDGE",EDGE,{"disambiguationData":[OSD([subQ0,sQuery(id+"F15.wireOp",EDGE,"E15.4.0.0")])]})})],"blendedInto":[]});}
            var Q55;
            {var subQ0=sQuery(id+"F0.wireOp",EDGE,"E0.top");Q55=makeQuery(id+"F20.opFillet","BLEND_EDGE",EDGE,{"blendedFrom":[makeQuery(id+"F16.boolean.opBoolean","COPY",EDGE,{"derivedFrom":makeQuery(id+"F16.opExtrude","SWEPT_EDGE",EDGE,{"disambiguationData":[OSD([subQ0,sQuery(id+"F15.wireOp",EDGE,"E15.10.0.2")])]})}),makeQuery(id+"F16.boolean.opBoolean","COPY",EDGE,{"derivedFrom":makeQuery(id+"F16.opExtrude","SWEPT_EDGE",EDGE,{"disambiguationData":[OSD([subQ0,sQuery(id+"F15.wireOp",EDGE,"E15.12.0.0")])]})})],"blendedInto":[]});}
            var Q56;
            {var subQ0=sQuery(id+"F0.wireOp",EDGE,"E0.top");Q56=makeQuery(id+"F20.opFillet","BLEND_EDGE",EDGE,{"blendedFrom":[makeQuery(id+"F16.boolean.opBoolean","COPY",EDGE,{"derivedFrom":makeQuery(id+"F16.opExtrude","SWEPT_EDGE",EDGE,{"disambiguationData":[OSD([subQ0,sQuery(id+"F15.wireOp",EDGE,"E15.12.0.2")])]})}),makeQuery(id+"F16.boolean.opBoolean","COPY",EDGE,{"derivedFrom":makeQuery(id+"F16.opExtrude","SWEPT_EDGE",EDGE,{"disambiguationData":[OSD([subQ0,sQuery(id+"F15.wireOp",EDGE,"E15.14.0.0")])]})})],"blendedInto":[]});}
            var Q57;
            {var subQ0=sQuery(id+"F0.wireOp",EDGE,"E0.top");Q57=makeQuery(id+"F20.opFillet","BLEND_EDGE",EDGE,{"blendedFrom":[makeQuery(id+"F16.boolean.opBoolean","COPY",EDGE,{"derivedFrom":makeQuery(id+"F16.opExtrude","SWEPT_EDGE",EDGE,{"disambiguationData":[OSD([subQ0,sQuery(id+"F15.wireOp",EDGE,"E15.14.0.2")])]})}),makeQuery(id+"F16.boolean.opBoolean","COPY",EDGE,{"derivedFrom":makeQuery(id+"F16.opExtrude","SWEPT_EDGE",EDGE,{"disambiguationData":[OSD([subQ0,sQuery(id+"F15.wireOp",EDGE,"E15.16.0.0")])]})})],"blendedInto":[]});}
            var Q58;
            {var subQ0=sQuery(id+"F0.wireOp",EDGE,"E0.top");Q58=makeQuery(id+"F20.opFillet","BLEND_EDGE",EDGE,{"blendedFrom":[makeQuery(id+"F16.boolean.opBoolean","COPY",EDGE,{"derivedFrom":makeQuery(id+"F16.opExtrude","SWEPT_EDGE",EDGE,{"disambiguationData":[OSD([subQ0,sQuery(id+"F15.wireOp",EDGE,"E15.16.0.2")])]})}),makeQuery(id+"F16.boolean.opBoolean","COPY",EDGE,{"derivedFrom":makeQuery(id+"F16.opExtrude","SWEPT_EDGE",EDGE,{"disambiguationData":[OSD([subQ0,sQuery(id+"F15.wireOp",EDGE,"E15.18.0.0")])]})})],"blendedInto":[]});}
            var Q59;
            {var subQ0=sQuery(id+"F0.wireOp",EDGE,"E0.top");Q59=makeQuery(id+"F20.opFillet","BLEND_EDGE",EDGE,{"blendedFrom":[makeQuery(id+"F16.boolean.opBoolean","COPY",EDGE,{"derivedFrom":makeQuery(id+"F16.opExtrude","SWEPT_EDGE",EDGE,{"disambiguationData":[OSD([subQ0,sQuery(id+"F15.wireOp",EDGE,"E15.18.0.2")])]})}),makeQuery(id+"F16.boolean.opBoolean","COPY",EDGE,{"derivedFrom":makeQuery(id+"F16.opExtrude","SWEPT_EDGE",EDGE,{"disambiguationData":[OSD([subQ0,sQuery(id+"F15.wireOp",EDGE,"E15.20.0.0")])]})})],"blendedInto":[]});}
            var Q60;
            {var subQ0=sQuery(id+"F0.wireOp",EDGE,"E0.top");Q60=makeQuery(id+"F20.opFillet","BLEND_EDGE",EDGE,{"blendedFrom":[makeQuery(id+"F16.boolean.opBoolean","COPY",EDGE,{"derivedFrom":makeQuery(id+"F16.opExtrude","SWEPT_EDGE",EDGE,{"disambiguationData":[OSD([subQ0,sQuery(id+"F15.wireOp",EDGE,"E15.20.0.2")])]})}),makeQuery(id+"F16.boolean.opBoolean","COPY",EDGE,{"derivedFrom":makeQuery(id+"F16.opExtrude","SWEPT_EDGE",EDGE,{"disambiguationData":[OSD([subQ0,sQuery(id+"F15.wireOp",EDGE,"E15.22.0.0")])]})})],"blendedInto":[]});}
            var Q61;
            {var subQ0=sQuery(id+"F0.wireOp",EDGE,"E0.top");Q61=makeQuery(id+"F20.opFillet","BLEND_EDGE",EDGE,{"blendedFrom":[makeQuery(id+"F16.boolean.opBoolean","COPY",EDGE,{"derivedFrom":makeQuery(id+"F16.opExtrude","SWEPT_EDGE",EDGE,{"disambiguationData":[OSD([subQ0,sQuery(id+"F15.wireOp",EDGE,"E15.22.0.2")])]})}),makeQuery(id+"F16.boolean.opBoolean","COPY",EDGE,{"derivedFrom":makeQuery(id+"F16.opExtrude","SWEPT_EDGE",EDGE,{"disambiguationData":[OSD([subQ0,sQuery(id+"F15.wireOp",EDGE,"E15.24.0.0")])]})})],"blendedInto":[]});}
            var Q62;
            {var subQ0=sQuery(id+"F0.wireOp",EDGE,"E0.top");Q62=makeQuery(id+"F20.opFillet","BLEND_EDGE",EDGE,{"blendedFrom":[makeQuery(id+"F16.boolean.opBoolean","COPY",EDGE,{"derivedFrom":makeQuery(id+"F16.opExtrude","SWEPT_EDGE",EDGE,{"disambiguationData":[OSD([subQ0,sQuery(id+"F15.wireOp",EDGE,"E15.24.0.2")])]})}),makeQuery(id+"F16.boolean.opBoolean","COPY",EDGE,{"derivedFrom":makeQuery(id+"F16.opExtrude","SWEPT_EDGE",EDGE,{"disambiguationData":[OSD([subQ0,sQuery(id+"F15.wireOp",EDGE,"E15.26.0.0")])]})})],"blendedInto":[]});}
            var Q63;
            {var subQ0=sQuery(id+"F0.wireOp",EDGE,"E0.top");Q63=makeQuery(id+"F20.opFillet","BLEND_EDGE",EDGE,{"blendedFrom":[makeQuery(id+"F16.boolean.opBoolean","COPY",EDGE,{"derivedFrom":makeQuery(id+"F16.opExtrude","SWEPT_EDGE",EDGE,{"disambiguationData":[OSD([subQ0,sQuery(id+"F15.wireOp",EDGE,"E15.26.0.2")])]})}),makeQuery(id+"F16.boolean.opBoolean","COPY",EDGE,{"derivedFrom":makeQuery(id+"F16.opExtrude","SWEPT_EDGE",EDGE,{"disambiguationData":[OSD([subQ0,sQuery(id+"F15.wireOp",EDGE,"E15.28.0.0")])]})})],"blendedInto":[]});}
            var Q64;
            {var subQ0=sQuery(id+"F0.wireOp",EDGE,"E0.top");Q64=makeQuery(id+"F20.opFillet","BLEND_EDGE",EDGE,{"blendedFrom":[makeQuery(id+"F16.boolean.opBoolean","COPY",EDGE,{"derivedFrom":makeQuery(id+"F16.opExtrude","SWEPT_EDGE",EDGE,{"disambiguationData":[OSD([subQ0,sQuery(id+"F15.wireOp",EDGE,"E15.28.0.2")])]})}),makeQuery(id+"F16.boolean.opBoolean","COPY",EDGE,{"derivedFrom":makeQuery(id+"F16.opExtrude","SWEPT_EDGE",EDGE,{"disambiguationData":[OSD([subQ0,sQuery(id+"F15.wireOp",EDGE,"E15.30.0.0")])]})})],"blendedInto":[]});}
            var Q65;
            {var subQ0=sQuery(id+"F0.wireOp",EDGE,"E0.top");Q65=makeQuery(id+"F20.opFillet","BLEND_EDGE",EDGE,{"blendedFrom":[makeQuery(id+"F16.boolean.opBoolean","COPY",EDGE,{"derivedFrom":makeQuery(id+"F16.opExtrude","SWEPT_EDGE",EDGE,{"disambiguationData":[OSD([subQ0,sQuery(id+"F15.wireOp",EDGE,"E15.30.0.2")])]})}),makeQuery(id+"F16.boolean.opBoolean","COPY",EDGE,{"derivedFrom":makeQuery(id+"F16.opExtrude","SWEPT_EDGE",EDGE,{"disambiguationData":[OSD([subQ0,sQuery(id+"F15.wireOp",EDGE,"E15.32.0.0")])]})})],"blendedInto":[]});}
            var Q66;
            {var subQ0=sQuery(id+"F0.wireOp",EDGE,"E0.top");Q66=makeQuery(id+"F20.opFillet","BLEND_EDGE",EDGE,{"blendedFrom":[makeQuery(id+"F16.boolean.opBoolean","COPY",EDGE,{"derivedFrom":makeQuery(id+"F16.opExtrude","SWEPT_EDGE",EDGE,{"disambiguationData":[OSD([subQ0,sQuery(id+"F15.wireOp",EDGE,"E15.32.0.2")])]})}),makeQuery(id+"F16.boolean.opBoolean","COPY",EDGE,{"derivedFrom":makeQuery(id+"F16.opExtrude","SWEPT_EDGE",EDGE,{"disambiguationData":[OSD([subQ0,sQuery(id+"F15.wireOp",EDGE,"E15.34.0.0")])]})})],"blendedInto":[]});}
            var Q67;
            {var subQ0=sQuery(id+"F0.wireOp",EDGE,"E0.top");Q67=makeQuery(id+"F20.opFillet","BLEND_EDGE",EDGE,{"blendedFrom":[makeQuery(id+"F16.boolean.opBoolean","COPY",EDGE,{"derivedFrom":makeQuery(id+"F16.opExtrude","SWEPT_EDGE",EDGE,{"disambiguationData":[OSD([subQ0,sQuery(id+"F15.wireOp",EDGE,"E15.34.0.2")])]})}),makeQuery(id+"F16.boolean.opBoolean","COPY",EDGE,{"derivedFrom":makeQuery(id+"F16.opExtrude","SWEPT_EDGE",EDGE,{"disambiguationData":[OSD([subQ0,sQuery(id+"F15.wireOp",EDGE,"E15.36.0.0")])]})})],"blendedInto":[]});}
            var Q68;
            {var subQ0=sQuery(id+"F0.wireOp",EDGE,"E0.top");Q68=makeQuery(id+"F20.opFillet","BLEND_EDGE",EDGE,{"blendedFrom":[makeQuery(id+"F16.boolean.opBoolean","COPY",EDGE,{"derivedFrom":makeQuery(id+"F16.opExtrude","SWEPT_EDGE",EDGE,{"disambiguationData":[OSD([subQ0,sQuery(id+"F15.wireOp",EDGE,"E15.36.0.2")])]})}),makeQuery(id+"F16.boolean.opBoolean","COPY",EDGE,{"derivedFrom":makeQuery(id+"F16.opExtrude","SWEPT_EDGE",EDGE,{"disambiguationData":[OSD([subQ0,sQuery(id+"F15.wireOp",EDGE,"E15.38.0.0")])]})})],"blendedInto":[]});}
            var Q69;
            {var subQ0=sQuery(id+"F0.wireOp",EDGE,"E0.top");Q69=makeQuery(id+"F20.opFillet","BLEND_EDGE",EDGE,{"blendedFrom":[makeQuery(id+"F16.boolean.opBoolean","COPY",EDGE,{"derivedFrom":makeQuery(id+"F16.opExtrude","SWEPT_EDGE",EDGE,{"disambiguationData":[OSD([subQ0,sQuery(id+"F15.wireOp",EDGE,"E15.38.0.2")])]})}),makeQuery(id+"F16.boolean.opBoolean","COPY",EDGE,{"derivedFrom":makeQuery(id+"F16.opExtrude","SWEPT_EDGE",EDGE,{"disambiguationData":[OSD([subQ0,sQuery(id+"F15.wireOp",EDGE,"E15.40.0.0")])]})})],"blendedInto":[]});}
            var Q70;
            {var subQ0=sQuery(id+"F0.wireOp",EDGE,"E0.top");Q70=makeQuery(id+"F20.opFillet","BLEND_EDGE",EDGE,{"blendedFrom":[makeQuery(id+"F16.boolean.opBoolean","COPY",EDGE,{"derivedFrom":makeQuery(id+"F16.opExtrude","SWEPT_EDGE",EDGE,{"disambiguationData":[OSD([subQ0,sQuery(id+"F15.wireOp",EDGE,"E15.40.0.2")])]})}),makeQuery(id+"F16.boolean.opBoolean","COPY",EDGE,{"derivedFrom":makeQuery(id+"F16.opExtrude","SWEPT_EDGE",EDGE,{"disambiguationData":[OSD([subQ0,sQuery(id+"F15.wireOp",EDGE,"E15.42.0.0")])]})})],"blendedInto":[]});}
            var Q71;
            {var subQ0=sQuery(id+"F0.wireOp",EDGE,"E0.top");Q71=makeQuery(id+"F20.opFillet","BLEND_EDGE",EDGE,{"blendedFrom":[makeQuery(id+"F16.boolean.opBoolean","COPY",EDGE,{"derivedFrom":makeQuery(id+"F16.opExtrude","SWEPT_EDGE",EDGE,{"disambiguationData":[OSD([subQ0,sQuery(id+"F15.wireOp",EDGE,"E15.42.0.2")])]})}),makeQuery(id+"F16.boolean.opBoolean","COPY",EDGE,{"derivedFrom":makeQuery(id+"F16.opExtrude","SWEPT_EDGE",EDGE,{"disambiguationData":[OSD([subQ0,sQuery(id+"F15.wireOp",EDGE,"E15.44.0.0")])]})})],"blendedInto":[]});}
            var Q72;
            {var subQ0=sQuery(id+"F0.wireOp",EDGE,"E0.top");Q72=makeQuery(id+"F20.opFillet","BLEND_EDGE",EDGE,{"blendedFrom":[makeQuery(id+"F16.boolean.opBoolean","COPY",EDGE,{"derivedFrom":makeQuery(id+"F16.opExtrude","SWEPT_EDGE",EDGE,{"disambiguationData":[OSD([subQ0,sQuery(id+"F15.wireOp",EDGE,"E15.44.0.2")])]})}),makeQuery(id+"F16.boolean.opBoolean","COPY",EDGE,{"derivedFrom":makeQuery(id+"F16.opExtrude","SWEPT_EDGE",EDGE,{"disambiguationData":[OSD([subQ0,sQuery(id+"F15.wireOp",EDGE,"E15.46.0.0")])]})})],"blendedInto":[]});}
            var Q73;
            {var subQ0=sQuery(id+"F0.wireOp",EDGE,"E0.top");Q73=makeQuery(id+"F20.opFillet","BLEND_EDGE",EDGE,{"blendedFrom":[makeQuery(id+"F16.boolean.opBoolean","COPY",EDGE,{"derivedFrom":makeQuery(id+"F16.opExtrude","SWEPT_EDGE",EDGE,{"disambiguationData":[OSD([subQ0,sQuery(id+"F15.wireOp",EDGE,"E15.46.0.2")])]})}),makeQuery(id+"F16.boolean.opBoolean","COPY",EDGE,{"derivedFrom":makeQuery(id+"F16.opExtrude","SWEPT_EDGE",EDGE,{"disambiguationData":[OSD([subQ0,sQuery(id+"F15.wireOp",EDGE,"E15.48.0.0")])]})})],"blendedInto":[]});}
            var Q74;
            {var subQ0=sQuery(id+"F0.wireOp",EDGE,"E0.top");Q74=makeQuery(id+"F20.opFillet","BLEND_EDGE",EDGE,{"blendedFrom":[makeQuery(id+"F16.boolean.opBoolean","COPY",EDGE,{"derivedFrom":makeQuery(id+"F16.opExtrude","SWEPT_EDGE",EDGE,{"disambiguationData":[OSD([subQ0,sQuery(id+"F15.wireOp",EDGE,"E15.48.0.2")])]})}),makeQuery(id+"F16.boolean.opBoolean","COPY",EDGE,{"derivedFrom":makeQuery(id+"F16.opExtrude","SWEPT_EDGE",EDGE,{"disambiguationData":[OSD([subQ0,sQuery(id+"F15.wireOp",EDGE,"E15.50.0.0")])]})})],"blendedInto":[]});}
            var Q75;
            {var subQ0=sQuery(id+"F0.wireOp",EDGE,"E0.top");Q75=makeQuery(id+"F20.opFillet","BLEND_EDGE",EDGE,{"blendedFrom":[makeQuery(id+"F16.boolean.opBoolean","COPY",EDGE,{"derivedFrom":makeQuery(id+"F16.opExtrude","SWEPT_EDGE",EDGE,{"disambiguationData":[OSD([subQ0,sQuery(id+"F15.wireOp",EDGE,"E15.50.0.2")])]})}),makeQuery(id+"F16.boolean.opBoolean","COPY",EDGE,{"derivedFrom":makeQuery(id+"F16.opExtrude","SWEPT_EDGE",EDGE,{"disambiguationData":[OSD([subQ0,sQuery(id+"F15.wireOp",EDGE,"E15.52.0.0")])]})})],"blendedInto":[]});}
            var Q76;
            {var subQ0=sQuery(id+"F0.wireOp",EDGE,"E0.top");Q76=makeQuery(id+"F20.opFillet","BLEND_EDGE",EDGE,{"blendedFrom":[makeQuery(id+"F16.boolean.opBoolean","COPY",EDGE,{"derivedFrom":makeQuery(id+"F16.opExtrude","SWEPT_EDGE",EDGE,{"disambiguationData":[OSD([subQ0,sQuery(id+"F15.wireOp",EDGE,"E15.54.0.2")])]})}),makeQuery(id+"F16.boolean.opBoolean","COPY",EDGE,{"derivedFrom":makeQuery(id+"F16.opExtrude","SWEPT_EDGE",EDGE,{"disambiguationData":[OSD([subQ0,sQuery(id+"F15.wireOp",EDGE,"E15.56.0.0")])]})})],"blendedInto":[]});}
            var Q77;
            {var subQ0=sQuery(id+"F0.wireOp",EDGE,"E0.top");Q77=makeQuery(id+"F20.opFillet","BLEND_EDGE",EDGE,{"blendedFrom":[makeQuery(id+"F16.boolean.opBoolean","COPY",EDGE,{"derivedFrom":makeQuery(id+"F16.opExtrude","SWEPT_EDGE",EDGE,{"disambiguationData":[OSD([subQ0,sQuery(id+"F15.wireOp",EDGE,"E15.56.0.2")])]})}),makeQuery(id+"F16.boolean.opBoolean","COPY",EDGE,{"derivedFrom":makeQuery(id+"F16.opExtrude","SWEPT_EDGE",EDGE,{"disambiguationData":[OSD([subQ0,sQuery(id+"F15.wireOp",EDGE,"E15.58.0.0")])]})})],"blendedInto":[]});}
            var Q78;
            {var subQ0=sQuery(id+"F0.wireOp",EDGE,"E0.top");Q78=makeQuery(id+"F20.opFillet","BLEND_EDGE",EDGE,{"blendedFrom":[makeQuery(id+"F16.boolean.opBoolean","COPY",EDGE,{"derivedFrom":makeQuery(id+"F16.opExtrude","SWEPT_EDGE",EDGE,{"disambiguationData":[OSD([subQ0,sQuery(id+"F15.wireOp",EDGE,"E15.58.0.2")])]})}),makeQuery(id+"F16.boolean.opBoolean","COPY",EDGE,{"derivedFrom":makeQuery(id+"F16.opExtrude","SWEPT_EDGE",EDGE,{"disambiguationData":[OSD([subQ0,sQuery(id+"F15.wireOp",EDGE,"E15.60.0.0")])]})})],"blendedInto":[]});}
            var Q79;
            {var subQ0=sQuery(id+"F0.wireOp",EDGE,"E0.top");Q79=makeQuery(id+"F20.opFillet","BLEND_EDGE",EDGE,{"blendedFrom":[makeQuery(id+"F16.boolean.opBoolean","COPY",EDGE,{"derivedFrom":makeQuery(id+"F16.opExtrude","SWEPT_EDGE",EDGE,{"disambiguationData":[OSD([subQ0,sQuery(id+"F15.wireOp",EDGE,"E15.60.0.2")])]})}),makeQuery(id+"F16.boolean.opBoolean","COPY",EDGE,{"derivedFrom":makeQuery(id+"F16.opExtrude","SWEPT_EDGE",EDGE,{"disambiguationData":[OSD([subQ0,sQuery(id+"F15.wireOp",EDGE,"E15.62.0.0")])]})})],"blendedInto":[]});}
            var Q80;
            {var subQ0=sQuery(id+"F0.wireOp",EDGE,"E0.top");Q80=makeQuery(id+"F20.opFillet","BLEND_EDGE",EDGE,{"blendedFrom":[makeQuery(id+"F16.boolean.opBoolean","COPY",EDGE,{"derivedFrom":makeQuery(id+"F16.opExtrude","SWEPT_EDGE",EDGE,{"disambiguationData":[OSD([subQ0,sQuery(id+"F15.wireOp",EDGE,"E15.62.0.2")])]})}),makeQuery(id+"F16.boolean.opBoolean","COPY",EDGE,{"derivedFrom":makeQuery(id+"F16.opExtrude","SWEPT_EDGE",EDGE,{"disambiguationData":[OSD([subQ0,sQuery(id+"F15.wireOp",EDGE,"E15.64.0.0")])]})})],"blendedInto":[]});}
            var Q81;
            {var subQ0=sQuery(id+"F0.wireOp",EDGE,"E0.top");Q81=makeQuery(id+"F20.opFillet","BLEND_EDGE",EDGE,{"blendedFrom":[makeQuery(id+"F16.boolean.opBoolean","COPY",EDGE,{"derivedFrom":makeQuery(id+"F16.opExtrude","SWEPT_EDGE",EDGE,{"disambiguationData":[OSD([subQ0,sQuery(id+"F15.wireOp",EDGE,"E15.64.0.2")])]})}),makeQuery(id+"F16.boolean.opBoolean","COPY",EDGE,{"derivedFrom":makeQuery(id+"F16.opExtrude","SWEPT_EDGE",EDGE,{"disambiguationData":[OSD([subQ0,sQuery(id+"F15.wireOp",EDGE,"E15.66.0.0")])]})})],"blendedInto":[]});}
            var Q82;
            {var subQ0=sQuery(id+"F0.wireOp",EDGE,"E0.top");Q82=makeQuery(id+"F20.opFillet","BLEND_EDGE",EDGE,{"blendedFrom":[makeQuery(id+"F16.boolean.opBoolean","COPY",EDGE,{"derivedFrom":makeQuery(id+"F16.opExtrude","SWEPT_EDGE",EDGE,{"disambiguationData":[OSD([subQ0,sQuery(id+"F15.wireOp",EDGE,"E15.66.0.2")])]})}),makeQuery(id+"F16.boolean.opBoolean","COPY",EDGE,{"derivedFrom":makeQuery(id+"F16.opExtrude","SWEPT_EDGE",EDGE,{"disambiguationData":[OSD([subQ0,sQuery(id+"F15.wireOp",EDGE,"E15.68.0.0")])]})})],"blendedInto":[]});}
            var Q83;
            {var subQ0=sQuery(id+"F0.wireOp",EDGE,"E0.top");Q83=makeQuery(id+"F20.opFillet","BLEND_EDGE",EDGE,{"blendedFrom":[makeQuery(id+"F16.boolean.opBoolean","COPY",EDGE,{"derivedFrom":makeQuery(id+"F16.opExtrude","SWEPT_EDGE",EDGE,{"disambiguationData":[OSD([subQ0,sQuery(id+"F15.wireOp",EDGE,"E15.68.0.2")])]})}),makeQuery(id+"F16.boolean.opBoolean","COPY",EDGE,{"derivedFrom":makeQuery(id+"F16.opExtrude","SWEPT_EDGE",EDGE,{"disambiguationData":[OSD([subQ0,sQuery(id+"F15.wireOp",EDGE,"E15.70.0.0")])]})})],"blendedInto":[]});}
            var Q84;
            {var subQ0=sQuery(id+"F0.wireOp",EDGE,"E0.top");Q84=makeQuery(id+"F20.opFillet","BLEND_EDGE",EDGE,{"blendedFrom":[makeQuery(id+"F16.boolean.opBoolean","COPY",EDGE,{"derivedFrom":makeQuery(id+"F16.opExtrude","SWEPT_EDGE",EDGE,{"disambiguationData":[OSD([subQ0,sQuery(id+"F15.wireOp",EDGE,"E15.70.0.2")])]})}),makeQuery(id+"F16.boolean.opBoolean","COPY",EDGE,{"derivedFrom":makeQuery(id+"F16.opExtrude","SWEPT_EDGE",EDGE,{"disambiguationData":[OSD([subQ0,sQuery(id+"F15.wireOp",EDGE,"E15.72.0.0")])]})})],"blendedInto":[]});}
            var Q85;
            {var subQ0=sQuery(id+"F0.wireOp",EDGE,"E0.top");Q85=makeQuery(id+"F20.opFillet","BLEND_EDGE",EDGE,{"blendedFrom":[makeQuery(id+"F16.boolean.opBoolean","COPY",EDGE,{"derivedFrom":makeQuery(id+"F16.opExtrude","SWEPT_EDGE",EDGE,{"disambiguationData":[OSD([subQ0,sQuery(id+"F15.wireOp",EDGE,"E15.72.0.2")])]})}),makeQuery(id+"F16.boolean.opBoolean","COPY",EDGE,{"derivedFrom":makeQuery(id+"F16.opExtrude","SWEPT_EDGE",EDGE,{"disambiguationData":[OSD([subQ0,sQuery(id+"F15.wireOp",EDGE,"E15.74.0.0")])]})})],"blendedInto":[]});}
            var Q86;
            {var subQ0=sQuery(id+"F0.wireOp",EDGE,"E0.top");Q86=makeQuery(id+"F20.opFillet","BLEND_EDGE",EDGE,{"blendedFrom":[makeQuery(id+"F16.boolean.opBoolean","COPY",EDGE,{"derivedFrom":makeQuery(id+"F16.opExtrude","SWEPT_EDGE",EDGE,{"disambiguationData":[OSD([subQ0,sQuery(id+"F15.wireOp",EDGE,"E15.74.0.2")])]})}),makeQuery(id+"F16.boolean.opBoolean","COPY",EDGE,{"derivedFrom":makeQuery(id+"F16.opExtrude","SWEPT_EDGE",EDGE,{"disambiguationData":[OSD([subQ0,sQuery(id+"F15.wireOp",EDGE,"E15.76.0.0")])]})})],"blendedInto":[]});}
            var Q87;
            {var subQ0=sQuery(id+"F0.wireOp",EDGE,"E0.top");Q87=makeQuery(id+"F20.opFillet","BLEND_EDGE",EDGE,{"blendedFrom":[makeQuery(id+"F16.boolean.opBoolean","COPY",EDGE,{"derivedFrom":makeQuery(id+"F16.opExtrude","SWEPT_EDGE",EDGE,{"disambiguationData":[OSD([subQ0,sQuery(id+"F15.wireOp",EDGE,"E15.76.0.2")])]})}),makeQuery(id+"F16.boolean.opBoolean","COPY",EDGE,{"derivedFrom":makeQuery(id+"F16.opExtrude","SWEPT_EDGE",EDGE,{"disambiguationData":[OSD([subQ0,sQuery(id+"F15.wireOp",EDGE,"E15.78.0.0")])]})})],"blendedInto":[]});}
            var Q88;
            {var subQ0=sQuery(id+"F0.wireOp",EDGE,"E0.top");Q88=makeQuery(id+"F20.opFillet","BLEND_EDGE",EDGE,{"blendedFrom":[makeQuery(id+"F16.boolean.opBoolean","COPY",EDGE,{"derivedFrom":makeQuery(id+"F16.opExtrude","SWEPT_EDGE",EDGE,{"disambiguationData":[OSD([subQ0,sQuery(id+"F15.wireOp",EDGE,"E15.78.0.2")])]})}),makeQuery(id+"F16.boolean.opBoolean","COPY",EDGE,{"derivedFrom":makeQuery(id+"F16.opExtrude","SWEPT_EDGE",EDGE,{"disambiguationData":[OSD([subQ0,sQuery(id+"F15.wireOp",EDGE,"E15.80.0.0")])]})})],"blendedInto":[]});}
            var Q89;
            {var subQ0=sQuery(id+"F0.wireOp",EDGE,"E0.top");Q89=makeQuery(id+"F20.opFillet","BLEND_EDGE",EDGE,{"blendedFrom":[makeQuery(id+"F16.boolean.opBoolean","COPY",EDGE,{"derivedFrom":makeQuery(id+"F16.opExtrude","SWEPT_EDGE",EDGE,{"disambiguationData":[OSD([subQ0,sQuery(id+"F15.wireOp",EDGE,"E15.80.0.2")])]})}),makeQuery(id+"F16.boolean.opBoolean","COPY",EDGE,{"derivedFrom":makeQuery(id+"F16.opExtrude","SWEPT_EDGE",EDGE,{"disambiguationData":[OSD([subQ0,sQuery(id+"F15.wireOp",EDGE,"E15.82.0.0")])]})})],"blendedInto":[]});}
            var Q90;
            {var subQ0=sQuery(id+"F0.wireOp",EDGE,"E0.top");Q90=makeQuery(id+"F20.opFillet","BLEND_EDGE",EDGE,{"blendedFrom":[makeQuery(id+"F16.boolean.opBoolean","COPY",EDGE,{"derivedFrom":makeQuery(id+"F16.opExtrude","SWEPT_EDGE",EDGE,{"disambiguationData":[OSD([subQ0,sQuery(id+"F15.wireOp",EDGE,"E15.82.0.2")])]})}),makeQuery(id+"F16.boolean.opBoolean","COPY",EDGE,{"derivedFrom":makeQuery(id+"F16.opExtrude","SWEPT_EDGE",EDGE,{"disambiguationData":[OSD([subQ0,sQuery(id+"F15.wireOp",EDGE,"E15.84.0.0")])]})})],"blendedInto":[]});}
            var Q91;
            {var subQ0=sQuery(id+"F0.wireOp",EDGE,"E0.top");Q91=makeQuery(id+"F20.opFillet","BLEND_EDGE",EDGE,{"blendedFrom":[makeQuery(id+"F16.boolean.opBoolean","COPY",EDGE,{"derivedFrom":makeQuery(id+"F16.opExtrude","SWEPT_EDGE",EDGE,{"disambiguationData":[OSD([subQ0,sQuery(id+"F15.wireOp",EDGE,"E15.84.0.2")])]})}),makeQuery(id+"F16.boolean.opBoolean","COPY",EDGE,{"derivedFrom":makeQuery(id+"F16.opExtrude","SWEPT_EDGE",EDGE,{"disambiguationData":[OSD([subQ0,sQuery(id+"F15.wireOp",EDGE,"E15.86.0.0")])]})})],"blendedInto":[]});}
            var Q92;
            {var subQ0=sQuery(id+"F0.wireOp",EDGE,"E0.top");Q92=makeQuery(id+"F20.opFillet","BLEND_EDGE",EDGE,{"blendedFrom":[makeQuery(id+"F16.boolean.opBoolean","COPY",EDGE,{"derivedFrom":makeQuery(id+"F16.opExtrude","SWEPT_EDGE",EDGE,{"disambiguationData":[OSD([subQ0,sQuery(id+"F15.wireOp",EDGE,"E15.86.0.2")])]})}),makeQuery(id+"F16.boolean.opBoolean","COPY",EDGE,{"derivedFrom":makeQuery(id+"F16.opExtrude","SWEPT_EDGE",EDGE,{"disambiguationData":[OSD([subQ0,sQuery(id+"F15.wireOp",EDGE,"E15.88.0.0")])]})})],"blendedInto":[]});}
            var Q93;
            {var subQ0=sQuery(id+"F0.wireOp",EDGE,"E0.top");Q93=makeQuery(id+"F20.opFillet","BLEND_EDGE",EDGE,{"blendedFrom":[makeQuery(id+"F16.boolean.opBoolean","COPY",EDGE,{"derivedFrom":makeQuery(id+"F16.opExtrude","SWEPT_EDGE",EDGE,{"disambiguationData":[OSD([subQ0,sQuery(id+"F15.wireOp",EDGE,"E15.88.0.2")])]})}),makeQuery(id+"F16.boolean.opBoolean","COPY",EDGE,{"derivedFrom":makeQuery(id+"F16.opExtrude","SWEPT_EDGE",EDGE,{"disambiguationData":[OSD([subQ0,sQuery(id+"F15.wireOp",EDGE,"E15.90.0.0")])]})})],"blendedInto":[]});}
            var Q94;
            {var subQ0=sQuery(id+"F0.wireOp",EDGE,"E0.top");Q94=makeQuery(id+"F20.opFillet","BLEND_EDGE",EDGE,{"blendedFrom":[makeQuery(id+"F16.boolean.opBoolean","COPY",EDGE,{"derivedFrom":makeQuery(id+"F16.opExtrude","SWEPT_EDGE",EDGE,{"disambiguationData":[OSD([subQ0,sQuery(id+"F15.wireOp",EDGE,"E15.90.0.2")])]})}),makeQuery(id+"F16.boolean.opBoolean","COPY",EDGE,{"derivedFrom":makeQuery(id+"F16.opExtrude","SWEPT_EDGE",EDGE,{"disambiguationData":[OSD([subQ0,sQuery(id+"F15.wireOp",EDGE,"E15.92.0.0")])]})})],"blendedInto":[]});}
            var Q95;
            {var subQ0=sQuery(id+"F0.wireOp",EDGE,"E0.top");Q95=makeQuery(id+"F20.opFillet","BLEND_EDGE",EDGE,{"blendedFrom":[makeQuery(id+"F16.boolean.opBoolean","COPY",EDGE,{"derivedFrom":makeQuery(id+"F16.opExtrude","SWEPT_EDGE",EDGE,{"disambiguationData":[OSD([subQ0,sQuery(id+"F15.wireOp",EDGE,"E15.92.0.2")])]})}),makeQuery(id+"F16.boolean.opBoolean","COPY",EDGE,{"derivedFrom":makeQuery(id+"F16.opExtrude","SWEPT_EDGE",EDGE,{"disambiguationData":[OSD([subQ0,sQuery(id+"F15.wireOp",EDGE,"E15.94.0.0")])]})})],"blendedInto":[]});}
            var Q96;
            {var subQ0=sQuery(id+"F0.wireOp",EDGE,"E0.top");Q96=makeQuery(id+"F20.opFillet","BLEND_EDGE",EDGE,{"blendedFrom":[makeQuery(id+"F16.boolean.opBoolean","COPY",EDGE,{"derivedFrom":makeQuery(id+"F16.opExtrude","SWEPT_EDGE",EDGE,{"disambiguationData":[OSD([subQ0,sQuery(id+"F15.wireOp",EDGE,"E15.94.0.2")])]})}),makeQuery(id+"F16.boolean.opBoolean","COPY",EDGE,{"derivedFrom":makeQuery(id+"F16.opExtrude","SWEPT_EDGE",EDGE,{"disambiguationData":[OSD([subQ0,sQuery(id+"F15.wireOp",EDGE,"E15.96.0.0")])]})})],"blendedInto":[]});}
            var Q97;
            {var subQ0=sQuery(id+"F0.wireOp",EDGE,"E0.top");Q97=makeQuery(id+"F20.opFillet","BLEND_EDGE",EDGE,{"blendedFrom":[makeQuery(id+"F16.boolean.opBoolean","COPY",EDGE,{"derivedFrom":makeQuery(id+"F16.opExtrude","SWEPT_EDGE",EDGE,{"disambiguationData":[OSD([subQ0,sQuery(id+"F15.wireOp",EDGE,"E15.96.0.2")])]})}),makeQuery(id+"F16.boolean.opBoolean","COPY",EDGE,{"derivedFrom":makeQuery(id+"F16.opExtrude","SWEPT_EDGE",EDGE,{"disambiguationData":[OSD([subQ0,sQuery(id+"F15.wireOp",EDGE,"E15.98.0.0")])]})})],"blendedInto":[]});}
            var Q98;
            {var subQ0=sQuery(id+"F0.wireOp",EDGE,"E0.top");Q98=makeQuery(id+"F20.opFillet","BLEND_EDGE",EDGE,{"blendedFrom":[makeQuery(id+"F16.boolean.opBoolean","COPY",EDGE,{"derivedFrom":makeQuery(id+"F16.opExtrude","SWEPT_EDGE",EDGE,{"disambiguationData":[OSD([subQ0,sQuery(id+"F15.wireOp",EDGE,"E15.98.0.2")])]})}),makeQuery(id+"F18.boolean.opBoolean","COPY",EDGE,{"derivedFrom":makeQuery(id+"F18.opExtrude","SWEPT_EDGE",EDGE,{"disambiguationData":[OSD([subQ0,sQuery(id+"F17.wireOp",EDGE,"E19.2.0.0")])]})})],"blendedInto":[]});}
            fillet(context, id + "F21", {"entities" : qUnion([Q0, Q1, Q2, Q3, Q4, Q5, Q6, Q7, Q8, Q9, Q10, Q11, Q12, Q13, Q14, Q15, Q16, Q17, Q18, Q19, Q20, Q21, Q22, Q23, Q24, Q25, Q26, Q27, Q28, Q29, Q30, Q31, Q32, Q33, Q34, Q35, Q36, Q37, Q38, Q39, Q40, Q41, Q42, Q43, Q44, Q45, Q46, Q47, Q48, Q49, Q50, Q51, Q52, Q53, Q54, Q55, Q56, Q57, Q58, Q59, Q60, Q61, Q62, Q63, Q64, Q65, Q66, Q67, Q68, Q69, Q70, Q71, Q72, Q73, Q74, Q75, Q76, Q77, Q78, Q79, Q80, Q81, Q82, Q83, Q84, Q85, Q86, Q87, Q88, Q89, Q90, Q91, Q92, Q93, Q94, Q95, Q96, Q97, Q98]), "radius" : 0.5 * mm, "tangentPropagation" : true, "allowEdgeOverflow" : false});
        }
    });
